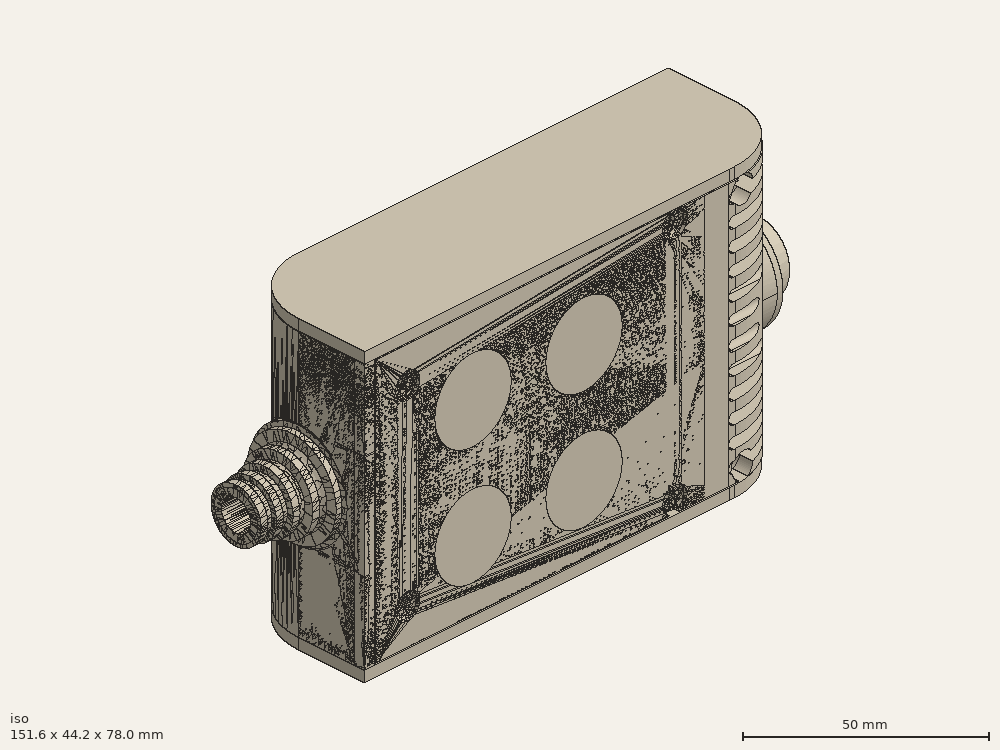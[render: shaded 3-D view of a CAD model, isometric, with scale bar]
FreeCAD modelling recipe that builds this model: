
FCSTD DOCUMENT  (FreeCAD 0.19R0.19.2)
Label: enclosure_191FCStd
License: All rights reserved
LicenseURL: http://en.wikipedia.org/wiki/All_rights_reserved
objects: Part::Revolution×152, Part::MultiFuse×146, Part::Feature×146, Sketcher::SketchObject×84, Part::Cut×70, Part::Cylinder×70, Part::Extrusion×67, Part::Fillet×58, Part::Box×36, App::MeasureDistance×4, PartDesign::Body×2, Image::ImagePlane×1
note: 831 computed .brp shape members not serialized (recipe doc carries the construction recipe); baked Part::Feature solids carry a one-line shape summary decoded from their .brp

FEATURE [Sketcher::SketchObject] Sketch  label="topSketch"
  FullyConstrained = true
  sketch-geometry (20):
    g0: LineSegment StartX=5.21097e-06 StartY=3 StartZ=0 EndX=5.21097e-06 EndY=19 EndZ=0
    g1: ArcOfCircle CenterX=19 CenterY=19 CenterZ=0 NormalX=0 NormalY=0 NormalZ=1 AngleXU=0 Radius=19 StartAngle=1.5708 EndAngle=3.14159
    g2: ArcOfCircle CenterX=19 CenterY=19 CenterZ=0 NormalX=0 NormalY=0 NormalZ=1 AngleXU=0 Radius=16 StartAngle=1.5708 EndAngle=3.14159
    g3: LineSegment StartX=114 StartY=35 StartZ=0 EndX=19 EndY=35 EndZ=0
    g4: LineSegment StartX=5.21097e-06 StartY=3 StartZ=0 EndX=5.21097e-06 EndY=0 EndZ=0
    g5: LineSegment StartX=3 StartY=0 StartZ=0 EndX=5.21097e-06 EndY=0 EndZ=0
    g6: LineSegment StartX=3 StartY=19 StartZ=0 EndX=3 EndY=0 EndZ=0
    g7: LineSegment StartX=19 StartY=38 StartZ=0 EndX=124 EndY=38 EndZ=0
    g8: Circle CenterX=119 CenterY=35 CenterZ=0 NormalX=0 NormalY=0 NormalZ=1 AngleXU=0 Radius=1
    g9: Circle CenterX=121 CenterY=35 CenterZ=0 NormalX=0 NormalY=0 NormalZ=1 AngleXU=0 Radius=1
    g10: Circle CenterX=121 CenterY=33 CenterZ=0 NormalX=0 NormalY=0 NormalZ=1 AngleXU=0 Radius=1
    g11: BSplineCurve PolesCount=3 KnotsCount=2 Degree=2 IsPeriodic=0
    g12: GeomPoint X=119 Y=35 Z=0
    g13: GeomPoint X=121 Y=33 Z=0
    g14: LineSegment StartX=119 StartY=35 StartZ=0 EndX=114 EndY=35 EndZ=0
    g15: ArcOfCircle CenterX=105 CenterY=19 CenterZ=0 NormalX=0 NormalY=0 NormalZ=1 AngleXU=0 Radius=19 StartAngle=5.7297 EndAngle=6.28319
    g16: ArcOfCircle CenterX=105 CenterY=19 CenterZ=0 NormalX=0 NormalY=0 NormalZ=1 AngleXU=0 Radius=16 StartAngle=5.60905 EndAngle=6.28319
    g17: LineSegment StartX=121 StartY=33 StartZ=0 EndX=121 EndY=19 EndZ=0
    g18: LineSegment StartX=124 StartY=38 StartZ=0 EndX=124 EndY=19 EndZ=0
    g19: LineSegment StartX=117.5 StartY=9.01251 StartZ=0 EndX=121.163 EndY=9.0125 EndZ=0
  constraints (46):
    c: Vertical(g0)
    c: Block(g0)
    c: Coincident(g1,g0)
    c: Block(g1)
    c: Coincident(g2,g1)
    c: Block(g2)
    c: Coincident(g3,g2)
    c: Horizontal(g3)
    c: Tangent(g3,g2)
    c: Coincident(g4,g0)
    c: Distance(g4) = 3
    c: Vertical(g4)
    c: Coincident(g5,g4)
    c: Horizontal(g5)
    c: Coincident(g6,g2)
    c: Coincident(g6,g5)
    c: Vertical(g6)
    c: Horizontal(g7)
    c: Distance(g7) = 105
    c: Coincident(g7,g1)
    c: Block(g3)
    c: Weight(g8) = 1
    c: Equal(g8,g9)
    c: Equal(g8,g10)
    c: InternalAlignment(g8,g11)
    c: InternalAlignment(g9,g11)
    c: InternalAlignment(g10,g11)
    c: InternalAlignment(g12,g11)
    c: InternalAlignment(g13,g11)
    c: Block(g11)
    c: Coincident(g14,g11)
    c: Coincident(g14,g3)
    c: Horizontal(g14)
    c: Block(g15)
    c: Coincident(g16,g15)
    c: Block(g16)
    c: Coincident(g17,g11)
    c: Coincident(g17,g16)
    c: Vertical(g17)
    c: Distance(g17) = 14
    c: Coincident(g18,g7)
    c: Coincident(g18,g15)
    c: Vertical(g18)
    c: Distance(g18) = 19
    c: Coincident(g19,g16)
    c: Coincident(g19,g15)
FEATURE [Sketcher::SketchObject] Sketch001  label="bottomSketch"
  FullyConstrained = true
  sketch-geometry (32):
    g0: LineSegment StartX=3.3 StartY=-6.03275e-07 StartZ=0 EndX=98 EndY=-6.03275e-07 EndZ=0
    g1: ArcOfCircle CenterX=98 CenterY=19 CenterZ=0 NormalX=0 NormalY=0 NormalZ=1 AngleXU=0 Radius=19 StartAngle=4.71239 EndAngle=5.71103
    g2: LineSegment StartX=6.3 StartY=8 StartZ=0 EndX=3.3 EndY=8 EndZ=0
    g3: LineSegment StartX=3.3 StartY=8 StartZ=0 EndX=3.3 EndY=-6.03275e-07 EndZ=0
    g4: ArcOfCircle CenterX=8.3 CenterY=5 CenterZ=0 NormalX=0 NormalY=0 NormalZ=1 AngleXU=0 Radius=2 StartAngle=3.14159 EndAngle=4.71239
    g5: LineSegment StartX=6.3 StartY=8 StartZ=0 EndX=6.3 EndY=5 EndZ=0
    g6: ArcOfCircle CenterX=98 CenterY=19 CenterZ=0 NormalX=0 NormalY=0 NormalZ=1 AngleXU=0 Radius=12.7 StartAngle=4.71239 EndAngle=6.28319
    g7: LineSegment StartX=94.7 StartY=3 StartZ=0 EndX=8.3 EndY=3 EndZ=0
    g8-g12: Circle x5 (B-spline internal-alignment scaffolding for g13; pole/knot coordinates omitted)
    g13: BSplineCurve PolesCount=5 KnotsCount=3 Degree=3 IsPeriodic=0
    g14: GeomPoint X=98 Y=6.3 Z=0
    g15: GeomPoint X=96.3938 Y=4.71946 Z=0
    g16: GeomPoint X=94.7 Y=3 Z=0
    g17-g23: Circle x7 (B-spline internal-alignment scaffolding for g24; pole/knot coordinates omitted)
    g24: BSplineCurve PolesCount=7 KnotsCount=5 Degree=3 IsPeriodic=0
    g25-g29: GeomPoint x5 (B-spline internal-alignment scaffolding for g24; pole/knot coordinates omitted)
    g30: ArcOfCircle CenterX=98 CenterY=19 CenterZ=0 NormalX=0 NormalY=0 NormalZ=1 AngleXU=0 Radius=15.7 StartAngle=5.81226 EndAngle=6.28319
    g31: LineSegment StartX=110.7 StartY=19 StartZ=0 EndX=113.7 EndY=19 EndZ=0
  constraints (41):
    c: Horizontal(g0)
    c: Coincident(g1,g0)
    c: Block(g1)
    c: Horizontal(g2)
    c: Distance(g2) = 3
    c: Coincident(g3,g2)
    c: Vertical(g3)
    c: Coincident(g3,g0)
    c: Block(g4)
    c: Block(g2)
    c: Coincident(g5,g2)
    c: Coincident(g5,g4)
    c: Vertical(g5)
    c: Coincident(g6,g1)
    c: Block(g6)
    c: Coincident(g7,g4)
    c: Horizontal(g7)
    c: Block(g0)
    c: Block(g7)
    c: Block(g3)
    c: Coincident(g13,g6)
    c: Weight(g8) = 1
    c: Equal(g8, g9-g12) x4
    c: Coincident(g13,g7)
    c: InternalAlignment(g8-g12 -> g13) x5
    c: InternalAlignment(g14,g13)
    c: InternalAlignment(g15,g13)
    c: InternalAlignment(g16,g13)
    c: Block(g13)
    c: Weight(g17) = 1
    c: Equal(g17, g18-g23) x6
    c: Coincident(g24,g1)
    c: InternalAlignment(g17-g23 -> g24) x7
    c: InternalAlignment(g25-g29 -> g24) x5
    c: Block(g24)
    c: Coincident(g30,g24)
    c: Coincident(g31,g6)
    c: Coincident(g31,g30)
    c: Horizontal(g31)
    c: Block(g31)
    c: Block(g30)
FEATURE [Part::Extrusion] Extrude  label="top"
  Base = -> Sketch
  Dir = (0,0,1)
  DirMode = 2
  FaceMakerClass = Part::FaceMakerBullseye
  LengthFwd = 72
  LengthRev = 0
  Solid = true
  Symmetric = false
FEATURE [Part::Extrusion] Extrude001  label="bottom"
  Base = -> Sketch001
  Dir = (0,0,1)
  DirMode = 2
  FaceMakerClass = Part::FaceMakerBullseye
  LengthFwd = 71.4
  LengthRev = 0
  Placement = pos=(0,0,0.3) rot=(0,0,1;0rad)
  Solid = true
  Symmetric = false
FEATURE [Sketcher::SketchObject] Sketch002  label="topSketch001"
  FullyConstrained = true
  sketch-geometry (8):
    g0: ArcOfCircle CenterX=19 CenterY=19.0975 CenterZ=0 NormalX=0 NormalY=0 NormalZ=1 AngleXU=0 Radius=18.9025 StartAngle=1.5708 EndAngle=3.14674
    g1: LineSegment StartX=0.0977805 StartY=19.0003 StartZ=0 EndX=0.0977805 EndY=0.000251602 EndZ=0
    g2: LineSegment StartX=19 StartY=38 StartZ=0 EndX=124 EndY=38 EndZ=0
    g3: LineSegment StartX=0.0977805 StartY=0.000251602 StartZ=0 EndX=105.098 EndY=0.000251602 EndZ=0
    g4: LineSegment StartX=124 StartY=38 StartZ=0 EndX=125.616 EndY=38 EndZ=0
    g5: LineSegment StartX=105.098 StartY=0.000251602 StartZ=0 EndX=106.713 EndY=0.000251602 EndZ=0
    g6: ArcOfCircle CenterX=106.616 CenterY=19 CenterZ=0 NormalX=0 NormalY=0 NormalZ=1 AngleXU=0 Radius=19 StartAngle=4.71754 EndAngle=6.28319
    g7: LineSegment StartX=125.616 StartY=38 StartZ=0 EndX=125.616 EndY=19 EndZ=0
  constraints (21):
    c: Block(g0)
    c: Coincident(g1,g0)
    c: Vertical(g1)
    c: Horizontal(g2)
    c: Distance(g2) = 105
    c: Coincident(g2,g0)
    c: Distance(g1) = 19
    c: Coincident(g3,g1)
    c: Horizontal(g3)
    c: Distance(g3) = 105
    c: Coincident(g4,g2)
    c: Horizontal(g4)
    c: Distance(g4) = 1.61553
    c: Horizontal(g5)
    c: Equal(g4,g5) = 1.61553
    c: Coincident(g5,g3)
    c: Block(g6)
    c: Coincident(g6,g5)
    c: Coincident(g7,g4)
    c: Coincident(g7,g6)
    c: Vertical(g7)
FEATURE [Part::Extrusion] Extrude002  label="sideA"
  Base = -> Sketch002
  Dir = (0,0,1)
  DirMode = 2
  FaceMakerClass = Part::FaceMakerBullseye
  LengthFwd = 3
  LengthRev = 0
  Placement = pos=(0,0,-3) rot=(0,0,1;0rad)
  Solid = true
  Symmetric = false
FEATURE [Sketcher::SketchObject] Sketch003  label="topSketch002"
  FullyConstrained = true
  sketch-geometry (6):
    g0: LineSegment StartX=19 StartY=38 StartZ=0 EndX=117 EndY=38 EndZ=0
    g1: ArcOfCircle CenterX=19 CenterY=19 CenterZ=0 NormalX=0 NormalY=0 NormalZ=1 AngleXU=0 Radius=19 StartAngle=1.5708 EndAngle=3.14159
    g2: LineSegment StartX=117 StartY=38 StartZ=0 EndX=117 EndY=19 EndZ=0
    g3: LineSegment StartX=98 StartY=1.0161e-12 StartZ=0 EndX=5.22862e-06 EndY=1.0161e-12 EndZ=0
    g4: LineSegment StartX=5.22862e-06 StartY=19 StartZ=0 EndX=5.22862e-06 EndY=1.0161e-12 EndZ=0
    g5: ArcOfCircle CenterX=98 CenterY=19 CenterZ=0 NormalX=0 NormalY=0 NormalZ=1 AngleXU=0 Radius=19 StartAngle=4.71239 EndAngle=6.28319
  constraints (16):
    c: Horizontal(g0)
    c: Distance(g0) = 98
    c: Coincident(g1,g0)
    c: Block(g1)
    c: Coincident(g2,g0)
    c: Vertical(g2)
    c: Distance(g2) = 19
    c: Horizontal(g3)
    c: Coincident(g4,g1)
    c: Vertical(g4)
    c: Coincident(g3,g4)
    c: Block(g3)
    c: Coincident(g5,g2)
    c: Coincident(g5,g3)
    c: Block(g0)
    c: Block(g5)
FEATURE [Sketcher::SketchObject] Sketch004
  FullyConstrained = true
  MapMode = 3
  Placement = pos=(0,0,0) rot=(1,0,0;1.5708rad)
  Support = -> [Extrude]
  sketch-geometry (8):
    g0: Circle CenterX=80.351 CenterY=-67.6202 CenterZ=0 NormalX=0 NormalY=0 NormalZ=1 AngleXU=0 Radius=2
    g1: Circle CenterX=80.351 CenterY=-67.6202 CenterZ=0 NormalX=0 NormalY=0 NormalZ=1 AngleXU=0 Radius=3
    g2: Circle CenterX=80.351 CenterY=-4.92017 CenterZ=0 NormalX=0 NormalY=0 NormalZ=1 AngleXU=0 Radius=2
    g3: Circle CenterX=80.351 CenterY=-4.92017 CenterZ=0 NormalX=0 NormalY=0 NormalZ=1 AngleXU=0 Radius=3
    g4: Circle CenterX=23.851 CenterY=-4.92017 CenterZ=0 NormalX=0 NormalY=0 NormalZ=1 AngleXU=0 Radius=2
    g5: Circle CenterX=23.851 CenterY=-4.92017 CenterZ=0 NormalX=0 NormalY=0 NormalZ=1 AngleXU=0 Radius=3
    g6: Circle CenterX=23.851 CenterY=-67.6202 CenterZ=0 NormalX=0 NormalY=0 NormalZ=1 AngleXU=0 Radius=2
    g7: Circle CenterX=23.851 CenterY=-67.6202 CenterZ=0 NormalX=0 NormalY=0 NormalZ=1 AngleXU=0 Radius=3
  constraints (8):
    c: Block(g3)
    c: Block(g2)
    c: Block(g1)
    c: Block(g0)
    c: Block(g6)
    c: Block(g7)
    c: Block(g4)
    c: Block(g5)
FEATURE [Part::Extrusion] Extrude004
  Base = -> Sketch004
  Dir = (0,-1,2e-16)
  DirMode = 2
  FaceMakerClass = Part::FaceMakerBullseye
  LengthFwd = 6
  LengthRev = 0
  Placement = pos=(0,9,0) rot=(0,0,1;0rad)
  Solid = true
  Symmetric = false
FEATURE [Sketcher::SketchObject] Sketch005
  FullyConstrained = true
  MapMode = 3
  Placement = pos=(0,0,0) rot=(1,0,0;1.5708rad)
  Support = -> [Extrude]
  sketch-geometry (8):
    g0: Circle CenterX=80.351 CenterY=-67.6202 CenterZ=0 NormalX=0 NormalY=0 NormalZ=1 AngleXU=0 Radius=3
    g1: Circle CenterX=80.351 CenterY=-4.92017 CenterZ=0 NormalX=0 NormalY=0 NormalZ=1 AngleXU=0 Radius=3
    g2: Circle CenterX=23.851 CenterY=-4.92017 CenterZ=0 NormalX=0 NormalY=0 NormalZ=1 AngleXU=0 Radius=3
    g3: Circle CenterX=23.851 CenterY=-67.6202 CenterZ=0 NormalX=0 NormalY=0 NormalZ=1 AngleXU=0 Radius=3
    g4: Circle CenterX=23.851 CenterY=-67.6202 CenterZ=0 NormalX=0 NormalY=0 NormalZ=1 AngleXU=0 Radius=5
    g5: Circle CenterX=80.351 CenterY=-67.6202 CenterZ=0 NormalX=0 NormalY=0 NormalZ=1 AngleXU=0 Radius=5
    g6: Circle CenterX=23.851 CenterY=-4.92017 CenterZ=0 NormalX=0 NormalY=0 NormalZ=1 AngleXU=0 Radius=5
    g7: Circle CenterX=80.351 CenterY=-4.92017 CenterZ=0 NormalX=0 NormalY=0 NormalZ=1 AngleXU=0 Radius=5
  constraints (8):
    c: Block(g1)
    c: Block(g0)
    c: Block(g3)
    c: Block(g2)
    c: Block(g5)
    c: Block(g4)
    c: Block(g6)
    c: Block(g7)
FEATURE [Part::Extrusion] Extrude005
  Base = -> Sketch005
  Dir = (0,-1,2e-16)
  DirMode = 2
  FaceMakerClass = Part::FaceMakerBullseye
  LengthFwd = 2
  LengthRev = 0
  Solid = true
  Symmetric = false
FEATURE [Sketcher::SketchObject] Sketch006
  FullyConstrained = true
  MapMode = 3
  Placement = pos=(0,0,0) rot=(1,0,0;1.5708rad)
  sketch-geometry (8):
    g0: Circle CenterX=80.351 CenterY=-67.6202 CenterZ=0 NormalX=0 NormalY=0 NormalZ=1 AngleXU=0 Radius=3
    g1: Circle CenterX=80.351 CenterY=-4.92017 CenterZ=0 NormalX=0 NormalY=0 NormalZ=1 AngleXU=0 Radius=3
    g2: Circle CenterX=23.851 CenterY=-4.92017 CenterZ=0 NormalX=0 NormalY=0 NormalZ=1 AngleXU=0 Radius=3
    g3: Circle CenterX=23.851 CenterY=-67.6202 CenterZ=0 NormalX=0 NormalY=0 NormalZ=1 AngleXU=0 Radius=3
    g4: Circle CenterX=23.851 CenterY=-67.6202 CenterZ=0 NormalX=0 NormalY=0 NormalZ=1 AngleXU=0 Radius=5
    g5: Circle CenterX=80.351 CenterY=-67.6202 CenterZ=0 NormalX=0 NormalY=0 NormalZ=1 AngleXU=0 Radius=5
    g6: Circle CenterX=23.851 CenterY=-4.92017 CenterZ=0 NormalX=0 NormalY=0 NormalZ=1 AngleXU=0 Radius=5
    g7: Circle CenterX=80.351 CenterY=-4.92017 CenterZ=0 NormalX=0 NormalY=0 NormalZ=1 AngleXU=0 Radius=5
  constraints (8):
    c: Block(g1)
    c: Block(g0)
    c: Block(g3)
    c: Block(g2)
    c: Block(g5)
    c: Block(g4)
    c: Block(g6)
    c: Block(g7)
FEATURE [Part::Extrusion] Extrude007
  Base = -> Sketch006
  Dir = (0,-1,2e-16)
  DirMode = 2
  FaceMakerClass = Part::FaceMakerBullseye
  LengthFwd = 2
  LengthRev = 0
  Solid = true
  Symmetric = false
FEATURE [Part::Fillet] Fillet
  Base = -> Extrude007
  Edges = 4 edges r=1.99: [Edge6,Edge12,Edge18,Edge24]
FEATURE [Part::Cut] Cut
  Base = -> Extrude005
  Placement = pos=(0,5,0) rot=(0,0,1;0rad)
  Tool = -> Fillet
FEATURE [Part::MultiFuse] Fusion  label="pCBScrews"
  Placement = pos=(-2.5,0,72.3) rot=(0,0,1;0rad)
  Shapes = -> [Extrude004,Cut]
FEATURE [App::MeasureDistance] Distance  label="Distance: 0.69 mm"
  Distance = 0.685967
  P1 = (24.0138,2.9647,0.3)
  P2 = (23.8901,3,-0.373787)
FEATURE [App::MeasureDistance] Distance001  label="Distance: 0.53 mm"
  Distance = 0.533607
  P1 = (80.2939,3,72.2334)
  P2 = (80.281,2.99661,71.7)
FEATURE [Part::Fillet] Fillet001
  Base = -> Extrude001
  Edges = 1 edges r=2.4: [Edge17]
FEATURE [Part::Fillet] Fillet002  label="bottom001"
  Base = -> Fillet001
  Edges = 1 edges r=2.4: [Edge36]
FEATURE [Part::Fillet] Fillet003  label="top001"
  Base = -> Extrude
  Edges = 1 edges r=2: [Edge1]
FEATURE [Sketcher::SketchObject] Sketch007
  FullyConstrained = true
  sketch-geometry (16):
    g0: LineSegment StartX=4 StartY=0 StartZ=0 EndX=4 EndY=2.4 EndZ=0
    g1: LineSegment StartX=4 StartY=2.4 StartZ=0 EndX=7 EndY=2.4 EndZ=0
    g2: LineSegment StartX=4 StartY=0 StartZ=0 EndX=5.7 EndY=0 EndZ=0
    g3: LineSegment StartX=5.7 StartY=0 StartZ=0 EndX=5.7 EndY=-5.6 EndZ=0
    g4-g8: Circle x5 (B-spline internal-alignment scaffolding for g9; pole/knot coordinates omitted)
    g9: BSplineCurve PolesCount=5 KnotsCount=3 Degree=3 IsPeriodic=0
    g10: GeomPoint X=7 Y=2.4 Z=0
    g11: GeomPoint X=10.4582 Y=-1.55472 Z=0
    g12: GeomPoint X=14 Y=-5.6 Z=0
    g13: LineSegment StartX=14 StartY=-5.6 StartZ=0 EndX=14 EndY=-14.1 EndZ=0
    g14: LineSegment StartX=14 StartY=-14.1 StartZ=0 EndX=6.5 EndY=-14.1 EndZ=0
    g15: LineSegment StartX=5.7 StartY=-5.6 StartZ=0 EndX=6.5 EndY=-14.1 EndZ=0
  constraints (28):
    c: Distance(g0) = 2.4
    c: Vertical(g0)
    c: Block(g0)
    c: Coincident(g1,g0)
    c: Horizontal(g1)
    c: Distance(g1) = 3
    c: Coincident(g2,g0)
    c: Horizontal(g2)
    c: Distance(g2) = 1.7
    c: Coincident(g3,g2)
    c: Vertical(g3)
    c: Distance(g3) = 5.6
    c: Coincident(g9,g1)
    c: Weight(g4) = 1
    c: Equal(g4, g5-g8) x4
    c: InternalAlignment(g4-g8 -> g9) x5
    c: InternalAlignment(g10,g9)
    c: InternalAlignment(g11,g9)
    c: InternalAlignment(g12,g9)
    c: Block(g9)
    c: Coincident(g13,g9)
    c: Vertical(g13)
    c: Distance(g13) = 8.5
    c: Coincident(g14,g13)
    c: Horizontal(g14)
    c: Distance(g14) = 7.5
    c: Coincident(g15,g3)
    c: Coincident(g15,g14)
FEATURE [Part::Feature] Face
  shape: bbox 10 x 16.5 x 2e-07 mm, 1 faces, 0 solids (baked)
FEATURE [Part::Revolution] Revolve  label="plugHousing"
  Angle = 360
  Axis = (0,1,0)
  Base = (0,0,0)
  FaceMakerClass = Part::FaceMakerBullseye
  Placement = pos=(0,0,36.15) rot=(0,0,1;0rad)
  Solid = false
  Source = -> Face
  Symmetric = false
FEATURE [Part::Feature] Face001
  shape: bbox 10 x 16.5 x 2e-07 mm, 1 faces, 0 solids (baked)
FEATURE [Part::Revolution] Revolve001  label="plugHousing001"
  Angle = 360
  Axis = (0,1,0)
  Base = (0,0,0)
  FaceMakerClass = Part::FaceMakerBullseye
  Placement = pos=(0,0,36.15) rot=(0,0,1;0rad)
  Solid = false
  Source = -> Face001
  Symmetric = false
FEATURE [Part::MultiFuse] Fusion001  label="plugHousing002"
  Placement = pos=(0,0,0) rot=(0,0,1;1.5708rad)
  Shapes = -> [Revolve001,Revolve]
FEATURE [Part::Feature] Face002
  shape: bbox 10 x 16.5 x 2e-07 mm, 1 faces, 0 solids (baked)
FEATURE [Part::Revolution] Revolve003  label="plugHousing005"
  Angle = 360
  Axis = (0,1,0)
  Base = (0,0,0)
  FaceMakerClass = Part::FaceMakerBullseye
  Placement = pos=(0,0,36.15) rot=(0,0,1;0rad)
  Solid = false
  Source = -> Face002
  Symmetric = false
FEATURE [Part::Feature] Face003
  shape: bbox 10 x 16.5 x 2e-07 mm, 1 faces, 0 solids (baked)
FEATURE [Part::Revolution] Revolve002  label="plugHousing003"
  Angle = 360
  Axis = (0,1,0)
  Base = (0,0,0)
  FaceMakerClass = Part::FaceMakerBullseye
  Placement = pos=(0,0,36.15) rot=(0,0,1;0rad)
  Solid = false
  Source = -> Face003
  Symmetric = false
FEATURE [Part::MultiFuse] Fusion002  label="plugHousing004"
  Placement = pos=(0,0,0) rot=(0,0,1;1.5708rad)
  Shapes = -> [Revolve002,Revolve003]
FEATURE [Part::MultiFuse] Fusion003  label="plugHousing006"
  Placement = pos=(0,19,0) rot=(0,0,1;3.14159rad)
  Shapes = -> [Fusion002,Fusion001]
FEATURE [Part::Feature] Face004
  shape: bbox 10 x 16.5 x 2e-07 mm, 1 faces, 0 solids (baked)
FEATURE [Part::Revolution] Revolve006  label="plugHousing010"
  Angle = 360
  Axis = (0,1,0)
  Base = (0,0,0)
  FaceMakerClass = Part::FaceMakerBullseye
  Placement = pos=(0,0,36.15) rot=(0,0,1;0rad)
  Solid = false
  Source = -> Face004
  Symmetric = false
FEATURE [Part::Feature] Face005
  shape: bbox 10 x 16.5 x 2e-07 mm, 1 faces, 0 solids (baked)
FEATURE [Part::Revolution] Revolve007  label="plugHousing011"
  Angle = 360
  Axis = (0,1,0)
  Base = (0,0,0)
  FaceMakerClass = Part::FaceMakerBullseye
  Placement = pos=(0,0,36.15) rot=(0,0,1;0rad)
  Solid = false
  Source = -> Face005
  Symmetric = false
FEATURE [Part::Feature] Face006
  shape: bbox 10 x 16.5 x 2e-07 mm, 1 faces, 0 solids (baked)
FEATURE [Part::Revolution] Revolve004  label="plugHousing007"
  Angle = 360
  Axis = (0,1,0)
  Base = (0,0,0)
  FaceMakerClass = Part::FaceMakerBullseye
  Placement = pos=(0,0,36.15) rot=(0,0,1;0rad)
  Solid = false
  Source = -> Face006
  Symmetric = false
FEATURE [Part::MultiFuse] Fusion004  label="plugHousing009"
  Placement = pos=(0,0,0) rot=(0,0,1;1.5708rad)
  Shapes = -> [Revolve004,Revolve007]
FEATURE [Part::Feature] Face007
  shape: bbox 10 x 16.5 x 2e-07 mm, 1 faces, 0 solids (baked)
FEATURE [Part::Revolution] Revolve005  label="plugHousing008"
  Angle = 360
  Axis = (0,1,0)
  Base = (0,0,0)
  FaceMakerClass = Part::FaceMakerBullseye
  Placement = pos=(0,0,36.15) rot=(0,0,1;0rad)
  Solid = false
  Source = -> Face007
  Symmetric = false
FEATURE [Part::MultiFuse] Fusion005  label="plugHousing012"
  Placement = pos=(0,0,0) rot=(0,0,1;1.5708rad)
  Shapes = -> [Revolve006,Revolve005]
FEATURE [Part::MultiFuse] Fusion006  label="plugHousing013"
  Placement = pos=(0,19,0) rot=(0,0,1;3.14159rad)
  Shapes = -> [Fusion005,Fusion004]
FEATURE [Part::MultiFuse] Fusion007  label="plugHousing014"
  Placement = pos=(122.621,0,-0.15) rot=(0,0,1;0rad)
  Shapes = -> [Fusion003,Fusion006]
FEATURE [Part::Cylinder] Cylinder002
  Angle = 360
  AttacherType = Attacher::AttachEngine3D
  Height = 20
  Placement = pos=(0,0,36.15) rot=(0,0,1;0rad)
  Radius = 4
FEATURE [Part::Cylinder] Cylinder003
  Angle = 360
  AttacherType = Attacher::AttachEngine3D
  Height = 10
  Placement = pos=(0,0,36.15) rot=(0,0,1;0rad)
  Radius = 4
FEATURE [Part::MultiFuse] Fusion009  label="removeToCreateHoleForPlugHousing"
  Placement = pos=(70,19,36.15) rot=(0,1,0;1.5708rad)
  Shapes = -> [Cylinder002,Cylinder003]
FEATURE [Part::Cylinder] Cylinder004
  Angle = 360
  AttacherType = Attacher::AttachEngine3D
  Height = 20
  Placement = pos=(0,0,36.15) rot=(0,0,1;0rad)
  Radius = 4
FEATURE [Part::Cylinder] Cylinder005
  Angle = 360
  AttacherType = Attacher::AttachEngine3D
  Height = 10
  Placement = pos=(0,0,36.15) rot=(0,0,1;0rad)
  Radius = 4
FEATURE [Part::MultiFuse] Fusion010  label="removeToCreateHoleForPlugHousing001"
  Placement = pos=(70,19,36.15) rot=(0,1,0;1.5708rad)
  Shapes = -> [Cylinder004,Cylinder005]
FEATURE [Part::Cut] Cut001
  Base = -> Fillet003
  Tool = -> Fusion010
FEATURE [Part::Cut] Cut002  label="Bottom"
  Base = -> Fillet002
  Tool = -> Fusion009
FEATURE [Part::Feature] Face008
  shape: bbox 10 x 16.5 x 2e-07 mm, 1 faces, 0 solids (baked)
FEATURE [Part::Revolution] Revolve011  label="plugHousing021"
  Angle = 360
  Axis = (0,1,0)
  Base = (0,0,0)
  FaceMakerClass = Part::FaceMakerBullseye
  Placement = pos=(0,0,36.15) rot=(0,0,1;0rad)
  Solid = false
  Source = -> Face008
  Symmetric = false
FEATURE [Part::Feature] Face009
  shape: bbox 10 x 16.5 x 2e-07 mm, 1 faces, 0 solids (baked)
FEATURE [Part::Revolution] Revolve012  label="plugHousing022"
  Angle = 360
  Axis = (0,1,0)
  Base = (0,0,0)
  FaceMakerClass = Part::FaceMakerBullseye
  Placement = pos=(0,0,36.15) rot=(0,0,1;0rad)
  Solid = false
  Source = -> Face009
  Symmetric = false
FEATURE [Part::Feature] Face010 .. Face013  x4 (patterned run collapsed; names and placements below)
  shape: bbox 10 x 16.5 x 2e-07 mm, 1 faces, 0 solids (baked)
FEATURE [Part::Revolution] Revolve015  label="plugHousing027"
  Angle = 360
  Axis = (0,1,0)
  Base = (0,0,0)
  FaceMakerClass = Part::FaceMakerBullseye
  Placement = pos=(0,0,36.15) rot=(0,0,1;0rad)
  Solid = false
  Source = -> Face013
  Symmetric = false
FEATURE [Part::Feature] Face014
  shape: bbox 10 x 16.5 x 2e-07 mm, 1 faces, 0 solids (baked)
FEATURE [Part::Feature] Face015
  shape: bbox 10 x 16.5 x 2e-07 mm, 1 faces, 0 solids (baked)
FEATURE [Part::Feature] Face016
  shape: bbox 10 x 16.5 x 2e-07 mm, 1 faces, 0 solids (baked)
FEATURE [Part::Revolution] Revolve019  label="plugHousing033"
  Angle = 360
  Axis = (0,1,0)
  Base = (0,0,0)
  FaceMakerClass = Part::FaceMakerBullseye
  Placement = pos=(0,0,36.15) rot=(0,0,1;0rad)
  Solid = false
  Source = -> Face016
  Symmetric = false
FEATURE [Part::Feature] Face017
  shape: bbox 10 x 16.5 x 2e-07 mm, 1 faces, 0 solids (baked)
FEATURE [Part::Revolution] Revolve020  label="plugHousing034"
  Angle = 360
  Axis = (0,1,0)
  Base = (0,0,0)
  FaceMakerClass = Part::FaceMakerBullseye
  Placement = pos=(0,0,36.15) rot=(0,0,1;0rad)
  Solid = false
  Source = -> Face017
  Symmetric = false
FEATURE [Part::Feature] Face018
  shape: bbox 10 x 16.5 x 2e-07 mm, 1 faces, 0 solids (baked)
FEATURE [Part::Revolution] Revolve016  label="plugHousing030"
  Angle = 360
  Axis = (0,1,0)
  Base = (0,0,0)
  FaceMakerClass = Part::FaceMakerBullseye
  Placement = pos=(0,0,36.15) rot=(0,0,1;0rad)
  Solid = false
  Source = -> Face018
  Symmetric = false
FEATURE [Part::MultiFuse] Fusion020  label="plugHousing038"
  Placement = pos=(0,0,0) rot=(0,0,1;1.5708rad)
  Shapes = -> [Revolve016,Revolve020]
FEATURE [Part::Feature] Face019
  shape: bbox 10 x 16.5 x 2e-07 mm, 1 faces, 0 solids (baked)
FEATURE [Part::Feature] Face020
  shape: bbox 10 x 16.5 x 2e-07 mm, 1 faces, 0 solids (baked)
FEATURE [Part::Revolution] Revolve017  label="plugHousing031"
  Angle = 360
  Axis = (0,1,0)
  Base = (0,0,0)
  FaceMakerClass = Part::FaceMakerBullseye
  Placement = pos=(0,0,36.15) rot=(0,0,1;0rad)
  Solid = false
  Source = -> Face020
  Symmetric = false
FEATURE [Part::MultiFuse] Fusion021  label="plugHousing039"
  Placement = pos=(0,0,0) rot=(0,0,1;1.5708rad)
  Shapes = -> [Revolve019,Revolve017]
FEATURE [Part::MultiFuse] Fusion023  label="plugHousing041"
  Placement = pos=(0,19,0) rot=(0,0,1;3.14159rad)
  Shapes = -> [Fusion021,Fusion020]
FEATURE [Part::Revolution] Revolve022  label="plugHousing043"
  Angle = 360
  Axis = (0,1,0)
  Base = (0,0,0)
  FaceMakerClass = Part::FaceMakerBullseye
  Placement = pos=(0,0,36.15) rot=(0,0,1;0rad)
  Solid = false
  Source = -> Face019
  Symmetric = false
FEATURE [Part::Feature] Face021
  shape: bbox 10 x 16.5 x 2e-07 mm, 1 faces, 0 solids (baked)
FEATURE [Part::Revolution] Revolve023  label="plugHousing044"
  Angle = 360
  Axis = (0,1,0)
  Base = (0,0,0)
  FaceMakerClass = Part::FaceMakerBullseye
  Placement = pos=(0,0,36.15) rot=(0,0,1;0rad)
  Solid = false
  Source = -> Face021
  Symmetric = false
FEATURE [Part::Feature] Face022
  shape: bbox 10 x 16.5 x 2e-07 mm, 1 faces, 0 solids (baked)
FEATURE [Part::Revolution] Revolve018  label="plugHousing032"
  Angle = 360
  Axis = (0,1,0)
  Base = (0,0,0)
  FaceMakerClass = Part::FaceMakerBullseye
  Placement = pos=(0,0,36.15) rot=(0,0,1;0rad)
  Solid = false
  Source = -> Face022
  Symmetric = false
FEATURE [Part::MultiFuse] Fusion022  label="plugHousing040"
  Placement = pos=(0,0,0) rot=(0,0,1;1.5708rad)
  Shapes = -> [Revolve018,Revolve023]
FEATURE [Part::Feature] Face023
  shape: bbox 10 x 16.5 x 2e-07 mm, 1 faces, 0 solids (baked)
FEATURE [Part::Revolution] Revolve021  label="plugHousing035"
  Angle = 360
  Axis = (0,1,0)
  Base = (0,0,0)
  FaceMakerClass = Part::FaceMakerBullseye
  Placement = pos=(0,0,36.15) rot=(0,0,1;0rad)
  Solid = false
  Source = -> Face023
  Symmetric = false
FEATURE [Part::MultiFuse] Fusion018  label="plugHousing036"
  Placement = pos=(0,0,0) rot=(0,0,1;1.5708rad)
  Shapes = -> [Revolve022,Revolve021]
FEATURE [Part::MultiFuse] Fusion019  label="plugHousing037"
  Placement = pos=(0,19,0) rot=(0,0,1;3.14159rad)
  Shapes = -> [Fusion018,Fusion022]
FEATURE [Part::MultiFuse] Fusion024  label="plugHousing042"
  Placement = pos=(122.621,0,-0.15) rot=(0,0,1;0rad)
  Shapes = -> [Fusion023,Fusion019]
FEATURE [Part::Cylinder] Cylinder006
  Angle = 360
  AttacherType = Attacher::AttachEngine3D
  Height = 20
  Placement = pos=(0,0,36.15) rot=(0,0,1;0rad)
  Radius = 14.3
FEATURE [Part::Cylinder] Cylinder007
  Angle = 360
  AttacherType = Attacher::AttachEngine3D
  Height = 10
  Placement = pos=(0,0,36.15) rot=(0,0,1;0rad)
  Radius = 4
FEATURE [Part::MultiFuse] Fusion026  label="removeToCreteHoleForPlugHousing"
  Placement = pos=(70,19,36) rot=(0,1,0;1.5708rad)
  Shapes = -> [Cylinder006,Cylinder007]
FEATURE [Part::Box] Box001  label="Cube001"
  AttacherType = Attacher::AttachEngine3D
  Height = 28
  Length = 3
  Placement = pos=(110.7,19,22) rot=(0,0,1;0rad)
  Width = 15.7
FEATURE [Part::Cut] Cut003  label="top002"
  Base = -> Cut001
  Tool = -> Fusion007
FEATURE [Part::Revolution] Revolve008  label="plugHousing015"
  Angle = 360
  Axis = (0,1,0)
  Base = (0,0,0)
  FaceMakerClass = Part::FaceMakerBullseye
  Placement = pos=(0,0,36.15) rot=(0,0,1;0rad)
  Solid = false
  Source = -> Face010
  Symmetric = false
FEATURE [Part::MultiFuse] Fusion013  label="plugHousing020"
  Placement = pos=(0,0,0) rot=(0,0,1;1.5708rad)
  Shapes = -> [Revolve008,Revolve012]
FEATURE [Part::Cut] Cut004  label="top003"
  Base = -> Cut003
  Placement = pos=(1,0,0) rot=(0,0,1;0rad)
  Tool = -> Fusion026
FEATURE [Part::Cylinder] Cylinder008
  Angle = 360
  AttacherType = Attacher::AttachEngine3D
  Height = 20
  Placement = pos=(0,0,36.15) rot=(0,0,1;0rad)
  Radius = 10.3
FEATURE [Part::Cylinder] Cylinder009
  Angle = 360
  AttacherType = Attacher::AttachEngine3D
  Height = 10
  Placement = pos=(0,0,36.15) rot=(0,0,1;0rad)
  Radius = 4
FEATURE [Part::MultiFuse] Fusion027  label="removeToCreteHoleForPlugHousing001"
  Placement = pos=(70,19,36) rot=(0,1,0;1.5708rad)
  Shapes = -> [Cylinder008,Cylinder009]
FEATURE [Part::Cut] Cut005  label="plugHousingTab"
  Base = -> Box001
  Tool = -> Fusion027
FEATURE [Part::MultiFuse] Fusion028  label="plugHousing045"
  Shapes = -> [Fusion024,Cut005]
FEATURE [Part::Box] Box002  label="Cube002"
  AttacherType = Attacher::AttachEngine3D
  Height = 28.8
  Length = 3
  Placement = pos=(107.3,28,21.6) rot=(0,0,1;0rad)
  Width = 7
FEATURE [Part::Box] Box003  label="Cube003"
  AttacherType = Attacher::AttachEngine3D
  Height = 3
  Length = 6.4
  Placement = pos=(107.3,28,18.6) rot=(0,0,1;0rad)
  Width = 7
FEATURE [Part::Box] Box004  label="Cube004"
  AttacherType = Attacher::AttachEngine3D
  Height = 3
  Length = 6.4
  Placement = pos=(107.3,28,50.4) rot=(0,0,1;0rad)
  Width = 7
FEATURE [Part::MultiFuse] Fusion029  label="plugHousingBracketHolder"
  Shapes = -> [Box004,Box002,Box003]
FEATURE [Part::Cylinder] Cylinder010
  Angle = 360
  AttacherType = Attacher::AttachEngine3D
  Height = 20
  Placement = pos=(0,0,36.15) rot=(0,0,1;0rad)
  Radius = 14.3
FEATURE [Part::Cylinder] Cylinder011
  Angle = 360
  AttacherType = Attacher::AttachEngine3D
  Height = 10
  Placement = pos=(0,0,36.15) rot=(0,0,1;0rad)
  Radius = 4
FEATURE [Part::MultiFuse] Fusion030  label="removeToCreteHoleForPlugHousing002"
  Placement = pos=(70,19,36) rot=(0,1,0;1.5708rad)
  Shapes = -> [Cylinder010,Cylinder011]
FEATURE [Part::Cut] Cut006  label="plugHousingBracketHolder001"
  Base = -> Fusion029
  Tool = -> Fusion030
FEATURE [Part::Cylinder] Cylinder012
  Angle = 360
  AttacherType = Attacher::AttachEngine3D
  Height = 20
  Placement = pos=(0,0,36.15) rot=(0,0,1;0rad)
  Radius = 7
FEATURE [Part::Cylinder] Cylinder013
  Angle = 360
  AttacherType = Attacher::AttachEngine3D
  Height = 10
  Placement = pos=(0,0,36.15) rot=(0,0,1;0rad)
  Radius = 4
FEATURE [Part::MultiFuse] Fusion032  label="removeToCreteHoleForPlugHousing003"
  Placement = pos=(70,19,36) rot=(0,1,0;1.5708rad)
  Shapes = -> [Cylinder012,Cylinder013]
FEATURE [Part::Cut] Cut007  label="bottom002"
  Base = -> Cut002
  Tool = -> Fusion032
FEATURE [Sketcher::SketchObject] Sketch008
  FullyConstrained = true
  sketch-geometry (54):
    g0: LineSegment StartX=-4.2 StartY=0 StartZ=0 EndX=-6.2 EndY=0 EndZ=0
    g1: LineSegment StartX=-14 StartY=-18 StartZ=0 EndX=-14 EndY=-26.5 EndZ=0
    g2: LineSegment StartX=-4.2 StartY=0 StartZ=0 EndX=-4.2 EndY=-13.4877 EndZ=0
    g3: Circle CenterX=-4.2 CenterY=-13.4877 CenterZ=0 NormalX=0 NormalY=0 NormalZ=1 AngleXU=0 Radius=1
    g4: Circle CenterX=-4.2 CenterY=-26.5 CenterZ=0 NormalX=0 NormalY=0 NormalZ=1 AngleXU=0 Radius=1
    g5: Circle CenterX=-8.2 CenterY=-26.5 CenterZ=0 NormalX=0 NormalY=0 NormalZ=1 AngleXU=0 Radius=1
    g6: BSplineCurve PolesCount=3 KnotsCount=2 Degree=2 IsPeriodic=0
    g7: GeomPoint X=-4.2 Y=-13.4877 Z=0
    g8: GeomPoint X=-8.2 Y=-26.5 Z=0
    g9: LineSegment StartX=-14 StartY=-26.5 StartZ=0 EndX=-8.2 EndY=-26.5 EndZ=0
    g10: LineSegment StartX=-10.15 StartY=-12 StartZ=0 EndX=-10.15 EndY=-14 EndZ=0
    g11: LineSegment StartX=-12.8401 StartY=-16 StartZ=0 EndX=-10.1571 EndY=-16 EndZ=0
    g12: LineSegment StartX=-10.15 StartY=-14 StartZ=0 EndX=-8.70761 EndY=-14 EndZ=0
    g13: LineSegment StartX=-12.8401 StartY=-16 StartZ=0 EndX=-12.8401 EndY=-17.6958 EndZ=0
    g14: LineSegment StartX=-10.15 StartY=-12 StartZ=0 EndX=-7.79258 EndY=-12 EndZ=0
    g15: Circle CenterX=-6.2215 CenterY=-2 CenterZ=0 NormalX=0 NormalY=0 NormalZ=1 AngleXU=0 Radius=1
    g16: Circle CenterX=-6.22762 CenterY=-2.58724 CenterZ=0 NormalX=0 NormalY=0 NormalZ=1 AngleXU=0 Radius=1
    g17: Circle CenterX=-6.32538 CenterY=-4 CenterZ=0 NormalX=0 NormalY=0 NormalZ=1 AngleXU=0 Radius=1
    g18: BSplineCurve PolesCount=3 KnotsCount=2 Degree=2 IsPeriodic=0
    g19: GeomPoint X=-6.2215 Y=-2 Z=0
    g20: GeomPoint X=-6.32538 Y=-4 Z=0
    g21: Circle CenterX=-6.48644 CenterY=-5.99526 CenterZ=0 NormalX=0 NormalY=0 NormalZ=1 AngleXU=0 Radius=1
    g22: Circle CenterX=-6.58486 CenterY=-6.99526 CenterZ=0 NormalX=0 NormalY=0 NormalZ=1 AngleXU=0 Radius=1
    g23: Circle CenterX=-6.77343 CenterY=-8 CenterZ=0 NormalX=0 NormalY=0 NormalZ=1 AngleXU=0 Radius=1
    g24: BSplineCurve PolesCount=3 KnotsCount=2 Degree=2 IsPeriodic=0
    g25: GeomPoint X=-6.48644 Y=-5.99526 Z=0
    g26: GeomPoint X=-6.77343 Y=-8 Z=0
    g27: Circle CenterX=-7.19003 CenterY=-10 CenterZ=0 NormalX=0 NormalY=0 NormalZ=1 AngleXU=0 Radius=1
    g28: Circle CenterX=-7.44407 CenterY=-11.0915 CenterZ=0 NormalX=0 NormalY=0 NormalZ=1 AngleXU=0 Radius=1
    g29: Circle CenterX=-7.79258 CenterY=-12 CenterZ=0 NormalX=0 NormalY=0 NormalZ=1 AngleXU=0 Radius=1
    g30: BSplineCurve PolesCount=3 KnotsCount=2 Degree=2 IsPeriodic=0
    g31: GeomPoint X=-7.19003 Y=-10 Z=0
    g32: GeomPoint X=-7.79258 Y=-12 Z=0
    g33: Circle CenterX=-8.70761 CenterY=-14 CenterZ=0 NormalX=0 NormalY=0 NormalZ=1 AngleXU=0 Radius=1
    g34: Circle CenterX=-9.33087 CenterY=-15.1837 CenterZ=0 NormalX=0 NormalY=0 NormalZ=1 AngleXU=0 Radius=1
    g35: Circle CenterX=-10.1571 CenterY=-16 CenterZ=0 NormalX=0 NormalY=0 NormalZ=1 AngleXU=0 Radius=1
    g36: BSplineCurve PolesCount=3 KnotsCount=2 Degree=2 IsPeriodic=0
    g37: GeomPoint X=-8.70761 Y=-14 Z=0
    g38: GeomPoint X=-10.1571 Y=-16 Z=0
    g39: Circle CenterX=-12.8401 CenterY=-17.6958 CenterZ=0 NormalX=0 NormalY=0 NormalZ=1 AngleXU=0 Radius=1
    g40: Circle CenterX=-13.3521 CenterY=-17.9027 CenterZ=0 NormalX=0 NormalY=0 NormalZ=1 AngleXU=0 Radius=1
    g41: Circle CenterX=-14 CenterY=-18 CenterZ=0 NormalX=0 NormalY=0 NormalZ=1 AngleXU=0 Radius=1
    g42: BSplineCurve PolesCount=3 KnotsCount=2 Degree=2 IsPeriodic=0
    g43: GeomPoint X=-12.8401 Y=-17.6958 Z=0
    g44: GeomPoint X=-14 Y=-18 Z=0
    g45: LineSegment StartX=-6.2 StartY=0 StartZ=0 EndX=-7.2 EndY=0 EndZ=0
    g46: LineSegment StartX=-7.2 StartY=0 StartZ=0 EndX=-7.2 EndY=-2 EndZ=0
    g47: LineSegment StartX=-7.2 StartY=-2 StartZ=0 EndX=-6.2215 EndY=-2 EndZ=0
    g48: LineSegment StartX=-6.32538 StartY=-4 StartZ=0 EndX=-7.65538 EndY=-4 EndZ=0
    g49: LineSegment StartX=-7.65538 StartY=-4 StartZ=0 EndX=-7.65538 EndY=-5.99526 EndZ=0
    g50: LineSegment StartX=-7.65538 StartY=-5.99526 StartZ=0 EndX=-6.48644 EndY=-5.99526 EndZ=0
    g51: LineSegment StartX=-6.77343 StartY=-8 StartZ=0 EndX=-8.43343 EndY=-8 EndZ=0
    g52: LineSegment StartX=-8.43343 StartY=-8 StartZ=0 EndX=-8.43343 EndY=-10 EndZ=0
    g53: LineSegment StartX=-8.43343 StartY=-10 StartZ=0 EndX=-7.19003 EndY=-10 EndZ=0
  constraints (112):
    c: Horizontal(g0)
    c: Distance(g0) = 2
    c: Block(g0)
    c: Vertical(g1)
    c: Coincident(g2,g0)
    c: Vertical(g2)
    c: Block(g2)
    c: Coincident(g6,g2)
    c: Weight(g3) = 1
    c: Equal(g3,g4)
    c: Equal(g3,g5)
    c: InternalAlignment(g3,g6)
    c: InternalAlignment(g4,g6)
    c: InternalAlignment(g5,g6)
    c: InternalAlignment(g7,g6)
    c: InternalAlignment(g8,g6)
    c: Block(g6)
    c: Coincident(g9,g1)
    c: Coincident(g9,g6)
    c: Horizontal(g9)
    c: Vertical(g10)
    c: Block(g10)
    c: Horizontal(g11)
    c: Block(g11)
    c: Coincident(g12,g10)
    c: Horizontal(g12)
    c: Block(g12)
    c: Coincident(g13,g11)
    c: Vertical(g13)
    c: Block(g13)
    c: Coincident(g14,g10)
    c: Horizontal(g14)
    c: Block(g14)
    c: Block(g9)
    c: Block(g1)
    c: Weight(g15) = 1
    c: Equal(g15,g16)
    c: Equal(g15,g17)
    c: InternalAlignment(g15,g18)
    c: InternalAlignment(g16,g18)
    c: InternalAlignment(g17,g18)
    c: InternalAlignment(g19,g18)
    c: InternalAlignment(g20,g18)
    c: Weight(g21) = 1
    c: Equal(g21,g22)
    c: Equal(g21,g23)
    c: InternalAlignment(g21,g24)
    c: InternalAlignment(g22,g24)
    c: InternalAlignment(g23,g24)
    c: InternalAlignment(g25,g24)
    c: InternalAlignment(g26,g24)
    c: Weight(g27) = 1
    c: Equal(g27,g28)
    c: Equal(g27,g29)
    c: Coincident(g30,g14)
    c: InternalAlignment(g27,g30)
    c: InternalAlignment(g28,g30)
    c: InternalAlignment(g29,g30)
    c: InternalAlignment(g31,g30)
    c: InternalAlignment(g32,g30)
    c: Coincident(g36,g12)
    c: Weight(g33) = 1
    c: Equal(g33,g34)
    c: Equal(g33,g35)
    c: Coincident(g36,g11)
    c: InternalAlignment(g33,g36)
    c: InternalAlignment(g34,g36)
    c: InternalAlignment(g35,g36)
    c: InternalAlignment(g37,g36)
    c: InternalAlignment(g38,g36)
    c: Coincident(g42,g13)
    c: Weight(g39) = 1
    c: Equal(g39,g40)
    c: Equal(g39,g41)
    c: Coincident(g42,g1)
    c: InternalAlignment(g39,g42)
    c: InternalAlignment(g40,g42)
    c: InternalAlignment(g41,g42)
    c: InternalAlignment(g43,g42)
    c: InternalAlignment(g44,g42)
    c: Block(g18)
    c: Block(g24)
    c: Block(g30)
    c: Block(g36)
    c: Block(g42)
    c: Horizontal(g45)
    c: Coincident(g45,g0)
    c: Vertical(g46)
    c: Coincident(g46,g45)
    c: Coincident(g47,g46)
    c: Coincident(g47,g18)
    c: Horizontal(g47)
    c: Block(g46)
    c: Coincident(g48,g18)
    c: Horizontal(g48)
    c: Distance(g48) = 1.33
    c: Vertical(g49)
    c: Coincident(g49,g48)
    c: Coincident(g50,g49)
    c: Coincident(g50,g24)
    c: Horizontal(g50)
    c: Tangent(g50,g22)
    c: Horizontal(g51)
    c: Coincident(g51,g24)
    c: Block(g51)
    c: Vertical(g52)
    c: Block(g52)
    c: Coincident(g52,g51)
    c: Coincident(g53,g52)
    c: Coincident(g53,g30)
    c: Horizontal(g53)
    c: Distance(g1) = 8.5
FEATURE [Part::Feature] Face024
  shape: bbox 9.8 x 26.5 x 2e-07 mm, 1 faces, 0 solids (baked)
FEATURE [Part::Revolution] Revolve024
  Angle = 360
  Axis = (0,1,0)
  Base = (0,0,0)
  FaceMakerClass = Part::FaceMakerBullseye
  Placement = pos=(0,0,0) rot=(0,0,1;1.5708rad)
  Solid = false
  Source = -> Face024
  Symmetric = false
FEATURE [Part::Feature] Face025
  shape: bbox 9.8 x 26.5 x 2e-07 mm, 1 faces, 0 solids (baked)
FEATURE [Part::Revolution] Revolve025
  Angle = 360
  Axis = (0,1,0)
  Base = (0,0,0)
  FaceMakerClass = Part::FaceMakerBullseye
  Placement = pos=(0,0,0) rot=(0,0,1;1.5708rad)
  Solid = false
  Source = -> Face025
  Symmetric = false
FEATURE [Part::MultiFuse] Fusion033
  Placement = pos=(-18,19,36) rot=(0,0,1;0rad)
  Shapes = -> [Revolve025,Revolve024]
FEATURE [Part::Cylinder] Cylinder014
  Angle = 360
  AttacherType = Attacher::AttachEngine3D
  Height = 20
  Placement = pos=(0,0,36.15) rot=(0,0,1;0rad)
  Radius = 14.3
FEATURE [Part::Cylinder] Cylinder015
  Angle = 360
  AttacherType = Attacher::AttachEngine3D
  Height = 10
  Placement = pos=(0,0,36.15) rot=(0,0,1;0rad)
  Radius = 4
FEATURE [Part::MultiFuse] Fusion034  label="removeToCreteHoleForPlugHousing004"
  Placement = pos=(-42,19,36) rot=(0,1,0;1.5708rad)
  Shapes = -> [Cylinder014,Cylinder015]
FEATURE [Part::Cut] Cut008  label="top004"
  Base = -> Cut004
  Placement = pos=(-1,0,0) rot=(0,0,1;0rad)
  Tool = -> Fusion034
FEATURE [Part::Box] Box005  label="Cube005"
  AttacherType = Attacher::AttachEngine3D
  Height = 28
  Length = 3
  Placement = pos=(110.7,19,22) rot=(0,0,1;0rad)
  Width = 15.7
FEATURE [Part::Cylinder] Cylinder016
  Angle = 360
  AttacherType = Attacher::AttachEngine3D
  Height = 10
  Placement = pos=(0,0,36.15) rot=(0,0,1;0rad)
  Radius = 4
FEATURE [Part::Cylinder] Cylinder017
  Angle = 360
  AttacherType = Attacher::AttachEngine3D
  Height = 20
  Placement = pos=(0,0,36.15) rot=(0,0,1;0rad)
  Radius = 10.3
FEATURE [Part::MultiFuse] Fusion035  label="removeToCreteHoleForPlugHousing005"
  Placement = pos=(70,19,36) rot=(0,1,0;1.5708rad)
  Shapes = -> [Cylinder017,Cylinder016]
FEATURE [Part::Cut] Cut009  label="plugHousingTab001"
  Base = -> Box005
  Placement = pos=(-107.4,-14,0) rot=(0,0,1;0rad)
  Tool = -> Fusion035
FEATURE [Part::Box] Box006  label="Cube006"
  AttacherType = Attacher::AttachEngine3D
  Height = 28
  Length = 3
  Placement = pos=(110.7,19,22) rot=(0,0,1;0rad)
  Width = 15.7
FEATURE [Part::Cylinder] Cylinder018
  Angle = 360
  AttacherType = Attacher::AttachEngine3D
  Height = 10
  Placement = pos=(0,0,36.15) rot=(0,0,1;0rad)
  Radius = 4
FEATURE [Part::Cylinder] Cylinder019
  Angle = 360
  AttacherType = Attacher::AttachEngine3D
  Height = 20
  Placement = pos=(0,0,36.15) rot=(0,0,1;0rad)
  Radius = 10.3
FEATURE [Part::MultiFuse] Fusion036  label="removeToCreteHoleForPlugHousing006"
  Placement = pos=(70,19,36) rot=(0,1,0;1.5708rad)
  Shapes = -> [Cylinder019,Cylinder018]
FEATURE [Part::Cut] Cut010  label="plugHousingTab002"
  Base = -> Box006
  Placement = pos=(-107.4,-14,0) rot=(0,0,1;0rad)
  Tool = -> Fusion036
FEATURE [Part::MultiFuse] Fusion037
  Placement = pos=(9.6,23,0) rot=(0,0,1;3.14159rad)
  Shapes = -> [Cut009,Cut010]
FEATURE [Part::Box] Box  label="Cube"
  AttacherType = Attacher::AttachEngine3D
  Height = 10
  Length = 3
  Placement = pos=(3.3,4,12) rot=(0,0,1;0rad)
  Width = 10
FEATURE [Part::Fillet] Fillet004
  Base = -> Fusion028
  Edges = 1 edges r=2: [Edge25]
FEATURE [Part::Fillet] Fillet005  label="plugHousing046"
  Base = -> Fillet004
  Edges = 1 edges r=2: [Edge8]
FEATURE [Part::Fillet] Fillet006
  Base = -> Box
  Edges = 1 edges r=2: [Edge11]
FEATURE [Part::Box] Box007  label="Cube007"
  AttacherType = Attacher::AttachEngine3D
  Height = 10
  Length = 3
  Placement = pos=(3.3,4,50) rot=(0,0,1;0rad)
  Width = 10
FEATURE [Part::Fillet] Fillet007
  Base = -> Box007
  Edges = 1 edges r=2: [Edge12]
FEATURE [Part::Box] Box008  label="Cube008"
  AttacherType = Attacher::AttachEngine3D
  Height = 28
  Length = 4
  Placement = pos=(5,0,22) rot=(0,0,1;0rad)
  Width = 10
FEATURE [Part::Fillet] Fillet008
  Base = -> Box008
  Edges = 1 edges r=1: [Edge7]
FEATURE [Part::Fillet] Fillet009
  Base = -> Fillet008
  Edges = 1 edges r=2: [Edge5]
FEATURE [Part::Fillet] Fillet010
  Base = -> Fillet009
  Edges = 1 edges r=2: [Edge2]
FEATURE [Sketcher::SketchObject] Sketch009  label="topSketch003"
  FullyConstrained = true
  sketch-geometry (4):
    g0: LineSegment StartX=16.8446 StartY=31.512 StartZ=0 EndX=16.3251 EndY=34.4666 EndZ=0
    g1: ArcOfCircle CenterX=19 CenterY=19.2524 CenterZ=0 NormalX=0 NormalY=0 NormalZ=1 AngleXU=0 Radius=15.4476 StartAngle=1.74483 EndAngle=2.72717
    g2: ArcOfCircle CenterX=19 CenterY=19.2524 CenterZ=0 NormalX=0 NormalY=0 NormalZ=1 AngleXU=0 Radius=12.4476 StartAngle=1.74483 EndAngle=2.73189
    g3: LineSegment StartX=4.86004 StartY=25.4725 StartZ=0 EndX=7.58253 EndY=24.2107 EndZ=0
  constraints (7):
    c: Block(g0)
    c: Coincident(g1,g0)
    c: Coincident(g2,g0)
    c: Coincident(g3,g1)
    c: Coincident(g3,g2)
    c: Block(g1)
    c: Block(g2)
FEATURE [Part::Extrusion] Extrude008
  Base = -> Sketch009
  Dir = (0,0,1)
  DirMode = 2
  FaceMakerClass = Part::FaceMakerBullseye
  LengthFwd = 10
  LengthRev = 0
  Placement = pos=(0,0,31) rot=(0,0,1;0rad)
  Solid = true
  Symmetric = false
FEATURE [Part::Cylinder] Cylinder020
  Angle = 360
  AttacherType = Attacher::AttachEngine3D
  Height = 20
  Placement = pos=(0,0,36.15) rot=(0,0,1;0rad)
  Radius = 8.2
FEATURE [Part::Cylinder] Cylinder021
  Angle = 360
  AttacherType = Attacher::AttachEngine3D
  Height = 10
  Placement = pos=(0,0,36.15) rot=(0,0,1;0rad)
  Radius = 4
FEATURE [Part::MultiFuse] Fusion038  label="removeToCreteHoleForPlugHousing007"
  Placement = pos=(-42,19,36) rot=(0,1,0;1.5708rad)
  Shapes = -> [Cylinder020,Cylinder021]
FEATURE [Part::Cut] Cut011
  Base = -> Extrude008
  Tool = -> Fusion038
FEATURE [Part::Fillet] Fillet011
  Base = -> Cut011
  Edges = 1 edges r=2: [Edge1]
FEATURE [Part::Fillet] Fillet012
  Base = -> Fillet011
  Edges = 1 edges r=2.5: [Edge1]
FEATURE [Part::Fillet] Fillet013
  Base = -> Fillet012
  Edges = 1 edges r=2.5: [Edge2]
FEATURE [Part::Box] Box010  label="Cube010"
  AttacherType = Attacher::AttachEngine3D
  Height = 16
  Length = 8
  Placement = pos=(12.7,31.52,28) rot=(0,0,1;0rad)
  Width = 4
FEATURE [Sketcher::SketchObject] Sketch010  label="topSketch004"
  FullyConstrained = true
  sketch-geometry (4):
    g0: LineSegment StartX=16.8446 StartY=31.512 StartZ=0 EndX=16.3251 EndY=34.4666 EndZ=0
    g1: ArcOfCircle CenterX=19 CenterY=19.2524 CenterZ=0 NormalX=0 NormalY=0 NormalZ=1 AngleXU=0 Radius=15.4476 StartAngle=1.74483 EndAngle=2.72717
    g2: ArcOfCircle CenterX=19 CenterY=19.2524 CenterZ=0 NormalX=0 NormalY=0 NormalZ=1 AngleXU=0 Radius=12.4476 StartAngle=1.74483 EndAngle=2.73189
    g3: LineSegment StartX=4.86004 StartY=25.4725 StartZ=0 EndX=7.58253 EndY=24.2107 EndZ=0
  constraints (7):
    c: Block(g0)
    c: Coincident(g1,g0)
    c: Coincident(g2,g0)
    c: Coincident(g3,g1)
    c: Coincident(g3,g2)
    c: Block(g1)
    c: Block(g2)
FEATURE [Part::Cylinder] Cylinder022
  Angle = 360
  AttacherType = Attacher::AttachEngine3D
  Height = 10
  Placement = pos=(0,0,36.15) rot=(0,0,1;0rad)
  Radius = 4
FEATURE [Sketcher::SketchObject] Sketch011  label="topSketch005"
  FullyConstrained = true
  sketch-geometry (4):
    g0: LineSegment StartX=16.8446 StartY=31.512 StartZ=0 EndX=16.3251 EndY=34.4666 EndZ=0
    g1: ArcOfCircle CenterX=19 CenterY=19.2524 CenterZ=0 NormalX=0 NormalY=0 NormalZ=1 AngleXU=0 Radius=15.4476 StartAngle=1.74483 EndAngle=2.72717
    g2: ArcOfCircle CenterX=19 CenterY=19.2524 CenterZ=0 NormalX=0 NormalY=0 NormalZ=1 AngleXU=0 Radius=12.4476 StartAngle=1.74483 EndAngle=2.73189
    g3: LineSegment StartX=4.86004 StartY=25.4725 StartZ=0 EndX=7.58253 EndY=24.2107 EndZ=0
  constraints (7):
    c: Block(g0)
    c: Coincident(g1,g0)
    c: Coincident(g2,g0)
    c: Coincident(g3,g1)
    c: Coincident(g3,g2)
    c: Block(g1)
    c: Block(g2)
FEATURE [Part::Extrusion] Extrude010
  Base = -> Sketch011
  Dir = (0,0,1)
  DirMode = 2
  FaceMakerClass = Part::FaceMakerBullseye
  LengthFwd = 10.6
  LengthRev = 0
  Placement = pos=(0,0,31) rot=(0,0,1;0rad)
  Solid = true
  Symmetric = false
FEATURE [Part::Cylinder] Cylinder023
  Angle = 360
  AttacherType = Attacher::AttachEngine3D
  Height = 20
  Placement = pos=(0,0,36.15) rot=(0,0,1;0rad)
  Radius = 8.2
FEATURE [Part::MultiFuse] Fusion039  label="removeToCreteHoleForPlugHousing008"
  Placement = pos=(-42,19,36) rot=(0,1,0;1.5708rad)
  Shapes = -> [Cylinder023,Cylinder022]
FEATURE [Part::Cut] Cut012
  Base = -> Extrude010
  Placement = pos=(0,0,-0.3) rot=(0,0,1;0rad)
  Tool = -> Fusion039
FEATURE [Part::Cut] Cut013
  Base = -> Box010
  Tool = -> Cut012
FEATURE [Part::Fillet] Fillet014
  Base = -> Cut013
  Edges = 1 edges r=0.7: [Edge13]
FEATURE [Part::Fillet] Fillet015
  Base = -> Fillet014
  Edges = 1 edges r=0.7: [Edge13]
FEATURE [Part::Fillet] Fillet016
  Base = -> Fillet015
  Edges = 1 edges r=0.7: [Edge16]
FEATURE [Part::Fillet] Fillet017
  Base = -> Fillet016
  Edges = 1 edges r=0.7: [Edge11]
FEATURE [Part::Fillet] Fillet018
  Base = -> Fillet017
  Edges = 1 edges r=0.7: [Edge10]
FEATURE [Part::Fillet] Fillet019
  Base = -> Fillet018
  Edges = 1 edges r=1.2: [Edge5]
FEATURE [Part::Fillet] Fillet020
  Base = -> Fillet019
  Edges = 1 edges r=1.2: [Edge12]
FEATURE [Part::Fillet] Fillet021
  Base = -> Fillet020
  Edges = 1 edges r=2: [Edge1]
  Placement = pos=(0.3,0,0) rot=(0,0,1;0rad)
FEATURE [Part::MultiFuse] Fusion040  label="top005"
  Shapes = -> [Cut008,Fillet021]
FEATURE [Part::MultiFuse] Fusion041  label="wireHolder"
  Shapes = -> [Fusion033,Fillet013]
FEATURE [Part::MultiFuse] Fusion042
  Shapes = -> [Fillet007,Fusion041]
FEATURE [Part::MultiFuse] Fusion043  label="wireHolder001"
  Shapes = -> [Fusion042,Fillet010]
FEATURE [Part::MultiFuse] Fusion044  label="wireHolder002"
  Shapes = -> [Fillet006,Fusion037,Fusion043]
FEATURE [Part::Feature] Face026
  shape: bbox 11 x 6 x 2e-07 mm, 1 faces, 0 solids (baked)
FEATURE [Part::Revolution] Revolve026
  Angle = 360
  Axis = (0,1,0)
  Base = (0,0,0)
  FaceMakerClass = Part::FaceMakerBullseye
  Placement = pos=(30.3,-1,19.7) rot=(0,0,1;0rad)
  Solid = false
  Source = -> Face026
  Symmetric = false
FEATURE [Sketcher::SketchObject] Sketch013  label="topSketch006"
  FullyConstrained = true
  sketch-geometry (13):
    g0: LineSegment StartX=117 StartY=19 StartZ=0 EndX=117 EndY=38 EndZ=0
    g1: ArcOfCircle CenterX=98 CenterY=19 CenterZ=0 NormalX=0 NormalY=0 NormalZ=1 AngleXU=0 Radius=19 StartAngle=5.7297 EndAngle=6.28319
    g2: LineSegment StartX=0 StartY=3 StartZ=0 EndX=0 EndY=19 EndZ=0
    g3: LineSegment StartX=19 StartY=38 StartZ=0 EndX=117 EndY=38 EndZ=0
    g4: ArcOfCircle CenterX=19 CenterY=19 CenterZ=0 NormalX=0 NormalY=0 NormalZ=1 AngleXU=0 Radius=19 StartAngle=1.5708 EndAngle=3.14159
    g5: ArcOfCircle CenterX=19 CenterY=19 CenterZ=0 NormalX=0 NormalY=0 NormalZ=1 AngleXU=0 Radius=16 StartAngle=1.5708 EndAngle=3.14159
    g6: ArcOfCircle CenterX=98 CenterY=19 CenterZ=0 NormalX=0 NormalY=0 NormalZ=1 AngleXU=0 Radius=16 StartAngle=5.60905 EndAngle=6.28319
    g7: LineSegment StartX=114 StartY=19 StartZ=0 EndX=114 EndY=35 EndZ=0
    g8: LineSegment StartX=110.5 StartY=9.01251 StartZ=0 EndX=114.163 EndY=9.01251 EndZ=0
    g9: LineSegment StartX=114 StartY=35 StartZ=0 EndX=19 EndY=35 EndZ=0
    g10: LineSegment StartX=0 StartY=3 StartZ=0 EndX=0 EndY=0 EndZ=0
    g11: LineSegment StartX=3 StartY=0 StartZ=0 EndX=0 EndY=0 EndZ=0
    g12: LineSegment StartX=3 StartY=19 StartZ=0 EndX=3 EndY=0 EndZ=0
  constraints (33):
    c: Vertical(g0)
    c: Distance(g0) = 19
    c: Block(g0)
    c: Coincident(g1,g0)
    c: Block(g1)
    c: Vertical(g2)
    c: Block(g2)
    c: Coincident(g3,g0)
    c: Horizontal(g3)
    c: Distance(g3) = 98
    c: Coincident(g4,g3)
    c: Coincident(g4,g2)
    c: Block(g4)
    c: Coincident(g5,g4)
    c: Coincident(g6,g1)
    c: Block(g6)
    c: Block(g5)
    c: Coincident(g7,g6)
    c: Vertical(g7)
    c: Coincident(g8,g6)
    c: Coincident(g8,g1)
    c: Coincident(g9,g7)
    c: Coincident(g9,g5)
    c: Horizontal(g9)
    c: Tangent(g9,g5)
    c: Coincident(g10,g2)
    c: Distance(g10) = 3
    c: Vertical(g10)
    c: Coincident(g11,g10)
    c: Horizontal(g11)
    c: Coincident(g12,g5)
    c: Coincident(g12,g11)
    c: Vertical(g12)
FEATURE [Part::Extrusion] Extrude011  label="top006"
  Base = -> Sketch013
  Dir = (0,0,1)
  DirMode = 2
  FaceMakerClass = Part::FaceMakerBullseye
  LengthFwd = 72
  LengthRev = 0
  Solid = true
  Symmetric = false
FEATURE [Sketcher::SketchObject] Sketch014
  FullyConstrained = true
  MapMode = 3
  Placement = pos=(0,0,0) rot=(1,0,0;1.5708rad)
  Support = -> [Extrude011]
  sketch-geometry (8):
    g0: Circle CenterX=80.351 CenterY=-67.6202 CenterZ=0 NormalX=0 NormalY=0 NormalZ=1 AngleXU=0 Radius=2
    g1: Circle CenterX=80.351 CenterY=-67.6202 CenterZ=0 NormalX=0 NormalY=0 NormalZ=1 AngleXU=0 Radius=3
    g2: Circle CenterX=80.351 CenterY=-4.92017 CenterZ=0 NormalX=0 NormalY=0 NormalZ=1 AngleXU=0 Radius=2
    g3: Circle CenterX=80.351 CenterY=-4.92017 CenterZ=0 NormalX=0 NormalY=0 NormalZ=1 AngleXU=0 Radius=3
    g4: Circle CenterX=23.851 CenterY=-4.92017 CenterZ=0 NormalX=0 NormalY=0 NormalZ=1 AngleXU=0 Radius=2
    g5: Circle CenterX=23.851 CenterY=-4.92017 CenterZ=0 NormalX=0 NormalY=0 NormalZ=1 AngleXU=0 Radius=3
    g6: Circle CenterX=23.851 CenterY=-67.6202 CenterZ=0 NormalX=0 NormalY=0 NormalZ=1 AngleXU=0 Radius=2
    g7: Circle CenterX=23.851 CenterY=-67.6202 CenterZ=0 NormalX=0 NormalY=0 NormalZ=1 AngleXU=0 Radius=3
  constraints (8):
    c: Block(g3)
    c: Block(g2)
    c: Block(g1)
    c: Block(g0)
    c: Block(g6)
    c: Block(g7)
    c: Block(g4)
    c: Block(g5)
FEATURE [Part::Feature] Face027
  shape: bbox 11 x 6 x 2e-07 mm, 1 faces, 0 solids (baked)
FEATURE [Part::Revolution] Revolve027
  Angle = 360
  Axis = (0,1,0)
  Base = (0,0,0)
  FaceMakerClass = Part::FaceMakerBullseye
  Placement = pos=(30.3,-1,51.7) rot=(0,0,1;0rad)
  Solid = false
  Source = -> Face027
  Symmetric = false
FEATURE [Part::Feature] Face028
  shape: bbox 11 x 6 x 2e-07 mm, 1 faces, 0 solids (baked)
FEATURE [Part::Revolution] Revolve028
  Angle = 360
  Axis = (0,1,0)
  Base = (0,0,0)
  FaceMakerClass = Part::FaceMakerBullseye
  Placement = pos=(62.3,-1,19.7) rot=(0,0,1;0rad)
  Solid = false
  Source = -> Face028
  Symmetric = false
FEATURE [Part::Feature] Face029
  shape: bbox 11 x 6 x 2e-07 mm, 1 faces, 0 solids (baked)
FEATURE [Part::Revolution] Revolve029
  Angle = 360
  Axis = (0,1,0)
  Base = (0,0,0)
  FaceMakerClass = Part::FaceMakerBullseye
  Placement = pos=(62.3,-1,51.7) rot=(0,0,1;0rad)
  Solid = false
  Source = -> Face029
  Symmetric = false
FEATURE [Part::Feature] Wire
  shape: bbox 11 x 5.2 x 2e-07 mm, 0 faces, 0 solids (baked)
FEATURE [Part::Revolution] Revolve030
  Angle = 360
  Axis = (0,1,0)
  Base = (0,0,0)
  FaceMakerClass = Part::FaceMakerBullseye
  Placement = pos=(30.3,38,19.7) rot=(0,0,1;0rad)
  Solid = true
  Source = -> Wire
  Symmetric = false
FEATURE [Part::Feature] Wire001
  shape: bbox 11 x 5.2 x 2e-07 mm, 0 faces, 0 solids (baked)
FEATURE [Part::Revolution] Revolve031
  Angle = 360
  Axis = (0,1,0)
  Base = (0,0,0)
  FaceMakerClass = Part::FaceMakerBullseye
  Placement = pos=(30.3,38,51.7) rot=(0,0,1;0rad)
  Solid = true
  Source = -> Wire001
  Symmetric = false
FEATURE [Part::Feature] Wire002
  shape: bbox 11 x 5.2 x 2e-07 mm, 0 faces, 0 solids (baked)
FEATURE [Part::Revolution] Revolve032
  Angle = 360
  Axis = (0,1,0)
  Base = (0,0,0)
  FaceMakerClass = Part::FaceMakerBullseye
  Placement = pos=(62.3,38,51.7) rot=(0,0,1;0rad)
  Solid = true
  Source = -> Wire002
  Symmetric = false
FEATURE [Part::Feature] Wire003
  shape: bbox 11 x 5.2 x 2e-07 mm, 0 faces, 0 solids (baked)
FEATURE [Part::Revolution] Revolve033
  Angle = 360
  Axis = (0,1,0)
  Base = (0,0,0)
  FaceMakerClass = Part::FaceMakerBullseye
  Placement = pos=(62.3,38,19.7) rot=(0,0,1;0rad)
  Solid = true
  Source = -> Wire003
  Symmetric = false
FEATURE [Part::MultiFuse] Fusion045  label="altRandScrewHousing"
  Shapes = -> [Revolve029,Revolve027,Revolve028,Revolve026]
FEATURE [Part::MultiFuse] Fusion046  label="fanScrewHousing"
  Shapes = -> [Revolve033,Revolve032,Revolve031,Revolve030]
FEATURE [Sketcher::SketchObject] Sketch015
  FullyConstrained = true
  sketch-geometry (17):
    g0: Circle CenterX=-3.5 CenterY=23.5 CenterZ=0 NormalX=0 NormalY=0 NormalZ=1 AngleXU=0 Radius=1
    g1: Circle CenterX=-1 CenterY=15.25 CenterZ=0 NormalX=0 NormalY=0 NormalZ=1 AngleXU=0 Radius=1
    g2: Circle CenterX=-3.5 CenterY=7 CenterZ=0 NormalX=0 NormalY=0 NormalZ=1 AngleXU=0 Radius=1
    g3: BSplineCurve PolesCount=3 KnotsCount=2 Degree=2 IsPeriodic=0
    g4: GeomPoint X=-3.5 Y=23.5 Z=0
    g5: GeomPoint X=-3.5 Y=7 Z=0
    g6: Circle CenterX=-4.8 CenterY=30.5 CenterZ=0 NormalX=0 NormalY=0 NormalZ=1 AngleXU=0 Radius=1
    g7: Circle CenterX=-3.5 CenterY=30.5 CenterZ=0 NormalX=0 NormalY=0 NormalZ=1 AngleXU=0 Radius=1
    g8: Circle CenterX=-3.5 CenterY=29.2 CenterZ=0 NormalX=0 NormalY=0 NormalZ=1 AngleXU=0 Radius=1
    g9: BSplineCurve PolesCount=3 KnotsCount=2 Degree=2 IsPeriodic=0
    g10: GeomPoint X=-4.8 Y=30.5 Z=0
    g11: GeomPoint X=-3.5 Y=29.2 Z=0
    g12: LineSegment StartX=-3.5 StartY=29.2 StartZ=0 EndX=-3.5 EndY=23.5 EndZ=0
    g13: LineSegment StartX=-4.8 StartY=30.5 StartZ=0 EndX=0 EndY=30.5 EndZ=0
    g14: LineSegment StartX=-3.5 StartY=0.3 StartZ=0 EndX=0 EndY=0.3 EndZ=0
    g15: LineSegment StartX=-3.5 StartY=0.3 StartZ=0 EndX=-3.5 EndY=7 EndZ=0
    g16: LineSegment StartX=0 StartY=0.3 StartZ=0 EndX=0 EndY=30.5 EndZ=0
  constraints (33):
    c: Weight(g0) = 1
    c: Equal(g0,g1)
    c: Equal(g0,g2)
    c: InternalAlignment(g0,g3)
    c: InternalAlignment(g1,g3)
    c: InternalAlignment(g2,g3)
    c: InternalAlignment(g4,g3)
    c: InternalAlignment(g5,g3)
    c: Block(g3)
    c: Weight(g6) = 1
    c: Equal(g6,g7)
    c: Equal(g6,g8)
    c: InternalAlignment(g6,g9)
    c: InternalAlignment(g7,g9)
    c: InternalAlignment(g8,g9)
    c: InternalAlignment(g10,g9)
    c: InternalAlignment(g11,g9)
    c: Block(g9)
    c: Coincident(g12,g9)
    c: Coincident(g12,g3)
    c: Vertical(g12)
    c: Coincident(g13,g9)
    c: Horizontal(g13)
    c: Distance(g13) = 4.8
    c: Horizontal(g14)
    c: Block(g14)
    c: Coincident(g15,g14)
    c: Coincident(g15,g3)
    c: Vertical(g15)
    c: Coincident(g16,g14)
    c: Coincident(g16,g13)
    c: Vertical(g16)
    c: Tangent(g16,g1)
FEATURE [Sketcher::SketchObject] Sketch016
  FullyConstrained = true
  sketch-geometry (16):
    g0: Circle CenterX=-3.5 CenterY=23.5 CenterZ=0 NormalX=0 NormalY=0 NormalZ=1 AngleXU=0 Radius=1
    g1: Circle CenterX=-1 CenterY=15.25 CenterZ=0 NormalX=0 NormalY=0 NormalZ=1 AngleXU=0 Radius=1
    g2: Circle CenterX=-3.5 CenterY=7 CenterZ=0 NormalX=0 NormalY=0 NormalZ=1 AngleXU=0 Radius=1
    g3: BSplineCurve PolesCount=3 KnotsCount=2 Degree=2 IsPeriodic=0
    g4: GeomPoint X=-3.5 Y=23.5 Z=0
    g5: GeomPoint X=-3.5 Y=7 Z=0
    g6: LineSegment StartX=-3.5 StartY=28.2 StartZ=0 EndX=-3.5 EndY=23.5 EndZ=0
    g7: LineSegment StartX=0 StartY=29.5 StartZ=0 EndX=0 EndY=30 EndZ=0
    g8: LineSegment StartX=-3.5 StartY=28.2 StartZ=0 EndX=-3.5 EndY=30 EndZ=0
    g9: LineSegment StartX=0 StartY=30 StartZ=0 EndX=0 EndY=30.5 EndZ=0
    g10: LineSegment StartX=0 StartY=30.5 StartZ=0 EndX=-3.5 EndY=30.5 EndZ=0
    g11: LineSegment StartX=-3.5 StartY=30.5 StartZ=0 EndX=-3.5 EndY=30 EndZ=0
    g12: LineSegment StartX=0 StartY=29.5 StartZ=0 EndX=0 EndY=5 EndZ=0
    g13: LineSegment StartX=-3.5 StartY=0.3 StartZ=0 EndX=-3.5 EndY=7 EndZ=0
    g14: LineSegment StartX=-3.5 StartY=0.3 StartZ=0 EndX=0 EndY=0.3 EndZ=0
    g15: LineSegment StartX=0 StartY=5 StartZ=0 EndX=0 EndY=0.3 EndZ=0
  constraints (39):
    c: Weight(g0) = 1
    c: Equal(g0,g1)
    c: Equal(g0,g2)
    c: InternalAlignment(g0,g3)
    c: InternalAlignment(g1,g3)
    c: InternalAlignment(g2,g3)
    c: InternalAlignment(g4,g3)
    c: InternalAlignment(g5,g3)
    c: Block(g3)
    c: Coincident(g6,g3)
    c: Vertical(g6)
    c: Vertical(g7)
    c: Distance(g7) = 0.5
    c: Coincident(g8,g6)
    c: Vertical(g8)
    c: Block(g6)
    c: Block(g7)
    c: Vertical(g9)
    c: Equal(g7,g9) = 0.5
    c: Block(g9)
    c: Coincident(g9,g7)
    c: Horizontal(g10)
    c: Coincident(g10,g9)
    c: Coincident(g11,g10)
    c: Coincident(g11,g8)
    c: Vertical(g11)
    c: Block(g11)
    c: Coincident(g12,g7)
    c: Vertical(g12)
    c: Coincident(g13,g3)
    c: Vertical(g13)
    c: Distance(g13) = 6.7
    c: Coincident(g14,g13)
    c: Horizontal(g14)
    c: Block(g14)
    c: Coincident(g15,g12)
    c: Coincident(g15,g14)
    c: Vertical(g15)
    c: Block(g15)
FEATURE [Sketcher::SketchObject] Sketch017
  FullyConstrained = true
  sketch-geometry (11):
    g0: LineSegment StartX=-3.5 StartY=1e-16 StartZ=0 EndX=-1.6 EndY=1e-16 EndZ=0
    g1: LineSegment StartX=-1.6 StartY=1e-16 StartZ=0 EndX=-1.6 EndY=1.5 EndZ=0
    g2: LineSegment StartX=-3.5 StartY=1.5 StartZ=0 EndX=-1.6 EndY=1.5 EndZ=0
    g3: LineSegment StartX=-3.5 StartY=1e-16 StartZ=0 EndX=-4.8 EndY=1e-16 EndZ=0
    g4: Circle CenterX=-3.5 CenterY=1.3 CenterZ=0 NormalX=0 NormalY=0 NormalZ=1 AngleXU=0 Radius=1
    g5: Circle CenterX=-3.5 CenterY=1e-16 CenterZ=0 NormalX=0 NormalY=0 NormalZ=1 AngleXU=0 Radius=1
    g6: Circle CenterX=-4.8 CenterY=1e-16 CenterZ=0 NormalX=0 NormalY=0 NormalZ=1 AngleXU=0 Radius=1
    g7: BSplineCurve PolesCount=3 KnotsCount=2 Degree=2 IsPeriodic=0
    g8: GeomPoint X=-3.5 Y=1.3 Z=0
    g9: GeomPoint X=-4.8 Y=1e-16 Z=0
    g10: LineSegment StartX=-3.5 StartY=1.3 StartZ=0 EndX=-3.5 EndY=1.5 EndZ=0
  constraints (24):
    c: Horizontal(g0)
    c: Distance(g0) = 1.9
    c: Block(g0)
    c: Coincident(g1,g0)
    c: Vertical(g1)
    c: Coincident(g2,g1)
    c: Horizontal(g2)
    c: Coincident(g3,g0)
    c: Horizontal(g3)
    c: Distance(g3) = 1.3
    c: Weight(g4) = 1
    c: Equal(g4,g5)
    c: Coincident(g5,g0)
    c: Equal(g4,g6)
    c: Coincident(g7,g3)
    c: InternalAlignment(g4,g7)
    c: InternalAlignment(g5,g7)
    c: InternalAlignment(g6,g7)
    c: InternalAlignment(g8,g7)
    c: InternalAlignment(g9,g7)
    c: Coincident(g10,g7)
    c: Coincident(g10,g2)
    c: Vertical(g10)
    c: Block(g10)
FEATURE [Part::Feature] Face035
  shape: bbox 3.2 x 1.5 x 2e-07 mm, 1 faces, 0 solids (baked)
FEATURE [Part::Revolution] Revolve039  label="backCaseScrewRetainer"
  Angle = 360
  Axis = (0,1,0)
  Base = (0,0,0)
  FaceMakerClass = Part::FaceMakerBullseye
  Placement = pos=(12.5,3,62) rot=(0,0,1;0rad)
  Solid = false
  Source = -> Face035
  Symmetric = false
FEATURE [Part::Feature] Face036
  shape: bbox 3.2 x 1.5 x 2e-07 mm, 1 faces, 0 solids (baked)
FEATURE [Part::Feature] Face039
  shape: bbox 4.8 x 30.2 x 2e-07 mm, 1 faces, 0 solids (baked)
FEATURE [Part::Revolution] Revolve043  label="frontCaseScrewPost002"
  Angle = 360
  Axis = (0,1,0)
  Base = (0,0,0)
  FaceMakerClass = Part::FaceMakerBullseye
  Placement = pos=(89.5,4.5,3.5) rot=(0,0,1;0rad)
  Solid = false
  Source = -> Face039
  Symmetric = false
FEATURE [Part::Feature] Face042
  shape: bbox 4.8 x 30.2 x 2e-07 mm, 1 faces, 0 solids (baked)
FEATURE [Part::Revolution] Revolve046  label="frontCaseScrewPost003"
  Angle = 360
  Axis = (0,1,0)
  Base = (0,0,0)
  FaceMakerClass = Part::FaceMakerBullseye
  Placement = pos=(89.5,4.5,68.5) rot=(0,0,1;0rad)
  Solid = false
  Source = -> Face042
  Symmetric = false
FEATURE [Part::Feature] Face043
  shape: bbox 3.2 x 1.5 x 2e-07 mm, 1 faces, 0 solids (baked)
FEATURE [Part::Revolution] Revolve047  label="frontCaseScrewRetainer002"
  Angle = 360
  Axis = (0,1,0)
  Base = (0,0,0)
  FaceMakerClass = Part::FaceMakerBullseye
  Placement = pos=(89.5,3,68.5) rot=(0,0,1;0rad)
  Solid = false
  Source = -> Face043
  Symmetric = false
FEATURE [Part::Feature] Face044
  shape: bbox 3.2 x 1.5 x 2e-07 mm, 1 faces, 0 solids (baked)
FEATURE [Part::Revolution] Revolve048  label="frontCaseScrewRetainer003"
  Angle = 360
  Axis = (0,1,0)
  Base = (0,0,0)
  FaceMakerClass = Part::FaceMakerBullseye
  Placement = pos=(89.5,3,3.5) rot=(0,0,1;0rad)
  Solid = false
  Source = -> Face044
  Symmetric = false
FEATURE [App::MeasureDistance] Distance002  label="Distance: 1.67 mm"
  Distance = 1.66921
  P1 = (99.2361,4.7524,71.7)
  P2 = (99.2347,6.42161,71.7)
FEATURE [Sketcher::SketchObject] Sketch018
  FullyConstrained = true
  sketch-geometry (7):
    g0: LineSegment StartX=0 StartY=0 StartZ=0 EndX=0 EndY=6 EndZ=0
    g1: Circle CenterX=0 CenterY=0 CenterZ=0 NormalX=0 NormalY=0 NormalZ=1 AngleXU=0 Radius=1
    g2: Circle CenterX=8 CenterY=6 CenterZ=0 NormalX=0 NormalY=0 NormalZ=1 AngleXU=0 Radius=1
    g3: BSplineCurve PolesCount=3 KnotsCount=2 Degree=2 IsPeriodic=0
    g4: GeomPoint X=0 Y=0 Z=0
    g5: GeomPoint X=8 Y=6 Z=0
    g6: LineSegment StartX=0 StartY=6 StartZ=0 EndX=8 EndY=6 EndZ=0
  constraints (14):
    c: Coincident(g0,g-1)
    c: Distance(g0) = 6
    c: Vertical(g0)
    c: Coincident(g3,g0)
    c: Weight(g1) = 1
    c: Equal(g1,g2)
    c: InternalAlignment(g1,g3)
    c: InternalAlignment(g2,g3)
    c: InternalAlignment(g4,g3)
    c: InternalAlignment(g5,g3)
    c: Block(g3)
    c: Coincident(g6,g0)
    c: Coincident(g6,g3)
    c: Horizontal(g6)
FEATURE [Part::Extrusion] Extrude012  label="caseScrewPillarBracket"
  Base = -> Sketch018
  Dir = (0,0,1)
  DirMode = 2
  FaceMakerClass = Part::FaceMakerBullseye
  LengthFwd = 2.4
  LengthRev = 0
  Placement = pos=(15.76,29,8.8) rot=(0,1,0;0rad)
  Solid = true
  Symmetric = false
FEATURE [Sketcher::SketchObject] Sketch019
  FullyConstrained = true
  sketch-geometry (7):
    g0: LineSegment StartX=0 StartY=0 StartZ=0 EndX=0 EndY=6 EndZ=0
    g1: Circle CenterX=0 CenterY=0 CenterZ=0 NormalX=0 NormalY=0 NormalZ=1 AngleXU=0 Radius=1
    g2: Circle CenterX=8 CenterY=6 CenterZ=0 NormalX=0 NormalY=0 NormalZ=1 AngleXU=0 Radius=1
    g3: BSplineCurve PolesCount=3 KnotsCount=2 Degree=2 IsPeriodic=0
    g4: GeomPoint X=0 Y=0 Z=0
    g5: GeomPoint X=8 Y=6 Z=0
    g6: LineSegment StartX=0 StartY=6 StartZ=0 EndX=8 EndY=6 EndZ=0
  constraints (14):
    c: Coincident(g0,g-1)
    c: Distance(g0) = 6
    c: Vertical(g0)
    c: Coincident(g3,g0)
    c: Weight(g1) = 1
    c: Equal(g1,g2)
    c: InternalAlignment(g1,g3)
    c: InternalAlignment(g2,g3)
    c: InternalAlignment(g4,g3)
    c: InternalAlignment(g5,g3)
    c: Block(g3)
    c: Coincident(g6,g0)
    c: Coincident(g6,g3)
    c: Horizontal(g6)
FEATURE [Part::Extrusion] Extrude013  label="caseScrewPillarBracket001"
  Base = -> Sketch019
  Dir = (0,0,1)
  DirMode = 2
  FaceMakerClass = Part::FaceMakerBullseye
  LengthFwd = 2.4
  LengthRev = 0
  Placement = pos=(15.76,29,60.8) rot=(0,0,1;0rad)
  Solid = true
  Symmetric = false
FEATURE [Sketcher::SketchObject] Sketch020
  FullyConstrained = true
  sketch-geometry (7):
    g0: LineSegment StartX=0 StartY=0 StartZ=0 EndX=0 EndY=6 EndZ=0
    g1: Circle CenterX=0 CenterY=0 CenterZ=0 NormalX=0 NormalY=0 NormalZ=1 AngleXU=0 Radius=1
    g2: Circle CenterX=8 CenterY=6 CenterZ=0 NormalX=0 NormalY=0 NormalZ=1 AngleXU=0 Radius=1
    g3: BSplineCurve PolesCount=3 KnotsCount=2 Degree=2 IsPeriodic=0
    g4: GeomPoint X=0 Y=0 Z=0
    g5: GeomPoint X=8 Y=6 Z=0
    g6: LineSegment StartX=0 StartY=6 StartZ=0 EndX=8 EndY=6 EndZ=0
  constraints (14):
    c: Coincident(g0,g-1)
    c: Distance(g0) = 6
    c: Vertical(g0)
    c: Coincident(g3,g0)
    c: Weight(g1) = 1
    c: Equal(g1,g2)
    c: InternalAlignment(g1,g3)
    c: InternalAlignment(g2,g3)
    c: InternalAlignment(g4,g3)
    c: InternalAlignment(g5,g3)
    c: Block(g3)
    c: Coincident(g6,g0)
    c: Coincident(g6,g3)
    c: Horizontal(g6)
FEATURE [Part::Extrusion] Extrude014  label="caseScrewPillarBracket002"
  Base = -> Sketch020
  Dir = (0,0,1)
  DirMode = 2
  FaceMakerClass = Part::FaceMakerBullseye
  LengthFwd = 2.4
  LengthRev = 0
  Placement = pos=(13.7,29,13.26) rot=(0,-1,0;1.5708rad)
  Solid = true
  Symmetric = false
FEATURE [Sketcher::SketchObject] Sketch021
  FullyConstrained = true
  sketch-geometry (7):
    g0: LineSegment StartX=0 StartY=0 StartZ=0 EndX=0 EndY=6 EndZ=0
    g1: Circle CenterX=0 CenterY=0 CenterZ=0 NormalX=0 NormalY=0 NormalZ=1 AngleXU=0 Radius=1
    g2: Circle CenterX=8 CenterY=6 CenterZ=0 NormalX=0 NormalY=0 NormalZ=1 AngleXU=0 Radius=1
    g3: BSplineCurve PolesCount=3 KnotsCount=2 Degree=2 IsPeriodic=0
    g4: GeomPoint X=0 Y=0 Z=0
    g5: GeomPoint X=8 Y=6 Z=0
    g6: LineSegment StartX=0 StartY=6 StartZ=0 EndX=8 EndY=6 EndZ=0
  constraints (14):
    c: Coincident(g0,g-1)
    c: Distance(g0) = 6
    c: Vertical(g0)
    c: Coincident(g3,g0)
    c: Weight(g1) = 1
    c: Equal(g1,g2)
    c: InternalAlignment(g1,g3)
    c: InternalAlignment(g2,g3)
    c: InternalAlignment(g4,g3)
    c: InternalAlignment(g5,g3)
    c: Block(g3)
    c: Coincident(g6,g0)
    c: Coincident(g6,g3)
    c: Horizontal(g6)
FEATURE [Part::Extrusion] Extrude015  label="caseScrewPillarBracket003"
  Base = -> Sketch021
  Dir = (0,0,1)
  DirMode = 2
  FaceMakerClass = Part::FaceMakerBullseye
  LengthFwd = 2.4
  LengthRev = 0
  Placement = pos=(11.3,29,58.74) rot=(0,1,0;1.5708rad)
  Solid = true
  Symmetric = false
FEATURE [Sketcher::SketchObject] Sketch022
  FullyConstrained = true
  sketch-geometry (7):
    g0: LineSegment StartX=0 StartY=0 StartZ=0 EndX=0 EndY=6 EndZ=0
    g1: Circle CenterX=0 CenterY=0 CenterZ=0 NormalX=0 NormalY=0 NormalZ=1 AngleXU=0 Radius=1
    g2: Circle CenterX=8 CenterY=6 CenterZ=0 NormalX=0 NormalY=0 NormalZ=1 AngleXU=0 Radius=1
    g3: BSplineCurve PolesCount=3 KnotsCount=2 Degree=2 IsPeriodic=0
    g4: GeomPoint X=0 Y=0 Z=0
    g5: GeomPoint X=8 Y=6 Z=0
    g6: LineSegment StartX=0 StartY=6 StartZ=0 EndX=8 EndY=6 EndZ=0
  constraints (14):
    c: Coincident(g0,g-1)
    c: Distance(g0) = 6
    c: Vertical(g0)
    c: Coincident(g3,g0)
    c: Weight(g1) = 1
    c: Equal(g1,g2)
    c: InternalAlignment(g1,g3)
    c: InternalAlignment(g2,g3)
    c: InternalAlignment(g4,g3)
    c: InternalAlignment(g5,g3)
    c: Block(g3)
    c: Coincident(g6,g0)
    c: Coincident(g6,g3)
    c: Horizontal(g6)
FEATURE [Part::Extrusion] Extrude016  label="caseScrewPillarBracket004"
  Base = -> Sketch022
  Dir = (0,0,1)
  DirMode = 2
  FaceMakerClass = Part::FaceMakerBullseye
  LengthFwd = 2.4
  LengthRev = 0
  Placement = pos=(88.3,29,65.23) rot=(0,1,0;1.5708rad)
  Solid = true
  Symmetric = false
FEATURE [Sketcher::SketchObject] Sketch023
  FullyConstrained = true
  sketch-geometry (7):
    g0: LineSegment StartX=0 StartY=0 StartZ=0 EndX=0 EndY=6 EndZ=0
    g1: Circle CenterX=0 CenterY=0 CenterZ=0 NormalX=0 NormalY=0 NormalZ=1 AngleXU=0 Radius=1
    g2: Circle CenterX=8 CenterY=6 CenterZ=0 NormalX=0 NormalY=0 NormalZ=1 AngleXU=0 Radius=1
    g3: BSplineCurve PolesCount=3 KnotsCount=2 Degree=2 IsPeriodic=0
    g4: GeomPoint X=0 Y=0 Z=0
    g5: GeomPoint X=8 Y=6 Z=0
    g6: LineSegment StartX=0 StartY=6 StartZ=0 EndX=8 EndY=6 EndZ=0
  constraints (14):
    c: Coincident(g0,g-1)
    c: Distance(g0) = 6
    c: Vertical(g0)
    c: Coincident(g3,g0)
    c: Weight(g1) = 1
    c: Equal(g1,g2)
    c: InternalAlignment(g1,g3)
    c: InternalAlignment(g2,g3)
    c: InternalAlignment(g4,g3)
    c: InternalAlignment(g5,g3)
    c: Block(g3)
    c: Coincident(g6,g0)
    c: Coincident(g6,g3)
    c: Horizontal(g6)
FEATURE [Part::Extrusion] Extrude017  label="caseScrewPillarBracket005"
  Base = -> Sketch023
  Dir = (0,0,1)
  DirMode = 2
  FaceMakerClass = Part::FaceMakerBullseye
  LengthFwd = 2.4
  LengthRev = 0
  Placement = pos=(90.7,29,6.77) rot=(0,-1,0;1.5708rad)
  Solid = true
  Symmetric = false
FEATURE [Sketcher::SketchObject] Sketch024
  FullyConstrained = true
  sketch-geometry (7):
    g0: LineSegment StartX=0 StartY=0 StartZ=0 EndX=0 EndY=6 EndZ=0
    g1: Circle CenterX=0 CenterY=0 CenterZ=0 NormalX=0 NormalY=0 NormalZ=1 AngleXU=0 Radius=1
    g2: Circle CenterX=8 CenterY=6 CenterZ=0 NormalX=0 NormalY=0 NormalZ=1 AngleXU=0 Radius=1
    g3: BSplineCurve PolesCount=3 KnotsCount=2 Degree=2 IsPeriodic=0
    g4: GeomPoint X=0 Y=0 Z=0
    g5: GeomPoint X=8 Y=6 Z=0
    g6: LineSegment StartX=0 StartY=6 StartZ=0 EndX=8 EndY=6 EndZ=0
  constraints (14):
    c: Coincident(g0,g-1)
    c: Distance(g0) = 6
    c: Vertical(g0)
    c: Coincident(g3,g0)
    c: Weight(g1) = 1
    c: Equal(g1,g2)
    c: InternalAlignment(g1,g3)
    c: InternalAlignment(g2,g3)
    c: InternalAlignment(g4,g3)
    c: InternalAlignment(g5,g3)
    c: Block(g3)
    c: Coincident(g6,g0)
    c: Coincident(g6,g3)
    c: Horizontal(g6)
FEATURE [Part::Extrusion] Extrude018  label="caseScrewPillarBracket006"
  Base = -> Sketch024
  Dir = (0,0,1)
  DirMode = 2
  FaceMakerClass = Part::FaceMakerBullseye
  LengthFwd = 2.4
  LengthRev = 0
  Placement = pos=(103.7,29,6.77) rot=(0,-1,0;1.5708rad)
  Solid = true
  Symmetric = false
FEATURE [Sketcher::SketchObject] Sketch025
  FullyConstrained = true
  sketch-geometry (7):
    g0: LineSegment StartX=0 StartY=0 StartZ=0 EndX=0 EndY=6 EndZ=0
    g1: Circle CenterX=0 CenterY=0 CenterZ=0 NormalX=0 NormalY=0 NormalZ=1 AngleXU=0 Radius=1
    g2: Circle CenterX=8 CenterY=6 CenterZ=0 NormalX=0 NormalY=0 NormalZ=1 AngleXU=0 Radius=1
    g3: BSplineCurve PolesCount=3 KnotsCount=2 Degree=2 IsPeriodic=0
    g4: GeomPoint X=0 Y=0 Z=0
    g5: GeomPoint X=8 Y=6 Z=0
    g6: LineSegment StartX=0 StartY=6 StartZ=0 EndX=8 EndY=6 EndZ=0
  constraints (14):
    c: Coincident(g0,g-1)
    c: Distance(g0) = 6
    c: Vertical(g0)
    c: Coincident(g3,g0)
    c: Weight(g1) = 1
    c: Equal(g1,g2)
    c: InternalAlignment(g1,g3)
    c: InternalAlignment(g2,g3)
    c: InternalAlignment(g4,g3)
    c: InternalAlignment(g5,g3)
    c: Block(g3)
    c: Coincident(g6,g0)
    c: Coincident(g6,g3)
    c: Horizontal(g6)
FEATURE [Part::Extrusion] Extrude019  label="caseScrewPillarBracket007"
  Base = -> Sketch025
  Dir = (0,0,1)
  DirMode = 2
  FaceMakerClass = Part::FaceMakerBullseye
  LengthFwd = 2.4
  LengthRev = 0
  Placement = pos=(101.3,29,65.23) rot=(0,1,0;1.5708rad)
  Solid = true
  Symmetric = false
FEATURE [Part::Box] Box011  label="frontCaseScrewPillarBracket"
  AttacherType = Attacher::AttachEngine3D
  Height = 2.4
  Length = 16
  Placement = pos=(87,28,2.3) rot=(0,0,1;0rad)
  Width = 7
FEATURE [Part::Box] Box012  label="frontCaseScrewPillarBracket001"
  AttacherType = Attacher::AttachEngine3D
  Height = 2.4
  Length = 16
  Placement = pos=(87,28,67.3) rot=(0,0,1;0rad)
  Width = 7
FEATURE [Sketcher::SketchObject] Sketch026
  FullyConstrained = true
  sketch-geometry (17):
    g0: Circle CenterX=-3.5 CenterY=23.5 CenterZ=0 NormalX=0 NormalY=0 NormalZ=1 AngleXU=0 Radius=1
    g1: Circle CenterX=-1 CenterY=15.25 CenterZ=0 NormalX=0 NormalY=0 NormalZ=1 AngleXU=0 Radius=1
    g2: Circle CenterX=-3.5 CenterY=7 CenterZ=0 NormalX=0 NormalY=0 NormalZ=1 AngleXU=0 Radius=1
    g3: BSplineCurve PolesCount=3 KnotsCount=2 Degree=2 IsPeriodic=0
    g4: GeomPoint X=-3.5 Y=23.5 Z=0
    g5: GeomPoint X=-3.5 Y=7 Z=0
    g6: Circle CenterX=-4.8 CenterY=30.5 CenterZ=0 NormalX=0 NormalY=0 NormalZ=1 AngleXU=0 Radius=1
    g7: Circle CenterX=-3.5 CenterY=30.5 CenterZ=0 NormalX=0 NormalY=0 NormalZ=1 AngleXU=0 Radius=1
    g8: Circle CenterX=-3.5 CenterY=29.2 CenterZ=0 NormalX=0 NormalY=0 NormalZ=1 AngleXU=0 Radius=1
    g9: BSplineCurve PolesCount=3 KnotsCount=2 Degree=2 IsPeriodic=0
    g10: GeomPoint X=-4.8 Y=30.5 Z=0
    g11: GeomPoint X=-3.5 Y=29.2 Z=0
    g12: LineSegment StartX=-3.5 StartY=29.2 StartZ=0 EndX=-3.5 EndY=23.5 EndZ=0
    g13: LineSegment StartX=-4.8 StartY=30.5 StartZ=0 EndX=0 EndY=30.5 EndZ=0
    g14: LineSegment StartX=-3.5 StartY=5 StartZ=0 EndX=-3.5 EndY=7 EndZ=0
    g15: LineSegment StartX=0 StartY=5 StartZ=0 EndX=0 EndY=30.5 EndZ=0
    g16: LineSegment StartX=-3.5 StartY=5 StartZ=0 EndX=0 EndY=5 EndZ=0
  constraints (33):
    c: Weight(g0) = 1
    c: Equal(g0,g1)
    c: Equal(g0,g2)
    c: InternalAlignment(g0,g3)
    c: InternalAlignment(g1,g3)
    c: InternalAlignment(g2,g3)
    c: InternalAlignment(g4,g3)
    c: InternalAlignment(g5,g3)
    c: Block(g3)
    c: Weight(g6) = 1
    c: Equal(g6,g7)
    c: Equal(g6,g8)
    c: InternalAlignment(g6,g9)
    c: InternalAlignment(g7,g9)
    c: InternalAlignment(g8,g9)
    c: InternalAlignment(g10,g9)
    c: InternalAlignment(g11,g9)
    c: Block(g9)
    c: Coincident(g12,g9)
    c: Coincident(g12,g3)
    c: Vertical(g12)
    c: Coincident(g13,g9)
    c: Horizontal(g13)
    c: Distance(g13) = 4.8
    c: Coincident(g14,g3)
    c: Vertical(g14)
    c: Coincident(g15,g13)
    c: Vertical(g15)
    c: Tangent(g15,g1)
    c: Distance(g14) = 2
    c: Coincident(g16,g14)
    c: Horizontal(g16)
    c: Coincident(g15,g16)
FEATURE [Part::Feature] Face050
  shape: bbox 4.8 x 25.5 x 2e-07 mm, 1 faces, 0 solids (baked)
FEATURE [Part::Revolution] Revolve054  label="moreFrontCaseScrewPost001"
  Angle = 360
  Axis = (0,1,0)
  Base = (0,0,0)
  FaceMakerClass = Part::FaceMakerBullseye
  Placement = pos=(102.5,4.5,3.5) rot=(0,0,1;0rad)
  Solid = false
  Source = -> Face050
  Symmetric = false
FEATURE [Part::Feature] Face051
  shape: bbox 4.8 x 25.5 x 2e-07 mm, 1 faces, 0 solids (baked)
FEATURE [Part::Revolution] Revolve055  label="moreFrontCaseScrewPost002"
  Angle = 360
  Axis = (0,1,0)
  Base = (0,0,0)
  FaceMakerClass = Part::FaceMakerBullseye
  Placement = pos=(102.5,4.5,68.5) rot=(0,0,1;0rad)
  Solid = false
  Source = -> Face051
  Symmetric = false
FEATURE [Sketcher::SketchObject] Sketch027
  FullyConstrained = true
  sketch-geometry (10):
    g0: LineSegment StartX=-1.6 StartY=4.7 StartZ=0 EndX=-1.6 EndY=1.7 EndZ=0
    g1: LineSegment StartX=-3.5 StartY=4.7 StartZ=0 EndX=-1.6 EndY=4.7 EndZ=0
    g2: LineSegment StartX=-1.6 StartY=1.7 StartZ=0 EndX=-1.6 EndY=1.5 EndZ=0
    g3: LineSegment StartX=-1.6 StartY=1.5 StartZ=0 EndX=-5.2 EndY=1.5 EndZ=0
    g4: Circle CenterX=-3.5 CenterY=4.7 CenterZ=0 NormalX=0 NormalY=0 NormalZ=1 AngleXU=0 Radius=1
    g5: Circle CenterX=-3.59627 CenterY=2.99743 CenterZ=0 NormalX=0 NormalY=0 NormalZ=1 AngleXU=0 Radius=1
    g6: Circle CenterX=-5.2 CenterY=1.5 CenterZ=0 NormalX=0 NormalY=0 NormalZ=1 AngleXU=0 Radius=1
    g7: BSplineCurve PolesCount=3 KnotsCount=2 Degree=2 IsPeriodic=0
    g8: GeomPoint X=-3.5 Y=4.7 Z=0
    g9: GeomPoint X=-5.2 Y=1.5 Z=0
  constraints (23):
    c: Vertical(g0)
    c: Distance(g0) = 3
    c: Coincident(g1,g0)
    c: Horizontal(g1)
    c: Block(g0)
    c: Block(g1)
    c: Coincident(g2,g0)
    c: Vertical(g2)
    c: Distance(g2) = 0.2
    c: Coincident(g3,g2)
    c: Horizontal(g3)
    c: Block(g3)
    c: Coincident(g7,g1)
    c: Weight(g4) = 1
    c: Equal(g4,g5)
    c: Equal(g4,g6)
    c: Coincident(g7,g3)
    c: InternalAlignment(g4,g7)
    c: InternalAlignment(g5,g7)
    c: InternalAlignment(g6,g7)
    c: InternalAlignment(g8,g7)
    c: InternalAlignment(g9,g7)
    c: Block(g7)
FEATURE [Sketcher::SketchObject] Sketch028
  FullyConstrained = true
  sketch-geometry (18):
    g0: LineSegment StartX=0 StartY=3e-16 StartZ=0 EndX=0 EndY=1.7 EndZ=0
    g1: LineSegment StartX=-3.5 StartY=0 StartZ=0 EndX=-3.5 EndY=0.9 EndZ=0
    g2: Circle CenterX=-2.7 CenterY=1.7 CenterZ=0 NormalX=0 NormalY=0 NormalZ=1 AngleXU=0 Radius=1
    g3: Circle CenterX=-3.5 CenterY=1.7 CenterZ=0 NormalX=0 NormalY=0 NormalZ=1 AngleXU=0 Radius=1
    g4: Circle CenterX=-3.5 CenterY=0.9 CenterZ=0 NormalX=0 NormalY=0 NormalZ=1 AngleXU=0 Radius=1
    g5: BSplineCurve PolesCount=3 KnotsCount=2 Degree=2 IsPeriodic=0
    g6: GeomPoint X=-2.7 Y=1.7 Z=0
    g7: GeomPoint X=-3.5 Y=0.9 Z=0
    g8: LineSegment StartX=-3.5 StartY=0 StartZ=0 EndX=-3.5 EndY=-7 EndZ=0
    g9: LineSegment StartX=0 StartY=3e-16 StartZ=0 EndX=0 EndY=-7 EndZ=0
    g10: LineSegment StartX=-3.5 StartY=-7 StartZ=0 EndX=0 EndY=-7 EndZ=0
    g11: LineSegment StartX=-2.7 StartY=1.7 StartZ=0 EndX=-1.6 EndY=1.7 EndZ=0
    g12: LineSegment StartX=0 StartY=1.7 StartZ=0 EndX=0 EndY=4.5 EndZ=0
    g13: LineSegment StartX=0 StartY=4.5 StartZ=0 EndX=0 EndY=10.8 EndZ=0
    g14: LineSegment StartX=0 StartY=10.8 StartZ=0 EndX=-2 EndY=10.8 EndZ=0
    g15: LineSegment StartX=-1.6 StartY=4.7 StartZ=0 EndX=-1.6 EndY=1.7 EndZ=0
    g16: LineSegment StartX=-1.6 StartY=4.7 StartZ=0 EndX=-2 EndY=4.7 EndZ=0
    g17: LineSegment StartX=-2 StartY=4.7 StartZ=0 EndX=-2 EndY=10.8 EndZ=0
  constraints (44):
    c: Vertical(g0)
    c: Vertical(g1)
    c: Distance(g1) = 0.9
    c: Block(g0)
    c: Distance(g0) = 1.7
    c: Weight(g2) = 1
    c: Equal(g2,g3)
    c: Equal(g2,g4)
    c: Coincident(g5,g1)
    c: InternalAlignment(g2,g5)
    c: InternalAlignment(g3,g5)
    c: InternalAlignment(g4,g5)
    c: InternalAlignment(g6,g5)
    c: InternalAlignment(g7,g5)
    c: Block(g5)
    c: Coincident(g8,g1)
    c: Vertical(g8)
    c: Distance(g8) = 7
    c: Vertical(g9)
    c: Equal(g8,g9) = 7
    c: Coincident(g9,g0)
    c: Coincident(g10,g8)
    c: Coincident(g10,g9)
    c: Horizontal(g10)
    c: Coincident(g11,g5)
    c: Horizontal(g11)
    c: Coincident(g12,g0)
    c: Vertical(g12)
    c: Distance(g12) = 2.8
    c: Coincident(g13,g12)
    c: Vertical(g13)
    c: Distance(g13) = 6.3
    c: Coincident(g14,g13)
    c: Horizontal(g14)
    c: Distance(g14) = 2
    c: Vertical(g15)
    c: Distance(g15) = 3
    c: Block(g11)
    c: Coincident(g15,g11)
    c: Coincident(g16,g15)
    c: Horizontal(g16)
    c: Coincident(g17,g16)
    c: Coincident(g17,g14)
    c: Vertical(g17)
FEATURE [Part::Revolution] Revolve040  label="backCaseScrewRetainer001"
  Angle = 360
  Axis = (0,1,0)
  Base = (0,0,0)
  FaceMakerClass = Part::FaceMakerBullseye
  Placement = pos=(12.5,3,10) rot=(0,0,1;0rad)
  Solid = false
  Source = -> Face036
  Symmetric = false
FEATURE [Part::Feature] Face055
  shape: bbox 3.5 x 30.2 x 2e-07 mm, 1 faces, 0 solids (baked)
FEATURE [Part::Revolution] Revolve059  label="backCaseScrewPost"
  Angle = 360
  Axis = (0,1,0)
  Base = (0,0,0)
  FaceMakerClass = Part::FaceMakerBullseye
  Placement = pos=(12.5,4.5,10) rot=(0,0,1;0rad)
  Solid = false
  Source = -> Face055
  Symmetric = false
FEATURE [Part::Feature] Face056
  shape: bbox 3.5 x 30.2 x 2e-07 mm, 1 faces, 0 solids (baked)
FEATURE [Part::Revolution] Revolve060  label="backCaseScrewPost001"
  Angle = 360
  Axis = (0,1,0)
  Base = (0,0,0)
  FaceMakerClass = Part::FaceMakerBullseye
  Placement = pos=(12.5,4.5,62) rot=(0,0,1;0rad)
  Solid = false
  Source = -> Face056
  Symmetric = false
FEATURE [Part::Feature] Face057
  shape: bbox 3.5 x 17.8 x 2e-07 mm, 1 faces, 0 solids (baked)
FEATURE [Part::Revolution] Revolve061  label="removeToCreateScrewAndThreadedInsertHole"
  Angle = 360
  Axis = (0,1,0)
  Base = (0,0,0)
  FaceMakerClass = Part::FaceMakerBullseye
  Placement = pos=(12.5,0,10) rot=(0,0,1;0rad)
  Solid = false
  Source = -> Face057
  Symmetric = false
FEATURE [Part::Feature] Face058
  shape: bbox 3.5 x 17.8 x 2e-07 mm, 1 faces, 0 solids (baked)
FEATURE [Part::Revolution] Revolve062  label="removeToCreateScrewAndThreadedInsertHole001"
  Angle = 360
  Axis = (0,1,0)
  Base = (0,0,0)
  FaceMakerClass = Part::FaceMakerBullseye
  Placement = pos=(12.5,0,62) rot=(0,0,1;0rad)
  Solid = false
  Source = -> Face058
  Symmetric = false
FEATURE [Part::Feature] Face059
  shape: bbox 3.5 x 17.8 x 2e-07 mm, 1 faces, 0 solids (baked)
FEATURE [Part::Revolution] Revolve063  label="removeToCreateScrewAndThreadedInsertHole002"
  Angle = 360
  Axis = (0,1,0)
  Base = (0,0,0)
  FaceMakerClass = Part::FaceMakerBullseye
  Placement = pos=(89.5,0,68.5) rot=(0,0,1;0rad)
  Solid = false
  Source = -> Face059
  Symmetric = false
FEATURE [Part::Feature] Face060
  shape: bbox 3.5 x 17.8 x 2e-07 mm, 1 faces, 0 solids (baked)
FEATURE [Part::Revolution] Revolve064  label="removeToCreateScrewAndThreadedInsertHole003"
  Angle = 360
  Axis = (0,1,0)
  Base = (0,0,0)
  FaceMakerClass = Part::FaceMakerBullseye
  Placement = pos=(89.5,0,3.5) rot=(0,0,1;0rad)
  Solid = false
  Source = -> Face060
  Symmetric = false
FEATURE [Part::Feature] Face061
  shape: bbox 3.5 x 17.8 x 2e-07 mm, 1 faces, 0 solids (baked)
FEATURE [Part::Revolution] Revolve065  label="removeToCreateScrewAndThreadedInsertHole004"
  Angle = 360
  Axis = (0,1,0)
  Base = (0,0,0)
  FaceMakerClass = Part::FaceMakerBullseye
  Placement = pos=(102.5,4.7,3.5) rot=(0,0,1;0rad)
  Solid = false
  Source = -> Face061
  Symmetric = false
FEATURE [Part::Feature] Face062
  shape: bbox 3.5 x 17.8 x 2e-07 mm, 1 faces, 0 solids (baked)
FEATURE [Part::Revolution] Revolve066  label="removeToCreateScrewAndThreadedInsertHole005"
  Angle = 360
  Axis = (0,1,0)
  Base = (0,0,0)
  FaceMakerClass = Part::FaceMakerBullseye
  Placement = pos=(102.5,4.7,68.5) rot=(0,0,1;0rad)
  Solid = false
  Source = -> Face062
  Symmetric = false
FEATURE [Part::MultiFuse] Fusion047  label="makeHoles"
  Shapes = -> [Revolve066,Revolve065,Revolve064,Revolve063,Revolve062,Revolve061]
FEATURE [Part::Feature] Face063
  shape: bbox 3.6 x 3.2 x 2e-07 mm, 1 faces, 0 solids (baked)
FEATURE [Part::Revolution] Revolve067  label="moreFrontCaseScrewRetainer002"
  Angle = 360
  Axis = (0,1,0)
  Base = (0,0,0)
  FaceMakerClass = Part::FaceMakerBullseye
  Placement = pos=(102.5,4.5,68.5) rot=(0,0,1;0rad)
  Solid = false
  Source = -> Face063
  Symmetric = false
FEATURE [Part::Feature] Face064
  shape: bbox 3.6 x 3.2 x 2e-07 mm, 1 faces, 0 solids (baked)
FEATURE [Part::Revolution] Revolve068  label="moreFrontCaseScrewRetainer003"
  Angle = 360
  Axis = (0,1,0)
  Base = (0,0,0)
  FaceMakerClass = Part::FaceMakerBullseye
  Placement = pos=(102.5,4.5,3.5) rot=(0,0,1;0rad)
  Solid = false
  Source = -> Face064
  Symmetric = false
FEATURE [Part::Feature] Face065
  shape: bbox 3.5 x 17.8 x 2e-07 mm, 1 faces, 0 solids (baked)
FEATURE [Part::Revolution] Revolve069  label="removeToCreateScrewAndThreadedInsertHole006"
  Angle = 360
  Axis = (0,1,0)
  Base = (0,0,0)
  FaceMakerClass = Part::FaceMakerBullseye
  Placement = pos=(12.5,0,10) rot=(0,0,1;0rad)
  Solid = false
  Source = -> Face065
  Symmetric = false
FEATURE [Part::Feature] Face066
  shape: bbox 3.5 x 17.8 x 2e-07 mm, 1 faces, 0 solids (baked)
FEATURE [Part::Revolution] Revolve070  label="removeToCreateScrewAndThreadedInsertHole007"
  Angle = 360
  Axis = (0,1,0)
  Base = (0,0,0)
  FaceMakerClass = Part::FaceMakerBullseye
  Placement = pos=(12.5,0,62) rot=(0,0,1;0rad)
  Solid = false
  Source = -> Face066
  Symmetric = false
FEATURE [Part::Feature] Face067
  shape: bbox 3.5 x 17.8 x 2e-07 mm, 1 faces, 0 solids (baked)
FEATURE [Part::Revolution] Revolve071  label="removeToCreateScrewAndThreadedInsertHole008"
  Angle = 360
  Axis = (0,1,0)
  Base = (0,0,0)
  FaceMakerClass = Part::FaceMakerBullseye
  Placement = pos=(89.5,0,68.5) rot=(0,0,1;0rad)
  Solid = false
  Source = -> Face067
  Symmetric = false
FEATURE [Part::Feature] Face068
  shape: bbox 3.5 x 17.8 x 2e-07 mm, 1 faces, 0 solids (baked)
FEATURE [Part::Revolution] Revolve072  label="removeToCreateScrewAndThreadedInsertHole009"
  Angle = 360
  Axis = (0,1,0)
  Base = (0,0,0)
  FaceMakerClass = Part::FaceMakerBullseye
  Placement = pos=(89.5,0,3.5) rot=(0,0,1;0rad)
  Solid = false
  Source = -> Face068
  Symmetric = false
FEATURE [Part::Feature] Face069
  shape: bbox 3.5 x 17.8 x 2e-07 mm, 1 faces, 0 solids (baked)
FEATURE [Part::Feature] Face070
  shape: bbox 3.5 x 17.8 x 2e-07 mm, 1 faces, 0 solids (baked)
FEATURE [Part::Revolution] Revolve073  label="removeToCreateScrewAndThreadedInsertHole010"
  Angle = 360
  Axis = (0,1,0)
  Base = (0,0,0)
  FaceMakerClass = Part::FaceMakerBullseye
  Placement = pos=(102.5,4.7,3.5) rot=(0,0,1;0rad)
  Solid = false
  Source = -> Face069
  Symmetric = false
FEATURE [Part::Revolution] Revolve074  label="removeToCreateScrewAndThreadedInsertHole011"
  Angle = 360
  Axis = (0,1,0)
  Base = (0,0,0)
  FaceMakerClass = Part::FaceMakerBullseye
  Placement = pos=(102.5,4.7,68.5) rot=(0,0,1;0rad)
  Solid = false
  Source = -> Face070
  Symmetric = false
FEATURE [Part::MultiFuse] Fusion048  label="makeHoles001"
  Shapes = -> [Revolve074,Revolve073,Revolve072,Revolve071,Revolve070,Revolve069]
FEATURE [Part::MultiFuse] Fusion049  label="caseScrewRetainers"
  Shapes = -> [Revolve067,Revolve068,Revolve048,Revolve047,Revolve039,Revolve040]
FEATURE [Part::Cut] Cut015  label="caseScrewRetainers001"
  Base = -> Fusion049
  Tool = -> Fusion048
FEATURE [Part::MultiFuse] Fusion050  label="casePillars"
  Shapes = -> [Revolve055,Revolve054,Revolve043,Revolve046,Revolve059,Revolve060]
FEATURE [Part::Feature] Face071 .. Face076  x6 (patterned run collapsed; names and placements below)
  shape: bbox 3.5 x 17.8 x 2e-07 mm, 1 faces, 0 solids (baked)
FEATURE [Part::Revolution] Revolve075  label="removeToCreateScrewAndThreadedInsertHole012"
  Angle = 360
  Axis = (0,1,0)
  Base = (0,0,0)
  FaceMakerClass = Part::FaceMakerBullseye
  Placement = pos=(12.5,0,10) rot=(0,0,1;0rad)
  Solid = false
  Source = -> Face071
  Symmetric = false
FEATURE [Part::Revolution] Revolve076  label="removeToCreateScrewAndThreadedInsertHole013"
  Angle = 360
  Axis = (0,1,0)
  Base = (0,0,0)
  FaceMakerClass = Part::FaceMakerBullseye
  Placement = pos=(12.5,0,62) rot=(0,0,1;0rad)
  Solid = false
  Source = -> Face072
  Symmetric = false
FEATURE [Part::Revolution] Revolve077  label="removeToCreateScrewAndThreadedInsertHole014"
  Angle = 360
  Axis = (0,1,0)
  Base = (0,0,0)
  FaceMakerClass = Part::FaceMakerBullseye
  Placement = pos=(89.5,0,68.5) rot=(0,0,1;0rad)
  Solid = false
  Source = -> Face073
  Symmetric = false
FEATURE [Part::Revolution] Revolve078  label="removeToCreateScrewAndThreadedInsertHole015"
  Angle = 360
  Axis = (0,1,0)
  Base = (0,0,0)
  FaceMakerClass = Part::FaceMakerBullseye
  Placement = pos=(89.5,0,3.5) rot=(0,0,1;0rad)
  Solid = false
  Source = -> Face074
  Symmetric = false
FEATURE [Part::Revolution] Revolve079  label="removeToCreateScrewAndThreadedInsertHole016"
  Angle = 360
  Axis = (0,1,0)
  Base = (0,0,0)
  FaceMakerClass = Part::FaceMakerBullseye
  Placement = pos=(102.5,4.7,3.5) rot=(0,0,1;0rad)
  Solid = false
  Source = -> Face075
  Symmetric = false
FEATURE [Part::Revolution] Revolve080  label="removeToCreateScrewAndThreadedInsertHole017"
  Angle = 360
  Axis = (0,1,0)
  Base = (0,0,0)
  FaceMakerClass = Part::FaceMakerBullseye
  Placement = pos=(102.5,4.7,68.5) rot=(0,0,1;0rad)
  Solid = false
  Source = -> Face076
  Symmetric = false
FEATURE [Part::MultiFuse] Fusion051  label="makeHoles002"
  Shapes = -> [Revolve080,Revolve079,Revolve078,Revolve077,Revolve076,Revolve075]
FEATURE [Part::Cut] Cut016  label="caesPillars"
  Base = -> Fusion050
  Tool = -> Fusion051
FEATURE [Part::Revolution] Revolve009  label="plugHousing016"
  Angle = 360
  Axis = (0,1,0)
  Base = (0,0,0)
  FaceMakerClass = Part::FaceMakerBullseye
  Placement = pos=(0,0,36.15) rot=(0,0,1;0rad)
  Solid = false
  Source = -> Face012
  Symmetric = false
FEATURE [Part::MultiFuse] Fusion014  label="plugHousing023"
  Placement = pos=(0,0,0) rot=(0,0,1;1.5708rad)
  Shapes = -> [Revolve011,Revolve009]
FEATURE [Part::Revolution] Revolve010  label="plugHousing017"
  Angle = 360
  Axis = (0,1,0)
  Base = (0,0,0)
  FaceMakerClass = Part::FaceMakerBullseye
  Placement = pos=(0,0,36.15) rot=(0,0,1;0rad)
  Solid = false
  Source = -> Face014
  Symmetric = false
FEATURE [Part::MultiFuse] Fusion015  label="plugHousing024"
  Placement = pos=(0,0,0) rot=(0,0,1;1.5708rad)
  Shapes = -> [Revolve010,Revolve015]
FEATURE [Part::Revolution] Revolve014  label="plugHousing026"
  Angle = 360
  Axis = (0,1,0)
  Base = (0,0,0)
  FaceMakerClass = Part::FaceMakerBullseye
  Placement = pos=(0,0,36.15) rot=(0,0,1;0rad)
  Solid = false
  Source = -> Face011
  Symmetric = false
FEATURE [Part::Revolution] Revolve013  label="plugHousing025"
  Angle = 360
  Axis = (0,1,0)
  Base = (0,0,0)
  FaceMakerClass = Part::FaceMakerBullseye
  Placement = pos=(0,0,36.15) rot=(0,0,1;0rad)
  Solid = false
  Source = -> Face015
  Symmetric = false
FEATURE [Part::MultiFuse] Fusion016  label="plugHousing028"
  Placement = pos=(0,19,0) rot=(0,0,1;3.14159rad)
  Shapes = -> [Fusion014,Fusion013]
FEATURE [Part::MultiFuse] Fusion011  label="plugHousing018"
  Placement = pos=(0,0,0) rot=(0,0,1;1.5708rad)
  Shapes = -> [Revolve014,Revolve013]
FEATURE [Part::MultiFuse] Fusion012  label="plugHousing019"
  Placement = pos=(0,19,0) rot=(0,0,1;3.14159rad)
  Shapes = -> [Fusion011,Fusion015]
FEATURE [Part::MultiFuse] Fusion017  label="plugHousing029"
  Placement = pos=(122.621,0,-0.15) rot=(0,0,1;0rad)
  Shapes = -> [Fusion016,Fusion012]
FEATURE [Part::MultiFuse] Fusion052  label="casePillarRetainers"
  Shapes = -> [Extrude012,Extrude013,Extrude014,Extrude015,Extrude016,Extrude017,Extrude018,Extrude019,Box011,Box012]
FEATURE [Part::Feature] Face077
  shape: bbox 3.5 x 17.8 x 2e-07 mm, 1 faces, 0 solids (baked)
FEATURE [Part::Revolution] Revolve081  label="removeToCreateScrewAndThreadedInsertHole018"
  Angle = 360
  Axis = (0,1,0)
  Base = (0,0,0)
  FaceMakerClass = Part::FaceMakerBullseye
  Placement = pos=(62.3,30.3,19.7) rot=(0,0,1;0rad)
  Solid = false
  Source = -> Face077
  Symmetric = false
FEATURE [Part::Feature] Face078
  shape: bbox 3.5 x 17.8 x 2e-07 mm, 1 faces, 0 solids (baked)
FEATURE [Part::Revolution] Revolve082  label="removeToCreateScrewAndThreadedInsertHole019"
  Angle = 360
  Axis = (0,1,0)
  Base = (0,0,0)
  FaceMakerClass = Part::FaceMakerBullseye
  Placement = pos=(62.3,30.3,51.7) rot=(0,0,1;0rad)
  Solid = false
  Source = -> Face078
  Symmetric = false
FEATURE [Part::Feature] Face079
  shape: bbox 3.5 x 17.8 x 2e-07 mm, 1 faces, 0 solids (baked)
FEATURE [Part::Revolution] Revolve083  label="removeToCreateScrewAndThreadedInsertHole020"
  Angle = 360
  Axis = (0,1,0)
  Base = (0,0,0)
  FaceMakerClass = Part::FaceMakerBullseye
  Placement = pos=(30.3,30.3,19.7) rot=(0,0,1;0rad)
  Solid = false
  Source = -> Face079
  Symmetric = false
FEATURE [Part::Feature] Face080
  shape: bbox 3.5 x 17.8 x 2e-07 mm, 1 faces, 0 solids (baked)
FEATURE [Part::Revolution] Revolve084  label="removeToCreateScrewAndThreadedInsertHole021"
  Angle = 360
  Axis = (0,1,0)
  Base = (0,0,0)
  FaceMakerClass = Part::FaceMakerBullseye
  Placement = pos=(30.3,30.3,51.7) rot=(0,0,1;0rad)
  Solid = false
  Source = -> Face080
  Symmetric = false
FEATURE [Part::MultiFuse] Fusion053  label="createThreadedInsertHolesForFan"
  Shapes = -> [Revolve081,Revolve082,Revolve083,Revolve084]
FEATURE [Part::Cut] Cut017  label="fanScrewHousing001"
  Base = -> Fusion046
  Tool = -> Fusion053
FEATURE [Part::Feature] Face081
  shape: bbox 3.5 x 17.8 x 2e-07 mm, 1 faces, 0 solids (baked)
FEATURE [Part::Revolution] Revolve085  label="removeToCreateScrewAndThreadedInsertHole022"
  Angle = 360
  Axis = (0,1,0)
  Base = (0,0,0)
  FaceMakerClass = Part::FaceMakerBullseye
  Placement = pos=(62.3,30.3,19.7) rot=(0,0,1;0rad)
  Solid = false
  Source = -> Face081
  Symmetric = false
FEATURE [Part::Feature] Face082
  shape: bbox 3.5 x 17.8 x 2e-07 mm, 1 faces, 0 solids (baked)
FEATURE [Part::Revolution] Revolve086  label="removeToCreateScrewAndThreadedInsertHole023"
  Angle = 360
  Axis = (0,1,0)
  Base = (0,0,0)
  FaceMakerClass = Part::FaceMakerBullseye
  Placement = pos=(62.3,30.3,51.7) rot=(0,0,1;0rad)
  Solid = false
  Source = -> Face082
  Symmetric = false
FEATURE [Part::Feature] Face083
  shape: bbox 3.5 x 17.8 x 2e-07 mm, 1 faces, 0 solids (baked)
FEATURE [Part::Revolution] Revolve087  label="removeToCreateScrewAndThreadedInsertHole024"
  Angle = 360
  Axis = (0,1,0)
  Base = (0,0,0)
  FaceMakerClass = Part::FaceMakerBullseye
  Placement = pos=(30.3,30.3,19.7) rot=(0,0,1;0rad)
  Solid = false
  Source = -> Face083
  Symmetric = false
FEATURE [Part::Feature] Face084
  shape: bbox 3.5 x 17.8 x 2e-07 mm, 1 faces, 0 solids (baked)
FEATURE [Part::Revolution] Revolve088  label="removeToCreateScrewAndThreadedInsertHole025"
  Angle = 360
  Axis = (0,1,0)
  Base = (0,0,0)
  FaceMakerClass = Part::FaceMakerBullseye
  Placement = pos=(30.3,30.3,51.7) rot=(0,0,1;0rad)
  Solid = false
  Source = -> Face084
  Symmetric = false
FEATURE [Part::MultiFuse] Fusion054  label="createThreadedInsertHolesForFan001"
  Shapes = -> [Revolve085,Revolve086,Revolve087,Revolve088]
FEATURE [Part::Cut] Cut018  label="top007"
  Base = -> Fusion040
  Tool = -> Fusion054
FEATURE [Sketcher::SketchObject] Sketch029
  FullyConstrained = false
  Placement = pos=(0,0,0) rot=(1,0,0;1.5708rad)
  sketch-geometry (24):
    g0: ArcOfCircle CenterX=-4 CenterY=-10.5 CenterZ=0 NormalX=0 NormalY=0 NormalZ=1 AngleXU=0 Radius=1.5 StartAngle=6e-16 EndAngle=3.14159
    g1: ArcOfCircle CenterX=-34.2 CenterY=-10.5 CenterZ=0 NormalX=0 NormalY=0 NormalZ=1 AngleXU=0 Radius=1.5 StartAngle=0 EndAngle=3.14159
    g2: ArcOfCircle CenterX=-34.2 CenterY=-27.7 CenterZ=0 NormalX=0 NormalY=0 NormalZ=1 AngleXU=0 Radius=1.5 StartAngle=3.14159 EndAngle=6.28319
    g3: ArcOfCircle CenterX=-4 CenterY=-27.7 CenterZ=0 NormalX=0 NormalY=0 NormalZ=1 AngleXU=0 Radius=1.5 StartAngle=3.1416 EndAngle=6.28319
    g4: ArcOfCircle CenterX=-10 CenterY=-4.3 CenterZ=0 NormalX=0 NormalY=0 NormalZ=1 AngleXU=0 Radius=1.5 StartAngle=2e-16 EndAngle=3.14159
    g5: ArcOfCircle CenterX=-16.1 CenterY=-1.8 CenterZ=0 NormalX=0 NormalY=0 NormalZ=1 AngleXU=0 Radius=1.5 StartAngle=5e-16 EndAngle=3.14159
    g6: ArcOfCircle CenterX=-22.1 CenterY=-1.8 CenterZ=0 NormalX=0 NormalY=0 NormalZ=1 AngleXU=0 Radius=1.5 StartAngle=5e-16 EndAngle=3.14159
    g7: ArcOfCircle CenterX=-28.2 CenterY=-4.3 CenterZ=0 NormalX=0 NormalY=0 NormalZ=1 AngleXU=0 Radius=1.5 StartAngle=2e-16 EndAngle=3.14159
    g8: ArcOfCircle CenterX=-10 CenterY=-33.9 CenterZ=0 NormalX=0 NormalY=0 NormalZ=1 AngleXU=0 Radius=1.5 StartAngle=3.14159 EndAngle=6.28319
    g9: ArcOfCircle CenterX=-16.1 CenterY=-36.4 CenterZ=0 NormalX=0 NormalY=0 NormalZ=1 AngleXU=0 Radius=1.5 StartAngle=3.14159 EndAngle=6.28319
    g10: ArcOfCircle CenterX=-22.1 CenterY=-36.4 CenterZ=0 NormalX=0 NormalY=0 NormalZ=1 AngleXU=0 Radius=1.5 StartAngle=3.14159 EndAngle=6.28319
    g11: ArcOfCircle CenterX=-28.2 CenterY=-33.9 CenterZ=0 NormalX=0 NormalY=0 NormalZ=1 AngleXU=0 Radius=1.5 StartAngle=3.14159 EndAngle=6.28319
    g12: LineSegment StartX=-35.7 StartY=-10.5 StartZ=0 EndX=-35.7 EndY=-27.7 EndZ=0
    g13: LineSegment StartX=-32.7 StartY=-10.5 StartZ=0 EndX=-32.7 EndY=-27.7 EndZ=0
    g14: LineSegment StartX=-29.7 StartY=-33.9 StartZ=0 EndX=-29.7 EndY=-4.3 EndZ=0
    g15: LineSegment StartX=-26.7 StartY=-33.9 StartZ=0 EndX=-26.7 EndY=-4.3 EndZ=0
    g16: LineSegment StartX=-2.5 StartY=-10.5 StartZ=0 EndX=-2.5 EndY=-27.7 EndZ=0
    g17: LineSegment StartX=-8.5 StartY=-4.3 StartZ=0 EndX=-8.5 EndY=-33.9 EndZ=0
    g18: LineSegment StartX=-5.5 StartY=-10.5 StartZ=0 EndX=-5.5 EndY=-27.7 EndZ=0
    g19: LineSegment StartX=-11.5 StartY=-4.3 StartZ=0 EndX=-11.5 EndY=-33.9 EndZ=0
    g20: LineSegment StartX=-14.6 StartY=-1.8 StartZ=0 EndX=-14.6 EndY=-36.4 EndZ=0
    g21: LineSegment StartX=-17.6 StartY=-1.8 StartZ=0 EndX=-17.6 EndY=-36.4 EndZ=0
    g22: LineSegment StartX=-20.6 StartY=-36.4 StartZ=0 EndX=-20.6 EndY=-1.8 EndZ=0
    g23: LineSegment StartX=-23.6 StartY=-1.8 StartZ=0 EndX=-23.6 EndY=-36.4 EndZ=0
  constraints (48):
    c: Block(g0)
    c: Block(g1)
    c: Block(g2)
    c: Block(g3)
    c: Block(g4)
    c: Block(g5)
    c: Block(g6)
    c: Block(g7)
    c: Block(g8)
    c: Block(g9)
    c: Block(g10)
    c: Block(g11)
    c: Coincident(g12,g1)
    c: Coincident(g12,g2)
    c: Vertical(g12)
    c: Coincident(g13,g1)
    c: Coincident(g13,g2)
    c: Vertical(g13)
    c: Coincident(g14,g11)
    c: Coincident(g14,g7)
    c: Vertical(g14)
    c: Coincident(g15,g11)
    c: Coincident(g15,g7)
    c: Vertical(g15)
    c: Coincident(g16,g0)
    c: Coincident(g16,g3)
    c: Vertical(g16)
    c: Coincident(g17,g4)
    c: Coincident(g17,g8)
    c: Vertical(g17)
    c: Coincident(g18,g0)
    c: Coincident(g18,g3)
    c: Vertical(g18)
    c: Coincident(g19,g4)
    c: Coincident(g19,g8)
    c: Vertical(g19)
    c: Coincident(g20,g5)
    c: Coincident(g20,g9)
    c: Vertical(g20)
    c: Coincident(g21,g5)
    c: Coincident(g21,g9)
    c: Vertical(g21)
    c: Coincident(g22,g10)
    c: Coincident(g22,g6)
    c: Vertical(g22)
    c: Coincident(g23,g6)
    c: Coincident(g23,g10)
    c: Vertical(g23)
FEATURE [Part::Extrusion] Extrude020  label="removeToCreateFanGrillHoles"
  Base = -> Sketch029
  Dir = (0,-1,6e-16)
  DirMode = 2
  FaceMakerClass = Part::FaceMakerBullseye
  LengthFwd = 10
  LengthRev = 0
  Placement = pos=(65.4,44,54.82) rot=(0,0,1;0rad)
  Solid = true
  Symmetric = false
FEATURE [Part::MultiFuse] Fusion055  label="top008"
  Shapes = -> [Cut017,Cut018]
FEATURE [Part::Cut] Cut019  label="top009"
  Base = -> Fusion055
  Tool = -> Extrude020
FEATURE [App::MeasureDistance] Distance003  label="Distance: 71.95 mm"
  Distance = 71.9513
  P1 = (117,38,72)
  P2 = (117,38,0.0487319)
FEATURE [Sketcher::SketchObject] Sketch030
  FullyConstrained = true
  Placement = pos=(117,19,0) rot=(0.57735,0.57735,0.57735;2.0944rad)
  sketch-geometry (48):
    g0: LineSegment StartX=-49.19 StartY=69.25 StartZ=0 EndX=-49.19 EndY=66.25 EndZ=0
    g1: LineSegment StartX=-49.19 StartY=63.5 StartZ=0 EndX=-49.19 EndY=60.5 EndZ=0
    g2: LineSegment StartX=-49.19 StartY=57.75 StartZ=0 EndX=-49.19 EndY=54.75 EndZ=0
    g3: LineSegment StartX=-49.19 StartY=52 StartZ=0 EndX=-49.19 EndY=49 EndZ=0
    g4: LineSegment StartX=-49.19 StartY=46.25 StartZ=0 EndX=-49.19 EndY=43.25 EndZ=0
    g5: LineSegment StartX=-49.19 StartY=40.5 StartZ=0 EndX=-49.19 EndY=37.5 EndZ=0
    g6: LineSegment StartX=-49.19 StartY=34.5 StartZ=0 EndX=-49.19 EndY=31.5 EndZ=0
    g7: LineSegment StartX=-49.19 StartY=28.75 StartZ=0 EndX=-49.19 EndY=25.75 EndZ=0
    g8: LineSegment StartX=-49.19 StartY=23 StartZ=0 EndX=-49.19 EndY=20 EndZ=0
    g9: LineSegment StartX=-49.19 StartY=17.25 StartZ=0 EndX=-49.19 EndY=14.25 EndZ=0
    g10: LineSegment StartX=-49.19 StartY=11.5 StartZ=0 EndX=-49.19 EndY=8.5 EndZ=0
    g11: LineSegment StartX=-49.19 StartY=5.75 StartZ=0 EndX=-49.19 EndY=2.75 EndZ=0
    g12: ArcOfCircle CenterX=-1.5 CenterY=67.75 CenterZ=0 NormalX=0 NormalY=0 NormalZ=1 AngleXU=0 Radius=1.5 StartAngle=4.71239 EndAngle=7.85398
    g13: ArcOfCircle CenterX=-1.5 CenterY=62 CenterZ=0 NormalX=0 NormalY=0 NormalZ=1 AngleXU=0 Radius=1.5 StartAngle=4.71239 EndAngle=7.85398
    g14: ArcOfCircle CenterX=-1.5 CenterY=56.25 CenterZ=0 NormalX=0 NormalY=0 NormalZ=1 AngleXU=0 Radius=1.5 StartAngle=4.71239 EndAngle=7.85398
    g15: ArcOfCircle CenterX=-11.49 CenterY=50.5 CenterZ=0 NormalX=0 NormalY=0 NormalZ=1 AngleXU=0 Radius=1.5 StartAngle=4.71239 EndAngle=7.85398
    g16: ArcOfCircle CenterX=-16.28 CenterY=44.75 CenterZ=0 NormalX=0 NormalY=0 NormalZ=1 AngleXU=0 Radius=1.5 StartAngle=4.71239 EndAngle=7.85398
    g17: ArcOfCircle CenterX=-18.2337 CenterY=39 CenterZ=0 NormalX=0 NormalY=0 NormalZ=1 AngleXU=0 Radius=1.5 StartAngle=4.71485 EndAngle=7.85398
    g18: ArcOfCircle CenterX=-16.2837 CenterY=27.25 CenterZ=0 NormalX=0 NormalY=0 NormalZ=1 AngleXU=0 Radius=1.5 StartAngle=4.71485 EndAngle=7.85398
    g19: ArcOfCircle CenterX=-18.2337 CenterY=33 CenterZ=0 NormalX=0 NormalY=0 NormalZ=1 AngleXU=0 Radius=1.5 StartAngle=4.71485 EndAngle=7.85398
    g20: ArcOfCircle CenterX=-11.49 CenterY=21.5 CenterZ=0 NormalX=0 NormalY=0 NormalZ=1 AngleXU=0 Radius=1.5 StartAngle=4.71239 EndAngle=7.85398
    g21: ArcOfCircle CenterX=-1.5 CenterY=4.25 CenterZ=0 NormalX=0 NormalY=0 NormalZ=1 AngleXU=0 Radius=1.5 StartAngle=4.71239 EndAngle=7.85398
    g22: ArcOfCircle CenterX=-1.5 CenterY=10 CenterZ=0 NormalX=0 NormalY=0 NormalZ=1 AngleXU=0 Radius=1.5 StartAngle=4.71239 EndAngle=7.85398
    g23: ArcOfCircle CenterX=-1.5 CenterY=15.75 CenterZ=0 NormalX=0 NormalY=0 NormalZ=1 AngleXU=0 Radius=1.5 StartAngle=4.71239 EndAngle=7.85398
    g24: LineSegment StartX=-49.19 StartY=69.25 StartZ=0 EndX=-1.5 EndY=69.25 EndZ=0
    g25: LineSegment StartX=-49.19 StartY=66.25 StartZ=0 EndX=-1.5 EndY=66.25 EndZ=0
    g26: LineSegment StartX=-49.19 StartY=63.5 StartZ=0 EndX=-1.5 EndY=63.5 EndZ=0
    g27: LineSegment StartX=-49.19 StartY=60.5 StartZ=0 EndX=-1.5 EndY=60.5 EndZ=0
    g28: LineSegment StartX=-49.19 StartY=57.75 StartZ=0 EndX=-1.5 EndY=57.75 EndZ=0
    g29: LineSegment StartX=-49.19 StartY=54.75 StartZ=0 EndX=-1.5 EndY=54.75 EndZ=0
    g30: LineSegment StartX=-49.19 StartY=52 StartZ=0 EndX=-11.49 EndY=52 EndZ=0
    g31: LineSegment StartX=-49.19 StartY=49 StartZ=0 EndX=-11.49 EndY=49 EndZ=0
    g32: LineSegment StartX=-49.19 StartY=46.25 StartZ=0 EndX=-16.28 EndY=46.25 EndZ=0
    g33: LineSegment StartX=-49.19 StartY=43.25 StartZ=0 EndX=-16.28 EndY=43.25 EndZ=0
    g34: LineSegment StartX=-49.19 StartY=40.5 StartZ=0 EndX=-18.2337 EndY=40.5 EndZ=0
    g35: LineSegment StartX=-49.19 StartY=37.5 StartZ=0 EndX=-18.23 EndY=37.5 EndZ=0
    g36: LineSegment StartX=-49.19 StartY=34.5 StartZ=0 EndX=-18.2337 EndY=34.5 EndZ=0
    g37: LineSegment StartX=-49.19 StartY=31.5 StartZ=0 EndX=-18.23 EndY=31.5 EndZ=0
    g38: LineSegment StartX=-49.19 StartY=28.75 StartZ=0 EndX=-16.2837 EndY=28.75 EndZ=0
    g39: LineSegment StartX=-49.19 StartY=25.75 StartZ=0 EndX=-16.28 EndY=25.75 EndZ=0
    g40: LineSegment StartX=-49.19 StartY=23 StartZ=0 EndX=-11.49 EndY=23 EndZ=0
    g41: LineSegment StartX=-49.19 StartY=20 StartZ=0 EndX=-11.49 EndY=20 EndZ=0
    g42: LineSegment StartX=-49.19 StartY=17.25 StartZ=0 EndX=-1.5 EndY=17.25 EndZ=0
    g43: LineSegment StartX=-49.19 StartY=14.25 StartZ=0 EndX=-1.5 EndY=14.25 EndZ=0
    g44: LineSegment StartX=-49.19 StartY=11.5 StartZ=0 EndX=-1.5 EndY=11.5 EndZ=0
    g45: LineSegment StartX=-49.19 StartY=8.5 StartZ=0 EndX=-1.5 EndY=8.5 EndZ=0
    g46: LineSegment StartX=-49.19 StartY=5.75 StartZ=0 EndX=-1.5 EndY=5.75 EndZ=0
    g47: LineSegment StartX=-49.19 StartY=2.75 StartZ=0 EndX=-1.5 EndY=2.75 EndZ=0
  constraints (120):
    c: Vertical(g0)
    c: Distance(g0) = 3
    c: Block(g0)
    c: Vertical(g1)
    c: Distance(g1) = 3
    c: Vertical(g2)
    c: Equal(g0,g2) = 3
    c: Block(g2)
    c: Vertical(g3)
    c: Equal(g1,g3) = 3
    c: Vertical(g4)
    c: Equal(g0,g4) = 3
    c: Block(g4)
    c: Vertical(g5)
    c: Equal(g1,g5) = 3
    c: Vertical(g6)
    c: Equal(g0,g6) = 3
    c: Block(g6)
    c: Vertical(g7)
    c: Equal(g1,g7) = 3
    c: Vertical(g8)
    c: Equal(g0,g8) = 3
    c: Block(g8)
    c: Vertical(g9)
    c: Equal(g1,g9) = 3
    c: Vertical(g10)
    c: Equal(g0,g10) = 3
    c: Block(g10)
    c: Vertical(g11)
    c: Equal(g1,g11) = 3
    c: Block(g12)
    c: Block(g13)
    c: Block(g14)
    c: Block(g15)
    c: Block(g16)
    c: Block(g17)
    c: Block(g18)
    c: Block(g19)
    c: Block(g20)
    c: Block(g21)
    c: Block(g22)
    c: Block(g23)
    c: Block(g11)
    c: Block(g9)
    c: Block(g7)
    c: Block(g5)
    c: Block(g3)
    c: Block(g1)
    c: Coincident(g24,g0)
    c: Coincident(g24,g12)
    c: Horizontal(g24)
    c: Coincident(g25,g0)
    c: Coincident(g25,g12)
    c: Horizontal(g25)
    c: Coincident(g26,g1)
    c: Coincident(g26,g13)
    c: Horizontal(g26)
    c: Coincident(g27,g1)
    c: Coincident(g27,g13)
    c: Horizontal(g27)
    c: Coincident(g28,g2)
    c: Coincident(g28,g14)
    c: Horizontal(g28)
    c: Coincident(g29,g2)
    c: Coincident(g29,g14)
    c: Horizontal(g29)
    c: Coincident(g30,g3)
    c: Coincident(g30,g15)
    c: Horizontal(g30)
    c: Coincident(g31,g3)
    c: Coincident(g31,g15)
    c: Horizontal(g31)
    c: Coincident(g32,g4)
    c: Coincident(g32,g16)
    c: Horizontal(g32)
    c: Coincident(g33,g4)
    c: Coincident(g33,g16)
    c: Horizontal(g33)
    c: Coincident(g34,g5)
    c: Coincident(g34,g17)
    c: Horizontal(g34)
    c: Coincident(g35,g5)
    c: Coincident(g35,g17)
    c: Horizontal(g35)
    c: Coincident(g36,g6)
    c: Coincident(g36,g19)
    c: Horizontal(g36)
    c: Coincident(g37,g6)
    c: Coincident(g37,g19)
    c: Horizontal(g37)
    c: Coincident(g38,g7)
    c: Coincident(g38,g18)
    c: Horizontal(g38)
    c: Coincident(g39,g7)
    c: Coincident(g39,g18)
    c: Horizontal(g39)
    c: Coincident(g40,g8)
    c: Coincident(g40,g20)
    c: Horizontal(g40)
    c: Coincident(g41,g8)
    c: Coincident(g41,g20)
    c: Horizontal(g41)
    c: Coincident(g42,g9)
    c: Coincident(g42,g23)
    c: Horizontal(g42)
    c: Coincident(g43,g9)
    c: Coincident(g43,g23)
    c: Horizontal(g43)
    c: Coincident(g44,g10)
    c: Coincident(g44,g22)
    c: Horizontal(g44)
    c: Coincident(g45,g10)
    c: Coincident(g45,g22)
    c: Horizontal(g45)
    c: Coincident(g46,g11)
    c: Coincident(g46,g21)
    c: Horizontal(g46)
    c: Coincident(g47,g11)
    c: Coincident(g47,g21)
    c: Horizontal(g47)
FEATURE [Sketcher::SketchObject] Sketch031
  FullyConstrained = true
  Placement = pos=(117,19,0) rot=(0.57735,0.57735,0.57735;2.0944rad)
  sketch-geometry (24):
    g0: ArcOfCircle CenterX=-49.19 CenterY=67.75 CenterZ=0 NormalX=0 NormalY=0 NormalZ=1 AngleXU=0 Radius=1.5 StartAngle=1.5708 EndAngle=4.71239
    g1: ArcOfCircle CenterX=-49.19 CenterY=62 CenterZ=0 NormalX=0 NormalY=0 NormalZ=1 AngleXU=0 Radius=1.5 StartAngle=1.5708 EndAngle=4.71239
    g2: ArcOfCircle CenterX=-49.19 CenterY=56.25 CenterZ=0 NormalX=0 NormalY=0 NormalZ=1 AngleXU=0 Radius=1.5 StartAngle=1.5708 EndAngle=4.71239
    g3: ArcOfCircle CenterX=-49.19 CenterY=50.5 CenterZ=0 NormalX=0 NormalY=0 NormalZ=1 AngleXU=0 Radius=1.5 StartAngle=1.5708 EndAngle=4.71239
    g4: ArcOfCircle CenterX=-49.19 CenterY=44.75 CenterZ=0 NormalX=0 NormalY=0 NormalZ=1 AngleXU=0 Radius=1.5 StartAngle=1.5708 EndAngle=4.71239
    g5: ArcOfCircle CenterX=-49.19 CenterY=39 CenterZ=0 NormalX=0 NormalY=0 NormalZ=1 AngleXU=0 Radius=1.5 StartAngle=1.5708 EndAngle=4.71239
    g6: ArcOfCircle CenterX=-49.19 CenterY=33 CenterZ=0 NormalX=0 NormalY=0 NormalZ=1 AngleXU=0 Radius=1.5 StartAngle=1.5708 EndAngle=4.71239
    g7: ArcOfCircle CenterX=-49.19 CenterY=27.25 CenterZ=0 NormalX=0 NormalY=0 NormalZ=1 AngleXU=0 Radius=1.5 StartAngle=1.5708 EndAngle=4.71239
    g8: ArcOfCircle CenterX=-49.19 CenterY=21.5 CenterZ=0 NormalX=0 NormalY=0 NormalZ=1 AngleXU=0 Radius=1.5 StartAngle=1.5708 EndAngle=4.71239
    g9: ArcOfCircle CenterX=-49.19 CenterY=15.75 CenterZ=0 NormalX=0 NormalY=0 NormalZ=1 AngleXU=0 Radius=1.5 StartAngle=1.5708 EndAngle=4.71239
    g10: ArcOfCircle CenterX=-49.19 CenterY=10 CenterZ=0 NormalX=0 NormalY=0 NormalZ=1 AngleXU=0 Radius=1.5 StartAngle=1.5708 EndAngle=4.71239
    g11: ArcOfCircle CenterX=-49.19 CenterY=4.25 CenterZ=0 NormalX=0 NormalY=0 NormalZ=1 AngleXU=0 Radius=1.5 StartAngle=1.5708 EndAngle=4.71239
    g12: LineSegment StartX=-49.19 StartY=69.25 StartZ=0 EndX=-49.19 EndY=66.25 EndZ=0
    g13: LineSegment StartX=-49.19 StartY=63.5 StartZ=0 EndX=-49.19 EndY=60.5 EndZ=0
    g14: LineSegment StartX=-49.19 StartY=57.75 StartZ=0 EndX=-49.19 EndY=54.75 EndZ=0
    g15: LineSegment StartX=-49.19 StartY=52 StartZ=0 EndX=-49.19 EndY=49 EndZ=0
    g16: LineSegment StartX=-49.19 StartY=46.25 StartZ=0 EndX=-49.19 EndY=43.25 EndZ=0
    g17: LineSegment StartX=-49.19 StartY=40.5 StartZ=0 EndX=-49.19 EndY=37.5 EndZ=0
    g18: LineSegment StartX=-49.19 StartY=34.5 StartZ=0 EndX=-49.19 EndY=31.5 EndZ=0
    g19: LineSegment StartX=-49.19 StartY=28.75 StartZ=0 EndX=-49.19 EndY=25.75 EndZ=0
    g20: LineSegment StartX=-49.19 StartY=23 StartZ=0 EndX=-49.19 EndY=20 EndZ=0
    g21: LineSegment StartX=-49.19 StartY=17.25 StartZ=0 EndX=-49.19 EndY=14.25 EndZ=0
    g22: LineSegment StartX=-49.19 StartY=11.5 StartZ=0 EndX=-49.19 EndY=8.5 EndZ=0
    g23: LineSegment StartX=-49.19 StartY=5.75 StartZ=0 EndX=-49.19 EndY=2.75 EndZ=0
  constraints (48):
    c: Block(g0)
    c: Block(g1)
    c: Block(g2)
    c: Block(g3)
    c: Block(g4)
    c: Block(g5)
    c: Block(g6)
    c: Block(g7)
    c: Block(g8)
    c: Block(g9)
    c: Block(g10)
    c: Block(g11)
    c: Coincident(g12,g0)
    c: Coincident(g12,g0)
    c: Vertical(g12)
    c: Vertical(g13)
    c: Coincident(g13,g1)
    c: Vertical(g14)
    c: Coincident(g14,g2)
    c: Vertical(g15)
    c: Coincident(g15,g3)
    c: Vertical(g16)
    c: Coincident(g16,g4)
    c: Vertical(g17)
    c: Coincident(g17,g5)
    c: Vertical(g18)
    c: Coincident(g18,g6)
    c: Vertical(g19)
    c: Coincident(g19,g7)
    c: Vertical(g20)
    c: Coincident(g20,g8)
    c: Vertical(g21)
    c: Coincident(g21,g9)
    c: Vertical(g22)
    c: Coincident(g22,g10)
    c: Vertical(g23)
    c: Coincident(g23,g11)
    c: Block(g23)
    c: Block(g22)
    c: Block(g21)
    c: Block(g20)
    c: Block(g13)
    c: Block(g14)
    c: Block(g15)
    c: Block(g16)
    c: Block(g17)
    c: Block(g18)
    c: Block(g19)
FEATURE [Part::Extrusion] Extrude022
  Base = -> Sketch030
  Dir = (1,-2e-16,2e-16)
  DirMode = 2
  FaceMakerClass = Part::FaceMakerBullseye
  LengthFwd = 19
  LengthRev = 0
  Placement = pos=(-19,0,0) rot=(0,0,1;0rad)
  Solid = true
  Symmetric = false
FEATURE [Part::Fillet] Fillet022
  Base = -> Extrude022
  Edges = 24 edges r=1.49: [Edge6,Edge11,Edge18,Edge23,Edge30,Edge35,Edge42,Edge47,Edge54,Edge59,Edge66,Edge71,Edge78,Edge83,Edge90,Edge95,Edge102,Edge107,Edge114,Edge119,Edge126,Edge131,Edge138,Edge143]
FEATURE [Part::Cut] Cut020  label="top010"
  Base = -> Cut019
  Tool = -> Fillet022
FEATURE [Sketcher::SketchObject] Sketch032
  FullyConstrained = true
  Placement = pos=(117,19,0) rot=(0.57735,0.57735,0.57735;2.0944rad)
  sketch-geometry (48):
    g0: LineSegment StartX=-49.19 StartY=69.25 StartZ=0 EndX=-49.19 EndY=66.25 EndZ=0
    g1: LineSegment StartX=-49.19 StartY=63.5 StartZ=0 EndX=-49.19 EndY=60.5 EndZ=0
    g2: LineSegment StartX=-49.19 StartY=57.75 StartZ=0 EndX=-49.19 EndY=54.75 EndZ=0
    g3: LineSegment StartX=-49.19 StartY=52 StartZ=0 EndX=-49.19 EndY=49 EndZ=0
    g4: LineSegment StartX=-49.19 StartY=46.25 StartZ=0 EndX=-49.19 EndY=43.25 EndZ=0
    g5: LineSegment StartX=-49.19 StartY=40.5 StartZ=0 EndX=-49.19 EndY=37.5 EndZ=0
    g6: LineSegment StartX=-49.19 StartY=34.5 StartZ=0 EndX=-49.19 EndY=31.5 EndZ=0
    g7: LineSegment StartX=-49.19 StartY=28.75 StartZ=0 EndX=-49.19 EndY=25.75 EndZ=0
    g8: LineSegment StartX=-49.19 StartY=23 StartZ=0 EndX=-49.19 EndY=20 EndZ=0
    g9: LineSegment StartX=-49.19 StartY=17.25 StartZ=0 EndX=-49.19 EndY=14.25 EndZ=0
    g10: LineSegment StartX=-49.19 StartY=11.5 StartZ=0 EndX=-49.19 EndY=8.5 EndZ=0
    g11: LineSegment StartX=-49.19 StartY=5.75 StartZ=0 EndX=-49.19 EndY=2.75 EndZ=0
    g12: ArcOfCircle CenterX=-1.5 CenterY=67.75 CenterZ=0 NormalX=0 NormalY=0 NormalZ=1 AngleXU=0 Radius=1.5 StartAngle=4.71239 EndAngle=7.85398
    g13: ArcOfCircle CenterX=-1.5 CenterY=62 CenterZ=0 NormalX=0 NormalY=0 NormalZ=1 AngleXU=0 Radius=1.5 StartAngle=4.71239 EndAngle=7.85398
    g14: ArcOfCircle CenterX=-1.5 CenterY=56.25 CenterZ=0 NormalX=0 NormalY=0 NormalZ=1 AngleXU=0 Radius=1.5 StartAngle=4.71239 EndAngle=7.85398
    g15: ArcOfCircle CenterX=-11.49 CenterY=50.5 CenterZ=0 NormalX=0 NormalY=0 NormalZ=1 AngleXU=0 Radius=1.5 StartAngle=4.71239 EndAngle=7.85398
    g16: ArcOfCircle CenterX=-16.28 CenterY=44.75 CenterZ=0 NormalX=0 NormalY=0 NormalZ=1 AngleXU=0 Radius=1.5 StartAngle=4.71239 EndAngle=7.85398
    g17: ArcOfCircle CenterX=-18.2337 CenterY=39 CenterZ=0 NormalX=0 NormalY=0 NormalZ=1 AngleXU=0 Radius=1.5 StartAngle=4.71485 EndAngle=7.85398
    g18: ArcOfCircle CenterX=-16.2837 CenterY=27.25 CenterZ=0 NormalX=0 NormalY=0 NormalZ=1 AngleXU=0 Radius=1.5 StartAngle=4.71485 EndAngle=7.85398
    g19: ArcOfCircle CenterX=-18.2337 CenterY=33 CenterZ=0 NormalX=0 NormalY=0 NormalZ=1 AngleXU=0 Radius=1.5 StartAngle=4.71485 EndAngle=7.85398
    g20: ArcOfCircle CenterX=-11.49 CenterY=21.5 CenterZ=0 NormalX=0 NormalY=0 NormalZ=1 AngleXU=0 Radius=1.5 StartAngle=4.71239 EndAngle=7.85398
    g21: ArcOfCircle CenterX=-1.5 CenterY=4.25 CenterZ=0 NormalX=0 NormalY=0 NormalZ=1 AngleXU=0 Radius=1.5 StartAngle=4.71239 EndAngle=7.85398
    g22: ArcOfCircle CenterX=-1.5 CenterY=10 CenterZ=0 NormalX=0 NormalY=0 NormalZ=1 AngleXU=0 Radius=1.5 StartAngle=4.71239 EndAngle=7.85398
    g23: ArcOfCircle CenterX=-1.5 CenterY=15.75 CenterZ=0 NormalX=0 NormalY=0 NormalZ=1 AngleXU=0 Radius=1.5 StartAngle=4.71239 EndAngle=7.85398
    g24: LineSegment StartX=-49.19 StartY=69.25 StartZ=0 EndX=-1.5 EndY=69.25 EndZ=0
    g25: LineSegment StartX=-49.19 StartY=66.25 StartZ=0 EndX=-1.5 EndY=66.25 EndZ=0
    g26: LineSegment StartX=-49.19 StartY=63.5 StartZ=0 EndX=-1.5 EndY=63.5 EndZ=0
    g27: LineSegment StartX=-49.19 StartY=60.5 StartZ=0 EndX=-1.5 EndY=60.5 EndZ=0
    g28: LineSegment StartX=-49.19 StartY=57.75 StartZ=0 EndX=-1.5 EndY=57.75 EndZ=0
    g29: LineSegment StartX=-49.19 StartY=54.75 StartZ=0 EndX=-1.5 EndY=54.75 EndZ=0
    g30: LineSegment StartX=-49.19 StartY=52 StartZ=0 EndX=-11.49 EndY=52 EndZ=0
    g31: LineSegment StartX=-49.19 StartY=49 StartZ=0 EndX=-11.49 EndY=49 EndZ=0
    g32: LineSegment StartX=-49.19 StartY=46.25 StartZ=0 EndX=-16.28 EndY=46.25 EndZ=0
    g33: LineSegment StartX=-49.19 StartY=43.25 StartZ=0 EndX=-16.28 EndY=43.25 EndZ=0
    g34: LineSegment StartX=-49.19 StartY=40.5 StartZ=0 EndX=-18.2337 EndY=40.5 EndZ=0
    g35: LineSegment StartX=-49.19 StartY=37.5 StartZ=0 EndX=-18.23 EndY=37.5 EndZ=0
    g36: LineSegment StartX=-49.19 StartY=34.5 StartZ=0 EndX=-18.2337 EndY=34.5 EndZ=0
    g37: LineSegment StartX=-49.19 StartY=31.5 StartZ=0 EndX=-18.23 EndY=31.5 EndZ=0
    g38: LineSegment StartX=-49.19 StartY=28.75 StartZ=0 EndX=-16.2837 EndY=28.75 EndZ=0
    g39: LineSegment StartX=-49.19 StartY=25.75 StartZ=0 EndX=-16.28 EndY=25.75 EndZ=0
    g40: LineSegment StartX=-49.19 StartY=23 StartZ=0 EndX=-11.49 EndY=23 EndZ=0
    g41: LineSegment StartX=-49.19 StartY=20 StartZ=0 EndX=-11.49 EndY=20 EndZ=0
    g42: LineSegment StartX=-49.19 StartY=17.25 StartZ=0 EndX=-1.5 EndY=17.25 EndZ=0
    g43: LineSegment StartX=-49.19 StartY=14.25 StartZ=0 EndX=-1.5 EndY=14.25 EndZ=0
    g44: LineSegment StartX=-49.19 StartY=11.5 StartZ=0 EndX=-1.5 EndY=11.5 EndZ=0
    g45: LineSegment StartX=-49.19 StartY=8.5 StartZ=0 EndX=-1.5 EndY=8.5 EndZ=0
    g46: LineSegment StartX=-49.19 StartY=5.75 StartZ=0 EndX=-1.5 EndY=5.75 EndZ=0
    g47: LineSegment StartX=-49.19 StartY=2.75 StartZ=0 EndX=-1.5 EndY=2.75 EndZ=0
  constraints (120):
    c: Vertical(g0)
    c: Distance(g0) = 3
    c: Block(g0)
    c: Vertical(g1)
    c: Distance(g1) = 3
    c: Vertical(g2)
    c: Equal(g0,g2) = 3
    c: Block(g2)
    c: Vertical(g3)
    c: Equal(g1,g3) = 3
    c: Vertical(g4)
    c: Equal(g0,g4) = 3
    c: Block(g4)
    c: Vertical(g5)
    c: Equal(g1,g5) = 3
    c: Vertical(g6)
    c: Equal(g0,g6) = 3
    c: Block(g6)
    c: Vertical(g7)
    c: Equal(g1,g7) = 3
    c: Vertical(g8)
    c: Equal(g0,g8) = 3
    c: Block(g8)
    c: Vertical(g9)
    c: Equal(g1,g9) = 3
    c: Vertical(g10)
    c: Equal(g0,g10) = 3
    c: Block(g10)
    c: Vertical(g11)
    c: Equal(g1,g11) = 3
    c: Block(g12)
    c: Block(g13)
    c: Block(g14)
    c: Block(g15)
    c: Block(g16)
    c: Block(g17)
    c: Block(g18)
    c: Block(g19)
    c: Block(g20)
    c: Block(g21)
    c: Block(g22)
    c: Block(g23)
    c: Block(g11)
    c: Block(g9)
    c: Block(g7)
    c: Block(g5)
    c: Block(g3)
    c: Block(g1)
    c: Coincident(g24,g0)
    c: Coincident(g24,g12)
    c: Horizontal(g24)
    c: Coincident(g25,g0)
    c: Coincident(g25,g12)
    c: Horizontal(g25)
    c: Coincident(g26,g1)
    c: Coincident(g26,g13)
    c: Horizontal(g26)
    c: Coincident(g27,g1)
    c: Coincident(g27,g13)
    c: Horizontal(g27)
    c: Coincident(g28,g2)
    c: Coincident(g28,g14)
    c: Horizontal(g28)
    c: Coincident(g29,g2)
    c: Coincident(g29,g14)
    c: Horizontal(g29)
    c: Coincident(g30,g3)
    c: Coincident(g30,g15)
    c: Horizontal(g30)
    c: Coincident(g31,g3)
    c: Coincident(g31,g15)
    c: Horizontal(g31)
    c: Coincident(g32,g4)
    c: Coincident(g32,g16)
    c: Horizontal(g32)
    c: Coincident(g33,g4)
    c: Coincident(g33,g16)
    c: Horizontal(g33)
    c: Coincident(g34,g5)
    c: Coincident(g34,g17)
    c: Horizontal(g34)
    c: Coincident(g35,g5)
    c: Coincident(g35,g17)
    c: Horizontal(g35)
    c: Coincident(g36,g6)
    c: Coincident(g36,g19)
    c: Horizontal(g36)
    c: Coincident(g37,g6)
    c: Coincident(g37,g19)
    c: Horizontal(g37)
    c: Coincident(g38,g7)
    c: Coincident(g38,g18)
    c: Horizontal(g38)
    c: Coincident(g39,g7)
    c: Coincident(g39,g18)
    c: Horizontal(g39)
    c: Coincident(g40,g8)
    c: Coincident(g40,g20)
    c: Horizontal(g40)
    c: Coincident(g41,g8)
    c: Coincident(g41,g20)
    c: Horizontal(g41)
    c: Coincident(g42,g9)
    c: Coincident(g42,g23)
    c: Horizontal(g42)
    c: Coincident(g43,g9)
    c: Coincident(g43,g23)
    c: Horizontal(g43)
    c: Coincident(g44,g10)
    c: Coincident(g44,g22)
    c: Horizontal(g44)
    c: Coincident(g45,g10)
    c: Coincident(g45,g22)
    c: Horizontal(g45)
    c: Coincident(g46,g11)
    c: Coincident(g46,g21)
    c: Horizontal(g46)
    c: Coincident(g47,g11)
    c: Coincident(g47,g21)
    c: Horizontal(g47)
FEATURE [Part::Extrusion] Extrude023
  Base = -> Sketch032
  Dir = (1,-2e-16,2e-16)
  DirMode = 2
  FaceMakerClass = Part::FaceMakerBullseye
  LengthFwd = 19
  LengthRev = 0
  Placement = pos=(-19,0,0) rot=(0,0,1;0rad)
  Solid = true
  Symmetric = false
FEATURE [Part::Fillet] Fillet023
  Base = -> Extrude023
  Edges = <same value as first occurrence — deduplicated (x6 in doc)>
  Placement = pos=(0,0.05,0) rot=(0,0,1;0rad)
FEATURE [Part::Cut] Cut014  label="bottom003"
  Base = -> Cut007
  Tool = -> Fusion047
FEATURE [Part::Cut] Cut021  label="bottom004"
  Base = -> Cut014
  Tool = -> Fillet023
FEATURE [Sketcher::SketchObject] Sketch033
  FullyConstrained = true
  Placement = pos=(117,19,0) rot=(0.57735,0.57735,0.57735;2.0944rad)
  sketch-geometry (8):
    g0: LineSegment StartX=-49.19 StartY=69.25 StartZ=0 EndX=-49.19 EndY=66.25 EndZ=0
    g1: LineSegment StartX=-49.19 StartY=5.75 StartZ=0 EndX=-49.19 EndY=2.75 EndZ=0
    g2: ArcOfCircle CenterX=-1.5 CenterY=67.75 CenterZ=0 NormalX=0 NormalY=0 NormalZ=1 AngleXU=0 Radius=1.5 StartAngle=4.71239 EndAngle=7.85398
    g3: ArcOfCircle CenterX=-1.5 CenterY=4.25 CenterZ=0 NormalX=0 NormalY=0 NormalZ=1 AngleXU=0 Radius=1.5 StartAngle=4.71239 EndAngle=7.85398
    g4: LineSegment StartX=-49.19 StartY=69.25 StartZ=0 EndX=-1.5 EndY=69.25 EndZ=0
    g5: LineSegment StartX=-49.19 StartY=66.25 StartZ=0 EndX=-1.5 EndY=66.25 EndZ=0
    g6: LineSegment StartX=-49.19 StartY=5.75 StartZ=0 EndX=-1.5 EndY=5.75 EndZ=0
    g7: LineSegment StartX=-49.19 StartY=2.75 StartZ=0 EndX=-1.5 EndY=2.75 EndZ=0
  constraints (19):
    c: Vertical(g0)
    c: Distance(g0) = 3
    c: Block(g0)
    c: Vertical(g1)
    c: Block(g2)
    c: Block(g3)
    c: Block(g1)
    c: Coincident(g4,g0)
    c: Coincident(g4,g2)
    c: Horizontal(g4)
    c: Coincident(g5,g0)
    c: Coincident(g5,g2)
    c: Horizontal(g5)
    c: Coincident(g6,g1)
    c: Coincident(g6,g3)
    c: Horizontal(g6)
    c: Coincident(g7,g1)
    c: Coincident(g7,g3)
    c: Horizontal(g7)
FEATURE [Sketcher::SketchObject] Sketch034
  FullyConstrained = true
  Placement = pos=(117,19,0) rot=(0.57735,0.57735,0.57735;2.0944rad)
  sketch-geometry (8):
    g0: LineSegment StartX=-49.19 StartY=63.5 StartZ=0 EndX=-49.19 EndY=60.5 EndZ=0
    g1: LineSegment StartX=-49.19 StartY=11.5 StartZ=0 EndX=-49.19 EndY=8.5 EndZ=0
    g2: ArcOfCircle CenterX=-1.5 CenterY=62 CenterZ=0 NormalX=0 NormalY=0 NormalZ=1 AngleXU=0 Radius=1.5 StartAngle=4.71239 EndAngle=7.85398
    g3: ArcOfCircle CenterX=-1.5 CenterY=10 CenterZ=0 NormalX=0 NormalY=0 NormalZ=1 AngleXU=0 Radius=1.5 StartAngle=4.71239 EndAngle=7.85398
    g4: LineSegment StartX=-49.19 StartY=63.5 StartZ=0 EndX=-1.5 EndY=63.5 EndZ=0
    g5: LineSegment StartX=-49.19 StartY=60.5 StartZ=0 EndX=-1.5 EndY=60.5 EndZ=0
    g6: LineSegment StartX=-49.19 StartY=11.5 StartZ=0 EndX=-1.5 EndY=11.5 EndZ=0
    g7: LineSegment StartX=-49.19 StartY=8.5 StartZ=0 EndX=-1.5 EndY=8.5 EndZ=0
  constraints (19):
    c: Vertical(g0)
    c: Distance(g0) = 3
    c: Vertical(g1)
    c: Block(g1)
    c: Block(g2)
    c: Block(g3)
    c: Block(g0)
    c: Coincident(g4,g0)
    c: Coincident(g4,g2)
    c: Horizontal(g4)
    c: Coincident(g5,g0)
    c: Coincident(g5,g2)
    c: Horizontal(g5)
    c: Coincident(g6,g1)
    c: Coincident(g6,g3)
    c: Horizontal(g6)
    c: Coincident(g7,g1)
    c: Coincident(g7,g3)
    c: Horizontal(g7)
FEATURE [Part::Extrusion] Extrude024
  Base = -> Sketch033
  Dir = (1,0,0)
  DirMode = 2
  FaceMakerClass = Part::FaceMakerBullseye
  LengthFwd = 10
  LengthRev = 0
  Solid = true
  Symmetric = false
FEATURE [Part::Extrusion] Extrude025
  Base = -> Sketch034
  Dir = (1,0,0)
  DirMode = 2
  FaceMakerClass = Part::FaceMakerBullseye
  LengthFwd = 10
  LengthRev = 0
  Solid = true
  Symmetric = false
FEATURE [Part::Fillet] Fillet024  label="removeFromtMoreFrontCaseScrewRetainers"
  Base = -> Extrude024
  Edges = 4 edges r=1.49: [Edge6,Edge11,Edge18,Edge23]
  Placement = pos=(-11,0,0) rot=(0,0,1;0rad)
FEATURE [Part::Fillet] Fillet025  label="removeFromtMoreFrontCaseScrewRetainers001"
  Base = -> Extrude025
  Edges = 4 edges r=1.49: [Edge6,Edge11,Edge18,Edge23]
  Placement = pos=(-19,0,0) rot=(0,0,1;0rad)
FEATURE [Part::Cut] Cut022
  Base = -> Cut015
  Tool = -> Fillet025
FEATURE [Part::Cut] Cut023  label="screwRetainers"
  Base = -> Cut022
  Tool = -> Fillet024
FEATURE [Part::MultiFuse] Fusion056  label="bottom005"
  Shapes = -> [Fusion044,Cut021]
FEATURE [Part::MultiFuse] Fusion057  label="casePillars001"
  Shapes = -> [Cut016,Fusion052]
FEATURE [Part::MultiFuse] Fusion058  label="bottom006"
  Shapes = -> [Fusion056,Cut023]
FEATURE [Part::MultiFuse] Fusion059  label="bottom007"
  Shapes = -> [Fusion058,Fillet005]
FEATURE [Part::MultiFuse] Fusion060  label="bottom008"
  Shapes = -> [Fusion059,Fusion]
FEATURE [Part::MultiFuse] Fusion061  label="top011"
  Shapes = -> [Cut006,Cut020]
FEATURE [Part::MultiFuse] Fusion062  label="top012"
  Shapes = -> [Fusion057,Fusion061]
FEATURE [Sketcher::SketchObject] Sketch035  label="topSketch007"
  FullyConstrained = true
  sketch-geometry (6):
    g0: LineSegment StartX=19 StartY=38 StartZ=0 EndX=117 EndY=38 EndZ=0
    g1: ArcOfCircle CenterX=19 CenterY=19 CenterZ=0 NormalX=0 NormalY=0 NormalZ=1 AngleXU=0 Radius=19 StartAngle=1.5708 EndAngle=3.14159
    g2: LineSegment StartX=117 StartY=38 StartZ=0 EndX=117 EndY=19 EndZ=0
    g3: LineSegment StartX=98 StartY=1.0161e-12 StartZ=0 EndX=5.22862e-06 EndY=1.0161e-12 EndZ=0
    g4: LineSegment StartX=5.22862e-06 StartY=19 StartZ=0 EndX=5.22862e-06 EndY=1.0161e-12 EndZ=0
    g5: ArcOfCircle CenterX=98 CenterY=19 CenterZ=0 NormalX=0 NormalY=0 NormalZ=1 AngleXU=0 Radius=19 StartAngle=4.71239 EndAngle=6.28319
  constraints (16):
    c: Horizontal(g0)
    c: Distance(g0) = 98
    c: Coincident(g1,g0)
    c: Block(g1)
    c: Coincident(g2,g0)
    c: Vertical(g2)
    c: Distance(g2) = 19
    c: Horizontal(g3)
    c: Coincident(g4,g1)
    c: Vertical(g4)
    c: Coincident(g3,g4)
    c: Block(g3)
    c: Coincident(g5,g2)
    c: Coincident(g5,g3)
    c: Block(g0)
    c: Block(g5)
FEATURE [Part::Extrusion] Extrude026  label="sideA001"
  Base = -> Sketch035
  Dir = (0,0,1)
  DirMode = 2
  FaceMakerClass = Part::FaceMakerBullseye
  LengthFwd = 3
  LengthRev = 0
  Placement = pos=(0,0,-2.7) rot=(0,0,1;0rad)
  Solid = true
  Symmetric = false
FEATURE [Sketcher::SketchObject] Sketch036  label="topSketch008"
  FullyConstrained = true
  sketch-geometry (6):
    g0: LineSegment StartX=19 StartY=38 StartZ=0 EndX=117 EndY=38 EndZ=0
    g1: ArcOfCircle CenterX=19 CenterY=19 CenterZ=0 NormalX=0 NormalY=0 NormalZ=1 AngleXU=0 Radius=19 StartAngle=1.5708 EndAngle=3.14159
    g2: LineSegment StartX=117 StartY=38 StartZ=0 EndX=117 EndY=19 EndZ=0
    g3: LineSegment StartX=98 StartY=1.0161e-12 StartZ=0 EndX=5.22862e-06 EndY=1.0161e-12 EndZ=0
    g4: LineSegment StartX=5.22862e-06 StartY=19 StartZ=0 EndX=5.22862e-06 EndY=1.0161e-12 EndZ=0
    g5: ArcOfCircle CenterX=98 CenterY=19 CenterZ=0 NormalX=0 NormalY=0 NormalZ=1 AngleXU=0 Radius=19 StartAngle=4.71239 EndAngle=6.28319
  constraints (16):
    c: Horizontal(g0)
    c: Distance(g0) = 98
    c: Coincident(g1,g0)
    c: Block(g1)
    c: Coincident(g2,g0)
    c: Vertical(g2)
    c: Distance(g2) = 19
    c: Horizontal(g3)
    c: Coincident(g4,g1)
    c: Vertical(g4)
    c: Coincident(g3,g4)
    c: Block(g3)
    c: Coincident(g5,g2)
    c: Coincident(g5,g3)
    c: Block(g0)
    c: Block(g5)
FEATURE [Part::Extrusion] Extrude027  label="sideB001"
  Base = -> Sketch036
  Dir = (0,0,1)
  DirMode = 2
  FaceMakerClass = Part::FaceMakerBullseye
  LengthFwd = 3
  LengthRev = 0
  Placement = pos=(0,0,71.7) rot=(0,0,1;0rad)
  Solid = true
  Symmetric = false
FEATURE [Part::MultiFuse] Fusion064  label="removeFromBottom"
  Shapes = -> [Extrude026,Extrude027]
FEATURE [Part::Cut] Cut024  label="bottom009"
  Base = -> Fusion060
  Tool = -> Fusion064
FEATURE [Sketcher::SketchObject] Sketch037  label="topSketch009"
  FullyConstrained = true
  sketch-geometry (8):
    g0: ArcOfCircle CenterX=19 CenterY=19.1201 CenterZ=0 NormalX=0 NormalY=0 NormalZ=1 AngleXU=0 Radius=18.8799 StartAngle=1.5708 EndAngle=3.14793
    g1: LineSegment StartX=0.120501 StartY=19.0004 StartZ=0 EndX=0.120501 EndY=0.000382114 EndZ=0
    g2: LineSegment StartX=19 StartY=38 StartZ=0 EndX=124 EndY=38 EndZ=0
    g3: LineSegment StartX=0.120501 StartY=0.000382114 StartZ=0 EndX=105.121 EndY=0.000382114 EndZ=0
    g4: LineSegment StartX=124 StartY=38 StartZ=0 EndX=125.616 EndY=38 EndZ=0
    g5: LineSegment StartX=105.121 StartY=0.000382114 StartZ=0 EndX=106.736 EndY=0.000382114 EndZ=0
    g6: ArcOfCircle CenterX=106.616 CenterY=19 CenterZ=0 NormalX=0 NormalY=0 NormalZ=1 AngleXU=0 Radius=19 StartAngle=4.71873 EndAngle=6.28319
    g7: LineSegment StartX=125.616 StartY=38 StartZ=0 EndX=125.616 EndY=19 EndZ=0
  constraints (21):
    c: Block(g0)
    c: Coincident(g1,g0)
    c: Vertical(g1)
    c: Horizontal(g2)
    c: Distance(g2) = 105
    c: Coincident(g2,g0)
    c: Distance(g1) = 19
    c: Coincident(g3,g1)
    c: Horizontal(g3)
    c: Distance(g3) = 105
    c: Coincident(g4,g2)
    c: Horizontal(g4)
    c: Distance(g4) = 1.61553
    c: Horizontal(g5)
    c: Equal(g4,g5) = 1.61553
    c: Coincident(g5,g3)
    c: Block(g6)
    c: Coincident(g6,g5)
    c: Coincident(g7,g4)
    c: Coincident(g7,g6)
    c: Vertical(g7)
FEATURE [Part::Extrusion] Extrude028  label="sideB"
  Base = -> Sketch037
  Dir = (0,0,1)
  DirMode = 2
  FaceMakerClass = Part::FaceMakerBullseye
  LengthFwd = 3
  LengthRev = 0
  Placement = pos=(0,0,72) rot=(0,0,1;0rad)
  Solid = true
  Symmetric = false
FEATURE [Sketcher::SketchObject] Sketch038  label="topSketch010"
  FullyConstrained = true
  sketch-geometry (22):
    g0: LineSegment StartX=5.21097e-06 StartY=3 StartZ=0 EndX=5.21097e-06 EndY=19 EndZ=0
    g1: ArcOfCircle CenterX=19 CenterY=19 CenterZ=0 NormalX=0 NormalY=0 NormalZ=1 AngleXU=0 Radius=19 StartAngle=1.5708 EndAngle=3.14159
    g2: ArcOfCircle CenterX=19 CenterY=19 CenterZ=0 NormalX=0 NormalY=0 NormalZ=1 AngleXU=0 Radius=16 StartAngle=1.5708 EndAngle=3.14159
    g3: LineSegment StartX=114 StartY=35 StartZ=0 EndX=19 EndY=35 EndZ=0
    g4: LineSegment StartX=5.21097e-06 StartY=3 StartZ=0 EndX=5.21097e-06 EndY=0 EndZ=0
    g5: LineSegment StartX=3 StartY=0 StartZ=0 EndX=5.21097e-06 EndY=0 EndZ=0
    g6: LineSegment StartX=3 StartY=19 StartZ=0 EndX=3 EndY=0 EndZ=0
    g7: LineSegment StartX=19 StartY=38 StartZ=0 EndX=124 EndY=38 EndZ=0
    g8: Circle CenterX=119 CenterY=35 CenterZ=0 NormalX=0 NormalY=0 NormalZ=1 AngleXU=0 Radius=1
    g9: Circle CenterX=121 CenterY=35 CenterZ=0 NormalX=0 NormalY=0 NormalZ=1 AngleXU=0 Radius=1
    g10: Circle CenterX=121 CenterY=33 CenterZ=0 NormalX=0 NormalY=0 NormalZ=1 AngleXU=0 Radius=1
    g11: BSplineCurve PolesCount=3 KnotsCount=2 Degree=2 IsPeriodic=0
    g12: GeomPoint X=119 Y=35 Z=0
    g13: GeomPoint X=121 Y=33 Z=0
    g14: LineSegment StartX=119 StartY=35 StartZ=0 EndX=114 EndY=35 EndZ=0
    g15: ArcOfCircle CenterX=105 CenterY=19 CenterZ=0 NormalX=0 NormalY=0 NormalZ=1 AngleXU=0 Radius=16 StartAngle=5.60905 EndAngle=6.28319
    g16: LineSegment StartX=121 StartY=33 StartZ=0 EndX=121 EndY=19 EndZ=0
    g17: LineSegment StartX=117.5 StartY=9.01251 StartZ=0 EndX=121.163 EndY=9.0125 EndZ=0
    g18: ArcOfCircle CenterX=105 CenterY=19 CenterZ=0 NormalX=0 NormalY=0 NormalZ=1 AngleXU=0 Radius=20.6155 StartAngle=5.7297 EndAngle=6.28319
    g19: LineSegment StartX=121.163 StartY=9.0125 StartZ=0 EndX=122.538 EndY=8.16329 EndZ=0
    g20: LineSegment StartX=124 StartY=38 StartZ=0 EndX=125.616 EndY=38 EndZ=0
    g21: LineSegment StartX=125.616 StartY=19 StartZ=0 EndX=125.616 EndY=38 EndZ=0
  constraints (49):
    c: Vertical(g0)
    c: Block(g0)
    c: Coincident(g1,g0)
    c: Block(g1)
    c: Coincident(g2,g1)
    c: Block(g2)
    c: Coincident(g3,g2)
    c: Horizontal(g3)
    c: Tangent(g3,g2)
    c: Coincident(g4,g0)
    c: Distance(g4) = 3
    c: Vertical(g4)
    c: Coincident(g5,g4)
    c: Horizontal(g5)
    c: Coincident(g6,g2)
    c: Coincident(g6,g5)
    c: Vertical(g6)
    c: Horizontal(g7)
    c: Distance(g7) = 105
    c: Coincident(g7,g1)
    c: Block(g3)
    c: Weight(g8) = 1
    c: Equal(g8,g9)
    c: Equal(g8,g10)
    c: InternalAlignment(g8,g11)
    c: InternalAlignment(g9,g11)
    c: InternalAlignment(g10,g11)
    c: InternalAlignment(g12,g11)
    c: InternalAlignment(g13,g11)
    c: Block(g11)
    c: Coincident(g14,g11)
    c: Coincident(g14,g3)
    c: Horizontal(g14)
    c: Block(g15)
    c: Coincident(g16,g11)
    c: Coincident(g16,g15)
    c: Vertical(g16)
    c: Distance(g16) = 14
    c: Coincident(g17,g15)
    c: Block(g18)
    c: Coincident(g19,g18)
    c: Coincident(g20,g7)
    c: Horizontal(g20)
    c: Vertical(g21)
    c: Coincident(g20,g21)
    c: Block(g20)
    c: Block(g21)
    c: Block(g19)
    c: Block(g17)
FEATURE [Part::Extrusion] Extrude029
  Base = -> Sketch038
  Dir = (0,0,1)
  DirMode = 2
  FaceMakerClass = Part::FaceMakerBullseye
  LengthFwd = 72
  LengthRev = 0
  Solid = true
  Symmetric = false
FEATURE [Part::Feature] Face085
  shape: bbox 4.8 x 25.5 x 2e-07 mm, 1 faces, 0 solids (baked)
FEATURE [Part::Revolution] Revolve089  label="moreFrontCaseScrewPost003"
  Angle = 360
  Axis = (0,1,0)
  Base = (0,0,0)
  FaceMakerClass = Part::FaceMakerBullseye
  Placement = pos=(109.5,4.5,3.5) rot=(0,0,1;0rad)
  Solid = false
  Source = -> Face085
  Symmetric = false
FEATURE [Part::Feature] Face086
  shape: bbox 4.8 x 25.5 x 2e-07 mm, 1 faces, 0 solids (baked)
FEATURE [Part::Revolution] Revolve090  label="moreFrontCaseScrewPost004"
  Angle = 360
  Axis = (0,1,0)
  Base = (0,0,0)
  FaceMakerClass = Part::FaceMakerBullseye
  Placement = pos=(109.5,4.5,68.5) rot=(0,0,1;0rad)
  Solid = false
  Source = -> Face086
  Symmetric = false
FEATURE [Part::Fillet] Fillet026  label="top013"
  Base = -> Extrude029
  Edges = 1 edges r=2: [Edge35]
FEATURE [Sketcher::SketchObject] Sketch039
  FullyConstrained = true
  sketch-geometry (7):
    g0: LineSegment StartX=0 StartY=0 StartZ=0 EndX=0 EndY=6 EndZ=0
    g1: Circle CenterX=0 CenterY=0 CenterZ=0 NormalX=0 NormalY=0 NormalZ=1 AngleXU=0 Radius=1
    g2: Circle CenterX=8 CenterY=6 CenterZ=0 NormalX=0 NormalY=0 NormalZ=1 AngleXU=0 Radius=1
    g3: BSplineCurve PolesCount=3 KnotsCount=2 Degree=2 IsPeriodic=0
    g4: GeomPoint X=0 Y=0 Z=0
    g5: GeomPoint X=8 Y=6 Z=0
    g6: LineSegment StartX=0 StartY=6 StartZ=0 EndX=8 EndY=6 EndZ=0
  constraints (14):
    c: Coincident(g0,g-1)
    c: Distance(g0) = 6
    c: Vertical(g0)
    c: Coincident(g3,g0)
    c: Weight(g1) = 1
    c: Equal(g1,g2)
    c: InternalAlignment(g1,g3)
    c: InternalAlignment(g2,g3)
    c: InternalAlignment(g4,g3)
    c: InternalAlignment(g5,g3)
    c: Block(g3)
    c: Coincident(g6,g0)
    c: Coincident(g6,g3)
    c: Horizontal(g6)
FEATURE [Sketcher::SketchObject] Sketch040
  FullyConstrained = true
  sketch-geometry (7):
    g0: LineSegment StartX=0 StartY=0 StartZ=0 EndX=0 EndY=6 EndZ=0
    g1: Circle CenterX=0 CenterY=0 CenterZ=0 NormalX=0 NormalY=0 NormalZ=1 AngleXU=0 Radius=1
    g2: Circle CenterX=8 CenterY=6 CenterZ=0 NormalX=0 NormalY=0 NormalZ=1 AngleXU=0 Radius=1
    g3: BSplineCurve PolesCount=3 KnotsCount=2 Degree=2 IsPeriodic=0
    g4: GeomPoint X=0 Y=0 Z=0
    g5: GeomPoint X=8 Y=6 Z=0
    g6: LineSegment StartX=0 StartY=6 StartZ=0 EndX=8 EndY=6 EndZ=0
  constraints (14):
    c: Coincident(g0,g-1)
    c: Distance(g0) = 6
    c: Vertical(g0)
    c: Coincident(g3,g0)
    c: Weight(g1) = 1
    c: Equal(g1,g2)
    c: InternalAlignment(g1,g3)
    c: InternalAlignment(g2,g3)
    c: InternalAlignment(g4,g3)
    c: InternalAlignment(g5,g3)
    c: Block(g3)
    c: Coincident(g6,g0)
    c: Coincident(g6,g3)
    c: Horizontal(g6)
FEATURE [Sketcher::SketchObject] Sketch041
  FullyConstrained = true
  sketch-geometry (7):
    g0: LineSegment StartX=0 StartY=0 StartZ=0 EndX=0 EndY=6 EndZ=0
    g1: Circle CenterX=0 CenterY=0 CenterZ=0 NormalX=0 NormalY=0 NormalZ=1 AngleXU=0 Radius=1
    g2: Circle CenterX=8 CenterY=6 CenterZ=0 NormalX=0 NormalY=0 NormalZ=1 AngleXU=0 Radius=1
    g3: BSplineCurve PolesCount=3 KnotsCount=2 Degree=2 IsPeriodic=0
    g4: GeomPoint X=0 Y=0 Z=0
    g5: GeomPoint X=8 Y=6 Z=0
    g6: LineSegment StartX=0 StartY=6 StartZ=0 EndX=8 EndY=6 EndZ=0
  constraints (14):
    c: Coincident(g0,g-1)
    c: Distance(g0) = 6
    c: Vertical(g0)
    c: Coincident(g3,g0)
    c: Weight(g1) = 1
    c: Equal(g1,g2)
    c: InternalAlignment(g1,g3)
    c: InternalAlignment(g2,g3)
    c: InternalAlignment(g4,g3)
    c: InternalAlignment(g5,g3)
    c: Block(g3)
    c: Coincident(g6,g0)
    c: Coincident(g6,g3)
    c: Horizontal(g6)
FEATURE [Sketcher::SketchObject] Sketch042
  FullyConstrained = true
  sketch-geometry (7):
    g0: LineSegment StartX=0 StartY=0 StartZ=0 EndX=0 EndY=6 EndZ=0
    g1: Circle CenterX=0 CenterY=0 CenterZ=0 NormalX=0 NormalY=0 NormalZ=1 AngleXU=0 Radius=1
    g2: Circle CenterX=8 CenterY=6 CenterZ=0 NormalX=0 NormalY=0 NormalZ=1 AngleXU=0 Radius=1
    g3: BSplineCurve PolesCount=3 KnotsCount=2 Degree=2 IsPeriodic=0
    g4: GeomPoint X=0 Y=0 Z=0
    g5: GeomPoint X=8 Y=6 Z=0
    g6: LineSegment StartX=0 StartY=6 StartZ=0 EndX=8 EndY=6 EndZ=0
  constraints (14):
    c: Coincident(g0,g-1)
    c: Distance(g0) = 6
    c: Vertical(g0)
    c: Coincident(g3,g0)
    c: Weight(g1) = 1
    c: Equal(g1,g2)
    c: InternalAlignment(g1,g3)
    c: InternalAlignment(g2,g3)
    c: InternalAlignment(g4,g3)
    c: InternalAlignment(g5,g3)
    c: Block(g3)
    c: Coincident(g6,g0)
    c: Coincident(g6,g3)
    c: Horizontal(g6)
FEATURE [Part::Extrusion] Extrude030  label="caseScrewPillarBracket008"
  Base = -> Sketch039
  Dir = (0,0,1)
  DirMode = 2
  FaceMakerClass = Part::FaceMakerBullseye
  LengthFwd = 2.4
  LengthRev = 0
  Placement = pos=(15.76,29,8.8) rot=(0,1,0;0rad)
  Solid = true
  Symmetric = false
FEATURE [Part::Extrusion] Extrude031  label="caseScrewPillarBracket009"
  Base = -> Sketch040
  Dir = (0,0,1)
  DirMode = 2
  FaceMakerClass = Part::FaceMakerBullseye
  LengthFwd = 2.4
  LengthRev = 0
  Placement = pos=(15.76,29,60.8) rot=(0,0,1;0rad)
  Solid = true
  Symmetric = false
FEATURE [Part::Extrusion] Extrude032  label="caseScrewPillarBracket010"
  Base = -> Sketch041
  Dir = (0,0,1)
  DirMode = 2
  FaceMakerClass = Part::FaceMakerBullseye
  LengthFwd = 2.4
  LengthRev = 0
  Placement = pos=(13.7,29,13.26) rot=(0,-1,0;1.5708rad)
  Solid = true
  Symmetric = false
FEATURE [Part::Extrusion] Extrude033  label="caseScrewPillarBracket011"
  Base = -> Sketch042
  Dir = (0,0,1)
  DirMode = 2
  FaceMakerClass = Part::FaceMakerBullseye
  LengthFwd = 2.4
  LengthRev = 0
  Placement = pos=(11.3,29,58.74) rot=(0,1,0;1.5708rad)
  Solid = true
  Symmetric = false
FEATURE [Sketcher::SketchObject] Sketch043
  FullyConstrained = true
  sketch-geometry (7):
    g0: LineSegment StartX=0 StartY=0 StartZ=0 EndX=0 EndY=6 EndZ=0
    g1: Circle CenterX=0 CenterY=0 CenterZ=0 NormalX=0 NormalY=0 NormalZ=1 AngleXU=0 Radius=1
    g2: Circle CenterX=8 CenterY=6 CenterZ=0 NormalX=0 NormalY=0 NormalZ=1 AngleXU=0 Radius=1
    g3: BSplineCurve PolesCount=3 KnotsCount=2 Degree=2 IsPeriodic=0
    g4: GeomPoint X=0 Y=0 Z=0
    g5: GeomPoint X=8 Y=6 Z=0
    g6: LineSegment StartX=0 StartY=6 StartZ=0 EndX=8 EndY=6 EndZ=0
  constraints (14):
    c: Coincident(g0,g-1)
    c: Distance(g0) = 6
    c: Vertical(g0)
    c: Coincident(g3,g0)
    c: Weight(g1) = 1
    c: Equal(g1,g2)
    c: InternalAlignment(g1,g3)
    c: InternalAlignment(g2,g3)
    c: InternalAlignment(g4,g3)
    c: InternalAlignment(g5,g3)
    c: Block(g3)
    c: Coincident(g6,g0)
    c: Coincident(g6,g3)
    c: Horizontal(g6)
FEATURE [Part::Extrusion] Extrude034  label="caseScrewPillarBracket012"
  Base = -> Sketch043
  Dir = (0,0,1)
  DirMode = 2
  FaceMakerClass = Part::FaceMakerBullseye
  LengthFwd = 2.4
  LengthRev = 0
  Placement = pos=(88.3,29,65.23) rot=(0,1,0;1.5708rad)
  Solid = true
  Symmetric = false
FEATURE [Sketcher::SketchObject] Sketch044
  FullyConstrained = true
  sketch-geometry (7):
    g0: LineSegment StartX=0 StartY=0 StartZ=0 EndX=0 EndY=6 EndZ=0
    g1: Circle CenterX=0 CenterY=0 CenterZ=0 NormalX=0 NormalY=0 NormalZ=1 AngleXU=0 Radius=1
    g2: Circle CenterX=8 CenterY=6 CenterZ=0 NormalX=0 NormalY=0 NormalZ=1 AngleXU=0 Radius=1
    g3: BSplineCurve PolesCount=3 KnotsCount=2 Degree=2 IsPeriodic=0
    g4: GeomPoint X=0 Y=0 Z=0
    g5: GeomPoint X=8 Y=6 Z=0
    g6: LineSegment StartX=0 StartY=6 StartZ=0 EndX=8 EndY=6 EndZ=0
  constraints (14):
    c: Coincident(g0,g-1)
    c: Distance(g0) = 6
    c: Vertical(g0)
    c: Coincident(g3,g0)
    c: Weight(g1) = 1
    c: Equal(g1,g2)
    c: InternalAlignment(g1,g3)
    c: InternalAlignment(g2,g3)
    c: InternalAlignment(g4,g3)
    c: InternalAlignment(g5,g3)
    c: Block(g3)
    c: Coincident(g6,g0)
    c: Coincident(g6,g3)
    c: Horizontal(g6)
FEATURE [Part::Extrusion] Extrude035  label="caseScrewPillarBracket013"
  Base = -> Sketch044
  Dir = (0,0,1)
  DirMode = 2
  FaceMakerClass = Part::FaceMakerBullseye
  LengthFwd = 2.4
  LengthRev = 0
  Placement = pos=(90.7,29,6.77) rot=(0,-1,0;1.5708rad)
  Solid = true
  Symmetric = false
FEATURE [Sketcher::SketchObject] Sketch045
  FullyConstrained = true
  sketch-geometry (7):
    g0: LineSegment StartX=0 StartY=0 StartZ=0 EndX=0 EndY=6 EndZ=0
    g1: Circle CenterX=0 CenterY=0 CenterZ=0 NormalX=0 NormalY=0 NormalZ=1 AngleXU=0 Radius=1
    g2: Circle CenterX=8 CenterY=6 CenterZ=0 NormalX=0 NormalY=0 NormalZ=1 AngleXU=0 Radius=1
    g3: BSplineCurve PolesCount=3 KnotsCount=2 Degree=2 IsPeriodic=0
    g4: GeomPoint X=0 Y=0 Z=0
    g5: GeomPoint X=8 Y=6 Z=0
    g6: LineSegment StartX=0 StartY=6 StartZ=0 EndX=8 EndY=6 EndZ=0
  constraints (14):
    c: Coincident(g0,g-1)
    c: Distance(g0) = 6
    c: Vertical(g0)
    c: Coincident(g3,g0)
    c: Weight(g1) = 1
    c: Equal(g1,g2)
    c: InternalAlignment(g1,g3)
    c: InternalAlignment(g2,g3)
    c: InternalAlignment(g4,g3)
    c: InternalAlignment(g5,g3)
    c: Block(g3)
    c: Coincident(g6,g0)
    c: Coincident(g6,g3)
    c: Horizontal(g6)
FEATURE [Sketcher::SketchObject] Sketch046
  FullyConstrained = true
  sketch-geometry (7):
    g0: LineSegment StartX=0 StartY=0 StartZ=0 EndX=0 EndY=6 EndZ=0
    g1: Circle CenterX=0 CenterY=0 CenterZ=0 NormalX=0 NormalY=0 NormalZ=1 AngleXU=0 Radius=1
    g2: Circle CenterX=8 CenterY=6 CenterZ=0 NormalX=0 NormalY=0 NormalZ=1 AngleXU=0 Radius=1
    g3: BSplineCurve PolesCount=3 KnotsCount=2 Degree=2 IsPeriodic=0
    g4: GeomPoint X=0 Y=0 Z=0
    g5: GeomPoint X=8 Y=6 Z=0
    g6: LineSegment StartX=0 StartY=6 StartZ=0 EndX=8 EndY=6 EndZ=0
  constraints (14):
    c: Coincident(g0,g-1)
    c: Distance(g0) = 6
    c: Vertical(g0)
    c: Coincident(g3,g0)
    c: Weight(g1) = 1
    c: Equal(g1,g2)
    c: InternalAlignment(g1,g3)
    c: InternalAlignment(g2,g3)
    c: InternalAlignment(g4,g3)
    c: InternalAlignment(g5,g3)
    c: Block(g3)
    c: Coincident(g6,g0)
    c: Coincident(g6,g3)
    c: Horizontal(g6)
FEATURE [Part::Extrusion] Extrude036  label="caseScrewPillarBracket014"
  Base = -> Sketch045
  Dir = (0,0,1)
  DirMode = 2
  FaceMakerClass = Part::FaceMakerBullseye
  LengthFwd = 2.4
  LengthRev = 0
  Placement = pos=(110.7,29,6.77) rot=(0,-1,0;1.5708rad)
  Solid = true
  Symmetric = false
FEATURE [Part::Extrusion] Extrude037  label="caseScrewPillarBracket015"
  Base = -> Sketch046
  Dir = (0,0,1)
  DirMode = 2
  FaceMakerClass = Part::FaceMakerBullseye
  LengthFwd = 2.4
  LengthRev = 0
  Placement = pos=(108.3,29,65.23) rot=(0,1,0;1.5708rad)
  Solid = true
  Symmetric = false
FEATURE [Part::Box] Box013  label="frontCaseScrewPillarBracket002"
  AttacherType = Attacher::AttachEngine3D
  Height = 2.4
  Length = 22
  Placement = pos=(87,28,2.3) rot=(0,0,1;0rad)
  Width = 7
FEATURE [Part::Box] Box014  label="frontCaseScrewPillarBracket003"
  AttacherType = Attacher::AttachEngine3D
  Height = 2.4
  Length = 22
  Placement = pos=(87,28,67.3) rot=(0,0,1;0rad)
  Width = 7
FEATURE [Part::Feature] Face087
  shape: bbox 4.8 x 30.2 x 2e-07 mm, 1 faces, 0 solids (baked)
FEATURE [Part::Revolution] Revolve091  label="frontCaseScrewPost004"
  Angle = 360
  Axis = (0,1,0)
  Base = (0,0,0)
  FaceMakerClass = Part::FaceMakerBullseye
  Placement = pos=(89.5,4.5,3.5) rot=(0,0,1;0rad)
  Solid = false
  Source = -> Face087
  Symmetric = false
FEATURE [Part::Feature] Face088
  shape: bbox 4.8 x 30.2 x 2e-07 mm, 1 faces, 0 solids (baked)
FEATURE [Part::Revolution] Revolve092  label="frontCaseScrewPost005"
  Angle = 360
  Axis = (0,1,0)
  Base = (0,0,0)
  FaceMakerClass = Part::FaceMakerBullseye
  Placement = pos=(89.5,4.5,68.5) rot=(0,0,1;0rad)
  Solid = false
  Source = -> Face088
  Symmetric = false
FEATURE [Part::Feature] Face089
  shape: bbox 3.5 x 30.2 x 2e-07 mm, 1 faces, 0 solids (baked)
FEATURE [Part::Revolution] Revolve093  label="backCaseScrewPost002"
  Angle = 360
  Axis = (0,1,0)
  Base = (0,0,0)
  FaceMakerClass = Part::FaceMakerBullseye
  Placement = pos=(12.5,4.5,10) rot=(0,0,1;0rad)
  Solid = false
  Source = -> Face089
  Symmetric = false
FEATURE [Part::Feature] Face090
  shape: bbox 3.5 x 30.2 x 2e-07 mm, 1 faces, 0 solids (baked)
FEATURE [Part::Revolution] Revolve094  label="backCaseScrewPost003"
  Angle = 360
  Axis = (0,1,0)
  Base = (0,0,0)
  FaceMakerClass = Part::FaceMakerBullseye
  Placement = pos=(12.5,4.5,62) rot=(0,0,1;0rad)
  Solid = false
  Source = -> Face090
  Symmetric = false
FEATURE [Part::Box] Box015  label="Cube011"
  AttacherType = Attacher::AttachEngine3D
  Height = 28.8
  Length = 3
  Placement = pos=(107.3,28,21.6) rot=(0,0,1;0rad)
  Width = 7
FEATURE [Part::Box] Box016  label="Cube012"
  AttacherType = Attacher::AttachEngine3D
  Height = 3
  Length = 7.4
  Placement = pos=(107.3,28,18.6) rot=(0,0,1;0rad)
  Width = 7
FEATURE [Part::Box] Box017  label="Cube013"
  AttacherType = Attacher::AttachEngine3D
  Height = 3
  Length = 7.4
  Placement = pos=(107.3,28,50.4) rot=(0,0,1;0rad)
  Width = 7
FEATURE [Part::Cylinder] Cylinder024
  Angle = 360
  AttacherType = Attacher::AttachEngine3D
  Height = 20
  Placement = pos=(0,0,36.15) rot=(0,0,1;0rad)
  Radius = 14.3
FEATURE [Part::Cylinder] Cylinder025
  Angle = 360
  AttacherType = Attacher::AttachEngine3D
  Height = 10
  Placement = pos=(0,0,36.15) rot=(0,0,1;0rad)
  Radius = 4
FEATURE [Part::MultiFuse] Fusion066  label="removeToCreteHoleForPlugHousing009"
  Placement = pos=(70,19,36) rot=(0,1,0;1.5708rad)
  Shapes = -> [Cylinder024,Cylinder025]
FEATURE [Part::MultiFuse] Fusion065  label="plugHousingBracketHolder002"
  Shapes = -> [Box017,Box015,Box016]
FEATURE [Part::Cut] Cut025  label="plugHousingBracketHolder003"
  Base = -> Fusion065
  Placement = pos=(7,0,0) rot=(0,0,1;0rad)
  Tool = -> Fusion066
FEATURE [Sketcher::SketchObject] Sketch047
  FullyConstrained = false
  Placement = pos=(0,0,0) rot=(1,0,0;1.5708rad)
  sketch-geometry (24):
    g0: ArcOfCircle CenterX=-4 CenterY=-10.5 CenterZ=0 NormalX=0 NormalY=0 NormalZ=1 AngleXU=0 Radius=1.5 StartAngle=6e-16 EndAngle=3.14159
    g1: ArcOfCircle CenterX=-34.2 CenterY=-10.5 CenterZ=0 NormalX=0 NormalY=0 NormalZ=1 AngleXU=0 Radius=1.5 StartAngle=0 EndAngle=3.14159
    g2: ArcOfCircle CenterX=-34.2 CenterY=-27.7 CenterZ=0 NormalX=0 NormalY=0 NormalZ=1 AngleXU=0 Radius=1.5 StartAngle=3.14159 EndAngle=6.28319
    g3: ArcOfCircle CenterX=-4 CenterY=-27.7 CenterZ=0 NormalX=0 NormalY=0 NormalZ=1 AngleXU=0 Radius=1.5 StartAngle=3.1416 EndAngle=6.28319
    g4: ArcOfCircle CenterX=-10 CenterY=-4.3 CenterZ=0 NormalX=0 NormalY=0 NormalZ=1 AngleXU=0 Radius=1.5 StartAngle=2e-16 EndAngle=3.14159
    g5: ArcOfCircle CenterX=-16.1 CenterY=-1.8 CenterZ=0 NormalX=0 NormalY=0 NormalZ=1 AngleXU=0 Radius=1.5 StartAngle=5e-16 EndAngle=3.14159
    g6: ArcOfCircle CenterX=-22.1 CenterY=-1.8 CenterZ=0 NormalX=0 NormalY=0 NormalZ=1 AngleXU=0 Radius=1.5 StartAngle=5e-16 EndAngle=3.14159
    g7: ArcOfCircle CenterX=-28.2 CenterY=-4.3 CenterZ=0 NormalX=0 NormalY=0 NormalZ=1 AngleXU=0 Radius=1.5 StartAngle=2e-16 EndAngle=3.14159
    g8: ArcOfCircle CenterX=-10 CenterY=-33.9 CenterZ=0 NormalX=0 NormalY=0 NormalZ=1 AngleXU=0 Radius=1.5 StartAngle=3.14159 EndAngle=6.28319
    g9: ArcOfCircle CenterX=-16.1 CenterY=-36.4 CenterZ=0 NormalX=0 NormalY=0 NormalZ=1 AngleXU=0 Radius=1.5 StartAngle=3.14159 EndAngle=6.28319
    g10: ArcOfCircle CenterX=-22.1 CenterY=-36.4 CenterZ=0 NormalX=0 NormalY=0 NormalZ=1 AngleXU=0 Radius=1.5 StartAngle=3.14159 EndAngle=6.28319
    g11: ArcOfCircle CenterX=-28.2 CenterY=-33.9 CenterZ=0 NormalX=0 NormalY=0 NormalZ=1 AngleXU=0 Radius=1.5 StartAngle=3.14159 EndAngle=6.28319
    g12: LineSegment StartX=-35.7 StartY=-10.5 StartZ=0 EndX=-35.7 EndY=-27.7 EndZ=0
    g13: LineSegment StartX=-32.7 StartY=-10.5 StartZ=0 EndX=-32.7 EndY=-27.7 EndZ=0
    g14: LineSegment StartX=-29.7 StartY=-33.9 StartZ=0 EndX=-29.7 EndY=-4.3 EndZ=0
    g15: LineSegment StartX=-26.7 StartY=-33.9 StartZ=0 EndX=-26.7 EndY=-4.3 EndZ=0
    g16: LineSegment StartX=-2.5 StartY=-10.5 StartZ=0 EndX=-2.5 EndY=-27.7 EndZ=0
    g17: LineSegment StartX=-8.5 StartY=-4.3 StartZ=0 EndX=-8.5 EndY=-33.9 EndZ=0
    g18: LineSegment StartX=-5.5 StartY=-10.5 StartZ=0 EndX=-5.5 EndY=-27.7 EndZ=0
    g19: LineSegment StartX=-11.5 StartY=-4.3 StartZ=0 EndX=-11.5 EndY=-33.9 EndZ=0
    g20: LineSegment StartX=-14.6 StartY=-1.8 StartZ=0 EndX=-14.6 EndY=-36.4 EndZ=0
    g21: LineSegment StartX=-17.6 StartY=-1.8 StartZ=0 EndX=-17.6 EndY=-36.4 EndZ=0
    g22: LineSegment StartX=-20.6 StartY=-36.4 StartZ=0 EndX=-20.6 EndY=-1.8 EndZ=0
    g23: LineSegment StartX=-23.6 StartY=-1.8 StartZ=0 EndX=-23.6 EndY=-36.4 EndZ=0
  constraints (48):
    c: Block(g0)
    c: Block(g1)
    c: Block(g2)
    c: Block(g3)
    c: Block(g4)
    c: Block(g5)
    c: Block(g6)
    c: Block(g7)
    c: Block(g8)
    c: Block(g9)
    c: Block(g10)
    c: Block(g11)
    c: Coincident(g12,g1)
    c: Coincident(g12,g2)
    c: Vertical(g12)
    c: Coincident(g13,g1)
    c: Coincident(g13,g2)
    c: Vertical(g13)
    c: Coincident(g14,g11)
    c: Coincident(g14,g7)
    c: Vertical(g14)
    c: Coincident(g15,g11)
    c: Coincident(g15,g7)
    c: Vertical(g15)
    c: Coincident(g16,g0)
    c: Coincident(g16,g3)
    c: Vertical(g16)
    c: Coincident(g17,g4)
    c: Coincident(g17,g8)
    c: Vertical(g17)
    c: Coincident(g18,g0)
    c: Coincident(g18,g3)
    c: Vertical(g18)
    c: Coincident(g19,g4)
    c: Coincident(g19,g8)
    c: Vertical(g19)
    c: Coincident(g20,g5)
    c: Coincident(g20,g9)
    c: Vertical(g20)
    c: Coincident(g21,g5)
    c: Coincident(g21,g9)
    c: Vertical(g21)
    c: Coincident(g22,g10)
    c: Coincident(g22,g6)
    c: Vertical(g22)
    c: Coincident(g23,g6)
    c: Coincident(g23,g10)
    c: Vertical(g23)
FEATURE [Part::Extrusion] Extrude038  label="removeToCreateFanGrillHoles001"
  Base = -> Sketch047
  Dir = (0,-1,6e-16)
  DirMode = 2
  FaceMakerClass = Part::FaceMakerBullseye
  LengthFwd = 10
  LengthRev = 0
  Placement = pos=(65.4,44,54.82) rot=(0,0,1;0rad)
  Solid = true
  Symmetric = false
FEATURE [Part::Feature] Wire004
  shape: bbox 11 x 5.2 x 2e-07 mm, 0 faces, 0 solids (baked)
FEATURE [Part::Revolution] Revolve095
  Angle = 360
  Axis = (0,1,0)
  Base = (0,0,0)
  FaceMakerClass = Part::FaceMakerBullseye
  Placement = pos=(30.3,38,19.7) rot=(0,0,1;0rad)
  Solid = true
  Source = -> Wire004
  Symmetric = false
FEATURE [Part::Feature] Wire005
  shape: bbox 11 x 5.2 x 2e-07 mm, 0 faces, 0 solids (baked)
FEATURE [Part::Revolution] Revolve096
  Angle = 360
  Axis = (0,1,0)
  Base = (0,0,0)
  FaceMakerClass = Part::FaceMakerBullseye
  Placement = pos=(30.3,38,51.7) rot=(0,0,1;0rad)
  Solid = true
  Source = -> Wire005
  Symmetric = false
FEATURE [Part::Feature] Wire006
  shape: bbox 11 x 5.2 x 2e-07 mm, 0 faces, 0 solids (baked)
FEATURE [Part::Revolution] Revolve097
  Angle = 360
  Axis = (0,1,0)
  Base = (0,0,0)
  FaceMakerClass = Part::FaceMakerBullseye
  Placement = pos=(62.3,38,51.7) rot=(0,0,1;0rad)
  Solid = true
  Source = -> Wire006
  Symmetric = false
FEATURE [Part::Feature] Wire007
  shape: bbox 11 x 5.2 x 2e-07 mm, 0 faces, 0 solids (baked)
FEATURE [Part::Revolution] Revolve098
  Angle = 360
  Axis = (0,1,0)
  Base = (0,0,0)
  FaceMakerClass = Part::FaceMakerBullseye
  Placement = pos=(62.3,38,19.7) rot=(0,0,1;0rad)
  Solid = true
  Source = -> Wire007
  Symmetric = false
FEATURE [Part::MultiFuse] Fusion067  label="fanScrewHousing002"
  Shapes = -> [Revolve098,Revolve097,Revolve096,Revolve095]
FEATURE [Part::Feature] Face091 .. Face094  x4 (patterned run collapsed; names and placements below)
  shape: bbox 3.5 x 17.8 x 2e-07 mm, 1 faces, 0 solids (baked)
FEATURE [Part::Revolution] Revolve099  label="removeToCreateScrewAndThreadedInsertHole026"
  Angle = 360
  Axis = (0,1,0)
  Base = (0,0,0)
  FaceMakerClass = Part::FaceMakerBullseye
  Placement = pos=(62.3,30.3,19.7) rot=(0,0,1;0rad)
  Solid = false
  Source = -> Face091
  Symmetric = false
FEATURE [Part::Revolution] Revolve100  label="removeToCreateScrewAndThreadedInsertHole027"
  Angle = 360
  Axis = (0,1,0)
  Base = (0,0,0)
  FaceMakerClass = Part::FaceMakerBullseye
  Placement = pos=(62.3,30.3,51.7) rot=(0,0,1;0rad)
  Solid = false
  Source = -> Face092
  Symmetric = false
FEATURE [Part::Revolution] Revolve101  label="removeToCreateScrewAndThreadedInsertHole028"
  Angle = 360
  Axis = (0,1,0)
  Base = (0,0,0)
  FaceMakerClass = Part::FaceMakerBullseye
  Placement = pos=(30.3,30.3,19.7) rot=(0,0,1;0rad)
  Solid = false
  Source = -> Face093
  Symmetric = false
FEATURE [Part::Revolution] Revolve102  label="removeToCreateScrewAndThreadedInsertHole029"
  Angle = 360
  Axis = (0,1,0)
  Base = (0,0,0)
  FaceMakerClass = Part::FaceMakerBullseye
  Placement = pos=(30.3,30.3,51.7) rot=(0,0,1;0rad)
  Solid = false
  Source = -> Face094
  Symmetric = false
FEATURE [Part::MultiFuse] Fusion068  label="createThreadedInsertHolesForFan002"
  Shapes = -> [Revolve099,Revolve100,Revolve101,Revolve102]
FEATURE [Part::Cut] Cut026  label="fanScrewHousing003"
  Base = -> Fusion067
  Tool = -> Fusion068
FEATURE [Sketcher::SketchObject] Sketch048
  FullyConstrained = false
  Placement = pos=(0,0,0) rot=(1,0,0;1.5708rad)
  sketch-geometry (24):
    g0: ArcOfCircle CenterX=-4 CenterY=-10.5 CenterZ=0 NormalX=0 NormalY=0 NormalZ=1 AngleXU=0 Radius=1.5 StartAngle=6e-16 EndAngle=3.14159
    g1: ArcOfCircle CenterX=-34.2 CenterY=-10.5 CenterZ=0 NormalX=0 NormalY=0 NormalZ=1 AngleXU=0 Radius=1.5 StartAngle=0 EndAngle=3.14159
    g2: ArcOfCircle CenterX=-34.2 CenterY=-27.7 CenterZ=0 NormalX=0 NormalY=0 NormalZ=1 AngleXU=0 Radius=1.5 StartAngle=3.14159 EndAngle=6.28319
    g3: ArcOfCircle CenterX=-4 CenterY=-27.7 CenterZ=0 NormalX=0 NormalY=0 NormalZ=1 AngleXU=0 Radius=1.5 StartAngle=3.1416 EndAngle=6.28319
    g4: ArcOfCircle CenterX=-10 CenterY=-4.3 CenterZ=0 NormalX=0 NormalY=0 NormalZ=1 AngleXU=0 Radius=1.5 StartAngle=2e-16 EndAngle=3.14159
    g5: ArcOfCircle CenterX=-16.1 CenterY=-1.8 CenterZ=0 NormalX=0 NormalY=0 NormalZ=1 AngleXU=0 Radius=1.5 StartAngle=5e-16 EndAngle=3.14159
    g6: ArcOfCircle CenterX=-22.1 CenterY=-1.8 CenterZ=0 NormalX=0 NormalY=0 NormalZ=1 AngleXU=0 Radius=1.5 StartAngle=5e-16 EndAngle=3.14159
    g7: ArcOfCircle CenterX=-28.2 CenterY=-4.3 CenterZ=0 NormalX=0 NormalY=0 NormalZ=1 AngleXU=0 Radius=1.5 StartAngle=2e-16 EndAngle=3.14159
    g8: ArcOfCircle CenterX=-10 CenterY=-33.9 CenterZ=0 NormalX=0 NormalY=0 NormalZ=1 AngleXU=0 Radius=1.5 StartAngle=3.14159 EndAngle=6.28319
    g9: ArcOfCircle CenterX=-16.1 CenterY=-36.4 CenterZ=0 NormalX=0 NormalY=0 NormalZ=1 AngleXU=0 Radius=1.5 StartAngle=3.14159 EndAngle=6.28319
    g10: ArcOfCircle CenterX=-22.1 CenterY=-36.4 CenterZ=0 NormalX=0 NormalY=0 NormalZ=1 AngleXU=0 Radius=1.5 StartAngle=3.14159 EndAngle=6.28319
    g11: ArcOfCircle CenterX=-28.2 CenterY=-33.9 CenterZ=0 NormalX=0 NormalY=0 NormalZ=1 AngleXU=0 Radius=1.5 StartAngle=3.14159 EndAngle=6.28319
    g12: LineSegment StartX=-35.7 StartY=-10.5 StartZ=0 EndX=-35.7 EndY=-27.7 EndZ=0
    g13: LineSegment StartX=-32.7 StartY=-10.5 StartZ=0 EndX=-32.7 EndY=-27.7 EndZ=0
    g14: LineSegment StartX=-29.7 StartY=-33.9 StartZ=0 EndX=-29.7 EndY=-4.3 EndZ=0
    g15: LineSegment StartX=-26.7 StartY=-33.9 StartZ=0 EndX=-26.7 EndY=-4.3 EndZ=0
    g16: LineSegment StartX=-2.5 StartY=-10.5 StartZ=0 EndX=-2.5 EndY=-27.7 EndZ=0
    g17: LineSegment StartX=-8.5 StartY=-4.3 StartZ=0 EndX=-8.5 EndY=-33.9 EndZ=0
    g18: LineSegment StartX=-5.5 StartY=-10.5 StartZ=0 EndX=-5.5 EndY=-27.7 EndZ=0
    g19: LineSegment StartX=-11.5 StartY=-4.3 StartZ=0 EndX=-11.5 EndY=-33.9 EndZ=0
    g20: LineSegment StartX=-14.6 StartY=-1.8 StartZ=0 EndX=-14.6 EndY=-36.4 EndZ=0
    g21: LineSegment StartX=-17.6 StartY=-1.8 StartZ=0 EndX=-17.6 EndY=-36.4 EndZ=0
    g22: LineSegment StartX=-20.6 StartY=-36.4 StartZ=0 EndX=-20.6 EndY=-1.8 EndZ=0
    g23: LineSegment StartX=-23.6 StartY=-1.8 StartZ=0 EndX=-23.6 EndY=-36.4 EndZ=0
  constraints (48):
    c: Block(g0)
    c: Block(g1)
    c: Block(g2)
    c: Block(g3)
    c: Block(g4)
    c: Block(g5)
    c: Block(g6)
    c: Block(g7)
    c: Block(g8)
    c: Block(g9)
    c: Block(g10)
    c: Block(g11)
    c: Coincident(g12,g1)
    c: Coincident(g12,g2)
    c: Vertical(g12)
    c: Coincident(g13,g1)
    c: Coincident(g13,g2)
    c: Vertical(g13)
    c: Coincident(g14,g11)
    c: Coincident(g14,g7)
    c: Vertical(g14)
    c: Coincident(g15,g11)
    c: Coincident(g15,g7)
    c: Vertical(g15)
    c: Coincident(g16,g0)
    c: Coincident(g16,g3)
    c: Vertical(g16)
    c: Coincident(g17,g4)
    c: Coincident(g17,g8)
    c: Vertical(g17)
    c: Coincident(g18,g0)
    c: Coincident(g18,g3)
    c: Vertical(g18)
    c: Coincident(g19,g4)
    c: Coincident(g19,g8)
    c: Vertical(g19)
    c: Coincident(g20,g5)
    c: Coincident(g20,g9)
    c: Vertical(g20)
    c: Coincident(g21,g5)
    c: Coincident(g21,g9)
    c: Vertical(g21)
    c: Coincident(g22,g10)
    c: Coincident(g22,g6)
    c: Vertical(g22)
    c: Coincident(g23,g6)
    c: Coincident(g23,g10)
    c: Vertical(g23)
FEATURE [Part::Extrusion] Extrude039  label="removeToCreateFanGrillHoles002"
  Base = -> Sketch048
  Dir = (0,-1,6e-16)
  DirMode = 2
  FaceMakerClass = Part::FaceMakerBullseye
  LengthFwd = 10
  LengthRev = 0
  Placement = pos=(65.4,44,54.82) rot=(0,0,1;0rad)
  Solid = true
  Symmetric = false
FEATURE [Part::Cut] Cut027  label="fanScrewHousing004"
  Base = -> Cut026
  Tool = -> Extrude038
FEATURE [Part::Cut] Cut028  label="top014"
  Base = -> Fillet026
  Tool = -> Extrude039
FEATURE [Part::Feature] Face095 .. Face098  x4 (patterned run collapsed; names and placements below)
  shape: bbox 3.5 x 17.8 x 2e-07 mm, 1 faces, 0 solids (baked)
FEATURE [Part::Revolution] Revolve103  label="removeToCreateScrewAndThreadedInsertHole030"
  Angle = 360
  Axis = (0,1,0)
  Base = (0,0,0)
  FaceMakerClass = Part::FaceMakerBullseye
  Placement = pos=(62.3,30.3,19.7) rot=(0,0,1;0rad)
  Solid = false
  Source = -> Face095
  Symmetric = false
FEATURE [Part::Revolution] Revolve104  label="removeToCreateScrewAndThreadedInsertHole031"
  Angle = 360
  Axis = (0,1,0)
  Base = (0,0,0)
  FaceMakerClass = Part::FaceMakerBullseye
  Placement = pos=(62.3,30.3,51.7) rot=(0,0,1;0rad)
  Solid = false
  Source = -> Face096
  Symmetric = false
FEATURE [Part::Revolution] Revolve105  label="removeToCreateScrewAndThreadedInsertHole032"
  Angle = 360
  Axis = (0,1,0)
  Base = (0,0,0)
  FaceMakerClass = Part::FaceMakerBullseye
  Placement = pos=(30.3,30.3,19.7) rot=(0,0,1;0rad)
  Solid = false
  Source = -> Face097
  Symmetric = false
FEATURE [Part::Revolution] Revolve106  label="removeToCreateScrewAndThreadedInsertHole033"
  Angle = 360
  Axis = (0,1,0)
  Base = (0,0,0)
  FaceMakerClass = Part::FaceMakerBullseye
  Placement = pos=(30.3,30.3,51.7) rot=(0,0,1;0rad)
  Solid = false
  Source = -> Face098
  Symmetric = false
FEATURE [Part::MultiFuse] Fusion069  label="createThreadedInsertHolesForFan003"
  Shapes = -> [Revolve103,Revolve104,Revolve105,Revolve106]
FEATURE [Part::Cut] Cut029  label="top015"
  Base = -> Cut028
  Tool = -> Fusion054
FEATURE [Part::Cut] Cut030  label="fanScrewHousing005"
  Base = -> Cut027
  Tool = -> Fusion069
FEATURE [Part::Cylinder] Cylinder026  label="removeToCreteHoleForPlugHousing010"
  Angle = 360
  AttacherType = Attacher::AttachEngine3D
  Height = 20
  Placement = pos=(-2,19,36) rot=(0,1,0;1.5708rad)
  Radius = 14.3
FEATURE [Part::Box] Box018  label="removeToCreteHoleForPlugHousing011"
  AttacherType = Attacher::AttachEngine3D
  Height = 28.6
  Length = 10
  Placement = pos=(-2,0,21.7) rot=(0,0,1;0rad)
  Width = 19
FEATURE [Part::Box] Box019  label="wireHolderBottomCaseBit"
  AttacherType = Attacher::AttachEngine3D
  Height = 28
  Length = 3
  Placement = pos=(0,0,22) rot=(0,0,1;0rad)
  Width = 21
FEATURE [Part::Cylinder] Cylinder027  label="removeToCreteHoleForPlugHousing012"
  Angle = 360
  AttacherType = Attacher::AttachEngine3D
  Height = 20
  Placement = pos=(-2,19,36) rot=(0,1,0;1.5708rad)
  Radius = 14.3
FEATURE [Part::Cut] Cut031  label="wireHolderBottomCaseBit001"
  Base = -> Box019
  Tool = -> Cylinder027
FEATURE [Part::MultiFuse] Fusion070  label="removeToCreteHoleForPlugHousing013"
  Shapes = -> [Box018,Cylinder026]
FEATURE [Part::Cut] Cut032  label="top016"
  Base = -> Cut029
  Tool = -> Fusion070
FEATURE [Part::Cylinder] Cylinder028
  Angle = 360
  AttacherType = Attacher::AttachEngine3D
  Height = 20
  Placement = pos=(0,0,36.15) rot=(0,0,1;0rad)
  Radius = 14.3
FEATURE [Part::Cylinder] Cylinder029
  Angle = 360
  AttacherType = Attacher::AttachEngine3D
  Height = 10
  Placement = pos=(0,0,36.15) rot=(0,0,1;0rad)
  Radius = 4
FEATURE [Part::MultiFuse] Fusion071  label="removeToCreteHoleForPlugHousing014"
  Placement = pos=(70,19,36) rot=(0,1,0;1.5708rad)
  Shapes = -> [Cylinder028,Cylinder029]
FEATURE [Sketcher::SketchObject] Sketch049  label="topSketch011"
  FullyConstrained = true
  sketch-geometry (4):
    g0: ArcOfCircle CenterX=105 CenterY=19 CenterZ=0 NormalX=0 NormalY=0 NormalZ=1 AngleXU=0 Radius=20.6155 StartAngle=5.54125 EndAngle=6.28319
    g1: ArcOfCircle CenterX=105 CenterY=19 CenterZ=0 NormalX=0 NormalY=0 NormalZ=1 AngleXU=0 Radius=13 StartAngle=5.54125 EndAngle=6.28319
    g2: LineSegment StartX=118 StartY=19 StartZ=0 EndX=125.616 EndY=19 EndZ=0
    g3: LineSegment StartX=114.583 StartY=10.2157 StartZ=0 EndX=120.197 EndY=5.06982 EndZ=0
  constraints (7):
    c: Block(g0)
    c: Block(g1)
    c: Coincident(g2,g1)
    c: Coincident(g2,g0)
    c: Horizontal(g2)
    c: Coincident(g3,g1)
    c: Coincident(g3,g0)
FEATURE [Part::Box] Box020  label="removeToCreteHoleForPlugHousing015"
  AttacherType = Attacher::AttachEngine3D
  Height = 28.6
  Length = 20
  Placement = pos=(106.15,0,21.7) rot=(0,0,1;0rad)
  Width = 19
FEATURE [Part::MultiFuse] Fusion072  label="removeToCreteHoleForPlugHousing016"
  Shapes = -> [Box020,Fusion071]
FEATURE [Part::Cut] Cut033  label="removeToCreteHoleForPlugHousing017"
  Base = -> Cut032
  Tool = -> Fusion072
FEATURE [Part::Cylinder] Cylinder030
  Angle = 360
  AttacherType = Attacher::AttachEngine3D
  Height = 20
  Placement = pos=(0,0,36.15) rot=(0,0,1;0rad)
  Radius = 14.3
FEATURE [Part::Cylinder] Cylinder031
  Angle = 360
  AttacherType = Attacher::AttachEngine3D
  Height = 10
  Placement = pos=(0,0,36.15) rot=(0,0,1;0rad)
  Radius = 4
FEATURE [Part::Box] Box021  label="removeToCreteHoleForPlugHousing019"
  AttacherType = Attacher::AttachEngine3D
  Height = 28.6
  Length = 20
  Placement = pos=(106.15,0,21.7) rot=(0,0,1;0rad)
  Width = 19
FEATURE [Part::MultiFuse] Fusion074  label="removeToCreteHoleForPlugHousing020"
  Placement = pos=(70,19,36) rot=(0,1,0;1.5708rad)
  Shapes = -> [Cylinder030,Cylinder031]
FEATURE [Part::MultiFuse] Fusion073  label="removeToCreteHoleForPlugHousing018"
  Placement = pos=(0,0,28.3) rot=(0,0,1;0rad)
  Shapes = -> [Box021,Fusion074]
FEATURE [Part::Cylinder] Cylinder032
  Angle = 360
  AttacherType = Attacher::AttachEngine3D
  Height = 20
  Placement = pos=(0,0,36.15) rot=(0,0,1;0rad)
  Radius = 14.3
FEATURE [Part::Cylinder] Cylinder033
  Angle = 360
  AttacherType = Attacher::AttachEngine3D
  Height = 10
  Placement = pos=(0,0,36.15) rot=(0,0,1;0rad)
  Radius = 4
FEATURE [Part::Box] Box022  label="removeToCreteHoleForPlugHousing021"
  AttacherType = Attacher::AttachEngine3D
  Height = 28.6
  Length = 20
  Placement = pos=(106.15,0,21.7) rot=(0,0,1;0rad)
  Width = 19
FEATURE [Part::MultiFuse] Fusion076  label="removeToCreteHoleForPlugHousing023"
  Placement = pos=(70,19,36) rot=(0,1,0;1.5708rad)
  Shapes = -> [Cylinder032,Cylinder033]
FEATURE [Part::MultiFuse] Fusion075  label="removeToCreteHoleForPlugHousing022"
  Placement = pos=(0,0,-28.3) rot=(0,0,1;0rad)
  Shapes = -> [Box022,Fusion076]
FEATURE [Part::MultiFuse] Fusion077  label="removeToCreatePlugHousingBottomBit"
  Shapes = -> [Fusion075,Fusion073]
FEATURE [Part::Cylinder] Cylinder034
  Angle = 360
  AttacherType = Attacher::AttachEngine3D
  Height = 20
  Placement = pos=(0,0,36.15) rot=(0,0,1;0rad)
  Radius = 14
FEATURE [Part::Cylinder] Cylinder035
  Angle = 360
  AttacherType = Attacher::AttachEngine3D
  Height = 10
  Placement = pos=(0,0,36.15) rot=(0,0,1;0rad)
  Radius = 4
FEATURE [Part::MultiFuse] Fusion078  label="removeToCreteHoleForPlugHousing024"
  Placement = pos=(70,19,36) rot=(0,1,0;1.5708rad)
  Shapes = -> [Cylinder034,Cylinder035]
FEATURE [Part::MultiFuse] Fusion079  label="removeToCreatePlugHousingBottomBit001"
  Shapes = -> [Fusion078,Fusion077]
FEATURE [Part::Extrusion] Extrude040  label="bottomPlugHousingBit"
  Base = -> Sketch049
  Dir = (0,0,1)
  DirMode = 2
  FaceMakerClass = Part::FaceMakerBullseye
  LengthFwd = 72
  LengthRev = 0
  Solid = true
  Symmetric = false
FEATURE [Part::Cut] Cut034  label="bottomPlugHousingBit001"
  Base = -> Extrude040
  Placement = pos=(-0.09,0,0) rot=(0,0,1;0rad)
  Tool = -> Fusion079
FEATURE [Part::Box] Box023  label="Cube014"
  AttacherType = Attacher::AttachEngine3D
  Height = 16
  Length = 8
  Placement = pos=(12.7,31.52,28) rot=(0,0,1;0rad)
  Width = 4
FEATURE [Part::Cylinder] Cylinder036
  Angle = 360
  AttacherType = Attacher::AttachEngine3D
  Height = 10
  Placement = pos=(0,0,36.15) rot=(0,0,1;0rad)
  Radius = 4
FEATURE [Part::Cylinder] Cylinder037
  Angle = 360
  AttacherType = Attacher::AttachEngine3D
  Height = 20
  Placement = pos=(0,0,36.15) rot=(0,0,1;0rad)
  Radius = 8.2
FEATURE [Part::MultiFuse] Fusion080  label="removeToCreteHoleForPlugHousing025"
  Placement = pos=(-42,19,36) rot=(0,1,0;1.5708rad)
  Shapes = -> [Cylinder037,Cylinder036]
FEATURE [Sketcher::SketchObject] Sketch050  label="topSketch012"
  FullyConstrained = true
  sketch-geometry (4):
    g0: LineSegment StartX=16.8446 StartY=31.512 StartZ=0 EndX=16.3251 EndY=34.4666 EndZ=0
    g1: ArcOfCircle CenterX=19 CenterY=19.2524 CenterZ=0 NormalX=0 NormalY=0 NormalZ=1 AngleXU=0 Radius=15.4476 StartAngle=1.74483 EndAngle=2.72717
    g2: ArcOfCircle CenterX=19 CenterY=19.2524 CenterZ=0 NormalX=0 NormalY=0 NormalZ=1 AngleXU=0 Radius=12.4476 StartAngle=1.74483 EndAngle=2.73189
    g3: LineSegment StartX=4.86004 StartY=25.4725 StartZ=0 EndX=7.58253 EndY=24.2107 EndZ=0
  constraints (7):
    c: Block(g0)
    c: Coincident(g1,g0)
    c: Coincident(g2,g0)
    c: Coincident(g3,g1)
    c: Coincident(g3,g2)
    c: Block(g1)
    c: Block(g2)
FEATURE [Part::Extrusion] Extrude041
  Base = -> Sketch050
  Dir = (0,0,1)
  DirMode = 2
  FaceMakerClass = Part::FaceMakerBullseye
  LengthFwd = 10.6
  LengthRev = 0
  Placement = pos=(0,0,31) rot=(0,0,1;0rad)
  Solid = true
  Symmetric = false
FEATURE [Part::Cut] Cut035
  Base = -> Extrude041
  Placement = pos=(0,0,-0.3) rot=(0,0,1;0rad)
  Tool = -> Fusion080
FEATURE [Part::Cut] Cut036
  Base = -> Box023
  Tool = -> Cut035
FEATURE [Part::Fillet] Fillet027
  Base = -> Cut036
  Edges = 1 edges r=0.7: [Edge13]
FEATURE [Part::Fillet] Fillet028
  Base = -> Fillet027
  Edges = 1 edges r=0.7: [Edge13]
FEATURE [Part::Fillet] Fillet029
  Base = -> Fillet028
  Edges = 1 edges r=0.7: [Edge16]
FEATURE [Part::Fillet] Fillet030
  Base = -> Fillet029
  Edges = 1 edges r=0.7: [Edge11]
FEATURE [Part::Fillet] Fillet031
  Base = -> Fillet030
  Edges = 1 edges r=0.7: [Edge10]
FEATURE [Part::Fillet] Fillet032
  Base = -> Fillet031
  Edges = 1 edges r=1.2: [Edge5]
FEATURE [Part::Fillet] Fillet033
  Base = -> Fillet032
  Edges = 1 edges r=1.2: [Edge12]
FEATURE [Part::Fillet] Fillet034  label="wireHousingRetainer"
  Base = -> Fillet033
  Edges = 1 edges r=2: [Edge1]
  Placement = pos=(0.3,0,0) rot=(0,0,1;0rad)
FEATURE [Part::Feature] Face099
  shape: bbox 3.5 x 17.8 x 2e-07 mm, 1 faces, 0 solids (baked)
FEATURE [Part::Revolution] Revolve107  label="removeToCreateScrewAndThreadedInsertHole034"
  Angle = 360
  Axis = (0,1,0)
  Base = (0,0,0)
  FaceMakerClass = Part::FaceMakerBullseye
  Placement = pos=(12.5,0,10) rot=(0,0,1;0rad)
  Solid = false
  Source = -> Face099
  Symmetric = false
FEATURE [Part::Feature] Face100
  shape: bbox 3.5 x 17.8 x 2e-07 mm, 1 faces, 0 solids (baked)
FEATURE [Part::Revolution] Revolve108  label="removeToCreateScrewAndThreadedInsertHole035"
  Angle = 360
  Axis = (0,1,0)
  Base = (0,0,0)
  FaceMakerClass = Part::FaceMakerBullseye
  Placement = pos=(12.5,0,62) rot=(0,0,1;0rad)
  Solid = false
  Source = -> Face100
  Symmetric = false
FEATURE [Part::Feature] Face101
  shape: bbox 3.5 x 17.8 x 2e-07 mm, 1 faces, 0 solids (baked)
FEATURE [Part::Revolution] Revolve109  label="removeToCreateScrewAndThreadedInsertHole036"
  Angle = 360
  Axis = (0,1,0)
  Base = (0,0,0)
  FaceMakerClass = Part::FaceMakerBullseye
  Placement = pos=(89.5,0,68.5) rot=(0,0,1;0rad)
  Solid = false
  Source = -> Face101
  Symmetric = false
FEATURE [Part::Feature] Face102
  shape: bbox 3.5 x 17.8 x 2e-07 mm, 1 faces, 0 solids (baked)
FEATURE [Part::Revolution] Revolve110  label="removeToCreateScrewAndThreadedInsertHole037"
  Angle = 360
  Axis = (0,1,0)
  Base = (0,0,0)
  FaceMakerClass = Part::FaceMakerBullseye
  Placement = pos=(89.5,0,3.5) rot=(0,0,1;0rad)
  Solid = false
  Source = -> Face102
  Symmetric = false
FEATURE [Part::Feature] Face103
  shape: bbox 3.5 x 17.8 x 2e-07 mm, 1 faces, 0 solids (baked)
FEATURE [Part::Revolution] Revolve111  label="removeToCreateScrewAndThreadedInsertHole038"
  Angle = 360
  Axis = (0,1,0)
  Base = (0,0,0)
  FaceMakerClass = Part::FaceMakerBullseye
  Placement = pos=(109.5,4.7,3.5) rot=(0,0,1;0rad)
  Solid = false
  Source = -> Face103
  Symmetric = false
FEATURE [Part::Feature] Face104
  shape: bbox 3.5 x 17.8 x 2e-07 mm, 1 faces, 0 solids (baked)
FEATURE [Part::Revolution] Revolve112  label="removeToCreateScrewAndThreadedInsertHole039"
  Angle = 360
  Axis = (0,1,0)
  Base = (0,0,0)
  FaceMakerClass = Part::FaceMakerBullseye
  Placement = pos=(109.5,4.7,68.5) rot=(0,0,1;0rad)
  Solid = false
  Source = -> Face104
  Symmetric = false
FEATURE [Part::MultiFuse] Fusion081  label="removeToCreateScrewAndThreadedInsertHole040"
  Shapes = -> [Revolve107,Revolve108,Revolve109,Revolve110,Revolve111,Revolve112]
FEATURE [Part::MultiFuse] Fusion082  label="casePillars002"
  Shapes = -> [Revolve094,Revolve092,Revolve090,Revolve089,Revolve091,Revolve093]
FEATURE [Part::Cut] Cut037  label="casePillars003"
  Base = -> Fusion082
  Tool = -> Fusion081
FEATURE [Sketcher::SketchObject] Sketch051
  FullyConstrained = true
  Placement = pos=(117,19,0) rot=(0.57735,0.57735,0.57735;2.0944rad)
  sketch-geometry (48):
    g0: LineSegment StartX=-49.19 StartY=69.25 StartZ=0 EndX=-49.19 EndY=66.25 EndZ=0
    g1: LineSegment StartX=-49.19 StartY=63.5 StartZ=0 EndX=-49.19 EndY=60.5 EndZ=0
    g2: LineSegment StartX=-49.19 StartY=57.75 StartZ=0 EndX=-49.19 EndY=54.75 EndZ=0
    g3: LineSegment StartX=-49.19 StartY=52 StartZ=0 EndX=-49.19 EndY=49 EndZ=0
    g4: LineSegment StartX=-49.19 StartY=46.25 StartZ=0 EndX=-49.19 EndY=43.25 EndZ=0
    g5: LineSegment StartX=-49.19 StartY=40.5 StartZ=0 EndX=-49.19 EndY=37.5 EndZ=0
    g6: LineSegment StartX=-49.19 StartY=34.5 StartZ=0 EndX=-49.19 EndY=31.5 EndZ=0
    g7: LineSegment StartX=-49.19 StartY=28.75 StartZ=0 EndX=-49.19 EndY=25.75 EndZ=0
    g8: LineSegment StartX=-49.19 StartY=23 StartZ=0 EndX=-49.19 EndY=20 EndZ=0
    g9: LineSegment StartX=-49.19 StartY=17.25 StartZ=0 EndX=-49.19 EndY=14.25 EndZ=0
    g10: LineSegment StartX=-49.19 StartY=11.5 StartZ=0 EndX=-49.19 EndY=8.5 EndZ=0
    g11: LineSegment StartX=-49.19 StartY=5.75 StartZ=0 EndX=-49.19 EndY=2.75 EndZ=0
    g12: ArcOfCircle CenterX=-1.5 CenterY=67.75 CenterZ=0 NormalX=0 NormalY=0 NormalZ=1 AngleXU=0 Radius=1.5 StartAngle=4.71239 EndAngle=7.85398
    g13: ArcOfCircle CenterX=-1.5 CenterY=62 CenterZ=0 NormalX=0 NormalY=0 NormalZ=1 AngleXU=0 Radius=1.5 StartAngle=4.71239 EndAngle=7.85398
    g14: ArcOfCircle CenterX=-1.5 CenterY=56.25 CenterZ=0 NormalX=0 NormalY=0 NormalZ=1 AngleXU=0 Radius=1.5 StartAngle=4.71239 EndAngle=7.85398
    g15: ArcOfCircle CenterX=-11.49 CenterY=50.5 CenterZ=0 NormalX=0 NormalY=0 NormalZ=1 AngleXU=0 Radius=1.5 StartAngle=4.71239 EndAngle=7.85398
    g16: ArcOfCircle CenterX=-16.28 CenterY=44.75 CenterZ=0 NormalX=0 NormalY=0 NormalZ=1 AngleXU=0 Radius=1.5 StartAngle=4.71239 EndAngle=7.85398
    g17: ArcOfCircle CenterX=-18.2337 CenterY=39 CenterZ=0 NormalX=0 NormalY=0 NormalZ=1 AngleXU=0 Radius=1.5 StartAngle=4.71485 EndAngle=7.85398
    g18: ArcOfCircle CenterX=-16.2837 CenterY=27.25 CenterZ=0 NormalX=0 NormalY=0 NormalZ=1 AngleXU=0 Radius=1.5 StartAngle=4.71485 EndAngle=7.85398
    g19: ArcOfCircle CenterX=-18.2337 CenterY=33 CenterZ=0 NormalX=0 NormalY=0 NormalZ=1 AngleXU=0 Radius=1.5 StartAngle=4.71485 EndAngle=7.85398
    g20: ArcOfCircle CenterX=-11.49 CenterY=21.5 CenterZ=0 NormalX=0 NormalY=0 NormalZ=1 AngleXU=0 Radius=1.5 StartAngle=4.71239 EndAngle=7.85398
    g21: ArcOfCircle CenterX=-1.5 CenterY=4.25 CenterZ=0 NormalX=0 NormalY=0 NormalZ=1 AngleXU=0 Radius=1.5 StartAngle=4.71239 EndAngle=7.85398
    g22: ArcOfCircle CenterX=-1.5 CenterY=10 CenterZ=0 NormalX=0 NormalY=0 NormalZ=1 AngleXU=0 Radius=1.5 StartAngle=4.71239 EndAngle=7.85398
    g23: ArcOfCircle CenterX=-1.5 CenterY=15.75 CenterZ=0 NormalX=0 NormalY=0 NormalZ=1 AngleXU=0 Radius=1.5 StartAngle=4.71239 EndAngle=7.85398
    g24: LineSegment StartX=-49.19 StartY=69.25 StartZ=0 EndX=-1.5 EndY=69.25 EndZ=0
    g25: LineSegment StartX=-49.19 StartY=66.25 StartZ=0 EndX=-1.5 EndY=66.25 EndZ=0
    g26: LineSegment StartX=-49.19 StartY=63.5 StartZ=0 EndX=-1.5 EndY=63.5 EndZ=0
    g27: LineSegment StartX=-49.19 StartY=60.5 StartZ=0 EndX=-1.5 EndY=60.5 EndZ=0
    g28: LineSegment StartX=-49.19 StartY=57.75 StartZ=0 EndX=-1.5 EndY=57.75 EndZ=0
    g29: LineSegment StartX=-49.19 StartY=54.75 StartZ=0 EndX=-1.5 EndY=54.75 EndZ=0
    g30: LineSegment StartX=-49.19 StartY=52 StartZ=0 EndX=-11.49 EndY=52 EndZ=0
    g31: LineSegment StartX=-49.19 StartY=49 StartZ=0 EndX=-11.49 EndY=49 EndZ=0
    g32: LineSegment StartX=-49.19 StartY=46.25 StartZ=0 EndX=-16.28 EndY=46.25 EndZ=0
    g33: LineSegment StartX=-49.19 StartY=43.25 StartZ=0 EndX=-16.28 EndY=43.25 EndZ=0
    g34: LineSegment StartX=-49.19 StartY=40.5 StartZ=0 EndX=-18.2337 EndY=40.5 EndZ=0
    g35: LineSegment StartX=-49.19 StartY=37.5 StartZ=0 EndX=-18.23 EndY=37.5 EndZ=0
    g36: LineSegment StartX=-49.19 StartY=34.5 StartZ=0 EndX=-18.2337 EndY=34.5 EndZ=0
    g37: LineSegment StartX=-49.19 StartY=31.5 StartZ=0 EndX=-18.23 EndY=31.5 EndZ=0
    g38: LineSegment StartX=-49.19 StartY=28.75 StartZ=0 EndX=-16.2837 EndY=28.75 EndZ=0
    g39: LineSegment StartX=-49.19 StartY=25.75 StartZ=0 EndX=-16.28 EndY=25.75 EndZ=0
    g40: LineSegment StartX=-49.19 StartY=23 StartZ=0 EndX=-11.49 EndY=23 EndZ=0
    g41: LineSegment StartX=-49.19 StartY=20 StartZ=0 EndX=-11.49 EndY=20 EndZ=0
    g42: LineSegment StartX=-49.19 StartY=17.25 StartZ=0 EndX=-1.5 EndY=17.25 EndZ=0
    g43: LineSegment StartX=-49.19 StartY=14.25 StartZ=0 EndX=-1.5 EndY=14.25 EndZ=0
    g44: LineSegment StartX=-49.19 StartY=11.5 StartZ=0 EndX=-1.5 EndY=11.5 EndZ=0
    g45: LineSegment StartX=-49.19 StartY=8.5 StartZ=0 EndX=-1.5 EndY=8.5 EndZ=0
    g46: LineSegment StartX=-49.19 StartY=5.75 StartZ=0 EndX=-1.5 EndY=5.75 EndZ=0
    g47: LineSegment StartX=-49.19 StartY=2.75 StartZ=0 EndX=-1.5 EndY=2.75 EndZ=0
  constraints (120):
    c: Vertical(g0)
    c: Distance(g0) = 3
    c: Block(g0)
    c: Vertical(g1)
    c: Distance(g1) = 3
    c: Vertical(g2)
    c: Equal(g0,g2) = 3
    c: Block(g2)
    c: Vertical(g3)
    c: Equal(g1,g3) = 3
    c: Vertical(g4)
    c: Equal(g0,g4) = 3
    c: Block(g4)
    c: Vertical(g5)
    c: Equal(g1,g5) = 3
    c: Vertical(g6)
    c: Equal(g0,g6) = 3
    c: Block(g6)
    c: Vertical(g7)
    c: Equal(g1,g7) = 3
    c: Vertical(g8)
    c: Equal(g0,g8) = 3
    c: Block(g8)
    c: Vertical(g9)
    c: Equal(g1,g9) = 3
    c: Vertical(g10)
    c: Equal(g0,g10) = 3
    c: Block(g10)
    c: Vertical(g11)
    c: Equal(g1,g11) = 3
    c: Block(g12)
    c: Block(g13)
    c: Block(g14)
    c: Block(g15)
    c: Block(g16)
    c: Block(g17)
    c: Block(g18)
    c: Block(g19)
    c: Block(g20)
    c: Block(g21)
    c: Block(g22)
    c: Block(g23)
    c: Block(g11)
    c: Block(g9)
    c: Block(g7)
    c: Block(g5)
    c: Block(g3)
    c: Block(g1)
    c: Coincident(g24,g0)
    c: Coincident(g24,g12)
    c: Horizontal(g24)
    c: Coincident(g25,g0)
    c: Coincident(g25,g12)
    c: Horizontal(g25)
    c: Coincident(g26,g1)
    c: Coincident(g26,g13)
    c: Horizontal(g26)
    c: Coincident(g27,g1)
    c: Coincident(g27,g13)
    c: Horizontal(g27)
    c: Coincident(g28,g2)
    c: Coincident(g28,g14)
    c: Horizontal(g28)
    c: Coincident(g29,g2)
    c: Coincident(g29,g14)
    c: Horizontal(g29)
    c: Coincident(g30,g3)
    c: Coincident(g30,g15)
    c: Horizontal(g30)
    c: Coincident(g31,g3)
    c: Coincident(g31,g15)
    c: Horizontal(g31)
    c: Coincident(g32,g4)
    c: Coincident(g32,g16)
    c: Horizontal(g32)
    c: Coincident(g33,g4)
    c: Coincident(g33,g16)
    c: Horizontal(g33)
    c: Coincident(g34,g5)
    c: Coincident(g34,g17)
    c: Horizontal(g34)
    c: Coincident(g35,g5)
    c: Coincident(g35,g17)
    c: Horizontal(g35)
    c: Coincident(g36,g6)
    c: Coincident(g36,g19)
    c: Horizontal(g36)
    c: Coincident(g37,g6)
    c: Coincident(g37,g19)
    c: Horizontal(g37)
    c: Coincident(g38,g7)
    c: Coincident(g38,g18)
    c: Horizontal(g38)
    c: Coincident(g39,g7)
    c: Coincident(g39,g18)
    c: Horizontal(g39)
    c: Coincident(g40,g8)
    c: Coincident(g40,g20)
    c: Horizontal(g40)
    c: Coincident(g41,g8)
    c: Coincident(g41,g20)
    c: Horizontal(g41)
    c: Coincident(g42,g9)
    c: Coincident(g42,g23)
    c: Horizontal(g42)
    c: Coincident(g43,g9)
    c: Coincident(g43,g23)
    c: Horizontal(g43)
    c: Coincident(g44,g10)
    c: Coincident(g44,g22)
    c: Horizontal(g44)
    c: Coincident(g45,g10)
    c: Coincident(g45,g22)
    c: Horizontal(g45)
    c: Coincident(g46,g11)
    c: Coincident(g46,g21)
    c: Horizontal(g46)
    c: Coincident(g47,g11)
    c: Coincident(g47,g21)
    c: Horizontal(g47)
FEATURE [Part::Extrusion] Extrude042
  Base = -> Sketch051
  Dir = (1,-2e-16,2e-16)
  DirMode = 2
  FaceMakerClass = Part::FaceMakerBullseye
  LengthFwd = 19
  LengthRev = 0
  Placement = pos=(-19,0,0) rot=(0,0,1;0rad)
  Solid = true
  Symmetric = false
FEATURE [Part::Fillet] Fillet035  label="removeToCreateVentalationHoles"
  Base = -> Extrude042
  Edges = <same value as first occurrence — deduplicated (x6 in doc)>
  Placement = pos=(7,0,0) rot=(0,0,1;0rad)
FEATURE [Part::Cut] Cut038  label="top017"
  Base = -> Cut033
  Tool = -> Fillet035
FEATURE [Sketcher::SketchObject] Sketch052  label="bottomSketch001"
  FullyConstrained = true
  sketch-geometry (45):
    g0: LineSegment StartX=6.29999 StartY=8 StartZ=0 EndX=3.29999 EndY=8 EndZ=0
    g1: LineSegment StartX=3.29999 StartY=8 StartZ=0 EndX=3.29999 EndY=-6.03275e-07 EndZ=0
    g2: ArcOfCircle CenterX=8.29999 CenterY=5 CenterZ=0 NormalX=0 NormalY=0 NormalZ=1 AngleXU=0 Radius=2 StartAngle=3.14159 EndAngle=4.71239
    g3: LineSegment StartX=6.29999 StartY=8 StartZ=0 EndX=6.29999 EndY=5 EndZ=0
    g4: ArcOfCircle CenterX=105 CenterY=19 CenterZ=0 NormalX=0 NormalY=0 NormalZ=1 AngleXU=0 Radius=12.7 StartAngle=4.71239 EndAngle=5.94289
    g5-g11: Circle x7 (B-spline internal-alignment scaffolding for g12; pole/knot coordinates omitted)
    g12: BSplineCurve PolesCount=7 KnotsCount=5 Degree=3 IsPeriodic=0
    g13-g17: GeomPoint x5 (B-spline internal-alignment scaffolding for g12; pole/knot coordinates omitted)
    g18: ArcOfCircle CenterX=105 CenterY=19 CenterZ=0 NormalX=0 NormalY=0 NormalZ=1 AngleXU=0 Radius=15.7 StartAngle=5.81226 EndAngle=6.28319
    g19: BSplineCurve PolesCount=5 KnotsCount=3 Degree=3 IsPeriodic=0
    g20: LineSegment StartX=8.29999 StartY=3 StartZ=0 EndX=101.7 EndY=3 EndZ=0
    g21: LineSegment StartX=3.29999 StartY=-6.03275e-07 StartZ=0 EndX=105 EndY=-6.03275e-07 EndZ=0
    g22: LineSegment StartX=120.974 StartY=8.71251 StartZ=0 EndX=122.332 EndY=7.83778 EndZ=0
    g23: LineSegment StartX=105 StartY=-6.03274e-07 StartZ=0 EndX=113 EndY=-6.03274e-07 EndZ=0
    g24: ArcOfCircle CenterX=105 CenterY=19 CenterZ=0 NormalX=0 NormalY=0 NormalZ=1 AngleXU=0 Radius=20.6155 StartAngle=5.11091 EndAngle=5.71103
    g25: ArcOfCircle CenterX=117.7 CenterY=19 CenterZ=0 NormalX=0 NormalY=0 NormalZ=1 AngleXU=0 Radius=3 StartAngle=1.2e-15 EndAngle=2.10468
    g26: Circle CenterX=116.345 CenterY=16.3232 CenterZ=0 NormalX=0 NormalY=0 NormalZ=1 AngleXU=0 Radius=1
    g27: Circle CenterX=117.24 CenterY=15.7584 CenterZ=0 NormalX=0 NormalY=0 NormalZ=1 AngleXU=0 Radius=1
    g28: Circle CenterX=116.972 CenterY=14.7612 CenterZ=0 NormalX=0 NormalY=0 NormalZ=1 AngleXU=0 Radius=1
    g29: BSplineCurve PolesCount=3 KnotsCount=2 Degree=2 IsPeriodic=0
    g30: GeomPoint X=116.345 Y=16.3232 Z=0
    g31: GeomPoint X=116.972 Y=14.7612 Z=0
    g32: Circle CenterX=115.828 CenterY=17.157 CenterZ=0 NormalX=0 NormalY=0 NormalZ=1 AngleXU=0 Radius=1
    g33: Circle CenterX=115.841 CenterY=16.639 CenterZ=0 NormalX=0 NormalY=0 NormalZ=1 AngleXU=0 Radius=1
    g34: Circle CenterX=116.345 CenterY=16.3232 CenterZ=0 NormalX=0 NormalY=0 NormalZ=1 AngleXU=0 Radius=1
    g35: BSplineCurve PolesCount=3 KnotsCount=2 Degree=2 IsPeriodic=0
    g36: GeomPoint X=115.828 Y=17.157 Z=0
    g37: GeomPoint X=116.345 Y=16.3232 Z=0
    g38: LineSegment StartX=115.828 StartY=17.157 StartZ=0 EndX=115.828 EndY=20.8307 EndZ=0
    g39: Circle CenterX=115.828 CenterY=20.8307 CenterZ=0 NormalX=0 NormalY=0 NormalZ=1 AngleXU=0 Radius=1
    g40: Circle CenterX=115.831 CenterY=21.3396 CenterZ=0 NormalX=0 NormalY=0 NormalZ=1 AngleXU=0 Radius=1
    g41: Circle CenterX=116.173 CenterY=21.5825 CenterZ=0 NormalX=0 NormalY=0 NormalZ=1 AngleXU=0 Radius=1
    g42: BSplineCurve PolesCount=3 KnotsCount=2 Degree=2 IsPeriodic=0
    g43: GeomPoint X=115.828 Y=20.8307 Z=0
    g44: GeomPoint X=116.173 Y=21.5825 Z=0
  constraints (70):
    c: Horizontal(g0)
    c: Distance(g0) = 3
    c: Coincident(g1,g0)
    c: Vertical(g1)
    c: Block(g2)
    c: Block(g0)
    c: Coincident(g3,g0)
    c: Coincident(g3,g2)
    c: Vertical(g3)
    c: Block(g1)
    c: Block(g4)
    c: Coincident(g19,g4)
    c: Block(g19)
    c: Equal(g5, g6-g11) x6
    c: InternalAlignment(g5-g11 -> g12) x7
    c: InternalAlignment(g13-g17 -> g12) x5
    c: Block(g12)
    c: Coincident(g18,g12)
    c: Block(g18)
    c: Coincident(g20,g2)
    c: Coincident(g20,g19)
    c: Horizontal(g20)
    c: Distance(g20) = 93.4
    c: Coincident(g21,g1)
    c: Horizontal(g21)
    c: Distance(g21) = 101.7
    c: Horizontal(g23)
    c: Distance(g23) = 8
    c: Coincident(g24,g23)
    c: Block(g23)
    c: Coincident(g22,g24)
    c: Block(g24)
    c: Block(g22)
    c: Distance(g22) = 1.61553
    c: Coincident(g25,g18)
    c: Block(g25)
    c: Weight(g26) = 1
    c: Equal(g26,g27)
    c: Equal(g26,g28)
    c: Coincident(g29,g4)
    c: InternalAlignment(g26,g29)
    c: InternalAlignment(g27,g29)
    c: InternalAlignment(g28,g29)
    c: InternalAlignment(g30,g29)
    c: InternalAlignment(g31,g29)
    c: Block(g29)
    c: Weight(g32) = 1
    c: Equal(g32,g33)
    c: Equal(g32,g34)
    c: Coincident(g35,g29)
    c: InternalAlignment(g32,g35)
    c: InternalAlignment(g33,g35)
    c: InternalAlignment(g34,g35)
    c: InternalAlignment(g36,g35)
    c: InternalAlignment(g37,g35)
    c: Block(g35)
    c: Coincident(g38,g35)
    c: Vertical(g38)
    c: Block(g38)
    c: Coincident(g42,g38)
    c: Weight(g39) = 1
    c: Equal(g39,g40)
    c: Equal(g39,g41)
    c: Coincident(g42,g25)
    c: InternalAlignment(g39,g42)
    c: InternalAlignment(g40,g42)
    c: InternalAlignment(g41,g42)
    c: InternalAlignment(g43,g42)
    c: InternalAlignment(g44,g42)
    c: Block(g42)
FEATURE [Part::Extrusion] Extrude043  label="bottom010"
  Base = -> Sketch052
  Dir = (0,0,1)
  DirMode = 2
  FaceMakerClass = Part::FaceMakerBullseye
  LengthFwd = 71.4
  LengthRev = 0
  Placement = pos=(0,0,0.3) rot=(0,0,1;0rad)
  Solid = true
  Symmetric = false
FEATURE [Sketcher::SketchObject] Sketch053  label="topSketch013"
  FullyConstrained = true
  sketch-geometry (22):
    g0: LineSegment StartX=5.21097e-06 StartY=3 StartZ=0 EndX=5.21097e-06 EndY=19 EndZ=0
    g1: ArcOfCircle CenterX=19 CenterY=19 CenterZ=0 NormalX=0 NormalY=0 NormalZ=1 AngleXU=0 Radius=19 StartAngle=1.5708 EndAngle=3.14159
    g2: ArcOfCircle CenterX=19 CenterY=19 CenterZ=0 NormalX=0 NormalY=0 NormalZ=1 AngleXU=0 Radius=16 StartAngle=1.5708 EndAngle=3.14159
    g3: LineSegment StartX=114 StartY=35 StartZ=0 EndX=19 EndY=35 EndZ=0
    g4: LineSegment StartX=5.21097e-06 StartY=3 StartZ=0 EndX=5.21097e-06 EndY=0 EndZ=0
    g5: LineSegment StartX=3 StartY=0 StartZ=0 EndX=5.21097e-06 EndY=0 EndZ=0
    g6: LineSegment StartX=3 StartY=19 StartZ=0 EndX=3 EndY=0 EndZ=0
    g7: LineSegment StartX=19 StartY=38 StartZ=0 EndX=124 EndY=38 EndZ=0
    g8: Circle CenterX=119 CenterY=35 CenterZ=0 NormalX=0 NormalY=0 NormalZ=1 AngleXU=0 Radius=1
    g9: Circle CenterX=121 CenterY=35 CenterZ=0 NormalX=0 NormalY=0 NormalZ=1 AngleXU=0 Radius=1
    g10: Circle CenterX=121 CenterY=33 CenterZ=0 NormalX=0 NormalY=0 NormalZ=1 AngleXU=0 Radius=1
    g11: BSplineCurve PolesCount=3 KnotsCount=2 Degree=2 IsPeriodic=0
    g12: GeomPoint X=119 Y=35 Z=0
    g13: GeomPoint X=121 Y=33 Z=0
    g14: LineSegment StartX=119 StartY=35 StartZ=0 EndX=114 EndY=35 EndZ=0
    g15: ArcOfCircle CenterX=105 CenterY=19 CenterZ=0 NormalX=0 NormalY=0 NormalZ=1 AngleXU=0 Radius=16 StartAngle=5.60905 EndAngle=6.28319
    g16: LineSegment StartX=121 StartY=33 StartZ=0 EndX=121 EndY=19 EndZ=0
    g17: LineSegment StartX=117.5 StartY=9.01251 StartZ=0 EndX=121.163 EndY=9.0125 EndZ=0
    g18: ArcOfCircle CenterX=105 CenterY=19 CenterZ=0 NormalX=0 NormalY=0 NormalZ=1 AngleXU=0 Radius=20.6155 StartAngle=5.7297 EndAngle=6.28319
    g19: LineSegment StartX=121.163 StartY=9.0125 StartZ=0 EndX=122.538 EndY=8.16329 EndZ=0
    g20: LineSegment StartX=124 StartY=38 StartZ=0 EndX=125.616 EndY=38 EndZ=0
    g21: LineSegment StartX=125.616 StartY=19 StartZ=0 EndX=125.616 EndY=38 EndZ=0
  constraints (50):
    c: Vertical(g0)
    c: Block(g0)
    c: Coincident(g1,g0)
    c: Block(g1)
    c: Coincident(g2,g1)
    c: Block(g2)
    c: Coincident(g3,g2)
    c: Horizontal(g3)
    c: Tangent(g3,g2)
    c: Coincident(g4,g0)
    c: Distance(g4) = 3
    c: Vertical(g4)
    c: Coincident(g5,g4)
    c: Horizontal(g5)
    c: Coincident(g6,g2)
    c: Coincident(g6,g5)
    c: Vertical(g6)
    c: Horizontal(g7)
    c: Distance(g7) = 105
    c: Coincident(g7,g1)
    c: Block(g3)
    c: Weight(g8) = 1
    c: Equal(g8,g9)
    c: Equal(g8,g10)
    c: InternalAlignment(g8,g11)
    c: InternalAlignment(g9,g11)
    c: InternalAlignment(g10,g11)
    c: InternalAlignment(g12,g11)
    c: InternalAlignment(g13,g11)
    c: Block(g11)
    c: Coincident(g14,g11)
    c: Coincident(g14,g3)
    c: Horizontal(g14)
    c: Block(g15)
    c: Coincident(g16,g11)
    c: Coincident(g16,g15)
    c: Vertical(g16)
    c: Distance(g16) = 14
    c: Coincident(g17,g15)
    c: Block(g18)
    c: Coincident(g19,g18)
    c: Coincident(g20,g7)
    c: Horizontal(g20)
    c: Vertical(g21)
    c: Coincident(g20,g21)
    c: Block(g20)
    c: Block(g21)
    c: Block(g19)
    c: Block(g17)
    c: Distance(g20) = 1.61553
FEATURE [Part::Extrusion] Extrude044
  Base = -> Sketch053
  Dir = (0,0,1)
  DirMode = 2
  FaceMakerClass = Part::FaceMakerBullseye
  LengthFwd = 72
  LengthRev = 0
  Solid = true
  Symmetric = false
FEATURE [Part::Fillet] Fillet036  label="top018"
  Base = -> Extrude044
  Edges = 1 edges r=2: [Edge41]
FEATURE [Sketcher::SketchObject] Sketch054
  FullyConstrained = false
  Placement = pos=(0,0,0) rot=(1,0,0;1.5708rad)
  sketch-geometry (24):
    g0: ArcOfCircle CenterX=-4 CenterY=-10.5 CenterZ=0 NormalX=0 NormalY=0 NormalZ=1 AngleXU=0 Radius=1.5 StartAngle=6e-16 EndAngle=3.14159
    g1: ArcOfCircle CenterX=-34.2 CenterY=-10.5 CenterZ=0 NormalX=0 NormalY=0 NormalZ=1 AngleXU=0 Radius=1.5 StartAngle=0 EndAngle=3.14159
    g2: ArcOfCircle CenterX=-34.2 CenterY=-27.7 CenterZ=0 NormalX=0 NormalY=0 NormalZ=1 AngleXU=0 Radius=1.5 StartAngle=3.14159 EndAngle=6.28319
    g3: ArcOfCircle CenterX=-4 CenterY=-27.7 CenterZ=0 NormalX=0 NormalY=0 NormalZ=1 AngleXU=0 Radius=1.5 StartAngle=3.1416 EndAngle=6.28319
    g4: ArcOfCircle CenterX=-10 CenterY=-4.3 CenterZ=0 NormalX=0 NormalY=0 NormalZ=1 AngleXU=0 Radius=1.5 StartAngle=2e-16 EndAngle=3.14159
    g5: ArcOfCircle CenterX=-16.1 CenterY=-1.8 CenterZ=0 NormalX=0 NormalY=0 NormalZ=1 AngleXU=0 Radius=1.5 StartAngle=5e-16 EndAngle=3.14159
    g6: ArcOfCircle CenterX=-22.1 CenterY=-1.8 CenterZ=0 NormalX=0 NormalY=0 NormalZ=1 AngleXU=0 Radius=1.5 StartAngle=5e-16 EndAngle=3.14159
    g7: ArcOfCircle CenterX=-28.2 CenterY=-4.3 CenterZ=0 NormalX=0 NormalY=0 NormalZ=1 AngleXU=0 Radius=1.5 StartAngle=2e-16 EndAngle=3.14159
    g8: ArcOfCircle CenterX=-10 CenterY=-33.9 CenterZ=0 NormalX=0 NormalY=0 NormalZ=1 AngleXU=0 Radius=1.5 StartAngle=3.14159 EndAngle=6.28319
    g9: ArcOfCircle CenterX=-16.1 CenterY=-36.4 CenterZ=0 NormalX=0 NormalY=0 NormalZ=1 AngleXU=0 Radius=1.5 StartAngle=3.14159 EndAngle=6.28319
    g10: ArcOfCircle CenterX=-22.1 CenterY=-36.4 CenterZ=0 NormalX=0 NormalY=0 NormalZ=1 AngleXU=0 Radius=1.5 StartAngle=3.14159 EndAngle=6.28319
    g11: ArcOfCircle CenterX=-28.2 CenterY=-33.9 CenterZ=0 NormalX=0 NormalY=0 NormalZ=1 AngleXU=0 Radius=1.5 StartAngle=3.14159 EndAngle=6.28319
    g12: LineSegment StartX=-35.7 StartY=-10.5 StartZ=0 EndX=-35.7 EndY=-27.7 EndZ=0
    g13: LineSegment StartX=-32.7 StartY=-10.5 StartZ=0 EndX=-32.7 EndY=-27.7 EndZ=0
    g14: LineSegment StartX=-29.7 StartY=-33.9 StartZ=0 EndX=-29.7 EndY=-4.3 EndZ=0
    g15: LineSegment StartX=-26.7 StartY=-33.9 StartZ=0 EndX=-26.7 EndY=-4.3 EndZ=0
    g16: LineSegment StartX=-2.5 StartY=-10.5 StartZ=0 EndX=-2.5 EndY=-27.7 EndZ=0
    g17: LineSegment StartX=-8.5 StartY=-4.3 StartZ=0 EndX=-8.5 EndY=-33.9 EndZ=0
    g18: LineSegment StartX=-5.5 StartY=-10.5 StartZ=0 EndX=-5.5 EndY=-27.7 EndZ=0
    g19: LineSegment StartX=-11.5 StartY=-4.3 StartZ=0 EndX=-11.5 EndY=-33.9 EndZ=0
    g20: LineSegment StartX=-14.6 StartY=-1.8 StartZ=0 EndX=-14.6 EndY=-36.4 EndZ=0
    g21: LineSegment StartX=-17.6 StartY=-1.8 StartZ=0 EndX=-17.6 EndY=-36.4 EndZ=0
    g22: LineSegment StartX=-20.6 StartY=-36.4 StartZ=0 EndX=-20.6 EndY=-1.8 EndZ=0
    g23: LineSegment StartX=-23.6 StartY=-1.8 StartZ=0 EndX=-23.6 EndY=-36.4 EndZ=0
  constraints (48):
    c: Block(g0)
    c: Block(g1)
    c: Block(g2)
    c: Block(g3)
    c: Block(g4)
    c: Block(g5)
    c: Block(g6)
    c: Block(g7)
    c: Block(g8)
    c: Block(g9)
    c: Block(g10)
    c: Block(g11)
    c: Coincident(g12,g1)
    c: Coincident(g12,g2)
    c: Vertical(g12)
    c: Coincident(g13,g1)
    c: Coincident(g13,g2)
    c: Vertical(g13)
    c: Coincident(g14,g11)
    c: Coincident(g14,g7)
    c: Vertical(g14)
    c: Coincident(g15,g11)
    c: Coincident(g15,g7)
    c: Vertical(g15)
    c: Coincident(g16,g0)
    c: Coincident(g16,g3)
    c: Vertical(g16)
    c: Coincident(g17,g4)
    c: Coincident(g17,g8)
    c: Vertical(g17)
    c: Coincident(g18,g0)
    c: Coincident(g18,g3)
    c: Vertical(g18)
    c: Coincident(g19,g4)
    c: Coincident(g19,g8)
    c: Vertical(g19)
    c: Coincident(g20,g5)
    c: Coincident(g20,g9)
    c: Vertical(g20)
    c: Coincident(g21,g5)
    c: Coincident(g21,g9)
    c: Vertical(g21)
    c: Coincident(g22,g10)
    c: Coincident(g22,g6)
    c: Vertical(g22)
    c: Coincident(g23,g6)
    c: Coincident(g23,g10)
    c: Vertical(g23)
FEATURE [Part::Extrusion] Extrude045  label="removeToCreateFanGrillHoles003"
  Base = -> Sketch054
  Dir = (0,-1,6e-16)
  DirMode = 2
  FaceMakerClass = Part::FaceMakerBullseye
  LengthFwd = 10
  LengthRev = 0
  Placement = pos=(65.4,44,54.82) rot=(0,0,1;0rad)
  Solid = true
  Symmetric = false
FEATURE [Part::Feature] Face105 .. Face108  x4 (patterned run collapsed; names and placements below)
  shape: bbox 3.5 x 17.8 x 2e-07 mm, 1 faces, 0 solids (baked)
FEATURE [Part::Revolution] Revolve113  label="removeToCreateScrewAndThreadedInsertHole041"
  Angle = 360
  Axis = (0,1,0)
  Base = (0,0,0)
  FaceMakerClass = Part::FaceMakerBullseye
  Placement = pos=(62.3,30.3,19.7) rot=(0,0,1;0rad)
  Solid = false
  Source = -> Face105
  Symmetric = false
FEATURE [Part::Revolution] Revolve114  label="removeToCreateScrewAndThreadedInsertHole042"
  Angle = 360
  Axis = (0,1,0)
  Base = (0,0,0)
  FaceMakerClass = Part::FaceMakerBullseye
  Placement = pos=(62.3,30.3,51.7) rot=(0,0,1;0rad)
  Solid = false
  Source = -> Face106
  Symmetric = false
FEATURE [Part::Revolution] Revolve115  label="removeToCreateScrewAndThreadedInsertHole043"
  Angle = 360
  Axis = (0,1,0)
  Base = (0,0,0)
  FaceMakerClass = Part::FaceMakerBullseye
  Placement = pos=(30.3,30.3,19.7) rot=(0,0,1;0rad)
  Solid = false
  Source = -> Face107
  Symmetric = false
FEATURE [Part::Revolution] Revolve116  label="removeToCreateScrewAndThreadedInsertHole044"
  Angle = 360
  Axis = (0,1,0)
  Base = (0,0,0)
  FaceMakerClass = Part::FaceMakerBullseye
  Placement = pos=(30.3,30.3,51.7) rot=(0,0,1;0rad)
  Solid = false
  Source = -> Face108
  Symmetric = false
FEATURE [Part::MultiFuse] Fusion083  label="createThreadedInsertHolesForFan004"
  Shapes = -> [Revolve113,Revolve114,Revolve115,Revolve116]
FEATURE [Part::Box] Box024  label="removeToCreteHoleForPlugHousing026"
  AttacherType = Attacher::AttachEngine3D
  Height = 28.6
  Length = 10
  Placement = pos=(-2,0,21.7) rot=(0,0,1;0rad)
  Width = 19
FEATURE [Part::Cylinder] Cylinder038  label="removeToCreteHoleForPlugHousing027"
  Angle = 360
  AttacherType = Attacher::AttachEngine3D
  Height = 20
  Placement = pos=(-2,19,36) rot=(0,1,0;1.5708rad)
  Radius = 14.3
FEATURE [Part::MultiFuse] Fusion084  label="removeToCreteHoleForPlugHousing028"
  Shapes = -> [Box024,Cylinder038]
FEATURE [Part::Cylinder] Cylinder039
  Angle = 360
  AttacherType = Attacher::AttachEngine3D
  Height = 20
  Placement = pos=(0,0,36.15) rot=(0,0,1;0rad)
  Radius = 14.3
FEATURE [Part::Cylinder] Cylinder040
  Angle = 360
  AttacherType = Attacher::AttachEngine3D
  Height = 10
  Placement = pos=(0,0,36.15) rot=(0,0,1;0rad)
  Radius = 4
FEATURE [Part::Box] Box025  label="removeToCreteHoleForPlugHousing030"
  AttacherType = Attacher::AttachEngine3D
  Height = 28.6
  Length = 20
  Placement = pos=(106.15,0,21.7) rot=(0,0,1;0rad)
  Width = 19
FEATURE [Part::MultiFuse] Fusion086  label="removeToCreteHoleForPlugHousing031"
  Placement = pos=(70,19,36) rot=(0,1,0;1.5708rad)
  Shapes = -> [Cylinder039,Cylinder040]
FEATURE [Part::MultiFuse] Fusion085  label="removeToCreteHoleForPlugHousing029"
  Shapes = -> [Box025,Fusion086]
FEATURE [Sketcher::SketchObject] Sketch055
  FullyConstrained = true
  Placement = pos=(117,19,0) rot=(0.57735,0.57735,0.57735;2.0944rad)
  sketch-geometry (48):
    g0: LineSegment StartX=-49.19 StartY=69.25 StartZ=0 EndX=-49.19 EndY=66.25 EndZ=0
    g1: LineSegment StartX=-49.19 StartY=63.5 StartZ=0 EndX=-49.19 EndY=60.5 EndZ=0
    g2: LineSegment StartX=-49.19 StartY=57.75 StartZ=0 EndX=-49.19 EndY=54.75 EndZ=0
    g3: LineSegment StartX=-49.19 StartY=52 StartZ=0 EndX=-49.19 EndY=49 EndZ=0
    g4: LineSegment StartX=-49.19 StartY=46.25 StartZ=0 EndX=-49.19 EndY=43.25 EndZ=0
    g5: LineSegment StartX=-49.19 StartY=40.5 StartZ=0 EndX=-49.19 EndY=37.5 EndZ=0
    g6: LineSegment StartX=-49.19 StartY=34.5 StartZ=0 EndX=-49.19 EndY=31.5 EndZ=0
    g7: LineSegment StartX=-49.19 StartY=28.75 StartZ=0 EndX=-49.19 EndY=25.75 EndZ=0
    g8: LineSegment StartX=-49.19 StartY=23 StartZ=0 EndX=-49.19 EndY=20 EndZ=0
    g9: LineSegment StartX=-49.19 StartY=17.25 StartZ=0 EndX=-49.19 EndY=14.25 EndZ=0
    g10: LineSegment StartX=-49.19 StartY=11.5 StartZ=0 EndX=-49.19 EndY=8.5 EndZ=0
    g11: LineSegment StartX=-49.19 StartY=5.75 StartZ=0 EndX=-49.19 EndY=2.75 EndZ=0
    g12: ArcOfCircle CenterX=-1.5 CenterY=67.75 CenterZ=0 NormalX=0 NormalY=0 NormalZ=1 AngleXU=0 Radius=1.5 StartAngle=4.71239 EndAngle=7.85398
    g13: ArcOfCircle CenterX=-1.5 CenterY=62 CenterZ=0 NormalX=0 NormalY=0 NormalZ=1 AngleXU=0 Radius=1.5 StartAngle=4.71239 EndAngle=7.85398
    g14: ArcOfCircle CenterX=-1.5 CenterY=56.25 CenterZ=0 NormalX=0 NormalY=0 NormalZ=1 AngleXU=0 Radius=1.5 StartAngle=4.71239 EndAngle=7.85398
    g15: ArcOfCircle CenterX=-11.49 CenterY=50.5 CenterZ=0 NormalX=0 NormalY=0 NormalZ=1 AngleXU=0 Radius=1.5 StartAngle=4.71239 EndAngle=7.85398
    g16: ArcOfCircle CenterX=-16.28 CenterY=44.75 CenterZ=0 NormalX=0 NormalY=0 NormalZ=1 AngleXU=0 Radius=1.5 StartAngle=4.71239 EndAngle=7.85398
    g17: ArcOfCircle CenterX=-18.2337 CenterY=39 CenterZ=0 NormalX=0 NormalY=0 NormalZ=1 AngleXU=0 Radius=1.5 StartAngle=4.71485 EndAngle=7.85398
    g18: ArcOfCircle CenterX=-16.2837 CenterY=27.25 CenterZ=0 NormalX=0 NormalY=0 NormalZ=1 AngleXU=0 Radius=1.5 StartAngle=4.71485 EndAngle=7.85398
    g19: ArcOfCircle CenterX=-18.2337 CenterY=33 CenterZ=0 NormalX=0 NormalY=0 NormalZ=1 AngleXU=0 Radius=1.5 StartAngle=4.71485 EndAngle=7.85398
    g20: ArcOfCircle CenterX=-11.49 CenterY=21.5 CenterZ=0 NormalX=0 NormalY=0 NormalZ=1 AngleXU=0 Radius=1.5 StartAngle=4.71239 EndAngle=7.85398
    g21: ArcOfCircle CenterX=-1.5 CenterY=4.25 CenterZ=0 NormalX=0 NormalY=0 NormalZ=1 AngleXU=0 Radius=1.5 StartAngle=4.71239 EndAngle=7.85398
    g22: ArcOfCircle CenterX=-1.5 CenterY=10 CenterZ=0 NormalX=0 NormalY=0 NormalZ=1 AngleXU=0 Radius=1.5 StartAngle=4.71239 EndAngle=7.85398
    g23: ArcOfCircle CenterX=-1.5 CenterY=15.75 CenterZ=0 NormalX=0 NormalY=0 NormalZ=1 AngleXU=0 Radius=1.5 StartAngle=4.71239 EndAngle=7.85398
    g24: LineSegment StartX=-49.19 StartY=69.25 StartZ=0 EndX=-1.5 EndY=69.25 EndZ=0
    g25: LineSegment StartX=-49.19 StartY=66.25 StartZ=0 EndX=-1.5 EndY=66.25 EndZ=0
    g26: LineSegment StartX=-49.19 StartY=63.5 StartZ=0 EndX=-1.5 EndY=63.5 EndZ=0
    g27: LineSegment StartX=-49.19 StartY=60.5 StartZ=0 EndX=-1.5 EndY=60.5 EndZ=0
    g28: LineSegment StartX=-49.19 StartY=57.75 StartZ=0 EndX=-1.5 EndY=57.75 EndZ=0
    g29: LineSegment StartX=-49.19 StartY=54.75 StartZ=0 EndX=-1.5 EndY=54.75 EndZ=0
    g30: LineSegment StartX=-49.19 StartY=52 StartZ=0 EndX=-11.49 EndY=52 EndZ=0
    g31: LineSegment StartX=-49.19 StartY=49 StartZ=0 EndX=-11.49 EndY=49 EndZ=0
    g32: LineSegment StartX=-49.19 StartY=46.25 StartZ=0 EndX=-16.28 EndY=46.25 EndZ=0
    g33: LineSegment StartX=-49.19 StartY=43.25 StartZ=0 EndX=-16.28 EndY=43.25 EndZ=0
    g34: LineSegment StartX=-49.19 StartY=40.5 StartZ=0 EndX=-18.2337 EndY=40.5 EndZ=0
    g35: LineSegment StartX=-49.19 StartY=37.5 StartZ=0 EndX=-18.23 EndY=37.5 EndZ=0
    g36: LineSegment StartX=-49.19 StartY=34.5 StartZ=0 EndX=-18.2337 EndY=34.5 EndZ=0
    g37: LineSegment StartX=-49.19 StartY=31.5 StartZ=0 EndX=-18.23 EndY=31.5 EndZ=0
    g38: LineSegment StartX=-49.19 StartY=28.75 StartZ=0 EndX=-16.2837 EndY=28.75 EndZ=0
    g39: LineSegment StartX=-49.19 StartY=25.75 StartZ=0 EndX=-16.28 EndY=25.75 EndZ=0
    g40: LineSegment StartX=-49.19 StartY=23 StartZ=0 EndX=-11.49 EndY=23 EndZ=0
    g41: LineSegment StartX=-49.19 StartY=20 StartZ=0 EndX=-11.49 EndY=20 EndZ=0
    g42: LineSegment StartX=-49.19 StartY=17.25 StartZ=0 EndX=-1.5 EndY=17.25 EndZ=0
    g43: LineSegment StartX=-49.19 StartY=14.25 StartZ=0 EndX=-1.5 EndY=14.25 EndZ=0
    g44: LineSegment StartX=-49.19 StartY=11.5 StartZ=0 EndX=-1.5 EndY=11.5 EndZ=0
    g45: LineSegment StartX=-49.19 StartY=8.5 StartZ=0 EndX=-1.5 EndY=8.5 EndZ=0
    g46: LineSegment StartX=-49.19 StartY=5.75 StartZ=0 EndX=-1.5 EndY=5.75 EndZ=0
    g47: LineSegment StartX=-49.19 StartY=2.75 StartZ=0 EndX=-1.5 EndY=2.75 EndZ=0
  constraints (120):
    c: Vertical(g0)
    c: Distance(g0) = 3
    c: Block(g0)
    c: Vertical(g1)
    c: Distance(g1) = 3
    c: Vertical(g2)
    c: Equal(g0,g2) = 3
    c: Block(g2)
    c: Vertical(g3)
    c: Equal(g1,g3) = 3
    c: Vertical(g4)
    c: Equal(g0,g4) = 3
    c: Block(g4)
    c: Vertical(g5)
    c: Equal(g1,g5) = 3
    c: Vertical(g6)
    c: Equal(g0,g6) = 3
    c: Block(g6)
    c: Vertical(g7)
    c: Equal(g1,g7) = 3
    c: Vertical(g8)
    c: Equal(g0,g8) = 3
    c: Block(g8)
    c: Vertical(g9)
    c: Equal(g1,g9) = 3
    c: Vertical(g10)
    c: Equal(g0,g10) = 3
    c: Block(g10)
    c: Vertical(g11)
    c: Equal(g1,g11) = 3
    c: Block(g12)
    c: Block(g13)
    c: Block(g14)
    c: Block(g15)
    c: Block(g16)
    c: Block(g17)
    c: Block(g18)
    c: Block(g19)
    c: Block(g20)
    c: Block(g21)
    c: Block(g22)
    c: Block(g23)
    c: Block(g11)
    c: Block(g9)
    c: Block(g7)
    c: Block(g5)
    c: Block(g3)
    c: Block(g1)
    c: Coincident(g24,g0)
    c: Coincident(g24,g12)
    c: Horizontal(g24)
    c: Coincident(g25,g0)
    c: Coincident(g25,g12)
    c: Horizontal(g25)
    c: Coincident(g26,g1)
    c: Coincident(g26,g13)
    c: Horizontal(g26)
    c: Coincident(g27,g1)
    c: Coincident(g27,g13)
    c: Horizontal(g27)
    c: Coincident(g28,g2)
    c: Coincident(g28,g14)
    c: Horizontal(g28)
    c: Coincident(g29,g2)
    c: Coincident(g29,g14)
    c: Horizontal(g29)
    c: Coincident(g30,g3)
    c: Coincident(g30,g15)
    c: Horizontal(g30)
    c: Coincident(g31,g3)
    c: Coincident(g31,g15)
    c: Horizontal(g31)
    c: Coincident(g32,g4)
    c: Coincident(g32,g16)
    c: Horizontal(g32)
    c: Coincident(g33,g4)
    c: Coincident(g33,g16)
    c: Horizontal(g33)
    c: Coincident(g34,g5)
    c: Coincident(g34,g17)
    c: Horizontal(g34)
    c: Coincident(g35,g5)
    c: Coincident(g35,g17)
    c: Horizontal(g35)
    c: Coincident(g36,g6)
    c: Coincident(g36,g19)
    c: Horizontal(g36)
    c: Coincident(g37,g6)
    c: Coincident(g37,g19)
    c: Horizontal(g37)
    c: Coincident(g38,g7)
    c: Coincident(g38,g18)
    c: Horizontal(g38)
    c: Coincident(g39,g7)
    c: Coincident(g39,g18)
    c: Horizontal(g39)
    c: Coincident(g40,g8)
    c: Coincident(g40,g20)
    c: Horizontal(g40)
    c: Coincident(g41,g8)
    c: Coincident(g41,g20)
    c: Horizontal(g41)
    c: Coincident(g42,g9)
    c: Coincident(g42,g23)
    c: Horizontal(g42)
    c: Coincident(g43,g9)
    c: Coincident(g43,g23)
    c: Horizontal(g43)
    c: Coincident(g44,g10)
    c: Coincident(g44,g22)
    c: Horizontal(g44)
    c: Coincident(g45,g10)
    c: Coincident(g45,g22)
    c: Horizontal(g45)
    c: Coincident(g46,g11)
    c: Coincident(g46,g21)
    c: Horizontal(g46)
    c: Coincident(g47,g11)
    c: Coincident(g47,g21)
    c: Horizontal(g47)
FEATURE [Part::Extrusion] Extrude046
  Base = -> Sketch055
  Dir = (1,0,0)
  DirMode = 2
  FaceMakerClass = Part::FaceMakerBullseye
  LengthFwd = 23
  LengthRev = 0
  Placement = pos=(-19,0,0) rot=(0,0,1;0rad)
  Solid = true
  Symmetric = false
FEATURE [Part::Fillet] Fillet038  label="removeToCreateVentalationHoles001"
  Base = -> Extrude046
  Edges = <same value as first occurrence — deduplicated (x6 in doc)>
  Placement = pos=(7,0,0) rot=(0,0,1;0rad)
FEATURE [Sketcher::SketchObject] Sketch056  label="topSketch014"
  FullyConstrained = true
  sketch-geometry (22):
    g0: LineSegment StartX=5.21097e-06 StartY=3 StartZ=0 EndX=5.21097e-06 EndY=19 EndZ=0
    g1: ArcOfCircle CenterX=19 CenterY=19 CenterZ=0 NormalX=0 NormalY=0 NormalZ=1 AngleXU=0 Radius=19 StartAngle=1.5708 EndAngle=3.14159
    g2: ArcOfCircle CenterX=19 CenterY=19 CenterZ=0 NormalX=0 NormalY=0 NormalZ=1 AngleXU=0 Radius=16 StartAngle=1.5708 EndAngle=3.14159
    g3: LineSegment StartX=114 StartY=35 StartZ=0 EndX=19 EndY=35 EndZ=0
    g4: LineSegment StartX=5.21097e-06 StartY=3 StartZ=0 EndX=5.21097e-06 EndY=0 EndZ=0
    g5: LineSegment StartX=3 StartY=0 StartZ=0 EndX=5.21097e-06 EndY=0 EndZ=0
    g6: LineSegment StartX=3 StartY=19 StartZ=0 EndX=3 EndY=0 EndZ=0
    g7: LineSegment StartX=19 StartY=38 StartZ=0 EndX=124 EndY=38 EndZ=0
    g8: Circle CenterX=119 CenterY=35 CenterZ=0 NormalX=0 NormalY=0 NormalZ=1 AngleXU=0 Radius=1
    g9: Circle CenterX=121 CenterY=35 CenterZ=0 NormalX=0 NormalY=0 NormalZ=1 AngleXU=0 Radius=1
    g10: Circle CenterX=121 CenterY=33 CenterZ=0 NormalX=0 NormalY=0 NormalZ=1 AngleXU=0 Radius=1
    g11: BSplineCurve PolesCount=3 KnotsCount=2 Degree=2 IsPeriodic=0
    g12: GeomPoint X=119 Y=35 Z=0
    g13: GeomPoint X=121 Y=33 Z=0
    g14: LineSegment StartX=119 StartY=35 StartZ=0 EndX=114 EndY=35 EndZ=0
    g15: ArcOfCircle CenterX=105 CenterY=19 CenterZ=0 NormalX=0 NormalY=0 NormalZ=1 AngleXU=0 Radius=16 StartAngle=5.60905 EndAngle=6.28319
    g16: LineSegment StartX=121 StartY=33 StartZ=0 EndX=121 EndY=19 EndZ=0
    g17: LineSegment StartX=117.5 StartY=9.01251 StartZ=0 EndX=121.163 EndY=9.0125 EndZ=0
    g18: ArcOfCircle CenterX=105 CenterY=19 CenterZ=0 NormalX=0 NormalY=0 NormalZ=1 AngleXU=0 Radius=20.6155 StartAngle=5.7297 EndAngle=6.28319
    g19: LineSegment StartX=121.163 StartY=9.0125 StartZ=0 EndX=122.538 EndY=8.16329 EndZ=0
    g20: LineSegment StartX=124 StartY=38 StartZ=0 EndX=125.616 EndY=38 EndZ=0
    g21: LineSegment StartX=125.616 StartY=19 StartZ=0 EndX=125.616 EndY=38 EndZ=0
  constraints (49):
    c: Vertical(g0)
    c: Block(g0)
    c: Coincident(g1,g0)
    c: Block(g1)
    c: Coincident(g2,g1)
    c: Block(g2)
    c: Coincident(g3,g2)
    c: Horizontal(g3)
    c: Tangent(g3,g2)
    c: Coincident(g4,g0)
    c: Distance(g4) = 3
    c: Vertical(g4)
    c: Coincident(g5,g4)
    c: Horizontal(g5)
    c: Coincident(g6,g2)
    c: Coincident(g6,g5)
    c: Vertical(g6)
    c: Horizontal(g7)
    c: Distance(g7) = 105
    c: Coincident(g7,g1)
    c: Block(g3)
    c: Weight(g8) = 1
    c: Equal(g8,g9)
    c: Equal(g8,g10)
    c: InternalAlignment(g8,g11)
    c: InternalAlignment(g9,g11)
    c: InternalAlignment(g10,g11)
    c: InternalAlignment(g12,g11)
    c: InternalAlignment(g13,g11)
    c: Block(g11)
    c: Coincident(g14,g11)
    c: Coincident(g14,g3)
    c: Horizontal(g14)
    c: Block(g15)
    c: Coincident(g16,g11)
    c: Coincident(g16,g15)
    c: Vertical(g16)
    c: Distance(g16) = 14
    c: Coincident(g17,g15)
    c: Block(g18)
    c: Coincident(g19,g18)
    c: Coincident(g20,g7)
    c: Horizontal(g20)
    c: Vertical(g21)
    c: Coincident(g20,g21)
    c: Block(g20)
    c: Block(g21)
    c: Block(g19)
    c: Block(g17)
FEATURE [Part::Box] Box026  label="removeToCreteHoleForPlugHousing032"
  AttacherType = Attacher::AttachEngine3D
  Height = 28.6
  Length = 10
  Placement = pos=(-2,0,21.7) rot=(0,0,1;0rad)
  Width = 19
FEATURE [Part::Feature] Face109 .. Face112  x4 (patterned run collapsed; names and placements below)
  shape: bbox 3.5 x 17.8 x 2e-07 mm, 1 faces, 0 solids (baked)
FEATURE [Part::Revolution] Revolve117  label="removeToCreateScrewAndThreadedInsertHole045"
  Angle = 360
  Axis = (0,1,0)
  Base = (0,0,0)
  FaceMakerClass = Part::FaceMakerBullseye
  Placement = pos=(62.3,30.3,19.7) rot=(0,0,1;0rad)
  Solid = false
  Source = -> Face109
  Symmetric = false
FEATURE [Part::Revolution] Revolve118  label="removeToCreateScrewAndThreadedInsertHole046"
  Angle = 360
  Axis = (0,1,0)
  Base = (0,0,0)
  FaceMakerClass = Part::FaceMakerBullseye
  Placement = pos=(62.3,30.3,51.7) rot=(0,0,1;0rad)
  Solid = false
  Source = -> Face110
  Symmetric = false
FEATURE [Part::Revolution] Revolve119  label="removeToCreateScrewAndThreadedInsertHole047"
  Angle = 360
  Axis = (0,1,0)
  Base = (0,0,0)
  FaceMakerClass = Part::FaceMakerBullseye
  Placement = pos=(30.3,30.3,19.7) rot=(0,0,1;0rad)
  Solid = false
  Source = -> Face111
  Symmetric = false
FEATURE [Part::Revolution] Revolve120  label="removeToCreateScrewAndThreadedInsertHole048"
  Angle = 360
  Axis = (0,1,0)
  Base = (0,0,0)
  FaceMakerClass = Part::FaceMakerBullseye
  Placement = pos=(30.3,30.3,51.7) rot=(0,0,1;0rad)
  Solid = false
  Source = -> Face112
  Symmetric = false
FEATURE [Part::MultiFuse] Fusion087  label="createThreadedInsertHolesForFan005"
  Shapes = -> [Revolve117,Revolve118,Revolve119,Revolve120]
FEATURE [Part::Extrusion] Extrude047
  Base = -> Sketch056
  Dir = (0,0,1)
  DirMode = 2
  FaceMakerClass = Part::FaceMakerBullseye
  LengthFwd = 72
  LengthRev = 0
  Solid = true
  Symmetric = false
FEATURE [Part::Fillet] Fillet039  label="top019"
  Base = -> Extrude047
  Edges = 1 edges r=2: [Edge35]
FEATURE [Sketcher::SketchObject] Sketch057
  FullyConstrained = false
  Placement = pos=(0,0,0) rot=(1,0,0;1.5708rad)
  sketch-geometry (24):
    g0: ArcOfCircle CenterX=-4 CenterY=-10.5 CenterZ=0 NormalX=0 NormalY=0 NormalZ=1 AngleXU=0 Radius=1.5 StartAngle=6e-16 EndAngle=3.14159
    g1: ArcOfCircle CenterX=-34.2 CenterY=-10.5 CenterZ=0 NormalX=0 NormalY=0 NormalZ=1 AngleXU=0 Radius=1.5 StartAngle=0 EndAngle=3.14159
    g2: ArcOfCircle CenterX=-34.2 CenterY=-27.7 CenterZ=0 NormalX=0 NormalY=0 NormalZ=1 AngleXU=0 Radius=1.5 StartAngle=3.14159 EndAngle=6.28319
    g3: ArcOfCircle CenterX=-4 CenterY=-27.7 CenterZ=0 NormalX=0 NormalY=0 NormalZ=1 AngleXU=0 Radius=1.5 StartAngle=3.1416 EndAngle=6.28319
    g4: ArcOfCircle CenterX=-10 CenterY=-4.3 CenterZ=0 NormalX=0 NormalY=0 NormalZ=1 AngleXU=0 Radius=1.5 StartAngle=2e-16 EndAngle=3.14159
    g5: ArcOfCircle CenterX=-16.1 CenterY=-1.8 CenterZ=0 NormalX=0 NormalY=0 NormalZ=1 AngleXU=0 Radius=1.5 StartAngle=5e-16 EndAngle=3.14159
    g6: ArcOfCircle CenterX=-22.1 CenterY=-1.8 CenterZ=0 NormalX=0 NormalY=0 NormalZ=1 AngleXU=0 Radius=1.5 StartAngle=5e-16 EndAngle=3.14159
    g7: ArcOfCircle CenterX=-28.2 CenterY=-4.3 CenterZ=0 NormalX=0 NormalY=0 NormalZ=1 AngleXU=0 Radius=1.5 StartAngle=2e-16 EndAngle=3.14159
    g8: ArcOfCircle CenterX=-10 CenterY=-33.9 CenterZ=0 NormalX=0 NormalY=0 NormalZ=1 AngleXU=0 Radius=1.5 StartAngle=3.14159 EndAngle=6.28319
    g9: ArcOfCircle CenterX=-16.1 CenterY=-36.4 CenterZ=0 NormalX=0 NormalY=0 NormalZ=1 AngleXU=0 Radius=1.5 StartAngle=3.14159 EndAngle=6.28319
    g10: ArcOfCircle CenterX=-22.1 CenterY=-36.4 CenterZ=0 NormalX=0 NormalY=0 NormalZ=1 AngleXU=0 Radius=1.5 StartAngle=3.14159 EndAngle=6.28319
    g11: ArcOfCircle CenterX=-28.2 CenterY=-33.9 CenterZ=0 NormalX=0 NormalY=0 NormalZ=1 AngleXU=0 Radius=1.5 StartAngle=3.14159 EndAngle=6.28319
    g12: LineSegment StartX=-35.7 StartY=-10.5 StartZ=0 EndX=-35.7 EndY=-27.7 EndZ=0
    g13: LineSegment StartX=-32.7 StartY=-10.5 StartZ=0 EndX=-32.7 EndY=-27.7 EndZ=0
    g14: LineSegment StartX=-29.7 StartY=-33.9 StartZ=0 EndX=-29.7 EndY=-4.3 EndZ=0
    g15: LineSegment StartX=-26.7 StartY=-33.9 StartZ=0 EndX=-26.7 EndY=-4.3 EndZ=0
    g16: LineSegment StartX=-2.5 StartY=-10.5 StartZ=0 EndX=-2.5 EndY=-27.7 EndZ=0
    g17: LineSegment StartX=-8.5 StartY=-4.3 StartZ=0 EndX=-8.5 EndY=-33.9 EndZ=0
    g18: LineSegment StartX=-5.5 StartY=-10.5 StartZ=0 EndX=-5.5 EndY=-27.7 EndZ=0
    g19: LineSegment StartX=-11.5 StartY=-4.3 StartZ=0 EndX=-11.5 EndY=-33.9 EndZ=0
    g20: LineSegment StartX=-14.6 StartY=-1.8 StartZ=0 EndX=-14.6 EndY=-36.4 EndZ=0
    g21: LineSegment StartX=-17.6 StartY=-1.8 StartZ=0 EndX=-17.6 EndY=-36.4 EndZ=0
    g22: LineSegment StartX=-20.6 StartY=-36.4 StartZ=0 EndX=-20.6 EndY=-1.8 EndZ=0
    g23: LineSegment StartX=-23.6 StartY=-1.8 StartZ=0 EndX=-23.6 EndY=-36.4 EndZ=0
  constraints (48):
    c: Block(g0)
    c: Block(g1)
    c: Block(g2)
    c: Block(g3)
    c: Block(g4)
    c: Block(g5)
    c: Block(g6)
    c: Block(g7)
    c: Block(g8)
    c: Block(g9)
    c: Block(g10)
    c: Block(g11)
    c: Coincident(g12,g1)
    c: Coincident(g12,g2)
    c: Vertical(g12)
    c: Coincident(g13,g1)
    c: Coincident(g13,g2)
    c: Vertical(g13)
    c: Coincident(g14,g11)
    c: Coincident(g14,g7)
    c: Vertical(g14)
    c: Coincident(g15,g11)
    c: Coincident(g15,g7)
    c: Vertical(g15)
    c: Coincident(g16,g0)
    c: Coincident(g16,g3)
    c: Vertical(g16)
    c: Coincident(g17,g4)
    c: Coincident(g17,g8)
    c: Vertical(g17)
    c: Coincident(g18,g0)
    c: Coincident(g18,g3)
    c: Vertical(g18)
    c: Coincident(g19,g4)
    c: Coincident(g19,g8)
    c: Vertical(g19)
    c: Coincident(g20,g5)
    c: Coincident(g20,g9)
    c: Vertical(g20)
    c: Coincident(g21,g5)
    c: Coincident(g21,g9)
    c: Vertical(g21)
    c: Coincident(g22,g10)
    c: Coincident(g22,g6)
    c: Vertical(g22)
    c: Coincident(g23,g6)
    c: Coincident(g23,g10)
    c: Vertical(g23)
FEATURE [Part::Extrusion] Extrude048  label="removeToCreateFanGrillHoles004"
  Base = -> Sketch057
  Dir = (0,-1,6e-16)
  DirMode = 2
  FaceMakerClass = Part::FaceMakerBullseye
  LengthFwd = 10
  LengthRev = 0
  Placement = pos=(65.4,44,54.82) rot=(0,0,1;0rad)
  Solid = true
  Symmetric = false
FEATURE [Part::Cut] Cut040  label="top021"
  Base = -> Fillet039
  Tool = -> Extrude048
FEATURE [Part::Cylinder] Cylinder041  label="removeToCreteHoleForPlugHousing034"
  Angle = 360
  AttacherType = Attacher::AttachEngine3D
  Height = 20
  Placement = pos=(-2,19,36) rot=(0,1,0;1.5708rad)
  Radius = 14.3
FEATURE [Part::MultiFuse] Fusion089  label="removeToCreteHoleForPlugHousing035"
  Shapes = -> [Box026,Cylinder041]
FEATURE [Part::Cylinder] Cylinder042
  Angle = 360
  AttacherType = Attacher::AttachEngine3D
  Height = 20
  Placement = pos=(0,0,36.15) rot=(0,0,1;0rad)
  Radius = 14.3
FEATURE [Part::Cylinder] Cylinder043
  Angle = 360
  AttacherType = Attacher::AttachEngine3D
  Height = 10
  Placement = pos=(0,0,36.15) rot=(0,0,1;0rad)
  Radius = 4
FEATURE [Part::Box] Box027  label="removeToCreteHoleForPlugHousing036"
  AttacherType = Attacher::AttachEngine3D
  Height = 28.6
  Length = 20
  Placement = pos=(106.15,0,21.7) rot=(0,0,1;0rad)
  Width = 19
FEATURE [Part::Cut] Cut041  label="top022"
  Base = -> Cut040
  Tool = -> Fusion087
FEATURE [Part::Cut] Cut039  label="top020"
  Base = -> Cut041
  Tool = -> Fusion089
FEATURE [Part::MultiFuse] Fusion090  label="removeToCreteHoleForPlugHousing037"
  Placement = pos=(70,19,36) rot=(0,1,0;1.5708rad)
  Shapes = -> [Cylinder042,Cylinder043]
FEATURE [Part::MultiFuse] Fusion088  label="removeToCreteHoleForPlugHousing033"
  Shapes = -> [Box027,Fusion090]
FEATURE [Part::Cut] Cut042  label="removeToCreteHoleForPlugHousing038"
  Base = -> Cut039
  Tool = -> Fusion088
FEATURE [Part::MultiFuse] Fusion091  label="removeFromTop"
  Shapes = -> [Fillet038,Fusion085,Fusion084,Fusion083,Extrude045]
FEATURE [Part::Cut] Cut043  label="REAL TOP ====="
  Base = -> Fillet036
  Tool = -> Fusion091
FEATURE [Part::MultiFuse] Fusion092  label="caseScrewPillarBracket016"
  Shapes = -> [Extrude030,Extrude031,Extrude032,Extrude033,Extrude034,Extrude035,Extrude036,Extrude037,Box013,Box014]
FEATURE [Sketcher::SketchObject] Sketch058  label="topSketch015"
  FullyConstrained = true
  sketch-geometry (20):
    g0: LineSegment StartX=5.21097e-06 StartY=3 StartZ=0 EndX=5.21097e-06 EndY=19 EndZ=0
    g1: ArcOfCircle CenterX=19 CenterY=19 CenterZ=0 NormalX=0 NormalY=0 NormalZ=1 AngleXU=0 Radius=19 StartAngle=1.5708 EndAngle=3.14159
    g2: ArcOfCircle CenterX=19 CenterY=19 CenterZ=0 NormalX=0 NormalY=0 NormalZ=1 AngleXU=0 Radius=16 StartAngle=1.5708 EndAngle=3.14159
    g3: LineSegment StartX=114 StartY=35 StartZ=0 EndX=19 EndY=35 EndZ=0
    g4: LineSegment StartX=5.21097e-06 StartY=3 StartZ=0 EndX=5.21097e-06 EndY=0 EndZ=0
    g5: LineSegment StartX=3 StartY=0 StartZ=0 EndX=5.21097e-06 EndY=0 EndZ=0
    g6: LineSegment StartX=3 StartY=19 StartZ=0 EndX=3 EndY=0 EndZ=0
    g7: LineSegment StartX=19 StartY=38 StartZ=0 EndX=124 EndY=38 EndZ=0
    g8: Circle CenterX=119 CenterY=35 CenterZ=0 NormalX=0 NormalY=0 NormalZ=1 AngleXU=0 Radius=1
    g9: Circle CenterX=121 CenterY=35 CenterZ=0 NormalX=0 NormalY=0 NormalZ=1 AngleXU=0 Radius=1
    g10: Circle CenterX=121 CenterY=33 CenterZ=0 NormalX=0 NormalY=0 NormalZ=1 AngleXU=0 Radius=1
    g11: BSplineCurve PolesCount=3 KnotsCount=2 Degree=2 IsPeriodic=0
    g12: GeomPoint X=119 Y=35 Z=0
    g13: GeomPoint X=121 Y=33 Z=0
    g14: LineSegment StartX=119 StartY=35 StartZ=0 EndX=114 EndY=35 EndZ=0
    g15: ArcOfCircle CenterX=105 CenterY=19 CenterZ=0 NormalX=0 NormalY=0 NormalZ=1 AngleXU=0 Radius=19 StartAngle=5.7297 EndAngle=6.28319
    g16: ArcOfCircle CenterX=105 CenterY=19 CenterZ=0 NormalX=0 NormalY=0 NormalZ=1 AngleXU=0 Radius=16 StartAngle=5.60905 EndAngle=6.28319
    g17: LineSegment StartX=121 StartY=33 StartZ=0 EndX=121 EndY=19 EndZ=0
    g18: LineSegment StartX=124 StartY=38 StartZ=0 EndX=124 EndY=19 EndZ=0
    g19: LineSegment StartX=117.5 StartY=9.01251 StartZ=0 EndX=121.163 EndY=9.0125 EndZ=0
  constraints (46):
    c: Vertical(g0)
    c: Block(g0)
    c: Coincident(g1,g0)
    c: Block(g1)
    c: Coincident(g2,g1)
    c: Block(g2)
    c: Coincident(g3,g2)
    c: Horizontal(g3)
    c: Tangent(g3,g2)
    c: Coincident(g4,g0)
    c: Distance(g4) = 3
    c: Vertical(g4)
    c: Coincident(g5,g4)
    c: Horizontal(g5)
    c: Coincident(g6,g2)
    c: Coincident(g6,g5)
    c: Vertical(g6)
    c: Horizontal(g7)
    c: Distance(g7) = 105
    c: Coincident(g7,g1)
    c: Block(g3)
    c: Weight(g8) = 1
    c: Equal(g8,g9)
    c: Equal(g8,g10)
    c: InternalAlignment(g8,g11)
    c: InternalAlignment(g9,g11)
    c: InternalAlignment(g10,g11)
    c: InternalAlignment(g12,g11)
    c: InternalAlignment(g13,g11)
    c: Block(g11)
    c: Coincident(g14,g11)
    c: Coincident(g14,g3)
    c: Horizontal(g14)
    c: Block(g15)
    c: Coincident(g16,g15)
    c: Block(g16)
    c: Coincident(g17,g11)
    c: Coincident(g17,g16)
    c: Vertical(g17)
    c: Distance(g17) = 14
    c: Coincident(g18,g7)
    c: Coincident(g18,g15)
    c: Vertical(g18)
    c: Distance(g18) = 19
    c: Coincident(g19,g16)
    c: Coincident(g19,g15)
FEATURE [Part::Extrusion] Extrude049  label="top023"
  Base = -> Sketch058
  Dir = (0,0,1)
  DirMode = 2
  FaceMakerClass = Part::FaceMakerBullseye
  LengthFwd = 72
  LengthRev = 0
  Solid = true
  Symmetric = false
FEATURE [Sketcher::SketchObject] Sketch059
  FullyConstrained = true
  MapMode = 3
  Placement = pos=(0,0,0) rot=(1,0,0;1.5708rad)
  Support = -> [Extrude049]
  sketch-geometry (8):
    g0: Circle CenterX=80.351 CenterY=-67.6202 CenterZ=0 NormalX=0 NormalY=0 NormalZ=1 AngleXU=0 Radius=2
    g1: Circle CenterX=80.351 CenterY=-67.6202 CenterZ=0 NormalX=0 NormalY=0 NormalZ=1 AngleXU=0 Radius=3
    g2: Circle CenterX=80.351 CenterY=-4.92017 CenterZ=0 NormalX=0 NormalY=0 NormalZ=1 AngleXU=0 Radius=2
    g3: Circle CenterX=80.351 CenterY=-4.92017 CenterZ=0 NormalX=0 NormalY=0 NormalZ=1 AngleXU=0 Radius=3
    g4: Circle CenterX=23.851 CenterY=-4.92017 CenterZ=0 NormalX=0 NormalY=0 NormalZ=1 AngleXU=0 Radius=2
    g5: Circle CenterX=23.851 CenterY=-4.92017 CenterZ=0 NormalX=0 NormalY=0 NormalZ=1 AngleXU=0 Radius=3
    g6: Circle CenterX=23.851 CenterY=-67.6202 CenterZ=0 NormalX=0 NormalY=0 NormalZ=1 AngleXU=0 Radius=2
    g7: Circle CenterX=23.851 CenterY=-67.6202 CenterZ=0 NormalX=0 NormalY=0 NormalZ=1 AngleXU=0 Radius=3
  constraints (8):
    c: Block(g3)
    c: Block(g2)
    c: Block(g1)
    c: Block(g0)
    c: Block(g6)
    c: Block(g7)
    c: Block(g4)
    c: Block(g5)
FEATURE [Sketcher::SketchObject] Sketch060
  FullyConstrained = true
  MapMode = 3
  Placement = pos=(0,0,0) rot=(1,0,0;1.5708rad)
  Support = -> [Extrude049]
  sketch-geometry (8):
    g0: Circle CenterX=80.351 CenterY=-67.6202 CenterZ=0 NormalX=0 NormalY=0 NormalZ=1 AngleXU=0 Radius=3
    g1: Circle CenterX=80.351 CenterY=-4.92017 CenterZ=0 NormalX=0 NormalY=0 NormalZ=1 AngleXU=0 Radius=3
    g2: Circle CenterX=23.851 CenterY=-4.92017 CenterZ=0 NormalX=0 NormalY=0 NormalZ=1 AngleXU=0 Radius=3
    g3: Circle CenterX=23.851 CenterY=-67.6202 CenterZ=0 NormalX=0 NormalY=0 NormalZ=1 AngleXU=0 Radius=3
    g4: Circle CenterX=23.851 CenterY=-67.6202 CenterZ=0 NormalX=0 NormalY=0 NormalZ=1 AngleXU=0 Radius=5
    g5: Circle CenterX=80.351 CenterY=-67.6202 CenterZ=0 NormalX=0 NormalY=0 NormalZ=1 AngleXU=0 Radius=5
    g6: Circle CenterX=23.851 CenterY=-4.92017 CenterZ=0 NormalX=0 NormalY=0 NormalZ=1 AngleXU=0 Radius=5
    g7: Circle CenterX=80.351 CenterY=-4.92017 CenterZ=0 NormalX=0 NormalY=0 NormalZ=1 AngleXU=0 Radius=5
  constraints (8):
    c: Block(g1)
    c: Block(g0)
    c: Block(g3)
    c: Block(g2)
    c: Block(g5)
    c: Block(g4)
    c: Block(g6)
    c: Block(g7)
FEATURE [Sketcher::SketchObject] Sketch061
  FullyConstrained = true
  MapMode = 3
  Placement = pos=(0,0,0) rot=(1,0,0;1.5708rad)
  sketch-geometry (8):
    g0: Circle CenterX=80.351 CenterY=-67.6202 CenterZ=0 NormalX=0 NormalY=0 NormalZ=1 AngleXU=0 Radius=3
    g1: Circle CenterX=80.351 CenterY=-4.92017 CenterZ=0 NormalX=0 NormalY=0 NormalZ=1 AngleXU=0 Radius=3
    g2: Circle CenterX=23.851 CenterY=-4.92017 CenterZ=0 NormalX=0 NormalY=0 NormalZ=1 AngleXU=0 Radius=3
    g3: Circle CenterX=23.851 CenterY=-67.6202 CenterZ=0 NormalX=0 NormalY=0 NormalZ=1 AngleXU=0 Radius=3
    g4: Circle CenterX=23.851 CenterY=-67.6202 CenterZ=0 NormalX=0 NormalY=0 NormalZ=1 AngleXU=0 Radius=5
    g5: Circle CenterX=80.351 CenterY=-67.6202 CenterZ=0 NormalX=0 NormalY=0 NormalZ=1 AngleXU=0 Radius=5
    g6: Circle CenterX=23.851 CenterY=-4.92017 CenterZ=0 NormalX=0 NormalY=0 NormalZ=1 AngleXU=0 Radius=5
    g7: Circle CenterX=80.351 CenterY=-4.92017 CenterZ=0 NormalX=0 NormalY=0 NormalZ=1 AngleXU=0 Radius=5
  constraints (8):
    c: Block(g1)
    c: Block(g0)
    c: Block(g3)
    c: Block(g2)
    c: Block(g5)
    c: Block(g4)
    c: Block(g6)
    c: Block(g7)
FEATURE [Sketcher::SketchObject] Sketch062  label="topSketch016"
  FullyConstrained = true
  sketch-geometry (20):
    g0: LineSegment StartX=5.21097e-06 StartY=3 StartZ=0 EndX=5.21097e-06 EndY=19 EndZ=0
    g1: ArcOfCircle CenterX=19 CenterY=19 CenterZ=0 NormalX=0 NormalY=0 NormalZ=1 AngleXU=0 Radius=19 StartAngle=1.5708 EndAngle=3.14159
    g2: ArcOfCircle CenterX=19 CenterY=19 CenterZ=0 NormalX=0 NormalY=0 NormalZ=1 AngleXU=0 Radius=16 StartAngle=1.5708 EndAngle=3.14159
    g3: LineSegment StartX=114 StartY=35 StartZ=0 EndX=19 EndY=35 EndZ=0
    g4: LineSegment StartX=5.21097e-06 StartY=3 StartZ=0 EndX=5.21097e-06 EndY=0 EndZ=0
    g5: LineSegment StartX=3 StartY=0 StartZ=0 EndX=5.21097e-06 EndY=0 EndZ=0
    g6: LineSegment StartX=3 StartY=19 StartZ=0 EndX=3 EndY=0 EndZ=0
    g7: LineSegment StartX=19 StartY=38 StartZ=0 EndX=124 EndY=38 EndZ=0
    g8: Circle CenterX=119 CenterY=35 CenterZ=0 NormalX=0 NormalY=0 NormalZ=1 AngleXU=0 Radius=1
    g9: Circle CenterX=121 CenterY=35 CenterZ=0 NormalX=0 NormalY=0 NormalZ=1 AngleXU=0 Radius=1
    g10: Circle CenterX=121 CenterY=33 CenterZ=0 NormalX=0 NormalY=0 NormalZ=1 AngleXU=0 Radius=1
    g11: BSplineCurve PolesCount=3 KnotsCount=2 Degree=2 IsPeriodic=0
    g12: GeomPoint X=119 Y=35 Z=0
    g13: GeomPoint X=121 Y=33 Z=0
    g14: LineSegment StartX=119 StartY=35 StartZ=0 EndX=114 EndY=35 EndZ=0
    g15: ArcOfCircle CenterX=105 CenterY=19 CenterZ=0 NormalX=0 NormalY=0 NormalZ=1 AngleXU=0 Radius=19 StartAngle=5.7297 EndAngle=6.28319
    g16: ArcOfCircle CenterX=105 CenterY=19 CenterZ=0 NormalX=0 NormalY=0 NormalZ=1 AngleXU=0 Radius=16 StartAngle=5.60905 EndAngle=6.28319
    g17: LineSegment StartX=121 StartY=33 StartZ=0 EndX=121 EndY=19 EndZ=0
    g18: LineSegment StartX=124 StartY=38 StartZ=0 EndX=124 EndY=19 EndZ=0
    g19: LineSegment StartX=117.5 StartY=9.01251 StartZ=0 EndX=121.163 EndY=9.0125 EndZ=0
  constraints (46):
    c: Vertical(g0)
    c: Block(g0)
    c: Coincident(g1,g0)
    c: Block(g1)
    c: Coincident(g2,g1)
    c: Block(g2)
    c: Coincident(g3,g2)
    c: Horizontal(g3)
    c: Tangent(g3,g2)
    c: Coincident(g4,g0)
    c: Distance(g4) = 3
    c: Vertical(g4)
    c: Coincident(g5,g4)
    c: Horizontal(g5)
    c: Coincident(g6,g2)
    c: Coincident(g6,g5)
    c: Vertical(g6)
    c: Horizontal(g7)
    c: Distance(g7) = 105
    c: Coincident(g7,g1)
    c: Block(g3)
    c: Weight(g8) = 1
    c: Equal(g8,g9)
    c: Equal(g8,g10)
    c: InternalAlignment(g8,g11)
    c: InternalAlignment(g9,g11)
    c: InternalAlignment(g10,g11)
    c: InternalAlignment(g12,g11)
    c: InternalAlignment(g13,g11)
    c: Block(g11)
    c: Coincident(g14,g11)
    c: Coincident(g14,g3)
    c: Horizontal(g14)
    c: Block(g15)
    c: Coincident(g16,g15)
    c: Block(g16)
    c: Coincident(g17,g11)
    c: Coincident(g17,g16)
    c: Vertical(g17)
    c: Distance(g17) = 14
    c: Coincident(g18,g7)
    c: Coincident(g18,g15)
    c: Vertical(g18)
    c: Distance(g18) = 19
    c: Coincident(g19,g16)
    c: Coincident(g19,g15)
FEATURE [Part::Extrusion] Extrude053  label="top024"
  Base = -> Sketch062
  Dir = (0,0,1)
  DirMode = 2
  FaceMakerClass = Part::FaceMakerBullseye
  LengthFwd = 72
  LengthRev = 0
  Solid = true
  Symmetric = false
FEATURE [Sketcher::SketchObject] Sketch063
  FullyConstrained = true
  MapMode = 3
  Placement = pos=(0,0,0) rot=(1,0,0;1.5708rad)
  Support = -> [Extrude053]
  sketch-geometry (8):
    g0: Circle CenterX=80.351 CenterY=-67.6202 CenterZ=0 NormalX=0 NormalY=0 NormalZ=1 AngleXU=0 Radius=2
    g1: Circle CenterX=80.351 CenterY=-67.6202 CenterZ=0 NormalX=0 NormalY=0 NormalZ=1 AngleXU=0 Radius=3
    g2: Circle CenterX=80.351 CenterY=-4.92017 CenterZ=0 NormalX=0 NormalY=0 NormalZ=1 AngleXU=0 Radius=2
    g3: Circle CenterX=80.351 CenterY=-4.92017 CenterZ=0 NormalX=0 NormalY=0 NormalZ=1 AngleXU=0 Radius=3
    g4: Circle CenterX=23.851 CenterY=-4.92017 CenterZ=0 NormalX=0 NormalY=0 NormalZ=1 AngleXU=0 Radius=2
    g5: Circle CenterX=23.851 CenterY=-4.92017 CenterZ=0 NormalX=0 NormalY=0 NormalZ=1 AngleXU=0 Radius=3
    g6: Circle CenterX=23.851 CenterY=-67.6202 CenterZ=0 NormalX=0 NormalY=0 NormalZ=1 AngleXU=0 Radius=2
    g7: Circle CenterX=23.851 CenterY=-67.6202 CenterZ=0 NormalX=0 NormalY=0 NormalZ=1 AngleXU=0 Radius=3
  constraints (8):
    c: Block(g3)
    c: Block(g2)
    c: Block(g1)
    c: Block(g0)
    c: Block(g6)
    c: Block(g7)
    c: Block(g4)
    c: Block(g5)
FEATURE [Part::Extrusion] Extrude054
  Base = -> Sketch063
  Dir = (0,-1,2e-16)
  DirMode = 2
  FaceMakerClass = Part::FaceMakerBullseye
  LengthFwd = 6
  LengthRev = 0
  Placement = pos=(0,9,0) rot=(0,0,1;0rad)
  Solid = true
  Symmetric = false
FEATURE [Sketcher::SketchObject] Sketch064  label="topSketch017"
  FullyConstrained = true
  sketch-geometry (20):
    g0: LineSegment StartX=5.21097e-06 StartY=3 StartZ=0 EndX=5.21097e-06 EndY=19 EndZ=0
    g1: ArcOfCircle CenterX=19 CenterY=19 CenterZ=0 NormalX=0 NormalY=0 NormalZ=1 AngleXU=0 Radius=19 StartAngle=1.5708 EndAngle=3.14159
    g2: ArcOfCircle CenterX=19 CenterY=19 CenterZ=0 NormalX=0 NormalY=0 NormalZ=1 AngleXU=0 Radius=16 StartAngle=1.5708 EndAngle=3.14159
    g3: LineSegment StartX=114 StartY=35 StartZ=0 EndX=19 EndY=35 EndZ=0
    g4: LineSegment StartX=5.21097e-06 StartY=3 StartZ=0 EndX=5.21097e-06 EndY=0 EndZ=0
    g5: LineSegment StartX=3 StartY=0 StartZ=0 EndX=5.21097e-06 EndY=0 EndZ=0
    g6: LineSegment StartX=3 StartY=19 StartZ=0 EndX=3 EndY=0 EndZ=0
    g7: LineSegment StartX=19 StartY=38 StartZ=0 EndX=124 EndY=38 EndZ=0
    g8: Circle CenterX=119 CenterY=35 CenterZ=0 NormalX=0 NormalY=0 NormalZ=1 AngleXU=0 Radius=1
    g9: Circle CenterX=121 CenterY=35 CenterZ=0 NormalX=0 NormalY=0 NormalZ=1 AngleXU=0 Radius=1
    g10: Circle CenterX=121 CenterY=33 CenterZ=0 NormalX=0 NormalY=0 NormalZ=1 AngleXU=0 Radius=1
    g11: BSplineCurve PolesCount=3 KnotsCount=2 Degree=2 IsPeriodic=0
    g12: GeomPoint X=119 Y=35 Z=0
    g13: GeomPoint X=121 Y=33 Z=0
    g14: LineSegment StartX=119 StartY=35 StartZ=0 EndX=114 EndY=35 EndZ=0
    g15: ArcOfCircle CenterX=105 CenterY=19 CenterZ=0 NormalX=0 NormalY=0 NormalZ=1 AngleXU=0 Radius=19 StartAngle=5.7297 EndAngle=6.28319
    g16: ArcOfCircle CenterX=105 CenterY=19 CenterZ=0 NormalX=0 NormalY=0 NormalZ=1 AngleXU=0 Radius=16 StartAngle=5.60905 EndAngle=6.28319
    g17: LineSegment StartX=121 StartY=33 StartZ=0 EndX=121 EndY=19 EndZ=0
    g18: LineSegment StartX=124 StartY=38 StartZ=0 EndX=124 EndY=19 EndZ=0
    g19: LineSegment StartX=117.5 StartY=9.01251 StartZ=0 EndX=121.163 EndY=9.0125 EndZ=0
  constraints (46):
    c: Vertical(g0)
    c: Block(g0)
    c: Coincident(g1,g0)
    c: Block(g1)
    c: Coincident(g2,g1)
    c: Block(g2)
    c: Coincident(g3,g2)
    c: Horizontal(g3)
    c: Tangent(g3,g2)
    c: Coincident(g4,g0)
    c: Distance(g4) = 3
    c: Vertical(g4)
    c: Coincident(g5,g4)
    c: Horizontal(g5)
    c: Coincident(g6,g2)
    c: Coincident(g6,g5)
    c: Vertical(g6)
    c: Horizontal(g7)
    c: Distance(g7) = 105
    c: Coincident(g7,g1)
    c: Block(g3)
    c: Weight(g8) = 1
    c: Equal(g8,g9)
    c: Equal(g8,g10)
    c: InternalAlignment(g8,g11)
    c: InternalAlignment(g9,g11)
    c: InternalAlignment(g10,g11)
    c: InternalAlignment(g12,g11)
    c: InternalAlignment(g13,g11)
    c: Block(g11)
    c: Coincident(g14,g11)
    c: Coincident(g14,g3)
    c: Horizontal(g14)
    c: Block(g15)
    c: Coincident(g16,g15)
    c: Block(g16)
    c: Coincident(g17,g11)
    c: Coincident(g17,g16)
    c: Vertical(g17)
    c: Distance(g17) = 14
    c: Coincident(g18,g7)
    c: Coincident(g18,g15)
    c: Vertical(g18)
    c: Distance(g18) = 19
    c: Coincident(g19,g16)
    c: Coincident(g19,g15)
FEATURE [Sketcher::SketchObject] Sketch065
  FullyConstrained = true
  MapMode = 3
  Placement = pos=(0,0,0) rot=(1,0,0;1.5708rad)
  sketch-geometry (8):
    g0: Circle CenterX=80.351 CenterY=-67.6202 CenterZ=0 NormalX=0 NormalY=0 NormalZ=1 AngleXU=0 Radius=3
    g1: Circle CenterX=80.351 CenterY=-4.92017 CenterZ=0 NormalX=0 NormalY=0 NormalZ=1 AngleXU=0 Radius=3
    g2: Circle CenterX=23.851 CenterY=-4.92017 CenterZ=0 NormalX=0 NormalY=0 NormalZ=1 AngleXU=0 Radius=3
    g3: Circle CenterX=23.851 CenterY=-67.6202 CenterZ=0 NormalX=0 NormalY=0 NormalZ=1 AngleXU=0 Radius=3
    g4: Circle CenterX=23.851 CenterY=-67.6202 CenterZ=0 NormalX=0 NormalY=0 NormalZ=1 AngleXU=0 Radius=5
    g5: Circle CenterX=80.351 CenterY=-67.6202 CenterZ=0 NormalX=0 NormalY=0 NormalZ=1 AngleXU=0 Radius=5
    g6: Circle CenterX=23.851 CenterY=-4.92017 CenterZ=0 NormalX=0 NormalY=0 NormalZ=1 AngleXU=0 Radius=5
    g7: Circle CenterX=80.351 CenterY=-4.92017 CenterZ=0 NormalX=0 NormalY=0 NormalZ=1 AngleXU=0 Radius=5
  constraints (8):
    c: Block(g1)
    c: Block(g0)
    c: Block(g3)
    c: Block(g2)
    c: Block(g5)
    c: Block(g4)
    c: Block(g6)
    c: Block(g7)
FEATURE [Part::Extrusion] Extrude056
  Base = -> Sketch065
  Dir = (0,-1,2e-16)
  DirMode = 2
  FaceMakerClass = Part::FaceMakerBullseye
  LengthFwd = 2
  LengthRev = 0
  Solid = true
  Symmetric = false
FEATURE [Part::Extrusion] Extrude057  label="top025"
  Base = -> Sketch064
  Dir = (0,0,1)
  DirMode = 2
  FaceMakerClass = Part::FaceMakerBullseye
  LengthFwd = 72
  LengthRev = 0
  Solid = true
  Symmetric = false
FEATURE [Sketcher::SketchObject] Sketch066
  FullyConstrained = true
  MapMode = 3
  Placement = pos=(0,0,0) rot=(1,0,0;1.5708rad)
  Support = -> [Extrude057]
  sketch-geometry (8):
    g0: Circle CenterX=80.351 CenterY=-67.6202 CenterZ=0 NormalX=0 NormalY=0 NormalZ=1 AngleXU=0 Radius=3
    g1: Circle CenterX=80.351 CenterY=-4.92017 CenterZ=0 NormalX=0 NormalY=0 NormalZ=1 AngleXU=0 Radius=3
    g2: Circle CenterX=23.851 CenterY=-4.92017 CenterZ=0 NormalX=0 NormalY=0 NormalZ=1 AngleXU=0 Radius=3
    g3: Circle CenterX=23.851 CenterY=-67.6202 CenterZ=0 NormalX=0 NormalY=0 NormalZ=1 AngleXU=0 Radius=3
    g4: Circle CenterX=23.851 CenterY=-67.6202 CenterZ=0 NormalX=0 NormalY=0 NormalZ=1 AngleXU=0 Radius=5
    g5: Circle CenterX=80.351 CenterY=-67.6202 CenterZ=0 NormalX=0 NormalY=0 NormalZ=1 AngleXU=0 Radius=5
    g6: Circle CenterX=23.851 CenterY=-4.92017 CenterZ=0 NormalX=0 NormalY=0 NormalZ=1 AngleXU=0 Radius=5
    g7: Circle CenterX=80.351 CenterY=-4.92017 CenterZ=0 NormalX=0 NormalY=0 NormalZ=1 AngleXU=0 Radius=5
  constraints (8):
    c: Block(g1)
    c: Block(g0)
    c: Block(g3)
    c: Block(g2)
    c: Block(g5)
    c: Block(g4)
    c: Block(g6)
    c: Block(g7)
FEATURE [Part::Extrusion] Extrude055
  Base = -> Sketch066
  Dir = (0,-1,2e-16)
  DirMode = 2
  FaceMakerClass = Part::FaceMakerBullseye
  LengthFwd = 2
  LengthRev = 0
  Solid = true
  Symmetric = false
FEATURE [Part::Fillet] Fillet041
  Base = -> Extrude056
  Edges = 4 edges r=1.99: [Edge6,Edge12,Edge18,Edge24]
FEATURE [Part::Cut] Cut045
  Base = -> Extrude055
  Placement = pos=(0,6,0) rot=(0,0,1;0rad)
  Tool = -> Fillet041
FEATURE [Part::MultiFuse] Fusion095  label="pcbScrewPillars"
  Placement = pos=(-3.2,-1,72.3) rot=(0,0,1;0rad)
  Shapes = -> [Cut045,Extrude054]
FEATURE [Part::Feature] Face113
  shape: bbox 3.2 x 1.5 x 2e-07 mm, 1 faces, 0 solids (baked)
FEATURE [Part::Revolution] Revolve121  label="backCaseScrewRetainer002"
  Angle = 360
  Axis = (0,1,0)
  Base = (0,0,0)
  FaceMakerClass = Part::FaceMakerBullseye
  Placement = pos=(12.5,3,62) rot=(0,0,1;0rad)
  Solid = false
  Source = -> Face113
  Symmetric = false
FEATURE [Part::Feature] Face114
  shape: bbox 3.2 x 1.5 x 2e-07 mm, 1 faces, 0 solids (baked)
FEATURE [Part::Feature] Face115
  shape: bbox 3.2 x 1.5 x 2e-07 mm, 1 faces, 0 solids (baked)
FEATURE [Part::Feature] Face116
  shape: bbox 3.2 x 1.5 x 2e-07 mm, 1 faces, 0 solids (baked)
FEATURE [Part::Revolution] Revolve122  label="frontCaseScrewRetainer004"
  Angle = 360
  Axis = (0,1,0)
  Base = (0,0,0)
  FaceMakerClass = Part::FaceMakerBullseye
  Placement = pos=(89.5,3,68.5) rot=(0,0,1;0rad)
  Solid = false
  Source = -> Face115
  Symmetric = false
FEATURE [Part::Revolution] Revolve123  label="frontCaseScrewRetainer005"
  Angle = 360
  Axis = (0,1,0)
  Base = (0,0,0)
  FaceMakerClass = Part::FaceMakerBullseye
  Placement = pos=(89.5,3,3.5) rot=(0,0,1;0rad)
  Solid = false
  Source = -> Face116
  Symmetric = false
FEATURE [Part::Revolution] Revolve124  label="backCaseScrewRetainer003"
  Angle = 360
  Axis = (0,1,0)
  Base = (0,0,0)
  FaceMakerClass = Part::FaceMakerBullseye
  Placement = pos=(12.5,3,10) rot=(0,0,1;0rad)
  Solid = false
  Source = -> Face114
  Symmetric = false
FEATURE [Part::Feature] Face117
  shape: bbox 3.6 x 3.2 x 2e-07 mm, 1 faces, 0 solids (baked)
FEATURE [Part::Revolution] Revolve125  label="moreFrontCaseScrewRetainer004"
  Angle = 360
  Axis = (0,1,0)
  Base = (0,0,0)
  FaceMakerClass = Part::FaceMakerBullseye
  Placement = pos=(109.5,4.5,68.5) rot=(0,0,1;0rad)
  Solid = false
  Source = -> Face117
  Symmetric = false
FEATURE [Part::Feature] Face118
  shape: bbox 3.6 x 3.2 x 2e-07 mm, 1 faces, 0 solids (baked)
FEATURE [Part::Revolution] Revolve126  label="moreFrontCaseScrewRetainer005"
  Angle = 360
  Axis = (0,1,0)
  Base = (0,0,0)
  FaceMakerClass = Part::FaceMakerBullseye
  Placement = pos=(109.5,4.5,3.5) rot=(0,0,1;0rad)
  Solid = false
  Source = -> Face118
  Symmetric = false
FEATURE [Part::MultiFuse] Fusion096  label="screwRetainers001"
  Shapes = -> [Revolve126,Revolve125,Revolve124,Revolve123,Revolve122,Revolve121]
FEATURE [Part::Feature] Face119
  shape: bbox 10 x 16.5 x 2e-07 mm, 1 faces, 0 solids (baked)
FEATURE [Part::Revolution] Revolve130  label="plugHousing050"
  Angle = 360
  Axis = (0,1,0)
  Base = (0,0,0)
  FaceMakerClass = Part::FaceMakerBullseye
  Placement = pos=(0,0,36.15) rot=(0,0,1;0rad)
  Solid = false
  Source = -> Face119
  Symmetric = false
FEATURE [Part::Feature] Face120
  shape: bbox 10 x 16.5 x 2e-07 mm, 1 faces, 0 solids (baked)
FEATURE [Part::Feature] Face121
  shape: bbox 10 x 16.5 x 2e-07 mm, 1 faces, 0 solids (baked)
FEATURE [Part::Revolution] Revolve127  label="plugHousing047"
  Angle = 360
  Axis = (0,1,0)
  Base = (0,0,0)
  FaceMakerClass = Part::FaceMakerBullseye
  Placement = pos=(0,0,36.15) rot=(0,0,1;0rad)
  Solid = false
  Source = -> Face121
  Symmetric = false
FEATURE [Part::Feature] Face122
  shape: bbox 10 x 16.5 x 2e-07 mm, 1 faces, 0 solids (baked)
FEATURE [Part::Feature] Face123
  shape: bbox 10 x 16.5 x 2e-07 mm, 1 faces, 0 solids (baked)
FEATURE [Part::Revolution] Revolve128  label="plugHousing048"
  Angle = 360
  Axis = (0,1,0)
  Base = (0,0,0)
  FaceMakerClass = Part::FaceMakerBullseye
  Placement = pos=(0,0,36.15) rot=(0,0,1;0rad)
  Solid = false
  Source = -> Face123
  Symmetric = false
FEATURE [Part::MultiFuse] Fusion100  label="plugHousing054"
  Placement = pos=(0,0,0) rot=(0,0,1;1.5708rad)
  Shapes = -> [Revolve130,Revolve128]
FEATURE [Part::Feature] Face124
  shape: bbox 10 x 16.5 x 2e-07 mm, 1 faces, 0 solids (baked)
FEATURE [Part::Feature] Face125
  shape: bbox 10 x 16.5 x 2e-07 mm, 1 faces, 0 solids (baked)
FEATURE [Part::Revolution] Revolve129  label="plugHousing049"
  Angle = 360
  Axis = (0,1,0)
  Base = (0,0,0)
  FaceMakerClass = Part::FaceMakerBullseye
  Placement = pos=(0,0,36.15) rot=(0,0,1;0rad)
  Solid = false
  Source = -> Face125
  Symmetric = false
FEATURE [Part::Feature] Face126
  shape: bbox 10 x 16.5 x 2e-07 mm, 1 faces, 0 solids (baked)
FEATURE [Part::Revolution] Revolve131  label="plugHousing058"
  Angle = 360
  Axis = (0,1,0)
  Base = (0,0,0)
  FaceMakerClass = Part::FaceMakerBullseye
  Placement = pos=(0,0,36.15) rot=(0,0,1;0rad)
  Solid = false
  Source = -> Face120
  Symmetric = false
FEATURE [Part::MultiFuse] Fusion099  label="plugHousing053"
  Placement = pos=(0,0,0) rot=(0,0,1;1.5708rad)
  Shapes = -> [Revolve127,Revolve131]
FEATURE [Part::MultiFuse] Fusion102  label="plugHousing056"
  Placement = pos=(0,19,0) rot=(0,0,1;3.14159rad)
  Shapes = -> [Fusion100,Fusion099]
FEATURE [Part::Revolution] Revolve132  label="plugHousing059"
  Angle = 360
  Axis = (0,1,0)
  Base = (0,0,0)
  FaceMakerClass = Part::FaceMakerBullseye
  Placement = pos=(0,0,36.15) rot=(0,0,1;0rad)
  Solid = false
  Source = -> Face126
  Symmetric = false
FEATURE [Part::Revolution] Revolve133  label="plugHousing060"
  Angle = 360
  Axis = (0,1,0)
  Base = (0,0,0)
  FaceMakerClass = Part::FaceMakerBullseye
  Placement = pos=(0,0,36.15) rot=(0,0,1;0rad)
  Solid = false
  Source = -> Face122
  Symmetric = false
FEATURE [Part::MultiFuse] Fusion097  label="plugHousing051"
  Placement = pos=(0,0,0) rot=(0,0,1;1.5708rad)
  Shapes = -> [Revolve133,Revolve132]
FEATURE [Part::Revolution] Revolve134  label="plugHousing061"
  Angle = 360
  Axis = (0,1,0)
  Base = (0,0,0)
  FaceMakerClass = Part::FaceMakerBullseye
  Placement = pos=(0,0,36.15) rot=(0,0,1;0rad)
  Solid = false
  Source = -> Face124
  Symmetric = false
FEATURE [Part::MultiFuse] Fusion101  label="plugHousing055"
  Placement = pos=(0,0,0) rot=(0,0,1;1.5708rad)
  Shapes = -> [Revolve129,Revolve134]
FEATURE [Part::MultiFuse] Fusion098  label="plugHousing052"
  Placement = pos=(0,19,0) rot=(0,0,1;3.14159rad)
  Shapes = -> [Fusion097,Fusion101]
FEATURE [Part::MultiFuse] Fusion103  label="plugHousing057"
  Placement = pos=(122.621,0,-0.15) rot=(0,0,1;0rad)
  Shapes = -> [Fusion102,Fusion098]
FEATURE [Part::Box] Box028  label="Cube015"
  AttacherType = Attacher::AttachEngine3D
  Height = 28
  Length = 3
  Placement = pos=(110.7,19,22) rot=(0,0,1;0rad)
  Width = 15.7
FEATURE [Part::Cylinder] Cylinder044
  Angle = 360
  AttacherType = Attacher::AttachEngine3D
  Height = 20
  Placement = pos=(0,0,36.15) rot=(0,0,1;0rad)
  Radius = 10.3
FEATURE [Part::Cylinder] Cylinder045
  Angle = 360
  AttacherType = Attacher::AttachEngine3D
  Height = 10
  Placement = pos=(0,0,36.15) rot=(0,0,1;0rad)
  Radius = 4
FEATURE [Part::MultiFuse] Fusion104  label="removeToCreteHoleForPlugHousing040"
  Placement = pos=(70,19,36) rot=(0,1,0;1.5708rad)
  Shapes = -> [Cylinder044,Cylinder045]
FEATURE [Part::Cut] Cut046  label="plugHousingTab003"
  Base = -> Box028
  Tool = -> Fusion104
FEATURE [Part::MultiFuse] Fusion105  label="plugHousing062"
  Shapes = -> [Fusion103,Cut046]
FEATURE [Part::Fillet] Fillet042
  Base = -> Fusion105
  Edges = 1 edges r=2: [Edge25]
FEATURE [Part::Fillet] Fillet043  label="plugHousing063"
  Base = -> Fillet042
  Edges = 1 edges r=2: [Edge8]
  Placement = pos=(7,0,0) rot=(0,0,1;0rad)
FEATURE [Part::Feature] Face127
  shape: bbox 10 x 16.5 x 2e-07 mm, 1 faces, 0 solids (baked)
FEATURE [Part::Feature] Face128
  shape: bbox 10 x 16.5 x 2e-07 mm, 1 faces, 0 solids (baked)
FEATURE [Part::Revolution] Revolve137  label="plugHousing070"
  Angle = 360
  Axis = (0,1,0)
  Base = (0,0,0)
  FaceMakerClass = Part::FaceMakerBullseye
  Placement = pos=(0,0,36.15) rot=(0,0,1;0rad)
  Solid = false
  Source = -> Face127
  Symmetric = false
FEATURE [Part::Revolution] Revolve140  label="plugHousing073"
  Angle = 360
  Axis = (0,1,0)
  Base = (0,0,0)
  FaceMakerClass = Part::FaceMakerBullseye
  Placement = pos=(0,0,36.15) rot=(0,0,1;0rad)
  Solid = false
  Source = -> Face128
  Symmetric = false
FEATURE [Part::Feature] Face129
  shape: bbox 10 x 16.5 x 2e-07 mm, 1 faces, 0 solids (baked)
FEATURE [Part::Revolution] Revolve138  label="plugHousing071"
  Angle = 360
  Axis = (0,1,0)
  Base = (0,0,0)
  FaceMakerClass = Part::FaceMakerBullseye
  Placement = pos=(0,0,36.15) rot=(0,0,1;0rad)
  Solid = false
  Source = -> Face129
  Symmetric = false
FEATURE [Part::Feature] Face130
  shape: bbox 10 x 16.5 x 2e-07 mm, 1 faces, 0 solids (baked)
FEATURE [Part::Revolution] Revolve139  label="plugHousing072"
  Angle = 360
  Axis = (0,1,0)
  Base = (0,0,0)
  FaceMakerClass = Part::FaceMakerBullseye
  Placement = pos=(0,0,36.15) rot=(0,0,1;0rad)
  Solid = false
  Source = -> Face130
  Symmetric = false
FEATURE [Part::Feature] Face131
  shape: bbox 10 x 16.5 x 2e-07 mm, 1 faces, 0 solids (baked)
FEATURE [Part::Revolution] Revolve135  label="plugHousing068"
  Angle = 360
  Axis = (0,1,0)
  Base = (0,0,0)
  FaceMakerClass = Part::FaceMakerBullseye
  Placement = pos=(0,0,36.15) rot=(0,0,1;0rad)
  Solid = false
  Source = -> Face131
  Symmetric = false
FEATURE [Part::MultiFuse] Fusion112  label="plugHousing078"
  Placement = pos=(0,0,0) rot=(0,0,1;1.5708rad)
  Shapes = -> [Revolve135,Revolve139]
FEATURE [Part::Feature] Face132
  shape: bbox 10 x 16.5 x 2e-07 mm, 1 faces, 0 solids (baked)
FEATURE [Part::Revolution] Revolve141  label="plugHousing074"
  Angle = 360
  Axis = (0,1,0)
  Base = (0,0,0)
  FaceMakerClass = Part::FaceMakerBullseye
  Placement = pos=(0,0,36.15) rot=(0,0,1;0rad)
  Solid = false
  Source = -> Face132
  Symmetric = false
FEATURE [Part::MultiFuse] Fusion110  label="plugHousing076"
  Placement = pos=(0,0,0) rot=(0,0,1;1.5708rad)
  Shapes = -> [Revolve141,Revolve140]
FEATURE [Part::Feature] Face133
  shape: bbox 10 x 16.5 x 2e-07 mm, 1 faces, 0 solids (baked)
FEATURE [Part::Revolution] Revolve136  label="plugHousing069"
  Angle = 360
  Axis = (0,1,0)
  Base = (0,0,0)
  FaceMakerClass = Part::FaceMakerBullseye
  Placement = pos=(0,0,36.15) rot=(0,0,1;0rad)
  Solid = false
  Source = -> Face133
  Symmetric = false
FEATURE [Part::MultiFuse] Fusion106  label="plugHousing064"
  Placement = pos=(0,0,0) rot=(0,0,1;1.5708rad)
  Shapes = -> [Revolve138,Revolve136]
FEATURE [Part::MultiFuse] Fusion108  label="plugHousing066"
  Placement = pos=(0,19,0) rot=(0,0,1;3.14159rad)
  Shapes = -> [Fusion106,Fusion112]
FEATURE [Part::Feature] Face134
  shape: bbox 10 x 16.5 x 2e-07 mm, 1 faces, 0 solids (baked)
FEATURE [Part::Revolution] Revolve142  label="plugHousing075"
  Angle = 360
  Axis = (0,1,0)
  Base = (0,0,0)
  FaceMakerClass = Part::FaceMakerBullseye
  Placement = pos=(0,0,36.15) rot=(0,0,1;0rad)
  Solid = false
  Source = -> Face134
  Symmetric = false
FEATURE [Part::MultiFuse] Fusion107  label="plugHousing065"
  Placement = pos=(0,0,0) rot=(0,0,1;1.5708rad)
  Shapes = -> [Revolve137,Revolve142]
FEATURE [Part::MultiFuse] Fusion111  label="plugHousing077"
  Placement = pos=(0,19,0) rot=(0,0,1;3.14159rad)
  Shapes = -> [Fusion110,Fusion107]
FEATURE [Part::MultiFuse] Fusion109  label="plugHousing067"
  Placement = pos=(131.236,0,-0.15) rot=(0,0,1;0rad)
  Shapes = -> [Fusion108,Fusion111]
FEATURE [Part::MultiFuse] Fusion113  label="plugHousing079"
  Shapes = -> [Fillet043,Fusion109]
FEATURE [Part::Feature] Face135
  shape: bbox 3.5 x 17.8 x 2e-07 mm, 1 faces, 0 solids (baked)
FEATURE [Part::Revolution] Revolve143  label="removeToCreateScrewAndThreadedInsertHole049"
  Angle = 360
  Axis = (0,1,0)
  Base = (0,0,0)
  FaceMakerClass = Part::FaceMakerBullseye
  Placement = pos=(12.5,0,10) rot=(0,0,1;0rad)
  Solid = false
  Source = -> Face135
  Symmetric = false
FEATURE [Part::Feature] Face136
  shape: bbox 3.5 x 17.8 x 2e-07 mm, 1 faces, 0 solids (baked)
FEATURE [Part::Revolution] Revolve144  label="removeToCreateScrewAndThreadedInsertHole050"
  Angle = 360
  Axis = (0,1,0)
  Base = (0,0,0)
  FaceMakerClass = Part::FaceMakerBullseye
  Placement = pos=(12.5,0,62) rot=(0,0,1;0rad)
  Solid = false
  Source = -> Face136
  Symmetric = false
FEATURE [Part::Feature] Face137
  shape: bbox 3.5 x 17.8 x 2e-07 mm, 1 faces, 0 solids (baked)
FEATURE [Part::Revolution] Revolve145  label="removeToCreateScrewAndThreadedInsertHole051"
  Angle = 360
  Axis = (0,1,0)
  Base = (0,0,0)
  FaceMakerClass = Part::FaceMakerBullseye
  Placement = pos=(89.5,0,68.5) rot=(0,0,1;0rad)
  Solid = false
  Source = -> Face137
  Symmetric = false
FEATURE [Part::Feature] Face138
  shape: bbox 3.5 x 17.8 x 2e-07 mm, 1 faces, 0 solids (baked)
FEATURE [Part::Revolution] Revolve146  label="removeToCreateScrewAndThreadedInsertHole052"
  Angle = 360
  Axis = (0,1,0)
  Base = (0,0,0)
  FaceMakerClass = Part::FaceMakerBullseye
  Placement = pos=(89.5,0,3.5) rot=(0,0,1;0rad)
  Solid = false
  Source = -> Face138
  Symmetric = false
FEATURE [Part::Feature] Face139
  shape: bbox 3.5 x 17.8 x 2e-07 mm, 1 faces, 0 solids (baked)
FEATURE [Part::Revolution] Revolve147  label="removeToCreateScrewAndThreadedInsertHole053"
  Angle = 360
  Axis = (0,1,0)
  Base = (0,0,0)
  FaceMakerClass = Part::FaceMakerBullseye
  Placement = pos=(109.5,4.7,3.5) rot=(0,0,1;0rad)
  Solid = false
  Source = -> Face139
  Symmetric = false
FEATURE [Part::Feature] Face140
  shape: bbox 3.5 x 17.8 x 2e-07 mm, 1 faces, 0 solids (baked)
FEATURE [Part::Revolution] Revolve148  label="removeToCreateScrewAndThreadedInsertHole054"
  Angle = 360
  Axis = (0,1,0)
  Base = (0,0,0)
  FaceMakerClass = Part::FaceMakerBullseye
  Placement = pos=(109.5,4.7,68.5) rot=(0,0,1;0rad)
  Solid = false
  Source = -> Face140
  Symmetric = false
FEATURE [Part::MultiFuse] Fusion114  label="removeToCreateScrewAndThreadedInsertHole055"
  Shapes = -> [Revolve148,Revolve147,Revolve146,Revolve145,Revolve144,Revolve143]
FEATURE [Part::Cut] Cut047  label="casePillars004"
  Base = -> Cut037
  Tool = -> Fusion114
FEATURE [Part::Feature] Face141
  shape: bbox 3.5 x 17.8 x 2e-07 mm, 1 faces, 0 solids (baked)
FEATURE [Part::Feature] Face142
  shape: bbox 3.5 x 17.8 x 2e-07 mm, 1 faces, 0 solids (baked)
FEATURE [Part::Feature] Face143
  shape: bbox 3.5 x 17.8 x 2e-07 mm, 1 faces, 0 solids (baked)
FEATURE [Part::Revolution] Revolve149  label="removeToCreateScrewAndThreadedInsertHole057"
  Angle = 360
  Axis = (0,1,0)
  Base = (0,0,0)
  FaceMakerClass = Part::FaceMakerBullseye
  Placement = pos=(12.5,0,10) rot=(0,0,1;0rad)
  Solid = false
  Source = -> Face141
  Symmetric = false
FEATURE [Part::Feature] Face144
  shape: bbox 3.5 x 17.8 x 2e-07 mm, 1 faces, 0 solids (baked)
FEATURE [Part::Feature] Face145
  shape: bbox 3.5 x 17.8 x 2e-07 mm, 1 faces, 0 solids (baked)
FEATURE [Part::Feature] Face146
  shape: bbox 3.5 x 17.8 x 2e-07 mm, 1 faces, 0 solids (baked)
FEATURE [Part::Revolution] Revolve150  label="removeToCreateScrewAndThreadedInsertHole058"
  Angle = 360
  Axis = (0,1,0)
  Base = (0,0,0)
  FaceMakerClass = Part::FaceMakerBullseye
  Placement = pos=(12.5,0,62) rot=(0,0,1;0rad)
  Solid = false
  Source = -> Face146
  Symmetric = false
FEATURE [Part::Revolution] Revolve151  label="removeToCreateScrewAndThreadedInsertHole059"
  Angle = 360
  Axis = (0,1,0)
  Base = (0,0,0)
  FaceMakerClass = Part::FaceMakerBullseye
  Placement = pos=(89.5,0,68.5) rot=(0,0,1;0rad)
  Solid = false
  Source = -> Face143
  Symmetric = false
FEATURE [Part::Revolution] Revolve152  label="removeToCreateScrewAndThreadedInsertHole060"
  Angle = 360
  Axis = (0,1,0)
  Base = (0,0,0)
  FaceMakerClass = Part::FaceMakerBullseye
  Placement = pos=(89.5,0,3.5) rot=(0,0,1;0rad)
  Solid = false
  Source = -> Face142
  Symmetric = false
FEATURE [Part::Revolution] Revolve153  label="removeToCreateScrewAndThreadedInsertHole061"
  Angle = 360
  Axis = (0,1,0)
  Base = (0,0,0)
  FaceMakerClass = Part::FaceMakerBullseye
  Placement = pos=(109.5,4.7,3.5) rot=(0,0,1;0rad)
  Solid = false
  Source = -> Face145
  Symmetric = false
FEATURE [Part::Revolution] Revolve154  label="removeToCreateScrewAndThreadedInsertHole062"
  Angle = 360
  Axis = (0,1,0)
  Base = (0,0,0)
  FaceMakerClass = Part::FaceMakerBullseye
  Placement = pos=(109.5,4.7,68.5) rot=(0,0,1;0rad)
  Solid = false
  Source = -> Face144
  Symmetric = false
FEATURE [Part::MultiFuse] Fusion115  label="removeToCreateScrewAndThreadedInsertHole056"
  Shapes = -> [Revolve154,Revolve153,Revolve152,Revolve151,Revolve150,Revolve149]
FEATURE [Part::Feature] Face147
  shape: bbox 9.8 x 26.5 x 2e-07 mm, 1 faces, 0 solids (baked)
FEATURE [Part::Revolution] Revolve155
  Angle = 360
  Axis = (0,1,0)
  Base = (0,0,0)
  FaceMakerClass = Part::FaceMakerBullseye
  Placement = pos=(0,0,0) rot=(0,0,1;1.5708rad)
  Solid = false
  Source = -> Face147
  Symmetric = false
FEATURE [Part::Feature] Face148
  shape: bbox 9.8 x 26.5 x 2e-07 mm, 1 faces, 0 solids (baked)
FEATURE [Part::Revolution] Revolve156
  Angle = 360
  Axis = (0,1,0)
  Base = (0,0,0)
  FaceMakerClass = Part::FaceMakerBullseye
  Placement = pos=(0,0,0) rot=(0,0,1;1.5708rad)
  Solid = false
  Source = -> Face148
  Symmetric = false
FEATURE [Part::MultiFuse] Fusion116
  Placement = pos=(-18,19,36) rot=(0,0,1;0rad)
  Shapes = -> [Revolve156,Revolve155]
FEATURE [Part::Box] Box029  label="Cube016"
  AttacherType = Attacher::AttachEngine3D
  Height = 28
  Length = 3
  Placement = pos=(110.7,19,22) rot=(0,0,1;0rad)
  Width = 15.7
FEATURE [Part::Cylinder] Cylinder046
  Angle = 360
  AttacherType = Attacher::AttachEngine3D
  Height = 10
  Placement = pos=(0,0,36.15) rot=(0,0,1;0rad)
  Radius = 4
FEATURE [Part::Cylinder] Cylinder047
  Angle = 360
  AttacherType = Attacher::AttachEngine3D
  Height = 20
  Placement = pos=(0,0,36.15) rot=(0,0,1;0rad)
  Radius = 10.3
FEATURE [Part::MultiFuse] Fusion117  label="removeToCreteHoleForPlugHousing041"
  Placement = pos=(70,19,36) rot=(0,1,0;1.5708rad)
  Shapes = -> [Cylinder047,Cylinder046]
FEATURE [Part::Cut] Cut049  label="plugHousingTab004"
  Base = -> Box029
  Placement = pos=(-107.4,-14,0) rot=(0,0,1;0rad)
  Tool = -> Fusion117
FEATURE [Part::Box] Box030  label="Cube017"
  AttacherType = Attacher::AttachEngine3D
  Height = 28
  Length = 3
  Placement = pos=(110.7,19,22) rot=(0,0,1;0rad)
  Width = 15.7
FEATURE [Part::Cylinder] Cylinder048
  Angle = 360
  AttacherType = Attacher::AttachEngine3D
  Height = 10
  Placement = pos=(0,0,36.15) rot=(0,0,1;0rad)
  Radius = 4
FEATURE [Part::Cylinder] Cylinder049
  Angle = 360
  AttacherType = Attacher::AttachEngine3D
  Height = 20
  Placement = pos=(0,0,36.15) rot=(0,0,1;0rad)
  Radius = 10.3
FEATURE [Part::MultiFuse] Fusion118  label="removeToCreteHoleForPlugHousing042"
  Placement = pos=(70,19,36) rot=(0,1,0;1.5708rad)
  Shapes = -> [Cylinder049,Cylinder048]
FEATURE [Part::Cut] Cut050  label="plugHousingTab005"
  Base = -> Box030
  Placement = pos=(-107.4,-14,0) rot=(0,0,1;0rad)
  Tool = -> Fusion118
FEATURE [Part::MultiFuse] Fusion119
  Placement = pos=(9.6,23,0) rot=(0,0,1;3.14159rad)
  Shapes = -> [Cut049,Cut050]
FEATURE [Part::Box] Box031  label="Cube018"
  AttacherType = Attacher::AttachEngine3D
  Height = 10
  Length = 3
  Placement = pos=(3.3,4,12) rot=(0,0,1;0rad)
  Width = 10
FEATURE [Part::Fillet] Fillet044
  Base = -> Box031
  Edges = 1 edges r=2: [Edge11]
FEATURE [Part::Box] Box032  label="Cube019"
  AttacherType = Attacher::AttachEngine3D
  Height = 10
  Length = 3
  Placement = pos=(3.3,4,50) rot=(0,0,1;0rad)
  Width = 10
FEATURE [Part::Fillet] Fillet045
  Base = -> Box032
  Edges = 1 edges r=2: [Edge12]
FEATURE [Part::Box] Box033  label="Cube020"
  AttacherType = Attacher::AttachEngine3D
  Height = 28
  Length = 4
  Placement = pos=(5,0,22) rot=(0,0,1;0rad)
  Width = 10
FEATURE [Part::Fillet] Fillet046
  Base = -> Box033
  Edges = 1 edges r=1: [Edge7]
FEATURE [Part::Fillet] Fillet047
  Base = -> Fillet046
  Edges = 1 edges r=2: [Edge5]
FEATURE [Part::Fillet] Fillet048
  Base = -> Fillet047
  Edges = 1 edges r=2: [Edge2]
FEATURE [Part::Cylinder] Cylinder050
  Angle = 360
  AttacherType = Attacher::AttachEngine3D
  Height = 20
  Placement = pos=(0,0,36.15) rot=(0,0,1;0rad)
  Radius = 8.2
FEATURE [Part::Cylinder] Cylinder051
  Angle = 360
  AttacherType = Attacher::AttachEngine3D
  Height = 10
  Placement = pos=(0,0,36.15) rot=(0,0,1;0rad)
  Radius = 4
FEATURE [Part::MultiFuse] Fusion120  label="removeToCreteHoleForPlugHousing043"
  Placement = pos=(-42,19,36) rot=(0,1,0;1.5708rad)
  Shapes = -> [Cylinder050,Cylinder051]
FEATURE [Sketcher::SketchObject] Sketch067  label="topSketch018"
  FullyConstrained = true
  sketch-geometry (4):
    g0: LineSegment StartX=16.8446 StartY=31.512 StartZ=0 EndX=16.3251 EndY=34.4666 EndZ=0
    g1: ArcOfCircle CenterX=19 CenterY=19.2524 CenterZ=0 NormalX=0 NormalY=0 NormalZ=1 AngleXU=0 Radius=15.4476 StartAngle=1.74483 EndAngle=2.72717
    g2: ArcOfCircle CenterX=19 CenterY=19.2524 CenterZ=0 NormalX=0 NormalY=0 NormalZ=1 AngleXU=0 Radius=12.4476 StartAngle=1.74483 EndAngle=2.73189
    g3: LineSegment StartX=4.86004 StartY=25.4725 StartZ=0 EndX=7.58253 EndY=24.2107 EndZ=0
  constraints (7):
    c: Block(g0)
    c: Coincident(g1,g0)
    c: Coincident(g2,g0)
    c: Coincident(g3,g1)
    c: Coincident(g3,g2)
    c: Block(g1)
    c: Block(g2)
FEATURE [Part::Extrusion] Extrude058
  Base = -> Sketch067
  Dir = (0,0,1)
  DirMode = 2
  FaceMakerClass = Part::FaceMakerBullseye
  LengthFwd = 10
  LengthRev = 0
  Placement = pos=(0,0,31) rot=(0,0,1;0rad)
  Solid = true
  Symmetric = false
FEATURE [Part::Cut] Cut051
  Base = -> Extrude058
  Tool = -> Fusion120
FEATURE [Part::Fillet] Fillet049
  Base = -> Cut051
  Edges = 1 edges r=2: [Edge1]
FEATURE [Part::Fillet] Fillet050
  Base = -> Fillet049
  Edges = 1 edges r=2.5: [Edge1]
FEATURE [Part::Fillet] Fillet051
  Base = -> Fillet050
  Edges = 1 edges r=2.5: [Edge2]
FEATURE [Part::MultiFuse] Fusion121  label="wireHolder003"
  Shapes = -> [Fusion116,Fillet051]
FEATURE [Part::MultiFuse] Fusion122
  Shapes = -> [Fillet045,Fusion121]
FEATURE [Part::MultiFuse] Fusion123  label="wireHolder004"
  Shapes = -> [Fusion122,Fillet048]
FEATURE [Part::MultiFuse] Fusion124  label="wireHolder005"
  Shapes = -> [Fillet044,Fusion119,Fusion123]
FEATURE [Sketcher::SketchObject] Sketch068  label="topSketch019"
  FullyConstrained = true
  sketch-geometry (6):
    g0: LineSegment StartX=19 StartY=38 StartZ=0 EndX=117 EndY=38 EndZ=0
    g1: ArcOfCircle CenterX=19 CenterY=19 CenterZ=0 NormalX=0 NormalY=0 NormalZ=1 AngleXU=0 Radius=19 StartAngle=1.5708 EndAngle=3.14159
    g2: LineSegment StartX=117 StartY=38 StartZ=0 EndX=117 EndY=19 EndZ=0
    g3: LineSegment StartX=98 StartY=1.0161e-12 StartZ=0 EndX=5.22862e-06 EndY=1.0161e-12 EndZ=0
    g4: LineSegment StartX=5.22862e-06 StartY=19 StartZ=0 EndX=5.22862e-06 EndY=1.0161e-12 EndZ=0
    g5: ArcOfCircle CenterX=98 CenterY=19 CenterZ=0 NormalX=0 NormalY=0 NormalZ=1 AngleXU=0 Radius=19 StartAngle=4.71239 EndAngle=6.28319
  constraints (16):
    c: Horizontal(g0)
    c: Distance(g0) = 98
    c: Coincident(g1,g0)
    c: Block(g1)
    c: Coincident(g2,g0)
    c: Vertical(g2)
    c: Distance(g2) = 19
    c: Horizontal(g3)
    c: Coincident(g4,g1)
    c: Vertical(g4)
    c: Coincident(g3,g4)
    c: Block(g3)
    c: Coincident(g5,g2)
    c: Coincident(g5,g3)
    c: Block(g0)
    c: Block(g5)
FEATURE [Part::Extrusion] Extrude059  label="sideA002"
  Base = -> Sketch068
  Dir = (0,0,1)
  DirMode = 2
  FaceMakerClass = Part::FaceMakerBullseye
  LengthFwd = 3
  LengthRev = 0
  Placement = pos=(0,0,-2.7) rot=(0,0,1;0rad)
  Solid = true
  Symmetric = false
FEATURE [Sketcher::SketchObject] Sketch069  label="topSketch020"
  FullyConstrained = true
  sketch-geometry (6):
    g0: LineSegment StartX=19 StartY=38 StartZ=0 EndX=117 EndY=38 EndZ=0
    g1: ArcOfCircle CenterX=19 CenterY=19 CenterZ=0 NormalX=0 NormalY=0 NormalZ=1 AngleXU=0 Radius=19 StartAngle=1.5708 EndAngle=3.14159
    g2: LineSegment StartX=117 StartY=38 StartZ=0 EndX=117 EndY=19 EndZ=0
    g3: LineSegment StartX=98 StartY=1.0161e-12 StartZ=0 EndX=5.22862e-06 EndY=1.0161e-12 EndZ=0
    g4: LineSegment StartX=5.22862e-06 StartY=19 StartZ=0 EndX=5.22862e-06 EndY=1.0161e-12 EndZ=0
    g5: ArcOfCircle CenterX=98 CenterY=19 CenterZ=0 NormalX=0 NormalY=0 NormalZ=1 AngleXU=0 Radius=19 StartAngle=4.71239 EndAngle=6.28319
  constraints (16):
    c: Horizontal(g0)
    c: Distance(g0) = 98
    c: Coincident(g1,g0)
    c: Block(g1)
    c: Coincident(g2,g0)
    c: Vertical(g2)
    c: Distance(g2) = 19
    c: Horizontal(g3)
    c: Coincident(g4,g1)
    c: Vertical(g4)
    c: Coincident(g3,g4)
    c: Block(g3)
    c: Coincident(g5,g2)
    c: Coincident(g5,g3)
    c: Block(g0)
    c: Block(g5)
FEATURE [Part::Extrusion] Extrude060  label="sideB002"
  Base = -> Sketch069
  Dir = (0,0,1)
  DirMode = 2
  FaceMakerClass = Part::FaceMakerBullseye
  LengthFwd = 3
  LengthRev = 0
  Placement = pos=(0,0,71.7) rot=(0,0,1;0rad)
  Solid = true
  Symmetric = false
FEATURE [Part::MultiFuse] Fusion127  label="removeFromBottom001"
  Placement = pos=(2,0,0) rot=(0,0,1;0rad)
  Shapes = -> [Extrude059,Extrude060]
FEATURE [Part::Cylinder] Cylinder052
  Angle = 360
  AttacherType = Attacher::AttachEngine3D
  Height = 20
  Placement = pos=(0,0,36.15) rot=(0,0,1;0rad)
  Radius = 14
FEATURE [Part::Cylinder] Cylinder053
  Angle = 360
  AttacherType = Attacher::AttachEngine3D
  Height = 10
  Placement = pos=(0,0,36.15) rot=(0,0,1;0rad)
  Radius = 4
FEATURE [Part::MultiFuse] Fusion128  label="removeToCreteHoleForPlugHousing044"
  Placement = pos=(70,19,36) rot=(0,1,0;1.5708rad)
  Shapes = -> [Cylinder052,Cylinder053]
FEATURE [Part::Cut] Cut052  label="bottom011"
  Base = -> Extrude043
  Tool = -> Fusion128
FEATURE [Part::Cut] Cut054  label="bottom012"
  Base = -> Cut052
  Tool = -> Fusion115
FEATURE [Sketcher::SketchObject] Sketch070
  FullyConstrained = true
  Placement = pos=(117,19,0) rot=(0.57735,0.57735,0.57735;2.0944rad)
  sketch-geometry (48):
    g0: LineSegment StartX=-49.19 StartY=69.25 StartZ=0 EndX=-49.19 EndY=66.25 EndZ=0
    g1: LineSegment StartX=-49.19 StartY=63.5 StartZ=0 EndX=-49.19 EndY=60.5 EndZ=0
    g2: LineSegment StartX=-49.19 StartY=57.75 StartZ=0 EndX=-49.19 EndY=54.75 EndZ=0
    g3: LineSegment StartX=-49.19 StartY=52 StartZ=0 EndX=-49.19 EndY=49 EndZ=0
    g4: LineSegment StartX=-49.19 StartY=46.25 StartZ=0 EndX=-49.19 EndY=43.25 EndZ=0
    g5: LineSegment StartX=-49.19 StartY=40.5 StartZ=0 EndX=-49.19 EndY=37.5 EndZ=0
    g6: LineSegment StartX=-49.19 StartY=34.5 StartZ=0 EndX=-49.19 EndY=31.5 EndZ=0
    g7: LineSegment StartX=-49.19 StartY=28.75 StartZ=0 EndX=-49.19 EndY=25.75 EndZ=0
    g8: LineSegment StartX=-49.19 StartY=23 StartZ=0 EndX=-49.19 EndY=20 EndZ=0
    g9: LineSegment StartX=-49.19 StartY=17.25 StartZ=0 EndX=-49.19 EndY=14.25 EndZ=0
    g10: LineSegment StartX=-49.19 StartY=11.5 StartZ=0 EndX=-49.19 EndY=8.5 EndZ=0
    g11: LineSegment StartX=-49.19 StartY=5.75 StartZ=0 EndX=-49.19 EndY=2.75 EndZ=0
    g12: ArcOfCircle CenterX=-1.5 CenterY=67.75 CenterZ=0 NormalX=0 NormalY=0 NormalZ=1 AngleXU=0 Radius=1.5 StartAngle=4.71239 EndAngle=7.85398
    g13: ArcOfCircle CenterX=-1.5 CenterY=62 CenterZ=0 NormalX=0 NormalY=0 NormalZ=1 AngleXU=0 Radius=1.5 StartAngle=4.71239 EndAngle=7.85398
    g14: ArcOfCircle CenterX=-1.5 CenterY=56.25 CenterZ=0 NormalX=0 NormalY=0 NormalZ=1 AngleXU=0 Radius=1.5 StartAngle=4.71239 EndAngle=7.85398
    g15: ArcOfCircle CenterX=-11.49 CenterY=50.5 CenterZ=0 NormalX=0 NormalY=0 NormalZ=1 AngleXU=0 Radius=1.5 StartAngle=4.71239 EndAngle=7.85398
    g16: ArcOfCircle CenterX=-16.28 CenterY=44.75 CenterZ=0 NormalX=0 NormalY=0 NormalZ=1 AngleXU=0 Radius=1.5 StartAngle=4.71239 EndAngle=7.85398
    g17: ArcOfCircle CenterX=-18.2337 CenterY=39 CenterZ=0 NormalX=0 NormalY=0 NormalZ=1 AngleXU=0 Radius=1.5 StartAngle=4.71485 EndAngle=7.85398
    g18: ArcOfCircle CenterX=-16.2837 CenterY=27.25 CenterZ=0 NormalX=0 NormalY=0 NormalZ=1 AngleXU=0 Radius=1.5 StartAngle=4.71485 EndAngle=7.85398
    g19: ArcOfCircle CenterX=-18.2337 CenterY=33 CenterZ=0 NormalX=0 NormalY=0 NormalZ=1 AngleXU=0 Radius=1.5 StartAngle=4.71485 EndAngle=7.85398
    g20: ArcOfCircle CenterX=-11.49 CenterY=21.5 CenterZ=0 NormalX=0 NormalY=0 NormalZ=1 AngleXU=0 Radius=1.5 StartAngle=4.71239 EndAngle=7.85398
    g21: ArcOfCircle CenterX=-1.5 CenterY=4.25 CenterZ=0 NormalX=0 NormalY=0 NormalZ=1 AngleXU=0 Radius=1.5 StartAngle=4.71239 EndAngle=7.85398
    g22: ArcOfCircle CenterX=-1.5 CenterY=10 CenterZ=0 NormalX=0 NormalY=0 NormalZ=1 AngleXU=0 Radius=1.5 StartAngle=4.71239 EndAngle=7.85398
    g23: ArcOfCircle CenterX=-1.5 CenterY=15.75 CenterZ=0 NormalX=0 NormalY=0 NormalZ=1 AngleXU=0 Radius=1.5 StartAngle=4.71239 EndAngle=7.85398
    g24: LineSegment StartX=-49.19 StartY=69.25 StartZ=0 EndX=-1.5 EndY=69.25 EndZ=0
    g25: LineSegment StartX=-49.19 StartY=66.25 StartZ=0 EndX=-1.5 EndY=66.25 EndZ=0
    g26: LineSegment StartX=-49.19 StartY=63.5 StartZ=0 EndX=-1.5 EndY=63.5 EndZ=0
    g27: LineSegment StartX=-49.19 StartY=60.5 StartZ=0 EndX=-1.5 EndY=60.5 EndZ=0
    g28: LineSegment StartX=-49.19 StartY=57.75 StartZ=0 EndX=-1.5 EndY=57.75 EndZ=0
    g29: LineSegment StartX=-49.19 StartY=54.75 StartZ=0 EndX=-1.5 EndY=54.75 EndZ=0
    g30: LineSegment StartX=-49.19 StartY=52 StartZ=0 EndX=-11.49 EndY=52 EndZ=0
    g31: LineSegment StartX=-49.19 StartY=49 StartZ=0 EndX=-11.49 EndY=49 EndZ=0
    g32: LineSegment StartX=-49.19 StartY=46.25 StartZ=0 EndX=-16.28 EndY=46.25 EndZ=0
    g33: LineSegment StartX=-49.19 StartY=43.25 StartZ=0 EndX=-16.28 EndY=43.25 EndZ=0
    g34: LineSegment StartX=-49.19 StartY=40.5 StartZ=0 EndX=-18.2337 EndY=40.5 EndZ=0
    g35: LineSegment StartX=-49.19 StartY=37.5 StartZ=0 EndX=-18.23 EndY=37.5 EndZ=0
    g36: LineSegment StartX=-49.19 StartY=34.5 StartZ=0 EndX=-18.2337 EndY=34.5 EndZ=0
    g37: LineSegment StartX=-49.19 StartY=31.5 StartZ=0 EndX=-18.23 EndY=31.5 EndZ=0
    g38: LineSegment StartX=-49.19 StartY=28.75 StartZ=0 EndX=-16.2837 EndY=28.75 EndZ=0
    g39: LineSegment StartX=-49.19 StartY=25.75 StartZ=0 EndX=-16.28 EndY=25.75 EndZ=0
    g40: LineSegment StartX=-49.19 StartY=23 StartZ=0 EndX=-11.49 EndY=23 EndZ=0
    g41: LineSegment StartX=-49.19 StartY=20 StartZ=0 EndX=-11.49 EndY=20 EndZ=0
    g42: LineSegment StartX=-49.19 StartY=17.25 StartZ=0 EndX=-1.5 EndY=17.25 EndZ=0
    g43: LineSegment StartX=-49.19 StartY=14.25 StartZ=0 EndX=-1.5 EndY=14.25 EndZ=0
    g44: LineSegment StartX=-49.19 StartY=11.5 StartZ=0 EndX=-1.5 EndY=11.5 EndZ=0
    g45: LineSegment StartX=-49.19 StartY=8.5 StartZ=0 EndX=-1.5 EndY=8.5 EndZ=0
    g46: LineSegment StartX=-49.19 StartY=5.75 StartZ=0 EndX=-1.5 EndY=5.75 EndZ=0
    g47: LineSegment StartX=-49.19 StartY=2.75 StartZ=0 EndX=-1.5 EndY=2.75 EndZ=0
  constraints (120):
    c: Vertical(g0)
    c: Distance(g0) = 3
    c: Block(g0)
    c: Vertical(g1)
    c: Distance(g1) = 3
    c: Vertical(g2)
    c: Equal(g0,g2) = 3
    c: Block(g2)
    c: Vertical(g3)
    c: Equal(g1,g3) = 3
    c: Vertical(g4)
    c: Equal(g0,g4) = 3
    c: Block(g4)
    c: Vertical(g5)
    c: Equal(g1,g5) = 3
    c: Vertical(g6)
    c: Equal(g0,g6) = 3
    c: Block(g6)
    c: Vertical(g7)
    c: Equal(g1,g7) = 3
    c: Vertical(g8)
    c: Equal(g0,g8) = 3
    c: Block(g8)
    c: Vertical(g9)
    c: Equal(g1,g9) = 3
    c: Vertical(g10)
    c: Equal(g0,g10) = 3
    c: Block(g10)
    c: Vertical(g11)
    c: Equal(g1,g11) = 3
    c: Block(g12)
    c: Block(g13)
    c: Block(g14)
    c: Block(g15)
    c: Block(g16)
    c: Block(g17)
    c: Block(g18)
    c: Block(g19)
    c: Block(g20)
    c: Block(g21)
    c: Block(g22)
    c: Block(g23)
    c: Block(g11)
    c: Block(g9)
    c: Block(g7)
    c: Block(g5)
    c: Block(g3)
    c: Block(g1)
    c: Coincident(g24,g0)
    c: Coincident(g24,g12)
    c: Horizontal(g24)
    c: Coincident(g25,g0)
    c: Coincident(g25,g12)
    c: Horizontal(g25)
    c: Coincident(g26,g1)
    c: Coincident(g26,g13)
    c: Horizontal(g26)
    c: Coincident(g27,g1)
    c: Coincident(g27,g13)
    c: Horizontal(g27)
    c: Coincident(g28,g2)
    c: Coincident(g28,g14)
    c: Horizontal(g28)
    c: Coincident(g29,g2)
    c: Coincident(g29,g14)
    c: Horizontal(g29)
    c: Coincident(g30,g3)
    c: Coincident(g30,g15)
    c: Horizontal(g30)
    c: Coincident(g31,g3)
    c: Coincident(g31,g15)
    c: Horizontal(g31)
    c: Coincident(g32,g4)
    c: Coincident(g32,g16)
    c: Horizontal(g32)
    c: Coincident(g33,g4)
    c: Coincident(g33,g16)
    c: Horizontal(g33)
    c: Coincident(g34,g5)
    c: Coincident(g34,g17)
    c: Horizontal(g34)
    c: Coincident(g35,g5)
    c: Coincident(g35,g17)
    c: Horizontal(g35)
    c: Coincident(g36,g6)
    c: Coincident(g36,g19)
    c: Horizontal(g36)
    c: Coincident(g37,g6)
    c: Coincident(g37,g19)
    c: Horizontal(g37)
    c: Coincident(g38,g7)
    c: Coincident(g38,g18)
    c: Horizontal(g38)
    c: Coincident(g39,g7)
    c: Coincident(g39,g18)
    c: Horizontal(g39)
    c: Coincident(g40,g8)
    c: Coincident(g40,g20)
    c: Horizontal(g40)
    c: Coincident(g41,g8)
    c: Coincident(g41,g20)
    c: Horizontal(g41)
    c: Coincident(g42,g9)
    c: Coincident(g42,g23)
    c: Horizontal(g42)
    c: Coincident(g43,g9)
    c: Coincident(g43,g23)
    c: Horizontal(g43)
    c: Coincident(g44,g10)
    c: Coincident(g44,g22)
    c: Horizontal(g44)
    c: Coincident(g45,g10)
    c: Coincident(g45,g22)
    c: Horizontal(g45)
    c: Coincident(g46,g11)
    c: Coincident(g46,g21)
    c: Horizontal(g46)
    c: Coincident(g47,g11)
    c: Coincident(g47,g21)
    c: Horizontal(g47)
FEATURE [Part::Extrusion] Extrude061
  Base = -> Sketch070
  Dir = (1,0,0)
  DirMode = 2
  FaceMakerClass = Part::FaceMakerBullseye
  LengthFwd = 23
  LengthRev = 0
  Placement = pos=(-19,0,0) rot=(0,0,1;0rad)
  Solid = true
  Symmetric = false
FEATURE [Part::Fillet] Fillet052  label="removeToCreateVentalationHoles002"
  Base = -> Extrude061
  Edges = <same value as first occurrence — deduplicated (x6 in doc)>
  Placement = pos=(7,0.02,0) rot=(0,0,1;0rad)
FEATURE [Part::MultiFuse] Fusion130  label="bottom013"
  Shapes = -> [Cut054,Cut034]
FEATURE [Part::Cut] Cut055
  Base = -> Fusion130
  Tool = -> Fillet052
FEATURE [Part::Cylinder] Cylinder054
  Angle = 360
  AttacherType = Attacher::AttachEngine3D
  Height = 20
  Placement = pos=(0,0,36.15) rot=(0,0,1;0rad)
  Radius = 4
FEATURE [Sketcher::SketchObject] Sketch071  label="bottomSketch002"
  FullyConstrained = true
  sketch-geometry (32):
    g0: LineSegment StartX=3.3 StartY=-6.03275e-07 StartZ=0 EndX=98 EndY=-6.03275e-07 EndZ=0
    g1: ArcOfCircle CenterX=98 CenterY=19 CenterZ=0 NormalX=0 NormalY=0 NormalZ=1 AngleXU=0 Radius=19 StartAngle=4.71239 EndAngle=5.71103
    g2: LineSegment StartX=6.3 StartY=8 StartZ=0 EndX=3.3 EndY=8 EndZ=0
    g3: LineSegment StartX=3.3 StartY=8 StartZ=0 EndX=3.3 EndY=-6.03275e-07 EndZ=0
    g4: ArcOfCircle CenterX=8.3 CenterY=5 CenterZ=0 NormalX=0 NormalY=0 NormalZ=1 AngleXU=0 Radius=2 StartAngle=3.14159 EndAngle=4.71239
    g5: LineSegment StartX=6.3 StartY=8 StartZ=0 EndX=6.3 EndY=5 EndZ=0
    g6: ArcOfCircle CenterX=98 CenterY=19 CenterZ=0 NormalX=0 NormalY=0 NormalZ=1 AngleXU=0 Radius=12.7 StartAngle=4.71239 EndAngle=6.28319
    g7: LineSegment StartX=94.7 StartY=3 StartZ=0 EndX=8.3 EndY=3 EndZ=0
    g8-g12: Circle x5 (B-spline internal-alignment scaffolding for g13; pole/knot coordinates omitted)
    g13: BSplineCurve PolesCount=5 KnotsCount=3 Degree=3 IsPeriodic=0
    g14: GeomPoint X=98 Y=6.3 Z=0
    g15: GeomPoint X=96.3938 Y=4.71946 Z=0
    g16: GeomPoint X=94.7 Y=3 Z=0
    g17-g23: Circle x7 (B-spline internal-alignment scaffolding for g24; pole/knot coordinates omitted)
    g24: BSplineCurve PolesCount=7 KnotsCount=5 Degree=3 IsPeriodic=0
    g25-g29: GeomPoint x5 (B-spline internal-alignment scaffolding for g24; pole/knot coordinates omitted)
    g30: ArcOfCircle CenterX=98 CenterY=19 CenterZ=0 NormalX=0 NormalY=0 NormalZ=1 AngleXU=0 Radius=15.7 StartAngle=5.81226 EndAngle=6.28319
    g31: LineSegment StartX=110.7 StartY=19 StartZ=0 EndX=113.7 EndY=19 EndZ=0
  constraints (41):
    c: Horizontal(g0)
    c: Coincident(g1,g0)
    c: Block(g1)
    c: Horizontal(g2)
    c: Distance(g2) = 3
    c: Coincident(g3,g2)
    c: Vertical(g3)
    c: Coincident(g3,g0)
    c: Block(g4)
    c: Block(g2)
    c: Coincident(g5,g2)
    c: Coincident(g5,g4)
    c: Vertical(g5)
    c: Coincident(g6,g1)
    c: Block(g6)
    c: Coincident(g7,g4)
    c: Horizontal(g7)
    c: Block(g0)
    c: Block(g7)
    c: Block(g3)
    c: Coincident(g13,g6)
    c: Weight(g8) = 1
    c: Equal(g8, g9-g12) x4
    c: Coincident(g13,g7)
    c: InternalAlignment(g8-g12 -> g13) x5
    c: InternalAlignment(g14,g13)
    c: InternalAlignment(g15,g13)
    c: InternalAlignment(g16,g13)
    c: Block(g13)
    c: Weight(g17) = 1
    c: Equal(g17, g18-g23) x6
    c: Coincident(g24,g1)
    c: InternalAlignment(g17-g23 -> g24) x7
    c: InternalAlignment(g25-g29 -> g24) x5
    c: Block(g24)
    c: Coincident(g30,g24)
    c: Coincident(g31,g6)
    c: Coincident(g31,g30)
    c: Horizontal(g31)
    c: Block(g31)
    c: Block(g30)
FEATURE [Part::Extrusion] Extrude062  label="bottom014"
  Base = -> Sketch071
  Dir = (0,0,1)
  DirMode = 2
  FaceMakerClass = Part::FaceMakerBullseye
  LengthFwd = 71.4
  LengthRev = 0
  Placement = pos=(0,0,0.3) rot=(0,0,1;0rad)
  Solid = true
  Symmetric = false
FEATURE [Part::Fillet] Fillet054
  Base = -> Extrude062
  Edges = 1 edges r=2.4: [Edge17]
FEATURE [Part::Fillet] Fillet055  label="bottom015"
  Base = -> Fillet054
  Edges = 1 edges r=2.4: [Edge36]
FEATURE [Part::Cylinder] Cylinder055
  Angle = 360
  AttacherType = Attacher::AttachEngine3D
  Height = 10
  Placement = pos=(0,0,36.15) rot=(0,0,1;0rad)
  Radius = 4
FEATURE [Part::MultiFuse] Fusion131  label="removeToCreateHoleForPlugHousing002"
  Placement = pos=(70,19,36.15) rot=(0,1,0;1.5708rad)
  Shapes = -> [Cylinder054,Cylinder055]
FEATURE [Part::Cut] Cut056  label="Bottom001"
  Base = -> Fillet055
  Placement = pos=(9,0,0) rot=(0,0,1;0rad)
  Tool = -> Fusion131
FEATURE [Part::Cut] Cut057
  Base = -> Cut055
  Tool = -> Cut056
FEATURE [Sketcher::SketchObject] Sketch072  label="topSketch021"
  FullyConstrained = true
  sketch-geometry (4):
    g0: ArcOfCircle CenterX=105 CenterY=19 CenterZ=0 NormalX=0 NormalY=0 NormalZ=1 AngleXU=0 Radius=20.6155 StartAngle=5.54125 EndAngle=6.28319
    g1: ArcOfCircle CenterX=105 CenterY=19 CenterZ=0 NormalX=0 NormalY=0 NormalZ=1 AngleXU=0 Radius=13 StartAngle=5.54125 EndAngle=6.28319
    g2: LineSegment StartX=118 StartY=19 StartZ=0 EndX=125.616 EndY=19 EndZ=0
    g3: LineSegment StartX=114.583 StartY=10.2157 StartZ=0 EndX=120.197 EndY=5.06982 EndZ=0
  constraints (7):
    c: Block(g0)
    c: Block(g1)
    c: Coincident(g2,g1)
    c: Coincident(g2,g0)
    c: Horizontal(g2)
    c: Coincident(g3,g1)
    c: Coincident(g3,g0)
FEATURE [Part::Extrusion] Extrude063  label="bottomPlugHousingBit003"
  Base = -> Sketch072
  Dir = (0,0,1)
  DirMode = 2
  FaceMakerClass = Part::FaceMakerBullseye
  LengthFwd = 72
  LengthRev = 0
  Solid = true
  Symmetric = false
FEATURE [Part::Cylinder] Cylinder056
  Angle = 360
  AttacherType = Attacher::AttachEngine3D
  Height = 20
  Placement = pos=(0,0,36.15) rot=(0,0,1;0rad)
  Radius = 14.3
FEATURE [Part::Cylinder] Cylinder057
  Angle = 360
  AttacherType = Attacher::AttachEngine3D
  Height = 10
  Placement = pos=(0,0,36.15) rot=(0,0,1;0rad)
  Radius = 4
FEATURE [Part::Box] Box034  label="removeToCreteHoleForPlugHousing047"
  AttacherType = Attacher::AttachEngine3D
  Height = 28.6
  Length = 20
  Placement = pos=(106.15,0,21.7) rot=(0,0,1;0rad)
  Width = 19
FEATURE [Part::Cylinder] Cylinder058
  Angle = 360
  AttacherType = Attacher::AttachEngine3D
  Height = 20
  Placement = pos=(0,0,36.15) rot=(0,0,1;0rad)
  Radius = 14.3
FEATURE [Part::Cylinder] Cylinder059
  Angle = 360
  AttacherType = Attacher::AttachEngine3D
  Height = 10
  Placement = pos=(0,0,36.15) rot=(0,0,1;0rad)
  Radius = 4
FEATURE [Part::MultiFuse] Fusion134  label="removeToCreteHoleForPlugHousing046"
  Placement = pos=(70,19,36) rot=(0,1,0;1.5708rad)
  Shapes = -> [Cylinder058,Cylinder059]
FEATURE [Part::Cylinder] Cylinder060
  Angle = 360
  AttacherType = Attacher::AttachEngine3D
  Height = 20
  Placement = pos=(0,0,36.15) rot=(0,0,1;0rad)
  Radius = 14
FEATURE [Part::Cylinder] Cylinder061
  Angle = 360
  AttacherType = Attacher::AttachEngine3D
  Height = 10
  Placement = pos=(0,0,36.15) rot=(0,0,1;0rad)
  Radius = 4
FEATURE [Part::MultiFuse] Fusion135  label="removeToCreteHoleForPlugHousing048"
  Placement = pos=(70,19,36) rot=(0,1,0;1.5708rad)
  Shapes = -> [Cylinder060,Cylinder061]
FEATURE [Part::Box] Box035  label="removeToCreteHoleForPlugHousing049"
  AttacherType = Attacher::AttachEngine3D
  Height = 28.6
  Length = 20
  Placement = pos=(106.15,0,21.7) rot=(0,0,1;0rad)
  Width = 19
FEATURE [Part::MultiFuse] Fusion133  label="removeToCreteHoleForPlugHousing045"
  Placement = pos=(0,0,-28.3) rot=(0,0,1;0rad)
  Shapes = -> [Box035,Fusion134]
FEATURE [Part::MultiFuse] Fusion138  label="removeToCreteHoleForPlugHousing051"
  Placement = pos=(70,19,36) rot=(0,1,0;1.5708rad)
  Shapes = -> [Cylinder056,Cylinder057]
FEATURE [Part::MultiFuse] Fusion137  label="removeToCreteHoleForPlugHousing050"
  Placement = pos=(0,0,28.3) rot=(0,0,1;0rad)
  Shapes = -> [Box034,Fusion138]
FEATURE [Part::MultiFuse] Fusion132  label="removeToCreatePlugHousingBottomBit002"
  Shapes = -> [Fusion133,Fusion137]
FEATURE [Part::MultiFuse] Fusion136  label="removeToCreatePlugHousingBottomBit003"
  Shapes = -> [Fusion135,Fusion132]
FEATURE [Part::Cut] Cut058  label="bottomPlugHousingBit002"
  Base = -> Extrude063
  Placement = pos=(-0.09,0,0) rot=(0,0,1;0rad)
  Tool = -> Fusion136
FEATURE [Sketcher::SketchObject] Sketch073  label="bottomSketch003"
  FullyConstrained = true
  sketch-geometry (45):
    g0: LineSegment StartX=6.29999 StartY=8 StartZ=0 EndX=3.29999 EndY=8 EndZ=0
    g1: LineSegment StartX=3.29999 StartY=8 StartZ=0 EndX=3.29999 EndY=-6.03275e-07 EndZ=0
    g2: ArcOfCircle CenterX=8.29999 CenterY=5 CenterZ=0 NormalX=0 NormalY=0 NormalZ=1 AngleXU=0 Radius=2 StartAngle=3.14159 EndAngle=4.71239
    g3: LineSegment StartX=6.29999 StartY=8 StartZ=0 EndX=6.29999 EndY=5 EndZ=0
    g4: ArcOfCircle CenterX=105 CenterY=19 CenterZ=0 NormalX=0 NormalY=0 NormalZ=1 AngleXU=0 Radius=12.7 StartAngle=4.71239 EndAngle=5.94289
    g5-g11: Circle x7 (B-spline internal-alignment scaffolding for g12; pole/knot coordinates omitted)
    g12: BSplineCurve PolesCount=7 KnotsCount=5 Degree=3 IsPeriodic=0
    g13-g17: GeomPoint x5 (B-spline internal-alignment scaffolding for g12; pole/knot coordinates omitted)
    g18: ArcOfCircle CenterX=105 CenterY=19 CenterZ=0 NormalX=0 NormalY=0 NormalZ=1 AngleXU=0 Radius=15.7 StartAngle=5.81226 EndAngle=6.28319
    g19: BSplineCurve PolesCount=5 KnotsCount=3 Degree=3 IsPeriodic=0
    g20: LineSegment StartX=8.29999 StartY=3 StartZ=0 EndX=101.7 EndY=3 EndZ=0
    g21: LineSegment StartX=3.29999 StartY=-6.03275e-07 StartZ=0 EndX=105 EndY=-6.03275e-07 EndZ=0
    g22: LineSegment StartX=120.974 StartY=8.71251 StartZ=0 EndX=122.332 EndY=7.83778 EndZ=0
    g23: LineSegment StartX=105 StartY=-6.03274e-07 StartZ=0 EndX=113 EndY=-6.03274e-07 EndZ=0
    g24: ArcOfCircle CenterX=105 CenterY=19 CenterZ=0 NormalX=0 NormalY=0 NormalZ=1 AngleXU=0 Radius=20.6155 StartAngle=5.11091 EndAngle=5.71103
    g25: ArcOfCircle CenterX=117.7 CenterY=19 CenterZ=0 NormalX=0 NormalY=0 NormalZ=1 AngleXU=0 Radius=3 StartAngle=1.2e-15 EndAngle=2.10468
    g26: Circle CenterX=116.345 CenterY=16.3232 CenterZ=0 NormalX=0 NormalY=0 NormalZ=1 AngleXU=0 Radius=1
    g27: Circle CenterX=117.24 CenterY=15.7584 CenterZ=0 NormalX=0 NormalY=0 NormalZ=1 AngleXU=0 Radius=1
    g28: Circle CenterX=116.972 CenterY=14.7612 CenterZ=0 NormalX=0 NormalY=0 NormalZ=1 AngleXU=0 Radius=1
    g29: BSplineCurve PolesCount=3 KnotsCount=2 Degree=2 IsPeriodic=0
    g30: GeomPoint X=116.345 Y=16.3232 Z=0
    g31: GeomPoint X=116.972 Y=14.7612 Z=0
    g32: Circle CenterX=115.828 CenterY=17.157 CenterZ=0 NormalX=0 NormalY=0 NormalZ=1 AngleXU=0 Radius=1
    g33: Circle CenterX=115.841 CenterY=16.639 CenterZ=0 NormalX=0 NormalY=0 NormalZ=1 AngleXU=0 Radius=1
    g34: Circle CenterX=116.345 CenterY=16.3232 CenterZ=0 NormalX=0 NormalY=0 NormalZ=1 AngleXU=0 Radius=1
    g35: BSplineCurve PolesCount=3 KnotsCount=2 Degree=2 IsPeriodic=0
    g36: GeomPoint X=115.828 Y=17.157 Z=0
    g37: GeomPoint X=116.345 Y=16.3232 Z=0
    g38: LineSegment StartX=115.828 StartY=17.157 StartZ=0 EndX=115.828 EndY=20.8307 EndZ=0
    g39: Circle CenterX=115.828 CenterY=20.8307 CenterZ=0 NormalX=0 NormalY=0 NormalZ=1 AngleXU=0 Radius=1
    g40: Circle CenterX=115.831 CenterY=21.3396 CenterZ=0 NormalX=0 NormalY=0 NormalZ=1 AngleXU=0 Radius=1
    g41: Circle CenterX=116.173 CenterY=21.5825 CenterZ=0 NormalX=0 NormalY=0 NormalZ=1 AngleXU=0 Radius=1
    g42: BSplineCurve PolesCount=3 KnotsCount=2 Degree=2 IsPeriodic=0
    g43: GeomPoint X=115.828 Y=20.8307 Z=0
    g44: GeomPoint X=116.173 Y=21.5825 Z=0
  constraints (70):
    c: Horizontal(g0)
    c: Distance(g0) = 3
    c: Coincident(g1,g0)
    c: Vertical(g1)
    c: Block(g2)
    c: Block(g0)
    c: Coincident(g3,g0)
    c: Coincident(g3,g2)
    c: Vertical(g3)
    c: Block(g1)
    c: Block(g4)
    c: Coincident(g19,g4)
    c: Block(g19)
    c: Equal(g5, g6-g11) x6
    c: InternalAlignment(g5-g11 -> g12) x7
    c: InternalAlignment(g13-g17 -> g12) x5
    c: Block(g12)
    c: Coincident(g18,g12)
    c: Block(g18)
    c: Coincident(g20,g2)
    c: Coincident(g20,g19)
    c: Horizontal(g20)
    c: Distance(g20) = 93.4
    c: Coincident(g21,g1)
    c: Horizontal(g21)
    c: Distance(g21) = 101.7
    c: Horizontal(g23)
    c: Distance(g23) = 8
    c: Coincident(g24,g23)
    c: Block(g23)
    c: Coincident(g22,g24)
    c: Block(g24)
    c: Block(g22)
    c: Distance(g22) = 1.61553
    c: Coincident(g25,g18)
    c: Block(g25)
    c: Weight(g26) = 1
    c: Equal(g26,g27)
    c: Equal(g26,g28)
    c: Coincident(g29,g4)
    c: InternalAlignment(g26,g29)
    c: InternalAlignment(g27,g29)
    c: InternalAlignment(g28,g29)
    c: InternalAlignment(g30,g29)
    c: InternalAlignment(g31,g29)
    c: Block(g29)
    c: Weight(g32) = 1
    c: Equal(g32,g33)
    c: Equal(g32,g34)
    c: Coincident(g35,g29)
    c: InternalAlignment(g32,g35)
    c: InternalAlignment(g33,g35)
    c: InternalAlignment(g34,g35)
    c: InternalAlignment(g36,g35)
    c: InternalAlignment(g37,g35)
    c: Block(g35)
    c: Coincident(g38,g35)
    c: Vertical(g38)
    c: Block(g38)
    c: Coincident(g42,g38)
    c: Weight(g39) = 1
    c: Equal(g39,g40)
    c: Equal(g39,g41)
    c: Coincident(g42,g25)
    c: InternalAlignment(g39,g42)
    c: InternalAlignment(g40,g42)
    c: InternalAlignment(g41,g42)
    c: InternalAlignment(g43,g42)
    c: InternalAlignment(g44,g42)
    c: Block(g42)
FEATURE [Part::Extrusion] Extrude064  label="bottom016"
  Base = -> Sketch073
  Dir = (0,0,1)
  DirMode = 2
  FaceMakerClass = Part::FaceMakerBullseye
  LengthFwd = 71.4
  LengthRev = 0
  Placement = pos=(0,0,0.3) rot=(0,0,1;0rad)
  Solid = true
  Symmetric = false
FEATURE [Part::Revolution] Revolve157  label="removeToCreateScrewAndThreadedInsertHole063"
  Angle = 360
  Axis = (0,1,0)
  Base = (0,0,0)
  FaceMakerClass = Part::FaceMakerBullseye
  Placement = pos=(12.5,0,10) rot=(0,0,1;0rad)
  Solid = false
  Source = -> Face141
  Symmetric = false
FEATURE [Sketcher::SketchObject] Sketch074
  FullyConstrained = true
  Placement = pos=(117,19,0) rot=(0.57735,0.57735,0.57735;2.0944rad)
  sketch-geometry (48):
    g0: LineSegment StartX=-49.19 StartY=69.25 StartZ=0 EndX=-49.19 EndY=66.25 EndZ=0
    g1: LineSegment StartX=-49.19 StartY=63.5 StartZ=0 EndX=-49.19 EndY=60.5 EndZ=0
    g2: LineSegment StartX=-49.19 StartY=57.75 StartZ=0 EndX=-49.19 EndY=54.75 EndZ=0
    g3: LineSegment StartX=-49.19 StartY=52 StartZ=0 EndX=-49.19 EndY=49 EndZ=0
    g4: LineSegment StartX=-49.19 StartY=46.25 StartZ=0 EndX=-49.19 EndY=43.25 EndZ=0
    g5: LineSegment StartX=-49.19 StartY=40.5 StartZ=0 EndX=-49.19 EndY=37.5 EndZ=0
    g6: LineSegment StartX=-49.19 StartY=34.5 StartZ=0 EndX=-49.19 EndY=31.5 EndZ=0
    g7: LineSegment StartX=-49.19 StartY=28.75 StartZ=0 EndX=-49.19 EndY=25.75 EndZ=0
    g8: LineSegment StartX=-49.19 StartY=23 StartZ=0 EndX=-49.19 EndY=20 EndZ=0
    g9: LineSegment StartX=-49.19 StartY=17.25 StartZ=0 EndX=-49.19 EndY=14.25 EndZ=0
    g10: LineSegment StartX=-49.19 StartY=11.5 StartZ=0 EndX=-49.19 EndY=8.5 EndZ=0
    g11: LineSegment StartX=-49.19 StartY=5.75 StartZ=0 EndX=-49.19 EndY=2.75 EndZ=0
    g12: ArcOfCircle CenterX=-1.5 CenterY=67.75 CenterZ=0 NormalX=0 NormalY=0 NormalZ=1 AngleXU=0 Radius=1.5 StartAngle=4.71239 EndAngle=7.85398
    g13: ArcOfCircle CenterX=-1.5 CenterY=62 CenterZ=0 NormalX=0 NormalY=0 NormalZ=1 AngleXU=0 Radius=1.5 StartAngle=4.71239 EndAngle=7.85398
    g14: ArcOfCircle CenterX=-1.5 CenterY=56.25 CenterZ=0 NormalX=0 NormalY=0 NormalZ=1 AngleXU=0 Radius=1.5 StartAngle=4.71239 EndAngle=7.85398
    g15: ArcOfCircle CenterX=-11.49 CenterY=50.5 CenterZ=0 NormalX=0 NormalY=0 NormalZ=1 AngleXU=0 Radius=1.5 StartAngle=4.71239 EndAngle=7.85398
    g16: ArcOfCircle CenterX=-16.28 CenterY=44.75 CenterZ=0 NormalX=0 NormalY=0 NormalZ=1 AngleXU=0 Radius=1.5 StartAngle=4.71239 EndAngle=7.85398
    g17: ArcOfCircle CenterX=-18.2337 CenterY=39 CenterZ=0 NormalX=0 NormalY=0 NormalZ=1 AngleXU=0 Radius=1.5 StartAngle=4.71485 EndAngle=7.85398
    g18: ArcOfCircle CenterX=-16.2837 CenterY=27.25 CenterZ=0 NormalX=0 NormalY=0 NormalZ=1 AngleXU=0 Radius=1.5 StartAngle=4.71485 EndAngle=7.85398
    g19: ArcOfCircle CenterX=-18.2337 CenterY=33 CenterZ=0 NormalX=0 NormalY=0 NormalZ=1 AngleXU=0 Radius=1.5 StartAngle=4.71485 EndAngle=7.85398
    g20: ArcOfCircle CenterX=-11.49 CenterY=21.5 CenterZ=0 NormalX=0 NormalY=0 NormalZ=1 AngleXU=0 Radius=1.5 StartAngle=4.71239 EndAngle=7.85398
    g21: ArcOfCircle CenterX=-1.5 CenterY=4.25 CenterZ=0 NormalX=0 NormalY=0 NormalZ=1 AngleXU=0 Radius=1.5 StartAngle=4.71239 EndAngle=7.85398
    g22: ArcOfCircle CenterX=-1.5 CenterY=10 CenterZ=0 NormalX=0 NormalY=0 NormalZ=1 AngleXU=0 Radius=1.5 StartAngle=4.71239 EndAngle=7.85398
    g23: ArcOfCircle CenterX=-1.5 CenterY=15.75 CenterZ=0 NormalX=0 NormalY=0 NormalZ=1 AngleXU=0 Radius=1.5 StartAngle=4.71239 EndAngle=7.85398
    g24: LineSegment StartX=-49.19 StartY=69.25 StartZ=0 EndX=-1.5 EndY=69.25 EndZ=0
    g25: LineSegment StartX=-49.19 StartY=66.25 StartZ=0 EndX=-1.5 EndY=66.25 EndZ=0
    g26: LineSegment StartX=-49.19 StartY=63.5 StartZ=0 EndX=-1.5 EndY=63.5 EndZ=0
    g27: LineSegment StartX=-49.19 StartY=60.5 StartZ=0 EndX=-1.5 EndY=60.5 EndZ=0
    g28: LineSegment StartX=-49.19 StartY=57.75 StartZ=0 EndX=-1.5 EndY=57.75 EndZ=0
    g29: LineSegment StartX=-49.19 StartY=54.75 StartZ=0 EndX=-1.5 EndY=54.75 EndZ=0
    g30: LineSegment StartX=-49.19 StartY=52 StartZ=0 EndX=-11.49 EndY=52 EndZ=0
    g31: LineSegment StartX=-49.19 StartY=49 StartZ=0 EndX=-11.49 EndY=49 EndZ=0
    g32: LineSegment StartX=-49.19 StartY=46.25 StartZ=0 EndX=-16.28 EndY=46.25 EndZ=0
    g33: LineSegment StartX=-49.19 StartY=43.25 StartZ=0 EndX=-16.28 EndY=43.25 EndZ=0
    g34: LineSegment StartX=-49.19 StartY=40.5 StartZ=0 EndX=-18.2337 EndY=40.5 EndZ=0
    g35: LineSegment StartX=-49.19 StartY=37.5 StartZ=0 EndX=-18.23 EndY=37.5 EndZ=0
    g36: LineSegment StartX=-49.19 StartY=34.5 StartZ=0 EndX=-18.2337 EndY=34.5 EndZ=0
    g37: LineSegment StartX=-49.19 StartY=31.5 StartZ=0 EndX=-18.23 EndY=31.5 EndZ=0
    g38: LineSegment StartX=-49.19 StartY=28.75 StartZ=0 EndX=-16.2837 EndY=28.75 EndZ=0
    g39: LineSegment StartX=-49.19 StartY=25.75 StartZ=0 EndX=-16.28 EndY=25.75 EndZ=0
    g40: LineSegment StartX=-49.19 StartY=23 StartZ=0 EndX=-11.49 EndY=23 EndZ=0
    g41: LineSegment StartX=-49.19 StartY=20 StartZ=0 EndX=-11.49 EndY=20 EndZ=0
    g42: LineSegment StartX=-49.19 StartY=17.25 StartZ=0 EndX=-1.5 EndY=17.25 EndZ=0
    g43: LineSegment StartX=-49.19 StartY=14.25 StartZ=0 EndX=-1.5 EndY=14.25 EndZ=0
    g44: LineSegment StartX=-49.19 StartY=11.5 StartZ=0 EndX=-1.5 EndY=11.5 EndZ=0
    g45: LineSegment StartX=-49.19 StartY=8.5 StartZ=0 EndX=-1.5 EndY=8.5 EndZ=0
    g46: LineSegment StartX=-49.19 StartY=5.75 StartZ=0 EndX=-1.5 EndY=5.75 EndZ=0
    g47: LineSegment StartX=-49.19 StartY=2.75 StartZ=0 EndX=-1.5 EndY=2.75 EndZ=0
  constraints (120):
    c: Vertical(g0)
    c: Distance(g0) = 3
    c: Block(g0)
    c: Vertical(g1)
    c: Distance(g1) = 3
    c: Vertical(g2)
    c: Equal(g0,g2) = 3
    c: Block(g2)
    c: Vertical(g3)
    c: Equal(g1,g3) = 3
    c: Vertical(g4)
    c: Equal(g0,g4) = 3
    c: Block(g4)
    c: Vertical(g5)
    c: Equal(g1,g5) = 3
    c: Vertical(g6)
    c: Equal(g0,g6) = 3
    c: Block(g6)
    c: Vertical(g7)
    c: Equal(g1,g7) = 3
    c: Vertical(g8)
    c: Equal(g0,g8) = 3
    c: Block(g8)
    c: Vertical(g9)
    c: Equal(g1,g9) = 3
    c: Vertical(g10)
    c: Equal(g0,g10) = 3
    c: Block(g10)
    c: Vertical(g11)
    c: Equal(g1,g11) = 3
    c: Block(g12)
    c: Block(g13)
    c: Block(g14)
    c: Block(g15)
    c: Block(g16)
    c: Block(g17)
    c: Block(g18)
    c: Block(g19)
    c: Block(g20)
    c: Block(g21)
    c: Block(g22)
    c: Block(g23)
    c: Block(g11)
    c: Block(g9)
    c: Block(g7)
    c: Block(g5)
    c: Block(g3)
    c: Block(g1)
    c: Coincident(g24,g0)
    c: Coincident(g24,g12)
    c: Horizontal(g24)
    c: Coincident(g25,g0)
    c: Coincident(g25,g12)
    c: Horizontal(g25)
    c: Coincident(g26,g1)
    c: Coincident(g26,g13)
    c: Horizontal(g26)
    c: Coincident(g27,g1)
    c: Coincident(g27,g13)
    c: Horizontal(g27)
    c: Coincident(g28,g2)
    c: Coincident(g28,g14)
    c: Horizontal(g28)
    c: Coincident(g29,g2)
    c: Coincident(g29,g14)
    c: Horizontal(g29)
    c: Coincident(g30,g3)
    c: Coincident(g30,g15)
    c: Horizontal(g30)
    c: Coincident(g31,g3)
    c: Coincident(g31,g15)
    c: Horizontal(g31)
    c: Coincident(g32,g4)
    c: Coincident(g32,g16)
    c: Horizontal(g32)
    c: Coincident(g33,g4)
    c: Coincident(g33,g16)
    c: Horizontal(g33)
    c: Coincident(g34,g5)
    c: Coincident(g34,g17)
    c: Horizontal(g34)
    c: Coincident(g35,g5)
    c: Coincident(g35,g17)
    c: Horizontal(g35)
    c: Coincident(g36,g6)
    c: Coincident(g36,g19)
    c: Horizontal(g36)
    c: Coincident(g37,g6)
    c: Coincident(g37,g19)
    c: Horizontal(g37)
    c: Coincident(g38,g7)
    c: Coincident(g38,g18)
    c: Horizontal(g38)
    c: Coincident(g39,g7)
    c: Coincident(g39,g18)
    c: Horizontal(g39)
    c: Coincident(g40,g8)
    c: Coincident(g40,g20)
    c: Horizontal(g40)
    c: Coincident(g41,g8)
    c: Coincident(g41,g20)
    c: Horizontal(g41)
    c: Coincident(g42,g9)
    c: Coincident(g42,g23)
    c: Horizontal(g42)
    c: Coincident(g43,g9)
    c: Coincident(g43,g23)
    c: Horizontal(g43)
    c: Coincident(g44,g10)
    c: Coincident(g44,g22)
    c: Horizontal(g44)
    c: Coincident(g45,g10)
    c: Coincident(g45,g22)
    c: Horizontal(g45)
    c: Coincident(g46,g11)
    c: Coincident(g46,g21)
    c: Horizontal(g46)
    c: Coincident(g47,g11)
    c: Coincident(g47,g21)
    c: Horizontal(g47)
FEATURE [Part::Extrusion] Extrude065
  Base = -> Sketch074
  Dir = (1,0,0)
  DirMode = 2
  FaceMakerClass = Part::FaceMakerBullseye
  LengthFwd = 23
  LengthRev = 0
  Placement = pos=(-19,0,0) rot=(0,0,1;0rad)
  Solid = true
  Symmetric = false
FEATURE [Part::Fillet] Fillet056  label="removeToCreateVentalationHoles003"
  Base = -> Extrude065
  Edges = <same value as first occurrence — deduplicated (x6 in doc)>
  Placement = pos=(7,0.02,0) rot=(0,0,1;0rad)
FEATURE [Part::Revolution] Revolve158  label="removeToCreateScrewAndThreadedInsertHole065"
  Angle = 360
  Axis = (0,1,0)
  Base = (0,0,0)
  FaceMakerClass = Part::FaceMakerBullseye
  Placement = pos=(12.5,0,62) rot=(0,0,1;0rad)
  Solid = false
  Source = -> Face146
  Symmetric = false
FEATURE [Part::Revolution] Revolve159  label="removeToCreateScrewAndThreadedInsertHole066"
  Angle = 360
  Axis = (0,1,0)
  Base = (0,0,0)
  FaceMakerClass = Part::FaceMakerBullseye
  Placement = pos=(89.5,0,68.5) rot=(0,0,1;0rad)
  Solid = false
  Source = -> Face143
  Symmetric = false
FEATURE [Part::Revolution] Revolve160  label="removeToCreateScrewAndThreadedInsertHole067"
  Angle = 360
  Axis = (0,1,0)
  Base = (0,0,0)
  FaceMakerClass = Part::FaceMakerBullseye
  Placement = pos=(89.5,0,3.5) rot=(0,0,1;0rad)
  Solid = false
  Source = -> Face142
  Symmetric = false
FEATURE [Part::Revolution] Revolve161  label="removeToCreateScrewAndThreadedInsertHole068"
  Angle = 360
  Axis = (0,1,0)
  Base = (0,0,0)
  FaceMakerClass = Part::FaceMakerBullseye
  Placement = pos=(109.5,4.7,3.5) rot=(0,0,1;0rad)
  Solid = false
  Source = -> Face145
  Symmetric = false
FEATURE [Part::Revolution] Revolve162  label="removeToCreateScrewAndThreadedInsertHole069"
  Angle = 360
  Axis = (0,1,0)
  Base = (0,0,0)
  FaceMakerClass = Part::FaceMakerBullseye
  Placement = pos=(109.5,4.7,68.5) rot=(0,0,1;0rad)
  Solid = false
  Source = -> Face144
  Symmetric = false
FEATURE [Part::MultiFuse] Fusion141  label="removeToCreateScrewAndThreadedInsertHole064"
  Shapes = -> [Revolve162,Revolve161,Revolve160,Revolve159,Revolve158,Revolve157]
FEATURE [Part::Cylinder] Cylinder062
  Angle = 360
  AttacherType = Attacher::AttachEngine3D
  Height = 20
  Placement = pos=(0,0,36.15) rot=(0,0,1;0rad)
  Radius = 14
FEATURE [Part::Cylinder] Cylinder063
  Angle = 360
  AttacherType = Attacher::AttachEngine3D
  Height = 10
  Placement = pos=(0,0,36.15) rot=(0,0,1;0rad)
  Radius = 4
FEATURE [Part::MultiFuse] Fusion139  label="removeToCreteHoleForPlugHousing052"
  Placement = pos=(70,19,36) rot=(0,1,0;1.5708rad)
  Shapes = -> [Cylinder062,Cylinder063]
FEATURE [Part::Cut] Cut060  label="bottom017"
  Base = -> Extrude064
  Tool = -> Fusion139
FEATURE [Part::Cut] Cut061  label="bottom019"
  Base = -> Cut060
  Tool = -> Fusion141
FEATURE [Part::MultiFuse] Fusion140  label="bottom018"
  Shapes = -> [Cut061,Cut058]
FEATURE [Part::Cut] Cut059  label="bottom020"
  Base = -> Fusion140
  Tool = -> Fillet056
FEATURE [Part::Box] Box036  label="Cube021"
  AttacherType = Attacher::AttachEngine3D
  Height = 80
  Length = 26
  Placement = pos=(0,-1,-5) rot=(0,0,1;0rad)
  Width = 11
FEATURE [Part::Cut] Cut062  label="removeFromBottom002"
  Base = -> Cut057
  Tool = -> Box036
FEATURE [Part::Cut] Cut063
  Base = -> Cut059
  Tool = -> Cut062
FEATURE [Part::Cut] Cut064  label="pcbStands"
  Base = -> Fusion095
  Tool = -> Fusion127
FEATURE [Sketcher::SketchObject] Sketch075  label="topSketch022"
  FullyConstrained = true
  sketch-geometry (6):
    g0: LineSegment StartX=19 StartY=38 StartZ=0 EndX=117 EndY=38 EndZ=0
    g1: ArcOfCircle CenterX=19 CenterY=19 CenterZ=0 NormalX=0 NormalY=0 NormalZ=1 AngleXU=0 Radius=19 StartAngle=1.5708 EndAngle=3.14159
    g2: LineSegment StartX=117 StartY=38 StartZ=0 EndX=117 EndY=19 EndZ=0
    g3: LineSegment StartX=98 StartY=1.0161e-12 StartZ=0 EndX=5.22862e-06 EndY=1.0161e-12 EndZ=0
    g4: LineSegment StartX=5.22862e-06 StartY=19 StartZ=0 EndX=5.22862e-06 EndY=1.0161e-12 EndZ=0
    g5: ArcOfCircle CenterX=98 CenterY=19 CenterZ=0 NormalX=0 NormalY=0 NormalZ=1 AngleXU=0 Radius=19 StartAngle=4.71239 EndAngle=6.28319
  constraints (16):
    c: Horizontal(g0)
    c: Distance(g0) = 98
    c: Coincident(g1,g0)
    c: Block(g1)
    c: Coincident(g2,g0)
    c: Vertical(g2)
    c: Distance(g2) = 19
    c: Horizontal(g3)
    c: Coincident(g4,g1)
    c: Vertical(g4)
    c: Coincident(g3,g4)
    c: Block(g3)
    c: Coincident(g5,g2)
    c: Coincident(g5,g3)
    c: Block(g0)
    c: Block(g5)
FEATURE [Part::Extrusion] Extrude067  label="sideB003"
  Base = -> Sketch075
  Dir = (0,0,1)
  DirMode = 2
  FaceMakerClass = Part::FaceMakerBullseye
  LengthFwd = 3
  LengthRev = 0
  Placement = pos=(0,0,71.7) rot=(0,0,1;0rad)
  Solid = true
  Symmetric = false
FEATURE [Sketcher::SketchObject] Sketch076  label="topSketch023"
  FullyConstrained = true
  sketch-geometry (6):
    g0: LineSegment StartX=19 StartY=38 StartZ=0 EndX=117 EndY=38 EndZ=0
    g1: ArcOfCircle CenterX=19 CenterY=19 CenterZ=0 NormalX=0 NormalY=0 NormalZ=1 AngleXU=0 Radius=19 StartAngle=1.5708 EndAngle=3.14159
    g2: LineSegment StartX=117 StartY=38 StartZ=0 EndX=117 EndY=19 EndZ=0
    g3: LineSegment StartX=98 StartY=1.0161e-12 StartZ=0 EndX=5.22862e-06 EndY=1.0161e-12 EndZ=0
    g4: LineSegment StartX=5.22862e-06 StartY=19 StartZ=0 EndX=5.22862e-06 EndY=1.0161e-12 EndZ=0
    g5: ArcOfCircle CenterX=98 CenterY=19 CenterZ=0 NormalX=0 NormalY=0 NormalZ=1 AngleXU=0 Radius=19 StartAngle=4.71239 EndAngle=6.28319
  constraints (16):
    c: Horizontal(g0)
    c: Distance(g0) = 98
    c: Coincident(g1,g0)
    c: Block(g1)
    c: Coincident(g2,g0)
    c: Vertical(g2)
    c: Distance(g2) = 19
    c: Horizontal(g3)
    c: Coincident(g4,g1)
    c: Vertical(g4)
    c: Coincident(g3,g4)
    c: Block(g3)
    c: Coincident(g5,g2)
    c: Coincident(g5,g3)
    c: Block(g0)
    c: Block(g5)
FEATURE [Part::Extrusion] Extrude066  label="sideA003"
  Base = -> Sketch076
  Dir = (0,0,1)
  DirMode = 2
  FaceMakerClass = Part::FaceMakerBullseye
  LengthFwd = 3
  LengthRev = 0
  Placement = pos=(0,0,-2.7) rot=(0,0,1;0rad)
  Solid = true
  Symmetric = false
FEATURE [Part::MultiFuse] Fusion142  label="removeFromBottom003"
  Placement = pos=(2,0,0) rot=(0,0,1;0rad)
  Shapes = -> [Extrude066,Extrude067]
FEATURE [Part::Cut] Cut065  label="screwRetainers002"
  Base = -> Fusion096
  Tool = -> Fusion142
FEATURE [Sketcher::SketchObject] Sketch077
  FullyConstrained = true
  Placement = pos=(117,19,0) rot=(0.57735,0.57735,0.57735;2.0944rad)
  sketch-geometry (8):
    g0: LineSegment StartX=-49.19 StartY=63.5 StartZ=0 EndX=-49.19 EndY=60.5 EndZ=0
    g1: LineSegment StartX=-49.19 StartY=11.5 StartZ=0 EndX=-49.19 EndY=8.5 EndZ=0
    g2: ArcOfCircle CenterX=-1.5 CenterY=62 CenterZ=0 NormalX=0 NormalY=0 NormalZ=1 AngleXU=0 Radius=1.5 StartAngle=4.71239 EndAngle=7.85398
    g3: ArcOfCircle CenterX=-1.5 CenterY=10 CenterZ=0 NormalX=0 NormalY=0 NormalZ=1 AngleXU=0 Radius=1.5 StartAngle=4.71239 EndAngle=7.85398
    g4: LineSegment StartX=-49.19 StartY=63.5 StartZ=0 EndX=-1.5 EndY=63.5 EndZ=0
    g5: LineSegment StartX=-49.19 StartY=60.5 StartZ=0 EndX=-1.5 EndY=60.5 EndZ=0
    g6: LineSegment StartX=-49.19 StartY=11.5 StartZ=0 EndX=-1.5 EndY=11.5 EndZ=0
    g7: LineSegment StartX=-49.19 StartY=8.5 StartZ=0 EndX=-1.5 EndY=8.5 EndZ=0
  constraints (19):
    c: Vertical(g0)
    c: Distance(g0) = 3
    c: Vertical(g1)
    c: Block(g1)
    c: Block(g2)
    c: Block(g3)
    c: Block(g0)
    c: Coincident(g4,g0)
    c: Coincident(g4,g2)
    c: Horizontal(g4)
    c: Coincident(g5,g0)
    c: Coincident(g5,g2)
    c: Horizontal(g5)
    c: Coincident(g6,g1)
    c: Coincident(g6,g3)
    c: Horizontal(g6)
    c: Coincident(g7,g1)
    c: Coincident(g7,g3)
    c: Horizontal(g7)
FEATURE [Part::Extrusion] Extrude068
  Base = -> Sketch077
  Dir = (1,0,0)
  DirMode = 2
  FaceMakerClass = Part::FaceMakerBullseye
  LengthFwd = 10
  LengthRev = 0
  Solid = true
  Symmetric = false
FEATURE [Part::Fillet] Fillet057  label="removeFromtMoreFrontCaseScrewRetainers002"
  Base = -> Extrude068
  Edges = 4 edges r=1.49: [Edge6,Edge11,Edge18,Edge23]
  Placement = pos=(-12,0,0) rot=(0,0,1;0rad)
FEATURE [Sketcher::SketchObject] Sketch078
  FullyConstrained = true
  Placement = pos=(117,19,0) rot=(0.57735,0.57735,0.57735;2.0944rad)
  sketch-geometry (8):
    g0: LineSegment StartX=-49.19 StartY=69.25 StartZ=0 EndX=-49.19 EndY=66.25 EndZ=0
    g1: LineSegment StartX=-49.19 StartY=5.75 StartZ=0 EndX=-49.19 EndY=2.75 EndZ=0
    g2: ArcOfCircle CenterX=-1.5 CenterY=67.75 CenterZ=0 NormalX=0 NormalY=0 NormalZ=1 AngleXU=0 Radius=1.5 StartAngle=4.71239 EndAngle=7.85398
    g3: ArcOfCircle CenterX=-1.5 CenterY=4.25 CenterZ=0 NormalX=0 NormalY=0 NormalZ=1 AngleXU=0 Radius=1.5 StartAngle=4.71239 EndAngle=7.85398
    g4: LineSegment StartX=-49.19 StartY=69.25 StartZ=0 EndX=-1.5 EndY=69.25 EndZ=0
    g5: LineSegment StartX=-49.19 StartY=66.25 StartZ=0 EndX=-1.5 EndY=66.25 EndZ=0
    g6: LineSegment StartX=-49.19 StartY=5.75 StartZ=0 EndX=-1.5 EndY=5.75 EndZ=0
    g7: LineSegment StartX=-49.19 StartY=2.75 StartZ=0 EndX=-1.5 EndY=2.75 EndZ=0
  constraints (19):
    c: Vertical(g0)
    c: Distance(g0) = 3
    c: Block(g0)
    c: Vertical(g1)
    c: Block(g2)
    c: Block(g3)
    c: Block(g1)
    c: Coincident(g4,g0)
    c: Coincident(g4,g2)
    c: Horizontal(g4)
    c: Coincident(g5,g0)
    c: Coincident(g5,g2)
    c: Horizontal(g5)
    c: Coincident(g6,g1)
    c: Coincident(g6,g3)
    c: Horizontal(g6)
    c: Coincident(g7,g1)
    c: Coincident(g7,g3)
    c: Horizontal(g7)
FEATURE [Part::Extrusion] Extrude069
  Base = -> Sketch078
  Dir = (1,0,0)
  DirMode = 2
  FaceMakerClass = Part::FaceMakerBullseye
  LengthFwd = 10
  LengthRev = 0
  Solid = true
  Symmetric = false
FEATURE [Part::Fillet] Fillet058  label="removeFromtMoreFrontCaseScrewRetainers003"
  Base = -> Extrude069
  Edges = 4 edges r=1.49: [Edge6,Edge11,Edge18,Edge23]
  Placement = pos=(-4,0,0) rot=(0,0,1;0rad)
FEATURE [Part::Cut] Cut066
  Base = -> Cut065
  Tool = -> Fillet058
FEATURE [Part::Cut] Cut067  label="screwPillars"
  Base = -> Cut066
  Tool = -> Fillet057
FEATURE [Part::MultiFuse] Fusion143  label="bottom021"
  Shapes = -> [Cut031,Cut063]
FEATURE [Part::Cylinder] Cylinder
  Angle = 360
  AttacherType = Attacher::AttachEngine3D
  Height = 10
  Placement = pos=(20.65,12,4.68) rot=(1,0,0;1.5708rad)
  Radius = 2
FEATURE [Part::Cylinder] Cylinder064
  Angle = 360
  AttacherType = Attacher::AttachEngine3D
  Height = 10
  Placement = pos=(20.65,12,67.38) rot=(1,0,0;1.5708rad)
  Radius = 2
FEATURE [Part::Cylinder] Cylinder065
  Angle = 360
  AttacherType = Attacher::AttachEngine3D
  Height = 10
  Placement = pos=(77.15,12,67.38) rot=(1,0,0;1.5708rad)
  Radius = 2
FEATURE [Part::Cylinder] Cylinder066
  Angle = 360
  AttacherType = Attacher::AttachEngine3D
  Height = 10
  Placement = pos=(77.15,12,4.68) rot=(1,0,0;1.5708rad)
  Radius = 2
FEATURE [Part::MultiFuse] Fusion144  label="removeFromThreadedInsertHousing"
  Shapes = -> [Cylinder065,Cylinder064,Cylinder,Cylinder066]
FEATURE [Part::Cut] Cut068  label="pcbStands001"
  Base = -> Cut064
  Tool = -> Fusion144
FEATURE [Part::MultiFuse] Fusion145
  Shapes = -> [Cut068,Fusion143]
FEATURE [Part::MultiFuse] Fusion146
  Shapes = -> [Fusion145]
FEATURE [Part::MultiFuse] Fusion147  label="bottom022"
  Shapes = -> [Cut067,Fusion146]
FEATURE [Part::MultiFuse] Fusion148  label="casePillars005"
  Shapes = -> [Cut047,Fusion092]
FEATURE [Part::MultiFuse] Fusion149  label="bottom023"
  Shapes = -> [Fusion124,Fusion113,Fusion147]
FEATURE [Part::MultiFuse] Fusion150  label="topBits"
  Shapes = -> [Cut025,Fusion148,Cut030,Fillet034]
FEATURE [Part::Feature] Face149 .. Face152  x4 (patterned run collapsed; names and placements below)
  shape: bbox 3.2 x 1.5 x 2e-07 mm, 1 faces, 0 solids (baked)
FEATURE [Part::Feature] Face153
  shape: bbox 3.6 x 3.2 x 2e-07 mm, 1 faces, 0 solids (baked)
FEATURE [Part::Feature] Face154
  shape: bbox 3.6 x 3.2 x 2e-07 mm, 1 faces, 0 solids (baked)
FEATURE [Sketcher::SketchObject] Sketch079  label="topSketch024"
  FullyConstrained = true
  sketch-geometry (6):
    g0: LineSegment StartX=19 StartY=38 StartZ=0 EndX=117 EndY=38 EndZ=0
    g1: ArcOfCircle CenterX=19 CenterY=19 CenterZ=0 NormalX=0 NormalY=0 NormalZ=1 AngleXU=0 Radius=19 StartAngle=1.5708 EndAngle=3.14159
    g2: LineSegment StartX=117 StartY=38 StartZ=0 EndX=117 EndY=19 EndZ=0
    g3: LineSegment StartX=98 StartY=1.0161e-12 StartZ=0 EndX=5.22862e-06 EndY=1.0161e-12 EndZ=0
    g4: LineSegment StartX=5.22862e-06 StartY=19 StartZ=0 EndX=5.22862e-06 EndY=1.0161e-12 EndZ=0
    g5: ArcOfCircle CenterX=98 CenterY=19 CenterZ=0 NormalX=0 NormalY=0 NormalZ=1 AngleXU=0 Radius=19 StartAngle=4.71239 EndAngle=6.28319
  constraints (16):
    c: Horizontal(g0)
    c: Distance(g0) = 98
    c: Coincident(g1,g0)
    c: Block(g1)
    c: Coincident(g2,g0)
    c: Vertical(g2)
    c: Distance(g2) = 19
    c: Horizontal(g3)
    c: Coincident(g4,g1)
    c: Vertical(g4)
    c: Coincident(g3,g4)
    c: Block(g3)
    c: Coincident(g5,g2)
    c: Coincident(g5,g3)
    c: Block(g0)
    c: Block(g5)
FEATURE [Sketcher::SketchObject] Sketch080  label="topSketch025"
  FullyConstrained = true
  sketch-geometry (6):
    g0: LineSegment StartX=19 StartY=38 StartZ=0 EndX=117 EndY=38 EndZ=0
    g1: ArcOfCircle CenterX=19 CenterY=19 CenterZ=0 NormalX=0 NormalY=0 NormalZ=1 AngleXU=0 Radius=19 StartAngle=1.5708 EndAngle=3.14159
    g2: LineSegment StartX=117 StartY=38 StartZ=0 EndX=117 EndY=19 EndZ=0
    g3: LineSegment StartX=98 StartY=1.0161e-12 StartZ=0 EndX=5.22862e-06 EndY=1.0161e-12 EndZ=0
    g4: LineSegment StartX=5.22862e-06 StartY=19 StartZ=0 EndX=5.22862e-06 EndY=1.0161e-12 EndZ=0
    g5: ArcOfCircle CenterX=98 CenterY=19 CenterZ=0 NormalX=0 NormalY=0 NormalZ=1 AngleXU=0 Radius=19 StartAngle=4.71239 EndAngle=6.28319
  constraints (16):
    c: Horizontal(g0)
    c: Distance(g0) = 98
    c: Coincident(g1,g0)
    c: Block(g1)
    c: Coincident(g2,g0)
    c: Vertical(g2)
    c: Distance(g2) = 19
    c: Horizontal(g3)
    c: Coincident(g4,g1)
    c: Vertical(g4)
    c: Coincident(g3,g4)
    c: Block(g3)
    c: Coincident(g5,g2)
    c: Coincident(g5,g3)
    c: Block(g0)
    c: Block(g5)
FEATURE [Part::Extrusion] Extrude070  label="sideA004"
  Base = -> Sketch080
  Dir = (0,0,1)
  DirMode = 2
  FaceMakerClass = Part::FaceMakerBullseye
  LengthFwd = 3
  LengthRev = 0
  Placement = pos=(0,0,-2.7) rot=(0,0,1;0rad)
  Solid = true
  Symmetric = false
FEATURE [Sketcher::SketchObject] Sketch081
  FullyConstrained = true
  Placement = pos=(117,19,0) rot=(0.57735,0.57735,0.57735;2.0944rad)
  sketch-geometry (8):
    g0: LineSegment StartX=-49.19 StartY=63.5 StartZ=0 EndX=-49.19 EndY=60.5 EndZ=0
    g1: LineSegment StartX=-49.19 StartY=11.5 StartZ=0 EndX=-49.19 EndY=8.5 EndZ=0
    g2: ArcOfCircle CenterX=-1.5 CenterY=62 CenterZ=0 NormalX=0 NormalY=0 NormalZ=1 AngleXU=0 Radius=1.5 StartAngle=4.71239 EndAngle=7.85398
    g3: ArcOfCircle CenterX=-1.5 CenterY=10 CenterZ=0 NormalX=0 NormalY=0 NormalZ=1 AngleXU=0 Radius=1.5 StartAngle=4.71239 EndAngle=7.85398
    g4: LineSegment StartX=-49.19 StartY=63.5 StartZ=0 EndX=-1.5 EndY=63.5 EndZ=0
    g5: LineSegment StartX=-49.19 StartY=60.5 StartZ=0 EndX=-1.5 EndY=60.5 EndZ=0
    g6: LineSegment StartX=-49.19 StartY=11.5 StartZ=0 EndX=-1.5 EndY=11.5 EndZ=0
    g7: LineSegment StartX=-49.19 StartY=8.5 StartZ=0 EndX=-1.5 EndY=8.5 EndZ=0
  constraints (19):
    c: Vertical(g0)
    c: Distance(g0) = 3
    c: Vertical(g1)
    c: Block(g1)
    c: Block(g2)
    c: Block(g3)
    c: Block(g0)
    c: Coincident(g4,g0)
    c: Coincident(g4,g2)
    c: Horizontal(g4)
    c: Coincident(g5,g0)
    c: Coincident(g5,g2)
    c: Horizontal(g5)
    c: Coincident(g6,g1)
    c: Coincident(g6,g3)
    c: Horizontal(g6)
    c: Coincident(g7,g1)
    c: Coincident(g7,g3)
    c: Horizontal(g7)
FEATURE [Part::Extrusion] Extrude071  label="sideB004"
  Base = -> Sketch079
  Dir = (0,0,1)
  DirMode = 2
  FaceMakerClass = Part::FaceMakerBullseye
  LengthFwd = 3
  LengthRev = 0
  Placement = pos=(0,0,71.7) rot=(0,0,1;0rad)
  Solid = true
  Symmetric = false
FEATURE [Part::MultiFuse] Fusion152  label="removeFromBottom004"
  Placement = pos=(2,0,0) rot=(0,0,1;0rad)
  Shapes = -> [Extrude070,Extrude071]
FEATURE [Part::Extrusion] Extrude072
  Base = -> Sketch081
  Dir = (1,0,0)
  DirMode = 2
  FaceMakerClass = Part::FaceMakerBullseye
  LengthFwd = 10
  LengthRev = 0
  Solid = true
  Symmetric = false
FEATURE [Part::Fillet] Fillet059  label="removeFromtMoreFrontCaseScrewRetainers004"
  Base = -> Extrude072
  Edges = 4 edges r=1.49: [Edge6,Edge11,Edge18,Edge23]
  Placement = pos=(-12,0,0) rot=(0,0,1;0rad)
FEATURE [Sketcher::SketchObject] Sketch082
  FullyConstrained = true
  Placement = pos=(117,19,0) rot=(0.57735,0.57735,0.57735;2.0944rad)
  sketch-geometry (8):
    g0: LineSegment StartX=-49.19 StartY=69.25 StartZ=0 EndX=-49.19 EndY=66.25 EndZ=0
    g1: LineSegment StartX=-49.19 StartY=5.75 StartZ=0 EndX=-49.19 EndY=2.75 EndZ=0
    g2: ArcOfCircle CenterX=-1.5 CenterY=67.75 CenterZ=0 NormalX=0 NormalY=0 NormalZ=1 AngleXU=0 Radius=1.5 StartAngle=4.71239 EndAngle=7.85398
    g3: ArcOfCircle CenterX=-1.5 CenterY=4.25 CenterZ=0 NormalX=0 NormalY=0 NormalZ=1 AngleXU=0 Radius=1.5 StartAngle=4.71239 EndAngle=7.85398
    g4: LineSegment StartX=-49.19 StartY=69.25 StartZ=0 EndX=-1.5 EndY=69.25 EndZ=0
    g5: LineSegment StartX=-49.19 StartY=66.25 StartZ=0 EndX=-1.5 EndY=66.25 EndZ=0
    g6: LineSegment StartX=-49.19 StartY=5.75 StartZ=0 EndX=-1.5 EndY=5.75 EndZ=0
    g7: LineSegment StartX=-49.19 StartY=2.75 StartZ=0 EndX=-1.5 EndY=2.75 EndZ=0
  constraints (19):
    c: Vertical(g0)
    c: Distance(g0) = 3
    c: Block(g0)
    c: Vertical(g1)
    c: Block(g2)
    c: Block(g3)
    c: Block(g1)
    c: Coincident(g4,g0)
    c: Coincident(g4,g2)
    c: Horizontal(g4)
    c: Coincident(g5,g0)
    c: Coincident(g5,g2)
    c: Horizontal(g5)
    c: Coincident(g6,g1)
    c: Coincident(g6,g3)
    c: Horizontal(g6)
    c: Coincident(g7,g1)
    c: Coincident(g7,g3)
    c: Horizontal(g7)
FEATURE [Part::Extrusion] Extrude073
  Base = -> Sketch082
  Dir = (1,0,0)
  DirMode = 2
  FaceMakerClass = Part::FaceMakerBullseye
  LengthFwd = 10
  LengthRev = 0
  Solid = true
  Symmetric = false
FEATURE [Part::Fillet] Fillet060  label="removeFromtMoreFrontCaseScrewRetainers005"
  Base = -> Extrude073
  Edges = 4 edges r=1.49: [Edge6,Edge11,Edge18,Edge23]
  Placement = pos=(-4,0,0) rot=(0,0,1;0rad)
FEATURE [Part::Revolution] Revolve163  label="backCaseScrewRetainer004"
  Angle = 360
  Axis = (0,1,0)
  Base = (0,0,0)
  FaceMakerClass = Part::FaceMakerBullseye
  Placement = pos=(12.5,3,62) rot=(0,0,1;0rad)
  Solid = false
  Source = -> Face149
  Symmetric = false
FEATURE [Part::Revolution] Revolve164  label="frontCaseScrewRetainer006"
  Angle = 360
  Axis = (0,1,0)
  Base = (0,0,0)
  FaceMakerClass = Part::FaceMakerBullseye
  Placement = pos=(89.5,3,68.5) rot=(0,0,1;0rad)
  Solid = false
  Source = -> Face151
  Symmetric = false
FEATURE [Part::Revolution] Revolve165  label="frontCaseScrewRetainer007"
  Angle = 360
  Axis = (0,1,0)
  Base = (0,0,0)
  FaceMakerClass = Part::FaceMakerBullseye
  Placement = pos=(89.5,3,3.5) rot=(0,0,1;0rad)
  Solid = false
  Source = -> Face152
  Symmetric = false
FEATURE [Part::Revolution] Revolve166  label="backCaseScrewRetainer005"
  Angle = 360
  Axis = (0,1,0)
  Base = (0,0,0)
  FaceMakerClass = Part::FaceMakerBullseye
  Placement = pos=(12.5,3,10) rot=(0,0,1;0rad)
  Solid = false
  Source = -> Face150
  Symmetric = false
FEATURE [Part::Revolution] Revolve167  label="moreFrontCaseScrewRetainer006"
  Angle = 360
  Axis = (0,1,0)
  Base = (0,0,0)
  FaceMakerClass = Part::FaceMakerBullseye
  Placement = pos=(109.5,4.5,68.5) rot=(0,0,1;0rad)
  Solid = false
  Source = -> Face153
  Symmetric = false
FEATURE [Part::Revolution] Revolve168  label="moreFrontCaseScrewRetainer007"
  Angle = 360
  Axis = (0,1,0)
  Base = (0,0,0)
  FaceMakerClass = Part::FaceMakerBullseye
  Placement = pos=(109.5,4.5,3.5) rot=(0,0,1;0rad)
  Solid = false
  Source = -> Face154
  Symmetric = false
FEATURE [Part::MultiFuse] Fusion151  label="screwRetainers003"
  Shapes = -> [Revolve168,Revolve167,Revolve166,Revolve165,Revolve164,Revolve163]
FEATURE [Part::Cut] Cut069  label="screwRetainers004"
  Base = -> Fusion151
  Tool = -> Fusion152
FEATURE [Part::Cut] Cut070
  Base = -> Cut069
  Tool = -> Fillet060
FEATURE [Part::Cut] Cut071  label="screwPillars001"
  Base = -> Cut070
  Tool = -> Fillet059
FEATURE [Part::MultiFuse] Fusion153  label="bottom024"
  Shapes = -> [Fusion149,Cut071]
FEATURE [Part::Cylinder] Cylinder067
  Angle = 360
  AttacherType = Attacher::AttachEngine3D
  Height = 10
  Placement = pos=(20.65,12,4.68) rot=(1,0,0;1.5708rad)
  Radius = 2
FEATURE [Part::Cylinder] Cylinder068
  Angle = 360
  AttacherType = Attacher::AttachEngine3D
  Height = 10
  Placement = pos=(20.65,12,67.38) rot=(1,0,0;1.5708rad)
  Radius = 2
FEATURE [Part::Cylinder] Cylinder069
  Angle = 360
  AttacherType = Attacher::AttachEngine3D
  Height = 10
  Placement = pos=(77.15,12,67.38) rot=(1,0,0;1.5708rad)
  Radius = 2
FEATURE [Part::Cylinder] Cylinder070
  Angle = 360
  AttacherType = Attacher::AttachEngine3D
  Height = 10
  Placement = pos=(77.15,12,4.68) rot=(1,0,0;1.5708rad)
  Radius = 2
FEATURE [Part::MultiFuse] Fusion154  label="removeFromThreadedInsertHousing001"
  Shapes = -> [Cylinder069,Cylinder068,Cylinder067,Cylinder070]
FEATURE [Part::Cut] Cut072  label="bottom025"
  Base = -> Fusion153
  Tool = -> Fusion154
FEATURE [Image::ImagePlane] ImagePlane
  XSize = 339
  YSize = 72
FEATURE [Sketcher::SketchObject] Sketch083
  FullyConstrained = true
  MapMode = 5
  Support = -> [XY_Plane]
  sketch-geometry (200):
    g0: LineSegment StartX=-151.619 StartY=28.8932 StartZ=0 EndX=-140.819 EndY=28.8932 EndZ=0
    g1: LineSegment StartX=-151.619 StartY=24.0313 StartZ=0 EndX=-151.619 EndY=28.8932 EndZ=0
    g2: LineSegment StartX=-140.819 StartY=17.7713 StartZ=0 EndX=-151.619 EndY=17.7713 EndZ=0
    g3: LineSegment StartX=-151.619 StartY=17.7713 StartZ=0 EndX=-151.619 EndY=22.6313 EndZ=0
    g4: LineSegment StartX=-151.619 StartY=22.6313 StartZ=0 EndX=-145.128 EndY=22.6313 EndZ=0
    g5: LineSegment StartX=-145.128 StartY=24.0313 StartZ=0 EndX=-140.819 EndY=28.8932 EndZ=0
    g6: LineSegment StartX=-145.128 StartY=22.6313 StartZ=0 EndX=-140.819 EndY=17.7713 EndZ=0
    g7: ArcOfCircle CenterX=-155.157 CenterY=23.3323 CenterZ=0 NormalX=0 NormalY=0 NormalZ=1 AngleXU=0 Radius=6.92354 StartAngle=1.03434 EndAngle=5.24885
    g8: ArcOfCircle CenterX=-155.157 CenterY=23.3323 CenterZ=0 NormalX=0 NormalY=0 NormalZ=1 AngleXU=0 Radius=12.6269 StartAngle=1.28675 EndAngle=4.99643
    g9: LineSegment StartX=-151.619 StartY=35.4532 StartZ=0 EndX=-151.619 EndY=29.2832 EndZ=0
    g10: LineSegment StartX=-151.619 StartY=17.3813 StartZ=0 EndX=-151.619 EndY=11.2113 EndZ=0
    g11-g21: Circle x11 (B-spline internal-alignment scaffolding for g22; pole/knot coordinates omitted)
    g22: BSplineCurve PolesCount=11 KnotsCount=9 Degree=3 IsPeriodic=0
    g23-g31: GeomPoint x9 (B-spline internal-alignment scaffolding for g22; pole/knot coordinates omitted)
    g32-g49: Circle x18 (B-spline internal-alignment scaffolding for g50; pole/knot coordinates omitted)
    g50: BSplineCurve PolesCount=18 KnotsCount=16 Degree=3 IsPeriodic=0
    g51-g66: GeomPoint x16 (B-spline internal-alignment scaffolding for g50; pole/knot coordinates omitted)
    g67: LineSegment StartX=-117.124 StartY=30.093 StartZ=0 EndX=-117.603 EndY=26.5272 EndZ=0
    g68: LineSegment StartX=-117.603 StartY=17.8472 StartZ=0 EndX=-117.124 EndY=14.2659 EndZ=0
    g69: Ellipse CenterX=-109.671 CenterY=20.025 CenterZ=0 NormalX=0 NormalY=0 NormalZ=1 MajorRadius=3.34798 MinorRadius=2.71052 AngleXU=-1.56793
    g70: GeomPoint X=-109.666 Y=18.0598 Z=0
    g71: GeomPoint X=-109.677 Y=21.9902 Z=0
    g72: Ellipse CenterX=-109.671 CenterY=20.0123 CenterZ=0 NormalX=0 NormalY=0 NormalZ=1 MajorRadius=6.93002 MinorRadius=6.36273 AngleXU=-3.13976
    g73: GeomPoint X=-112.417 Y=20.0073 Z=0
    g74: GeomPoint X=-106.925 Y=20.0173 Z=0
    g75: Ellipse CenterX=-51.7682 CenterY=20.1463 CenterZ=0 NormalX=0 NormalY=0 NormalZ=1 MajorRadius=3.19279 MinorRadius=2.71052 AngleXU=-1.52774
    g76: GeomPoint X=-51.6955 Y=18.4606 Z=0
    g77: GeomPoint X=-51.8408 Y=21.832 Z=0
    g78: GeomPoint X=-54.5142 Y=20.1413 Z=0
    g79: GeomPoint X=-49.0221 Y=20.1513 Z=0
    g80: Ellipse CenterX=-51.7682 CenterY=20.1463 CenterZ=0 NormalX=0 NormalY=0 NormalZ=1 MajorRadius=6.93002 MinorRadius=6.36273 AngleXU=-3.13976
    g81: Ellipse CenterX=-22.8436 CenterY=20.1783 CenterZ=0 NormalX=0 NormalY=0 NormalZ=1 MajorRadius=3.31512 MinorRadius=2.71052 AngleXU=-1.60214
    g82: GeomPoint X=-22.9034 Y=18.2706 Z=0
    g83: GeomPoint X=-22.7838 Y=22.0861 Z=0
    g84: GeomPoint X=-25.5897 Y=20.1733 Z=0
    g85: GeomPoint X=-20.0976 Y=20.1833 Z=0
    g86: Ellipse CenterX=-22.8436 CenterY=20.1783 CenterZ=0 NormalX=0 NormalY=0 NormalZ=1 MajorRadius=6.93002 MinorRadius=6.36273 AngleXU=-3.13976
    g87: LineSegment StartX=-101.889 StartY=14.1107 StartZ=0 EndX=-97.7455 EndY=14.1107 EndZ=0
    g88: LineSegment StartX=-93.8155 StartY=14.1107 StartZ=0 EndX=-89.6755 EndY=14.1107 EndZ=0
    g89: LineSegment StartX=-85.7455 StartY=14.1107 StartZ=0 EndX=-81.6055 EndY=14.1107 EndZ=0
    g90: LineSegment StartX=-101.889 StartY=14.1107 StartZ=0 EndX=-101.889 EndY=25.9907 EndZ=0
    g91: LineSegment StartX=-101.889 StartY=25.9907 StartZ=0 EndX=-97.8594 EndY=25.9907 EndZ=0
    g92: LineSegment StartX=-97.8594 StartY=25.9907 StartZ=0 EndX=-97.8594 EndY=24.0907 EndZ=0
    g93: LineSegment StartX=-97.7455 StartY=14.1107 StartZ=0 EndX=-97.7455 EndY=19.9107 EndZ=0
    g94: LineSegment StartX=-89.6755 StartY=14.1107 StartZ=0 EndX=-89.6755 EndY=19.9107 EndZ=0
    g95: LineSegment StartX=-93.8155 StartY=14.1107 StartZ=0 EndX=-93.8155 EndY=21.0107 EndZ=0
    g96-g106: Circle x11 (B-spline internal-alignment scaffolding for g107; pole/knot coordinates omitted)
    g107: BSplineCurve PolesCount=11 KnotsCount=9 Degree=3 IsPeriodic=0
    g108-g116: GeomPoint x9 (B-spline internal-alignment scaffolding for g107; pole/knot coordinates omitted)
    g117: BSplineCurve PolesCount=11 KnotsCount=9 Degree=3 IsPeriodic=0
    g118-g125: Circle x8 (B-spline internal-alignment scaffolding for g126; pole/knot coordinates omitted)
    g126: BSplineCurve PolesCount=8 KnotsCount=6 Degree=3 IsPeriodic=0
    g127-g132: GeomPoint x6 (B-spline internal-alignment scaffolding for g126; pole/knot coordinates omitted)
    g133: BSplineCurve PolesCount=8 KnotsCount=6 Degree=3 IsPeriodic=0
    g134: LineSegment StartX=-85.7455 StartY=21.0107 StartZ=0 EndX=-85.7455 EndY=14.1107 EndZ=0
    g135: LineSegment StartX=-80.0879 StartY=14.1107 StartZ=0 EndX=-75.944 EndY=14.1107 EndZ=0
    g136: LineSegment StartX=-72.014 StartY=14.1107 StartZ=0 EndX=-67.874 EndY=14.1107 EndZ=0
    g137: LineSegment StartX=-63.944 StartY=14.1107 StartZ=0 EndX=-59.804 EndY=14.1107 EndZ=0
    g138: LineSegment StartX=-80.0879 StartY=14.1107 StartZ=0 EndX=-80.0879 EndY=25.9907 EndZ=0
    g139: LineSegment StartX=-80.0879 StartY=25.9907 StartZ=0 EndX=-76.0579 EndY=25.9907 EndZ=0
    g140: LineSegment StartX=-76.0579 StartY=25.9907 StartZ=0 EndX=-76.0579 EndY=24.0907 EndZ=0
    g141: LineSegment StartX=-75.944 StartY=14.1107 StartZ=0 EndX=-75.944 EndY=19.9107 EndZ=0
    g142: LineSegment StartX=-67.874 StartY=14.1107 StartZ=0 EndX=-67.874 EndY=19.9107 EndZ=0
    g143: LineSegment StartX=-72.014 StartY=14.1107 StartZ=0 EndX=-72.014 EndY=21.0107 EndZ=0
    g144-g148: Circle x5 (B-spline internal-alignment scaffolding for g149; pole/knot coordinates omitted)
    g149: BSplineCurve PolesCount=11 KnotsCount=9 Degree=3 IsPeriodic=0
    g150-g158: GeomPoint x9 (B-spline internal-alignment scaffolding for g149; pole/knot coordinates omitted)
    g159: BSplineCurve PolesCount=11 KnotsCount=9 Degree=3 IsPeriodic=0
    g160-g167: Circle x8 (B-spline internal-alignment scaffolding for g168; pole/knot coordinates omitted)
    g168: BSplineCurve PolesCount=8 KnotsCount=6 Degree=3 IsPeriodic=0
    g169-g174: GeomPoint x6 (B-spline internal-alignment scaffolding for g168; pole/knot coordinates omitted)
    g175: BSplineCurve PolesCount=8 KnotsCount=6 Degree=3 IsPeriodic=0
    g176: LineSegment StartX=-63.944 StartY=21.0107 StartZ=0 EndX=-63.944 EndY=14.1107 EndZ=0
    g177: LineSegment StartX=-59.804 StartY=14.1107 StartZ=0 EndX=-59.804 EndY=21.5868 EndZ=0
    g178: BSplineCurve PolesCount=4 KnotsCount=2 Degree=3 IsPeriodic=0
    g179: GeomPoint X=-59.804 Y=21.5868 Z=0
    g180: GeomPoint X=-60.2379 Y=24.0907 Z=0
    g181: LineSegment StartX=-81.6055 StartY=14.1107 StartZ=0 EndX=-81.6055 EndY=21.5868 EndZ=0
    g182: LineSegment StartX=-151.619 StartY=24.0313 StartZ=0 EndX=-145.128 EndY=24.0313 EndZ=0
    g183: Circle CenterX=-82.0394 CenterY=24.0907 CenterZ=0 NormalX=0 NormalY=0 NormalZ=1 AngleXU=0 Radius=1
    g184: Circle CenterX=-81.7131 CenterY=23.2736 CenterZ=0 NormalX=0 NormalY=0 NormalZ=1 AngleXU=0 Radius=1
    g185: Circle CenterX=-81.6055 CenterY=21.5868 CenterZ=0 NormalX=0 NormalY=0 NormalZ=1 AngleXU=0 Radius=1
    g186: BSplineCurve PolesCount=3 KnotsCount=2 Degree=2 IsPeriodic=0
    g187: GeomPoint X=-82.0394 Y=24.0907 Z=0
    g188: GeomPoint X=-81.6055 Y=21.5868 Z=0
    g189: Ellipse CenterX=-37.3522 CenterY=19.9515 CenterZ=0 NormalX=0 NormalY=0 NormalZ=1 MajorRadius=2.99755 MinorRadius=2.49 AngleXU=1.5708
    g190: GeomPoint X=-37.3522 Y=21.6203 Z=0
    g191: GeomPoint X=-37.3522 Y=18.2826 Z=0
    g192: ArcOfEllipse CenterX=-38.7647 CenterY=20.06 CenterZ=0 NormalX=0 NormalY=0 NormalZ=1 MajorRadius=6.30025 MinorRadius=5.3849 AngleXU=1.57276 StartAngle=5.50632 EndAngle=10.3035
    g193: GeomPoint X=-38.7711 Y=23.3304 Z=0
    g194: GeomPoint X=-38.7583 Y=16.7895 Z=0
    g195: LineSegment StartX=-34.6109 StartY=14.0378 StartZ=0 EndX=-30.8984 EndY=14.0378 EndZ=0
    g196: LineSegment StartX=-30.8984 StartY=14.0378 StartZ=0 EndX=-30.8984 EndY=31.1784 EndZ=0
    g197: LineSegment StartX=-30.8984 StartY=31.1784 StartZ=0 EndX=-34.9984 EndY=31.1784 EndZ=0
    g198: LineSegment StartX=-34.9984 StartY=24.5602 StartZ=0 EndX=-34.9984 EndY=31.1784 EndZ=0
    g199: LineSegment StartX=-34.6109 StartY=16.0476 StartZ=0 EndX=-34.6109 EndY=14.0378 EndZ=0
  constraints (195):
    c: Coincident(g1,g0)
    c: Horizontal(g0)
    c: Vertical(g1)
    c: Coincident(g2,g3)
    c: Coincident(g3,g4)
    c: Horizontal(g4)
    c: Horizontal(g2)
    c: Vertical(g3)
    c: Block(g1)
    c: Distance(g3) = 4.86
    c: Block(g4)
    c: Distance(g0) = 10.8
    c: Distance(g2) = 10.8
    c: Coincident(g5,g0)
    c: Coincident(g6,g4)
    c: Coincident(g6,g2)
    c: Block(g8)
    c: Block(g7)
    c: Coincident(g9,g8)
    c: Coincident(g9,g7)
    c: Vertical(g9)
    c: Coincident(g10,g7)
    c: Coincident(g10,g8)
    c: Vertical(g10)
    c: Weight(g11) = 1
    c: Equal(g11, g12-g21) x10
    c: InternalAlignment(g11-g21 -> g22) x11
    c: InternalAlignment(g23-g31 -> g22) x9
    c: Block(g22)
    c: Weight(g32) = 1
    c: Equal(g32, g33-g49) x17
    c: InternalAlignment(g32-g49 -> g50) x18
    c: InternalAlignment(g51-g66 -> g50) x16
    c: Block(g50)
    c: Coincident(g67,g50)
    c: Coincident(g67,g22)
    c: Coincident(g68,g22)
    c: Coincident(g68,g50)
    c: InternalAlignment(g70,g69)
    c: InternalAlignment(g71,g69)
    c: Block(g69)
    c: InternalAlignment(g73,g72)
    c: InternalAlignment(g74,g72)
    c: Block(g72)
    c: InternalAlignment(g76,g75)
    c: InternalAlignment(g77,g75)
    c: InternalAlignment(g78,g80)
    c: InternalAlignment(g79,g80)
    c: Block(g80)
    c: Coincident(g75,g80)
    c: Block(g75)
    c: InternalAlignment(g82,g81)
    c: InternalAlignment(g83,g81)
    c: InternalAlignment(g84,g86)
    c: InternalAlignment(g85,g86)
    c: Block(g86)
    c: Coincident(g81,g86)
    c: Block(g81)
    c: Horizontal(g87)
    c: Block(g87)
    c: Horizontal(g88)
    c: Distance(g88) = 4.14
    c: Horizontal(g89)
    c: Equal(g88,g89) = 4.14
    c: Block(g89)
    c: Block(g88)
    c: Coincident(g90,g87)
    c: Vertical(g90)
    c: Distance(g90) = 11.88
    c: Coincident(g91,g90)
    c: Horizontal(g91)
    c: Coincident(g92,g91)
    c: Vertical(g92)
    c: Distance(g91) = 4.03
    c: Distance(g92) = 1.9
    c: Coincident(g93,g87)
    c: Vertical(g93)
    c: Vertical(g94)
    c: Coincident(g94,g88)
    c: Distance(g93) = 5.8
    c: Distance(g94) = 5.8
    c: Vertical(g95)
    c: Coincident(g95,g88)
    c: Distance(g95) = 6.9
    c: Coincident(g107,g92)
    c: Weight(g96) = 1
    c: Equal(g96, g97-g106) x10
    c: InternalAlignment(g96-g106 -> g107) x11
    c: InternalAlignment(g108-g116 -> g107) x9
    c: Block(g107)
    c: Block(g117)
    c: Coincident(g126,g93)
    c: Weight(g118) = 1
    c: Equal(g118, g119-g125) x7
    c: Coincident(g126,g95)
    c: InternalAlignment(g118-g125 -> g126) x8
    c: InternalAlignment(g127-g132 -> g126) x6
    c: Coincident(g133,g94)
    c: Block(g126)
    c: Block(g133)
    c: Coincident(g134,g133)
    c: Coincident(g134,g89)
    c: Vertical(g134)
    c: Horizontal(g135)
    c: Block(g135)
    c: Horizontal(g136)
    c: Equal(g88,g136) = 4.14
    c: Horizontal(g137)
    c: Equal(g136,g137) = 4.14
    c: Block(g137)
    c: Block(g136)
    c: Coincident(g138,g135)
    c: Vertical(g138)
    c: Equal(g90,g138) = 11.88
    c: Coincident(g139,g138)
    c: Horizontal(g139)
    c: Coincident(g140,g139)
    c: Vertical(g140)
    c: Equal(g91,g139) = 4.03
    c: Equal(g92,g140) = 1.9
    c: Coincident(g141,g135)
    c: Vertical(g141)
    c: Vertical(g142)
    c: Coincident(g142,g136)
    c: Equal(g93,g141) = 5.8
    c: Equal(g94,g142) = 5.8
    c: Vertical(g143)
    c: Coincident(g143,g136)
    c: Equal(g95,g143) = 6.9
    c: Coincident(g149,g140)
    c: Equal(g96,g144) = 1
    c: Equal(g144, g145-g148) x4
    c: InternalAlignment(g144-g148 -> g149) x5
    c: InternalAlignment(g150-g158 -> g149) x9
    c: Block(g149)
    c: Block(g159)
    c: Coincident(g168,g141)
    c: Equal(g118,g160) = 1
    c: Equal(g160, g161-g167) x7
    c: Coincident(g168,g143)
    c: InternalAlignment(g160-g167 -> g168) x8
    c: InternalAlignment(g169-g174 -> g168) x6
    c: Coincident(g175,g142)
    c: Block(g168)
    c: Block(g175)
    c: Coincident(g176,g175)
    c: Coincident(g176,g137)
    c: Vertical(g176)
    c: Coincident(g177,g137)
    c: Vertical(g177)
    c: Coincident(g178,g177)
    c: Coincident(g178,g159)
    c: InternalAlignment(g179,g178)
    c: InternalAlignment(g180,g178)
    c: Block(g178)
    c: Vertical(g181)
    c: Coincident(g181,g89)
    c: Block(g5)
    c: Coincident(g182,g1)
    c: Coincident(g182,g5)
    c: Horizontal(g182)
    c: Coincident(g186,g117)
    c: Weight(g183) = 1
    c: Equal(g183,g184)
    c: Equal(g183,g185)
    c: Coincident(g186,g181)
    c: InternalAlignment(g183,g186)
    c: InternalAlignment(g184,g186)
    c: InternalAlignment(g185,g186)
    c: InternalAlignment(g187,g186)
    c: InternalAlignment(g188,g186)
    c: Block(g186)
    c: InternalAlignment(g190,g189)
    c: InternalAlignment(g191,g189)
    c: Block(g189)
    c: InternalAlignment(g193,g192)
    c: InternalAlignment(g194,g192)
    c: Block(g192)
    c: Horizontal(g195)
    c: Block(g195)
    c: Coincident(g196,g195)
    c: Vertical(g196)
    c: Block(g196)
    c: Distance(g195) = 3.71244
    c: Coincident(g197,g196)
    c: Horizontal(g197)
    c: Distance(g197) = 4.1
    c: Coincident(g198,g192)
    c: Coincident(g198,g197)
    c: Vertical(g198)
    c: Block(g198)
    c: Coincident(g199,g192)
    c: Coincident(g199,g195)
    c: Vertical(g199)
    c: Block(g199)
FEATURE [PartDesign::Body] Body
  Group = -> [Sketch083]
  Origin = -> Origin
FEATURE [Sketcher::SketchObject] Sketch084
  FullyConstrained = true
  MapMode = 5
  Support = -> [XY_Plane001]
FEATURE [PartDesign::Body] Body001
  Group = -> [Sketch084]
  Origin = -> Origin001
